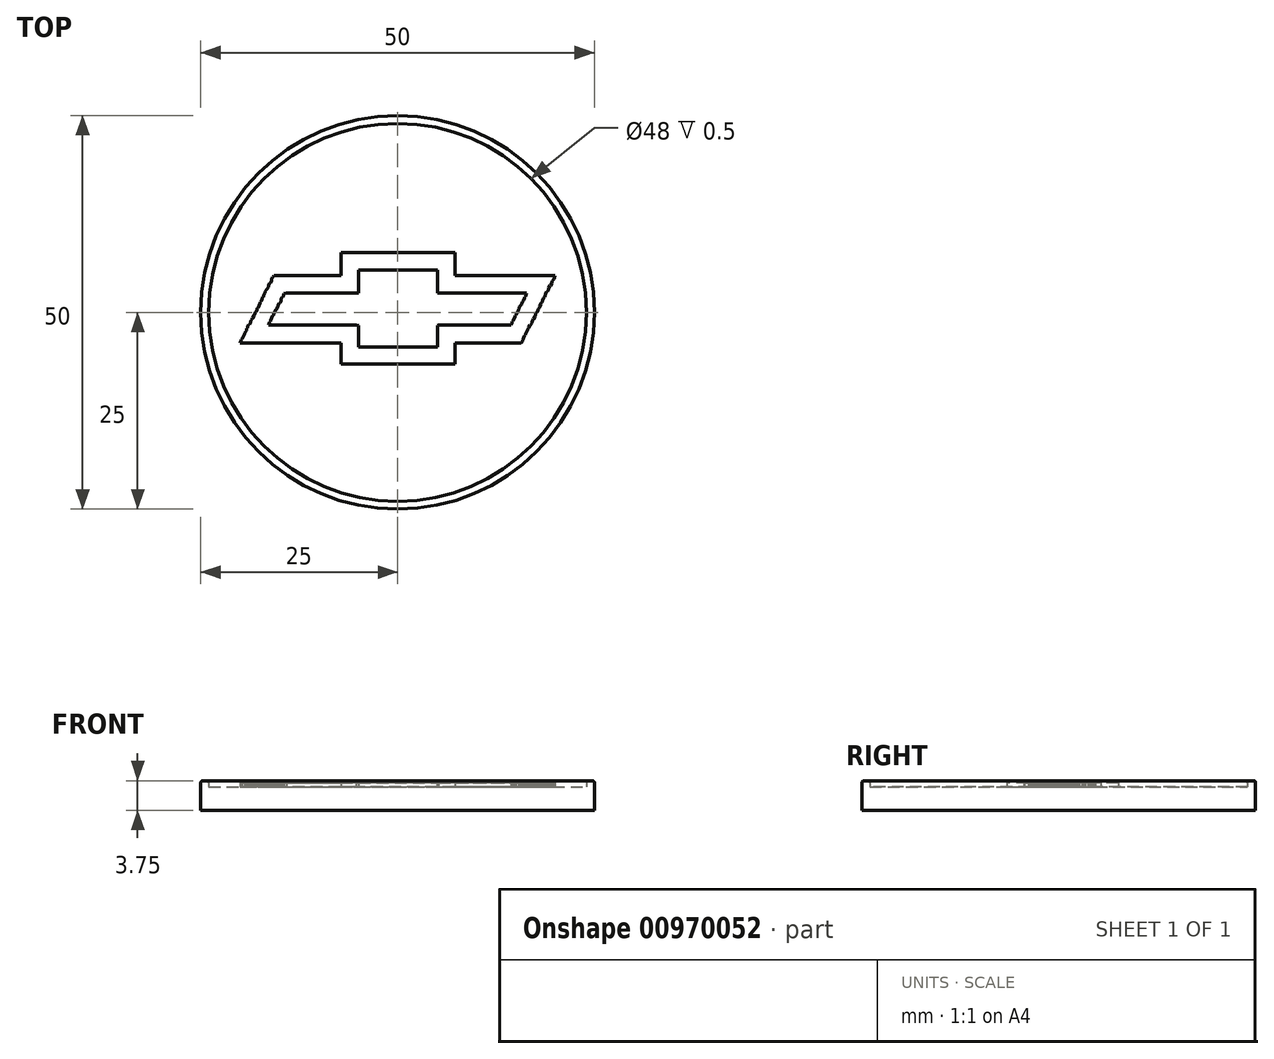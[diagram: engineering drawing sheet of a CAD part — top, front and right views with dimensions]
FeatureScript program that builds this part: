
annotation { "Feature Type Name" : "Feature", "Feature Type Description" : "" }
export const myFeature = defineFeature(function(context is Context, id is Id, definition is map)
    precondition{}
    {
        {
            var Q0;
            Q0=qCreatedBy(makeId("Front.planeOp"),FACE);
            var sketch = newSketch(context, id + "F0", { "sketchPlane" : qUnion([Q0])});
            skLineSegment(sketch, "E0.bottom", {"start": v(0, 0) * mm, "end": v(-25, 0) * mm});
            skLineSegment(sketch, "E0.top", {"start": v(0, 3) * mm, "end": v(-25, 3) * mm});
            skLineSegment(sketch, "E0.left", {"start": v(0, 0) * mm, "end": v(0, 3) * mm});
            skLineSegment(sketch, "E0.right", {"start": v(-25, 0) * mm, "end": v(-25, 3) * mm});
            skLineSegment(sketch, "E1.bottom", {"start": v(-25, 3) * mm, "end": v(-24, 3) * mm});
            skLineSegment(sketch, "E1.top", {"start": v(-25, 3.75) * mm, "end": v(-24, 3.75) * mm});
            skLineSegment(sketch, "E1.left", {"start": v(-25, 3) * mm, "end": v(-25, 3.75) * mm});
            skLineSegment(sketch, "E1.right", {"start": v(-24, 3) * mm, "end": v(-24, 3.75) * mm});
            skSolve(sketch);
        }
        {
            var Q0;
            Q0 = qSketchRegion(id + "F0", true);
            var Q1;
            Q1=sQuery(id+"F0.wireOp",EDGE,"E0.left");
            revolve(context, id + "F1", {"surfaceOperationType" : NewSurfaceOperationType.NEW, "entities" : qUnion([Q0]), "axis" : qUnion([Q1]), "revolveType" : RevolveType.FULL});
        }
        {
            var Q0;
            Q0=qCreatedBy(makeId("Top.planeOp"),FACE);
            cPlane(context, id + "F2", {"entities" : qUnion([Q0]), "cplaneType" : CPlaneType.OFFSET, "offset" : 3 * mm, "width" : 150 * mm, "height" : 150 * mm});
        }
        {
            var Q0;
            Q0=qCreatedBy(id+"F2.planeOp",FACE);
            var sketch = newSketch(context, id + "F3", { "sketchPlane" : qUnion([Q0])});
            skLineSegment(sketch, "E2", {"start": v(-7.2, 7.58) * mm, "end": v(-7.2, 7.38) * mm});
            skLineSegment(sketch, "E3", {"start": v(-7.2, 7.38) * mm, "end": v(-7.2, 7.33) * mm});
            skLineSegment(sketch, "E4", {"start": v(-7.2, 7.33) * mm, "end": v(-7.2, 7.28) * mm});
            skLineSegment(sketch, "E5", {"start": v(-7.2, 7.28) * mm, "end": v(-7.2, 7.23) * mm});
            skLineSegment(sketch, "E6", {"start": v(-7.2, 7.23) * mm, "end": v(-7.2, 7.18) * mm});
            skLineSegment(sketch, "E7", {"start": v(-7.2, 7.18) * mm, "end": v(-7.2, 7.12) * mm});
            skLineSegment(sketch, "E8", {"start": v(-7.2, 7.12) * mm, "end": v(-7.2, 7.08) * mm});
            skLineSegment(sketch, "E9", {"start": v(-7.2, 7.08) * mm, "end": v(-7.2, 7.03) * mm});
            skLineSegment(sketch, "E10", {"start": v(-7.2, 7.03) * mm, "end": v(-7.2, 6.98) * mm});
            skLineSegment(sketch, "E11", {"start": v(-7.2, 6.98) * mm, "end": v(-7.2, 6.93) * mm});
            skLineSegment(sketch, "E12", {"start": v(-7.2, 6.93) * mm, "end": v(-7.2, 6.88) * mm});
            skLineSegment(sketch, "E13", {"start": v(-7.2, 6.88) * mm, "end": v(-7.2, 6.83) * mm});
            skLineSegment(sketch, "E14", {"start": v(-7.2, 6.83) * mm, "end": v(-7.2, 6.77) * mm});
            skLineSegment(sketch, "E15", {"start": v(-7.2, 6.77) * mm, "end": v(-7.2, 6.72) * mm});
            skLineSegment(sketch, "E16", {"start": v(-7.2, 6.72) * mm, "end": v(-7.2, 6.68) * mm});
            skLineSegment(sketch, "E17", {"start": v(-7.2, 6.68) * mm, "end": v(-7.2, 6.62) * mm});
            skLineSegment(sketch, "E18", {"start": v(-7.2, 6.62) * mm, "end": v(-7.2, 6.58) * mm});
            skLineSegment(sketch, "E19", {"start": v(-7.2, 6.58) * mm, "end": v(-7.2, 6.52) * mm});
            skLineSegment(sketch, "E20", {"start": v(-7.2, 6.52) * mm, "end": v(-7.2, 6.47) * mm});
            skLineSegment(sketch, "E21", {"start": v(-7.2, 6.47) * mm, "end": v(-7.2, 6.42) * mm});
            skLineSegment(sketch, "E22", {"start": v(-7.2, 6.42) * mm, "end": v(-7.2, 6.38) * mm});
            skLineSegment(sketch, "E23", {"start": v(-7.2, 6.38) * mm, "end": v(-7.2, 6.33) * mm});
            skLineSegment(sketch, "E24", {"start": v(-7.2, 6.33) * mm, "end": v(-7.2, 6.28) * mm});
            skLineSegment(sketch, "E25", {"start": v(-7.2, 6.28) * mm, "end": v(-7.2, 6.23) * mm});
            skLineSegment(sketch, "E26", {"start": v(-7.2, 6.23) * mm, "end": v(-7.2, 6.17) * mm});
            skLineSegment(sketch, "E27", {"start": v(-7.2, 6.17) * mm, "end": v(-7.2, 6.12) * mm});
            skLineSegment(sketch, "E28", {"start": v(-7.2, 6.12) * mm, "end": v(-7.2, 6.08) * mm});
            skLineSegment(sketch, "E29", {"start": v(-7.2, 6.08) * mm, "end": v(-7.2, 6.03) * mm});
            skLineSegment(sketch, "E30", {"start": v(-7.2, 6.03) * mm, "end": v(-7.2, 5.98) * mm});
            skLineSegment(sketch, "E31", {"start": v(-7.2, 5.98) * mm, "end": v(-7.2, 5.92) * mm});
            skLineSegment(sketch, "E32", {"start": v(-7.2, 5.92) * mm, "end": v(-7.2, 5.88) * mm});
            skLineSegment(sketch, "E33", {"start": v(-7.2, 5.88) * mm, "end": v(-7.2, 5.83) * mm});
            skLineSegment(sketch, "E34", {"start": v(-7.2, 5.83) * mm, "end": v(-7.2, 5.77) * mm});
            skLineSegment(sketch, "E35", {"start": v(-7.2, 5.77) * mm, "end": v(-7.2, 5.72) * mm});
            skLineSegment(sketch, "E36", {"start": v(-7.2, 5.72) * mm, "end": v(-7.2, 5.68) * mm});
            skLineSegment(sketch, "E37", {"start": v(-7.2, 5.68) * mm, "end": v(-7.2, 5.63) * mm});
            skLineSegment(sketch, "E38", {"start": v(-7.2, 5.63) * mm, "end": v(-7.2, 5.58) * mm});
            skLineSegment(sketch, "E39", {"start": v(-7.2, 5.58) * mm, "end": v(-7.2, 5.53) * mm});
            skLineSegment(sketch, "E40", {"start": v(-7.2, 5.53) * mm, "end": v(-7.2, 5.48) * mm});
            skLineSegment(sketch, "E41", {"start": v(-7.2, 5.48) * mm, "end": v(-7.2, 5.42) * mm});
            skLineSegment(sketch, "E42", {"start": v(-7.2, 5.42) * mm, "end": v(-7.2, 5.38) * mm});
            skLineSegment(sketch, "E43", {"start": v(-7.2, 5.38) * mm, "end": v(-7.2, 5.33) * mm});
            skLineSegment(sketch, "E44", {"start": v(-7.2, 5.33) * mm, "end": v(-7.2, 5.28) * mm});
            skLineSegment(sketch, "E45", {"start": v(-7.2, 5.28) * mm, "end": v(-7.2, 5.23) * mm});
            skLineSegment(sketch, "E46", {"start": v(-7.2, 5.23) * mm, "end": v(-7.2, 5.17) * mm});
            skLineSegment(sketch, "E47", {"start": v(-7.2, 5.17) * mm, "end": v(-7.2, 5.12) * mm});
            skLineSegment(sketch, "E48", {"start": v(-7.2, 5.12) * mm, "end": v(-7.2, 5.08) * mm});
            skLineSegment(sketch, "E49", {"start": v(-7.2, 5.08) * mm, "end": v(-7.2, 5.03) * mm});
            skLineSegment(sketch, "E50", {"start": v(-7.2, 5.03) * mm, "end": v(-7.2, 4.68) * mm});
            skLineSegment(sketch, "E51", {"start": v(-7.2, 4.68) * mm, "end": v(-7.4, 4.68) * mm});
            skLineSegment(sketch, "E52", {"start": v(-7.4, 4.68) * mm, "end": v(-7.45, 4.68) * mm});
            skLineSegment(sketch, "E53", {"start": v(-7.45, 4.68) * mm, "end": v(-7.5, 4.68) * mm});
            skLineSegment(sketch, "E54", {"start": v(-7.5, 4.68) * mm, "end": v(-7.55, 4.68) * mm});
            skLineSegment(sketch, "E55", {"start": v(-7.55, 4.68) * mm, "end": v(-7.6, 4.68) * mm});
            skLineSegment(sketch, "E56", {"start": v(-7.6, 4.68) * mm, "end": v(-7.65, 4.68) * mm});
            skLineSegment(sketch, "E57", {"start": v(-7.65, 4.68) * mm, "end": v(-7.7, 4.68) * mm});
            skLineSegment(sketch, "E58", {"start": v(-7.7, 4.68) * mm, "end": v(-7.75, 4.68) * mm});
            skLineSegment(sketch, "E59", {"start": v(-7.75, 4.68) * mm, "end": v(-7.8, 4.68) * mm});
            skLineSegment(sketch, "E60", {"start": v(-7.8, 4.68) * mm, "end": v(-7.85, 4.68) * mm});
            skLineSegment(sketch, "E61", {"start": v(-7.85, 4.68) * mm, "end": v(-7.9, 4.68) * mm});
            skLineSegment(sketch, "E62", {"start": v(-7.9, 4.68) * mm, "end": v(-7.95, 4.68) * mm});
            skLineSegment(sketch, "E63", {"start": v(-7.95, 4.68) * mm, "end": v(-8, 4.68) * mm});
            skLineSegment(sketch, "E64", {"start": v(-8, 4.68) * mm, "end": v(-8.05, 4.68) * mm});
            skLineSegment(sketch, "E65", {"start": v(-8.05, 4.68) * mm, "end": v(-8.1, 4.68) * mm});
            skLineSegment(sketch, "E66", {"start": v(-8.1, 4.68) * mm, "end": v(-8.15, 4.68) * mm});
            skLineSegment(sketch, "E67", {"start": v(-8.15, 4.68) * mm, "end": v(-8.2, 4.68) * mm});
            skLineSegment(sketch, "E68", {"start": v(-8.2, 4.68) * mm, "end": v(-8.25, 4.68) * mm});
            skLineSegment(sketch, "E69", {"start": v(-8.25, 4.68) * mm, "end": v(-8.3, 4.68) * mm});
            skLineSegment(sketch, "E70", {"start": v(-8.3, 4.68) * mm, "end": v(-8.35, 4.68) * mm});
            skLineSegment(sketch, "E71", {"start": v(-8.35, 4.68) * mm, "end": v(-8.4, 4.68) * mm});
            skLineSegment(sketch, "E72", {"start": v(-8.4, 4.68) * mm, "end": v(-8.45, 4.68) * mm});
            skLineSegment(sketch, "E73", {"start": v(-8.45, 4.68) * mm, "end": v(-8.5, 4.68) * mm});
            skLineSegment(sketch, "E74", {"start": v(-8.5, 4.68) * mm, "end": v(-8.55, 4.68) * mm});
            skLineSegment(sketch, "E75", {"start": v(-8.55, 4.68) * mm, "end": v(-8.6, 4.68) * mm});
            skLineSegment(sketch, "E76", {"start": v(-8.6, 4.68) * mm, "end": v(-8.65, 4.68) * mm});
            skLineSegment(sketch, "E77", {"start": v(-8.65, 4.68) * mm, "end": v(-8.7, 4.68) * mm});
            skLineSegment(sketch, "E78", {"start": v(-8.7, 4.68) * mm, "end": v(-8.75, 4.68) * mm});
            skLineSegment(sketch, "E79", {"start": v(-8.75, 4.68) * mm, "end": v(-8.8, 4.68) * mm});
            skLineSegment(sketch, "E80", {"start": v(-8.8, 4.68) * mm, "end": v(-8.85, 4.68) * mm});
            skLineSegment(sketch, "E81", {"start": v(-8.85, 4.68) * mm, "end": v(-8.9, 4.68) * mm});
            skLineSegment(sketch, "E82", {"start": v(-8.9, 4.68) * mm, "end": v(-8.95, 4.68) * mm});
            skLineSegment(sketch, "E83", {"start": v(-8.95, 4.68) * mm, "end": v(-9, 4.68) * mm});
            skLineSegment(sketch, "E84", {"start": v(-9, 4.68) * mm, "end": v(-9.05, 4.68) * mm});
            skLineSegment(sketch, "E85", {"start": v(-9.05, 4.68) * mm, "end": v(-9.1, 4.68) * mm});
            skLineSegment(sketch, "E86", {"start": v(-9.1, 4.68) * mm, "end": v(-9.15, 4.68) * mm});
            skLineSegment(sketch, "E87", {"start": v(-9.15, 4.68) * mm, "end": v(-9.2, 4.68) * mm});
            skLineSegment(sketch, "E88", {"start": v(-9.2, 4.68) * mm, "end": v(-9.25, 4.68) * mm});
            skLineSegment(sketch, "E89", {"start": v(-9.25, 4.68) * mm, "end": v(-9.3, 4.68) * mm});
            skLineSegment(sketch, "E90", {"start": v(-9.3, 4.68) * mm, "end": v(-9.35, 4.68) * mm});
            skLineSegment(sketch, "E91", {"start": v(-9.35, 4.68) * mm, "end": v(-9.4, 4.68) * mm});
            skLineSegment(sketch, "E92", {"start": v(-9.4, 4.68) * mm, "end": v(-9.45, 4.68) * mm});
            skLineSegment(sketch, "E93", {"start": v(-9.45, 4.68) * mm, "end": v(-9.5, 4.68) * mm});
            skLineSegment(sketch, "E94", {"start": v(-9.5, 4.68) * mm, "end": v(-9.55, 4.68) * mm});
            skLineSegment(sketch, "E95", {"start": v(-9.55, 4.68) * mm, "end": v(-9.6, 4.68) * mm});
            skLineSegment(sketch, "E96", {"start": v(-9.6, 4.68) * mm, "end": v(-9.65, 4.68) * mm});
            skLineSegment(sketch, "E97", {"start": v(-9.65, 4.68) * mm, "end": v(-9.7, 4.68) * mm});
            skLineSegment(sketch, "E98", {"start": v(-9.7, 4.68) * mm, "end": v(-9.75, 4.68) * mm});
            skLineSegment(sketch, "E99", {"start": v(-9.75, 4.68) * mm, "end": v(-9.8, 4.68) * mm});
            skLineSegment(sketch, "E100", {"start": v(-9.8, 4.68) * mm, "end": v(-9.85, 4.68) * mm});
            skLineSegment(sketch, "E101", {"start": v(-9.85, 4.68) * mm, "end": v(-9.9, 4.68) * mm});
            skLineSegment(sketch, "E102", {"start": v(-9.9, 4.68) * mm, "end": v(-9.95, 4.68) * mm});
            skLineSegment(sketch, "E103", {"start": v(-9.95, 4.68) * mm, "end": v(-10, 4.68) * mm});
            skLineSegment(sketch, "E104", {"start": v(-10, 4.68) * mm, "end": v(-10.05, 4.68) * mm});
            skLineSegment(sketch, "E105", {"start": v(-10.05, 4.68) * mm, "end": v(-10.1, 4.68) * mm});
            skLineSegment(sketch, "E106", {"start": v(-10.1, 4.68) * mm, "end": v(-10.15, 4.68) * mm});
            skLineSegment(sketch, "E107", {"start": v(-10.15, 4.68) * mm, "end": v(-10.2, 4.68) * mm});
            skLineSegment(sketch, "E108", {"start": v(-10.2, 4.68) * mm, "end": v(-10.25, 4.68) * mm});
            skLineSegment(sketch, "E109", {"start": v(-10.25, 4.68) * mm, "end": v(-10.3, 4.68) * mm});
            skLineSegment(sketch, "E110", {"start": v(-10.3, 4.68) * mm, "end": v(-10.35, 4.68) * mm});
            skLineSegment(sketch, "E111", {"start": v(-10.35, 4.68) * mm, "end": v(-10.4, 4.68) * mm});
            skLineSegment(sketch, "E112", {"start": v(-10.4, 4.68) * mm, "end": v(-10.45, 4.68) * mm});
            skLineSegment(sketch, "E113", {"start": v(-10.45, 4.68) * mm, "end": v(-10.5, 4.68) * mm});
            skLineSegment(sketch, "E114", {"start": v(-10.5, 4.68) * mm, "end": v(-10.55, 4.68) * mm});
            skLineSegment(sketch, "E115", {"start": v(-10.55, 4.68) * mm, "end": v(-10.6, 4.68) * mm});
            skLineSegment(sketch, "E116", {"start": v(-10.6, 4.68) * mm, "end": v(-10.65, 4.68) * mm});
            skLineSegment(sketch, "E117", {"start": v(-10.65, 4.68) * mm, "end": v(-10.7, 4.68) * mm});
            skLineSegment(sketch, "E118", {"start": v(-10.7, 4.68) * mm, "end": v(-10.75, 4.68) * mm});
            skLineSegment(sketch, "E119", {"start": v(-10.75, 4.68) * mm, "end": v(-10.8, 4.68) * mm});
            skLineSegment(sketch, "E120", {"start": v(-10.8, 4.68) * mm, "end": v(-10.85, 4.68) * mm});
            skLineSegment(sketch, "E121", {"start": v(-10.85, 4.68) * mm, "end": v(-10.9, 4.68) * mm});
            skLineSegment(sketch, "E122", {"start": v(-10.9, 4.68) * mm, "end": v(-10.95, 4.68) * mm});
            skLineSegment(sketch, "E123", {"start": v(-10.95, 4.68) * mm, "end": v(-11, 4.68) * mm});
            skLineSegment(sketch, "E124", {"start": v(-11, 4.68) * mm, "end": v(-11.05, 4.68) * mm});
            skLineSegment(sketch, "E125", {"start": v(-11.05, 4.68) * mm, "end": v(-11.1, 4.68) * mm});
            skLineSegment(sketch, "E126", {"start": v(-11.1, 4.68) * mm, "end": v(-11.15, 4.68) * mm});
            skLineSegment(sketch, "E127", {"start": v(-11.15, 4.68) * mm, "end": v(-11.2, 4.68) * mm});
            skLineSegment(sketch, "E128", {"start": v(-11.2, 4.68) * mm, "end": v(-11.25, 4.68) * mm});
            skLineSegment(sketch, "E129", {"start": v(-11.25, 4.68) * mm, "end": v(-11.3, 4.68) * mm});
            skLineSegment(sketch, "E130", {"start": v(-11.3, 4.68) * mm, "end": v(-11.35, 4.68) * mm});
            skLineSegment(sketch, "E131", {"start": v(-11.35, 4.68) * mm, "end": v(-11.4, 4.68) * mm});
            skLineSegment(sketch, "E132", {"start": v(-11.4, 4.68) * mm, "end": v(-11.45, 4.68) * mm});
            skLineSegment(sketch, "E133", {"start": v(-11.45, 4.68) * mm, "end": v(-11.5, 4.68) * mm});
            skLineSegment(sketch, "E134", {"start": v(-11.5, 4.68) * mm, "end": v(-11.55, 4.68) * mm});
            skLineSegment(sketch, "E135", {"start": v(-11.55, 4.68) * mm, "end": v(-11.6, 4.68) * mm});
            skLineSegment(sketch, "E136", {"start": v(-11.6, 4.68) * mm, "end": v(-11.65, 4.68) * mm});
            skLineSegment(sketch, "E137", {"start": v(-11.65, 4.68) * mm, "end": v(-11.7, 4.68) * mm});
            skLineSegment(sketch, "E138", {"start": v(-11.7, 4.68) * mm, "end": v(-11.75, 4.68) * mm});
            skLineSegment(sketch, "E139", {"start": v(-11.75, 4.68) * mm, "end": v(-11.8, 4.68) * mm});
            skLineSegment(sketch, "E140", {"start": v(-11.8, 4.68) * mm, "end": v(-11.85, 4.68) * mm});
            skLineSegment(sketch, "E141", {"start": v(-11.85, 4.68) * mm, "end": v(-11.9, 4.68) * mm});
            skLineSegment(sketch, "E142", {"start": v(-11.9, 4.68) * mm, "end": v(-11.95, 4.68) * mm});
            skLineSegment(sketch, "E143", {"start": v(-11.95, 4.68) * mm, "end": v(-12, 4.68) * mm});
            skLineSegment(sketch, "E144", {"start": v(-12, 4.68) * mm, "end": v(-12.05, 4.68) * mm});
            skLineSegment(sketch, "E145", {"start": v(-12.05, 4.68) * mm, "end": v(-12.1, 4.68) * mm});
            skLineSegment(sketch, "E146", {"start": v(-12.1, 4.68) * mm, "end": v(-12.15, 4.68) * mm});
            skLineSegment(sketch, "E147", {"start": v(-12.15, 4.68) * mm, "end": v(-12.2, 4.68) * mm});
            skLineSegment(sketch, "E148", {"start": v(-12.2, 4.68) * mm, "end": v(-12.25, 4.68) * mm});
            skLineSegment(sketch, "E149", {"start": v(-12.25, 4.68) * mm, "end": v(-12.3, 4.68) * mm});
            skLineSegment(sketch, "E150", {"start": v(-12.3, 4.68) * mm, "end": v(-12.35, 4.68) * mm});
            skLineSegment(sketch, "E151", {"start": v(-12.35, 4.68) * mm, "end": v(-12.4, 4.68) * mm});
            skLineSegment(sketch, "E152", {"start": v(-12.4, 4.68) * mm, "end": v(-12.45, 4.68) * mm});
            skLineSegment(sketch, "E153", {"start": v(-12.45, 4.68) * mm, "end": v(-12.5, 4.68) * mm});
            skLineSegment(sketch, "E154", {"start": v(-12.5, 4.68) * mm, "end": v(-12.55, 4.68) * mm});
            skLineSegment(sketch, "E155", {"start": v(-12.55, 4.68) * mm, "end": v(-12.6, 4.68) * mm});
            skLineSegment(sketch, "E156", {"start": v(-12.6, 4.68) * mm, "end": v(-12.65, 4.68) * mm});
            skLineSegment(sketch, "E157", {"start": v(-12.65, 4.68) * mm, "end": v(-12.7, 4.68) * mm});
            skLineSegment(sketch, "E158", {"start": v(-12.7, 4.68) * mm, "end": v(-12.75, 4.68) * mm});
            skLineSegment(sketch, "E159", {"start": v(-12.75, 4.68) * mm, "end": v(-12.8, 4.68) * mm});
            skLineSegment(sketch, "E160", {"start": v(-12.8, 4.68) * mm, "end": v(-12.85, 4.68) * mm});
            skLineSegment(sketch, "E161", {"start": v(-12.85, 4.68) * mm, "end": v(-12.9, 4.68) * mm});
            skLineSegment(sketch, "E162", {"start": v(-12.9, 4.68) * mm, "end": v(-12.95, 4.68) * mm});
            skLineSegment(sketch, "E163", {"start": v(-12.95, 4.68) * mm, "end": v(-13, 4.68) * mm});
            skLineSegment(sketch, "E164", {"start": v(-13, 4.68) * mm, "end": v(-13.05, 4.68) * mm});
            skLineSegment(sketch, "E165", {"start": v(-13.05, 4.68) * mm, "end": v(-13.1, 4.68) * mm});
            skLineSegment(sketch, "E166", {"start": v(-13.1, 4.68) * mm, "end": v(-13.15, 4.68) * mm});
            skLineSegment(sketch, "E167", {"start": v(-13.15, 4.68) * mm, "end": v(-13.2, 4.68) * mm});
            skLineSegment(sketch, "E168", {"start": v(-13.2, 4.68) * mm, "end": v(-13.25, 4.68) * mm});
            skLineSegment(sketch, "E169", {"start": v(-13.25, 4.68) * mm, "end": v(-13.3, 4.68) * mm});
            skLineSegment(sketch, "E170", {"start": v(-13.3, 4.68) * mm, "end": v(-13.35, 4.68) * mm});
            skLineSegment(sketch, "E171", {"start": v(-13.35, 4.68) * mm, "end": v(-13.4, 4.68) * mm});
            skLineSegment(sketch, "E172", {"start": v(-13.4, 4.68) * mm, "end": v(-13.45, 4.68) * mm});
            skLineSegment(sketch, "E173", {"start": v(-13.45, 4.68) * mm, "end": v(-13.5, 4.68) * mm});
            skLineSegment(sketch, "E174", {"start": v(-13.5, 4.68) * mm, "end": v(-13.55, 4.68) * mm});
            skLineSegment(sketch, "E175", {"start": v(-13.55, 4.68) * mm, "end": v(-13.6, 4.68) * mm});
            skLineSegment(sketch, "E176", {"start": v(-13.6, 4.68) * mm, "end": v(-13.65, 4.68) * mm});
            skLineSegment(sketch, "E177", {"start": v(-13.65, 4.68) * mm, "end": v(-13.7, 4.68) * mm});
            skLineSegment(sketch, "E178", {"start": v(-13.7, 4.68) * mm, "end": v(-13.75, 4.68) * mm});
            skLineSegment(sketch, "E179", {"start": v(-13.75, 4.68) * mm, "end": v(-13.8, 4.68) * mm});
            skLineSegment(sketch, "E180", {"start": v(-13.8, 4.68) * mm, "end": v(-13.85, 4.68) * mm});
            skLineSegment(sketch, "E181", {"start": v(-13.85, 4.68) * mm, "end": v(-13.9, 4.68) * mm});
            skLineSegment(sketch, "E182", {"start": v(-13.9, 4.68) * mm, "end": v(-13.95, 4.68) * mm});
            skLineSegment(sketch, "E183", {"start": v(-13.95, 4.68) * mm, "end": v(-14, 4.68) * mm});
            skLineSegment(sketch, "E184", {"start": v(-14, 4.68) * mm, "end": v(-14.05, 4.68) * mm});
            skLineSegment(sketch, "E185", {"start": v(-14.05, 4.68) * mm, "end": v(-14.1, 4.68) * mm});
            skLineSegment(sketch, "E186", {"start": v(-14.1, 4.68) * mm, "end": v(-14.15, 4.68) * mm});
            skLineSegment(sketch, "E187", {"start": v(-14.15, 4.68) * mm, "end": v(-14.2, 4.68) * mm});
            skLineSegment(sketch, "E188", {"start": v(-14.2, 4.68) * mm, "end": v(-14.25, 4.68) * mm});
            skLineSegment(sketch, "E189", {"start": v(-14.25, 4.68) * mm, "end": v(-14.3, 4.68) * mm});
            skLineSegment(sketch, "E190", {"start": v(-14.3, 4.68) * mm, "end": v(-14.35, 4.68) * mm});
            skLineSegment(sketch, "E191", {"start": v(-14.35, 4.68) * mm, "end": v(-14.4, 4.68) * mm});
            skLineSegment(sketch, "E192", {"start": v(-14.4, 4.68) * mm, "end": v(-14.45, 4.68) * mm});
            skLineSegment(sketch, "E193", {"start": v(-14.45, 4.68) * mm, "end": v(-14.5, 4.68) * mm});
            skLineSegment(sketch, "E194", {"start": v(-14.5, 4.68) * mm, "end": v(-14.55, 4.68) * mm});
            skLineSegment(sketch, "E195", {"start": v(-14.55, 4.68) * mm, "end": v(-14.6, 4.68) * mm});
            skLineSegment(sketch, "E196", {"start": v(-14.6, 4.68) * mm, "end": v(-14.65, 4.68) * mm});
            skLineSegment(sketch, "E197", {"start": v(-14.65, 4.68) * mm, "end": v(-14.7, 4.68) * mm});
            skLineSegment(sketch, "E198", {"start": v(-14.7, 4.68) * mm, "end": v(-14.75, 4.68) * mm});
            skLineSegment(sketch, "E199", {"start": v(-14.75, 4.68) * mm, "end": v(-14.8, 4.68) * mm});
            skLineSegment(sketch, "E200", {"start": v(-14.8, 4.68) * mm, "end": v(-14.85, 4.68) * mm});
            skLineSegment(sketch, "E201", {"start": v(-14.85, 4.68) * mm, "end": v(-14.9, 4.68) * mm});
            skLineSegment(sketch, "E202", {"start": v(-14.9, 4.68) * mm, "end": v(-14.95, 4.68) * mm});
            skLineSegment(sketch, "E203", {"start": v(-14.95, 4.68) * mm, "end": v(-15, 4.68) * mm});
            skLineSegment(sketch, "E204", {"start": v(-15, 4.68) * mm, "end": v(-15.05, 4.68) * mm});
            skLineSegment(sketch, "E205", {"start": v(-15.05, 4.68) * mm, "end": v(-15.1, 4.68) * mm});
            skLineSegment(sketch, "E206", {"start": v(-15.1, 4.68) * mm, "end": v(-15.15, 4.68) * mm});
            skLineSegment(sketch, "E207", {"start": v(-15.15, 4.68) * mm, "end": v(-15.2, 4.68) * mm});
            skLineSegment(sketch, "E208", {"start": v(-15.2, 4.68) * mm, "end": v(-15.25, 4.68) * mm});
            skLineSegment(sketch, "E209", {"start": v(-15.25, 4.68) * mm, "end": v(-15.3, 4.68) * mm});
            skLineSegment(sketch, "E210", {"start": v(-15.3, 4.68) * mm, "end": v(-15.35, 4.68) * mm});
            skLineSegment(sketch, "E211", {"start": v(-15.35, 4.68) * mm, "end": v(-15.7, 4.68) * mm});
            skLineSegment(sketch, "E212", {"start": v(-15.7, 4.68) * mm, "end": v(-15.75, 4.52) * mm});
            skLineSegment(sketch, "E213", {"start": v(-15.75, 4.53) * mm, "end": v(-15.85, 4.48) * mm});
            skLineSegment(sketch, "E214", {"start": v(-15.85, 4.48) * mm, "end": v(-16, 4.22) * mm});
            skLineSegment(sketch, "E215", {"start": v(-16, 4.22) * mm, "end": v(-16, 4.03) * mm});
            skLineSegment(sketch, "E216", {"start": v(-16, 4.03) * mm, "end": v(-16.15, 3.73) * mm});
            skLineSegment(sketch, "E217", {"start": v(-16.15, 3.73) * mm, "end": v(-16.25, 3.73) * mm});
            skLineSegment(sketch, "E218", {"start": v(-16.25, 3.73) * mm, "end": v(-16.4, 3.43) * mm});
            skLineSegment(sketch, "E219", {"start": v(-16.4, 3.43) * mm, "end": v(-16.4, 3.23) * mm});
            skLineSegment(sketch, "E220", {"start": v(-16.4, 3.23) * mm, "end": v(-16.65, 2.93) * mm});
            skLineSegment(sketch, "E221", {"start": v(-16.65, 2.93) * mm, "end": v(-16.8, 2.62) * mm});
            skLineSegment(sketch, "E222", {"start": v(-16.8, 2.63) * mm, "end": v(-16.8, 2.48) * mm});
            skLineSegment(sketch, "E223", {"start": v(-16.8, 2.48) * mm, "end": v(-16.9, 2.43) * mm});
            skLineSegment(sketch, "E224", {"start": v(-16.9, 2.43) * mm, "end": v(-17.05, 2.12) * mm});
            skLineSegment(sketch, "E225", {"start": v(-17.05, 2.13) * mm, "end": v(-17.05, 1.98) * mm});
            skLineSegment(sketch, "E226", {"start": v(-17.05, 1.98) * mm, "end": v(-17.15, 1.93) * mm});
            skLineSegment(sketch, "E227", {"start": v(-17.15, 1.93) * mm, "end": v(-17.2, 1.67) * mm});
            skLineSegment(sketch, "E228", {"start": v(-17.2, 1.68) * mm, "end": v(-17.35, 1.38) * mm});
            skLineSegment(sketch, "E229", {"start": v(-17.35, 1.38) * mm, "end": v(-17.45, 1.33) * mm});
            skLineSegment(sketch, "E230", {"start": v(-17.45, 1.33) * mm, "end": v(-17.45, 1.18) * mm});
            skLineSegment(sketch, "E231", {"start": v(-17.45, 1.18) * mm, "end": v(-17.6, 0.88) * mm});
            skLineSegment(sketch, "E232", {"start": v(-17.6, 0.88) * mm, "end": v(-17.75, 0.57) * mm});
            skLineSegment(sketch, "E233", {"start": v(-17.75, 0.58) * mm, "end": v(-17.85, 0.53) * mm});
            skLineSegment(sketch, "E234", {"start": v(-17.85, 0.53) * mm, "end": v(-17.85, 0.38) * mm});
            skLineSegment(sketch, "E235", {"start": v(-17.85, 0.38) * mm, "end": v(-18, 0.07) * mm});
            skLineSegment(sketch, "E236", {"start": v(-18, 0.08) * mm, "end": v(-18.1, 0.08) * mm});
            skLineSegment(sketch, "E237", {"start": v(-18.1, 0.08) * mm, "end": v(-18.1, -0.07) * mm});
            skLineSegment(sketch, "E238", {"start": v(-18.1, -0.07) * mm, "end": v(-18.25, -0.43) * mm});
            skLineSegment(sketch, "E239", {"start": v(-18.25, -0.42) * mm, "end": v(-18.4, -0.73) * mm});
            skLineSegment(sketch, "E240", {"start": v(-18.4, -0.72) * mm, "end": v(-18.5, -0.72) * mm});
            skLineSegment(sketch, "E241", {"start": v(-18.5, -0.72) * mm, "end": v(-18.5, -0.87) * mm});
            skLineSegment(sketch, "E242", {"start": v(-18.5, -0.87) * mm, "end": v(-18.6, -0.97) * mm});
            skLineSegment(sketch, "E243", {"start": v(-18.6, -0.97) * mm, "end": v(-18.6, -1.07) * mm});
            skLineSegment(sketch, "E244", {"start": v(-18.6, -1.07) * mm, "end": v(-18.65, -1.07) * mm});
            skLineSegment(sketch, "E245", {"start": v(-18.65, -1.07) * mm, "end": v(-18.65, -1.17) * mm});
            skLineSegment(sketch, "E246", {"start": v(-18.65, -1.17) * mm, "end": v(-18.7, -1.17) * mm});
            skLineSegment(sketch, "E247", {"start": v(-18.7, -1.17) * mm, "end": v(-18.7, -1.27) * mm});
            skLineSegment(sketch, "E248", {"start": v(-18.7, -1.27) * mm, "end": v(-18.8, -1.52) * mm});
            skLineSegment(sketch, "E249", {"start": v(-18.8, -1.52) * mm, "end": v(-18.9, -1.52) * mm});
            skLineSegment(sketch, "E250", {"start": v(-18.9, -1.52) * mm, "end": v(-19.05, -1.82) * mm});
            skLineSegment(sketch, "E251", {"start": v(-19.05, -1.82) * mm, "end": v(-19.05, -1.97) * mm});
            skLineSegment(sketch, "E252", {"start": v(-19.05, -1.97) * mm, "end": v(-19.15, -2.03) * mm});
            skLineSegment(sketch, "E253", {"start": v(-19.15, -2.02) * mm, "end": v(-19.2, -2.32) * mm});
            skLineSegment(sketch, "E254", {"start": v(-19.2, -2.32) * mm, "end": v(-19.35, -2.57) * mm});
            skLineSegment(sketch, "E255", {"start": v(-19.35, -2.57) * mm, "end": v(-19.45, -2.62) * mm});
            skLineSegment(sketch, "E256", {"start": v(-19.45, -2.62) * mm, "end": v(-19.45, -2.77) * mm});
            skLineSegment(sketch, "E257", {"start": v(-19.45, -2.77) * mm, "end": v(-19.6, -3.07) * mm});
            skLineSegment(sketch, "E258", {"start": v(-19.6, -3.07) * mm, "end": v(-19.75, -3.37) * mm});
            skLineSegment(sketch, "E259", {"start": v(-19.75, -3.37) * mm, "end": v(-19.85, -3.42) * mm});
            skLineSegment(sketch, "E260", {"start": v(-19.85, -3.42) * mm, "end": v(-19.85, -3.57) * mm});
            skLineSegment(sketch, "E261", {"start": v(-19.85, -3.57) * mm, "end": v(-20, -3.87) * mm});
            skLineSegment(sketch, "E262", {"start": v(-20, -3.87) * mm, "end": v(-19.8, -3.87) * mm});
            skLineSegment(sketch, "E263", {"start": v(-19.8, -3.87) * mm, "end": v(-19.75, -3.87) * mm});
            skLineSegment(sketch, "E264", {"start": v(-19.75, -3.87) * mm, "end": v(-19.7, -3.87) * mm});
            skLineSegment(sketch, "E265", {"start": v(-19.7, -3.87) * mm, "end": v(-19.65, -3.87) * mm});
            skLineSegment(sketch, "E266", {"start": v(-19.65, -3.87) * mm, "end": v(-19.6, -3.87) * mm});
            skLineSegment(sketch, "E267", {"start": v(-19.6, -3.87) * mm, "end": v(-19.55, -3.87) * mm});
            skLineSegment(sketch, "E268", {"start": v(-19.55, -3.87) * mm, "end": v(-19.5, -3.87) * mm});
            skLineSegment(sketch, "E269", {"start": v(-19.5, -3.87) * mm, "end": v(-19.45, -3.87) * mm});
            skLineSegment(sketch, "E270", {"start": v(-19.45, -3.87) * mm, "end": v(-19.4, -3.87) * mm});
            skLineSegment(sketch, "E271", {"start": v(-19.4, -3.87) * mm, "end": v(-19.35, -3.87) * mm});
            skLineSegment(sketch, "E272", {"start": v(-19.35, -3.87) * mm, "end": v(-19.3, -3.87) * mm});
            skLineSegment(sketch, "E273", {"start": v(-19.3, -3.87) * mm, "end": v(-19.25, -3.87) * mm});
            skLineSegment(sketch, "E274", {"start": v(-19.25, -3.87) * mm, "end": v(-19.2, -3.87) * mm});
            skLineSegment(sketch, "E275", {"start": v(-19.2, -3.87) * mm, "end": v(-19.15, -3.87) * mm});
            skLineSegment(sketch, "E276", {"start": v(-19.15, -3.87) * mm, "end": v(-19.1, -3.87) * mm});
            skLineSegment(sketch, "E277", {"start": v(-19.1, -3.87) * mm, "end": v(-19.05, -3.87) * mm});
            skLineSegment(sketch, "E278", {"start": v(-19.05, -3.87) * mm, "end": v(-19, -3.87) * mm});
            skLineSegment(sketch, "E279", {"start": v(-19, -3.87) * mm, "end": v(-18.95, -3.87) * mm});
            skLineSegment(sketch, "E280", {"start": v(-18.95, -3.87) * mm, "end": v(-18.9, -3.87) * mm});
            skLineSegment(sketch, "E281", {"start": v(-18.9, -3.87) * mm, "end": v(-18.85, -3.87) * mm});
            skLineSegment(sketch, "E282", {"start": v(-18.85, -3.87) * mm, "end": v(-18.8, -3.87) * mm});
            skLineSegment(sketch, "E283", {"start": v(-18.8, -3.87) * mm, "end": v(-18.75, -3.87) * mm});
            skLineSegment(sketch, "E284", {"start": v(-18.75, -3.87) * mm, "end": v(-18.7, -3.87) * mm});
            skLineSegment(sketch, "E285", {"start": v(-18.7, -3.87) * mm, "end": v(-18.65, -3.87) * mm});
            skLineSegment(sketch, "E286", {"start": v(-18.65, -3.87) * mm, "end": v(-18.6, -3.87) * mm});
            skLineSegment(sketch, "E287", {"start": v(-18.6, -3.87) * mm, "end": v(-18.55, -3.87) * mm});
            skLineSegment(sketch, "E288", {"start": v(-18.55, -3.87) * mm, "end": v(-18.5, -3.87) * mm});
            skLineSegment(sketch, "E289", {"start": v(-18.5, -3.87) * mm, "end": v(-18.45, -3.87) * mm});
            skLineSegment(sketch, "E290", {"start": v(-18.45, -3.87) * mm, "end": v(-18.4, -3.87) * mm});
            skLineSegment(sketch, "E291", {"start": v(-18.4, -3.87) * mm, "end": v(-18.35, -3.87) * mm});
            skLineSegment(sketch, "E292", {"start": v(-18.35, -3.87) * mm, "end": v(-18.3, -3.87) * mm});
            skLineSegment(sketch, "E293", {"start": v(-18.3, -3.87) * mm, "end": v(-18.25, -3.87) * mm});
            skLineSegment(sketch, "E294", {"start": v(-18.25, -3.87) * mm, "end": v(-18.2, -3.87) * mm});
            skLineSegment(sketch, "E295", {"start": v(-18.2, -3.87) * mm, "end": v(-18.15, -3.87) * mm});
            skLineSegment(sketch, "E296", {"start": v(-18.15, -3.87) * mm, "end": v(-18.1, -3.87) * mm});
            skLineSegment(sketch, "E297", {"start": v(-18.1, -3.87) * mm, "end": v(-18.05, -3.87) * mm});
            skLineSegment(sketch, "E298", {"start": v(-18.05, -3.87) * mm, "end": v(-18, -3.87) * mm});
            skLineSegment(sketch, "E299", {"start": v(-18, -3.87) * mm, "end": v(-17.95, -3.87) * mm});
            skLineSegment(sketch, "E300", {"start": v(-17.95, -3.87) * mm, "end": v(-17.9, -3.87) * mm});
            skLineSegment(sketch, "E301", {"start": v(-17.9, -3.87) * mm, "end": v(-17.85, -3.87) * mm});
            skLineSegment(sketch, "E302", {"start": v(-17.85, -3.87) * mm, "end": v(-17.8, -3.87) * mm});
            skLineSegment(sketch, "E303", {"start": v(-17.8, -3.87) * mm, "end": v(-17.75, -3.87) * mm});
            skLineSegment(sketch, "E304", {"start": v(-17.75, -3.87) * mm, "end": v(-17.7, -3.87) * mm});
            skLineSegment(sketch, "E305", {"start": v(-17.7, -3.87) * mm, "end": v(-17.65, -3.87) * mm});
            skLineSegment(sketch, "E306", {"start": v(-17.65, -3.87) * mm, "end": v(-17.6, -3.87) * mm});
            skLineSegment(sketch, "E307", {"start": v(-17.6, -3.87) * mm, "end": v(-17.55, -3.87) * mm});
            skLineSegment(sketch, "E308", {"start": v(-17.55, -3.87) * mm, "end": v(-17.5, -3.87) * mm});
            skLineSegment(sketch, "E309", {"start": v(-17.5, -3.87) * mm, "end": v(-17.45, -3.87) * mm});
            skLineSegment(sketch, "E310", {"start": v(-17.45, -3.87) * mm, "end": v(-17.4, -3.87) * mm});
            skLineSegment(sketch, "E311", {"start": v(-17.4, -3.87) * mm, "end": v(-17.35, -3.87) * mm});
            skLineSegment(sketch, "E312", {"start": v(-17.35, -3.87) * mm, "end": v(-17.3, -3.87) * mm});
            skLineSegment(sketch, "E313", {"start": v(-17.3, -3.87) * mm, "end": v(-17.25, -3.87) * mm});
            skLineSegment(sketch, "E314", {"start": v(-17.25, -3.87) * mm, "end": v(-17.2, -3.87) * mm});
            skLineSegment(sketch, "E315", {"start": v(-17.2, -3.87) * mm, "end": v(-17.15, -3.87) * mm});
            skLineSegment(sketch, "E316", {"start": v(-17.15, -3.87) * mm, "end": v(-17.1, -3.87) * mm});
            skLineSegment(sketch, "E317", {"start": v(-17.1, -3.87) * mm, "end": v(-17.05, -3.87) * mm});
            skLineSegment(sketch, "E318", {"start": v(-17.05, -3.87) * mm, "end": v(-17, -3.87) * mm});
            skLineSegment(sketch, "E319", {"start": v(-17, -3.87) * mm, "end": v(-16.95, -3.87) * mm});
            skLineSegment(sketch, "E320", {"start": v(-16.95, -3.87) * mm, "end": v(-16.9, -3.87) * mm});
            skLineSegment(sketch, "E321", {"start": v(-16.9, -3.87) * mm, "end": v(-16.85, -3.87) * mm});
            skLineSegment(sketch, "E322", {"start": v(-16.85, -3.87) * mm, "end": v(-16.8, -3.87) * mm});
            skLineSegment(sketch, "E323", {"start": v(-16.8, -3.87) * mm, "end": v(-16.75, -3.87) * mm});
            skLineSegment(sketch, "E324", {"start": v(-16.75, -3.87) * mm, "end": v(-16.7, -3.87) * mm});
            skLineSegment(sketch, "E325", {"start": v(-16.7, -3.87) * mm, "end": v(-16.65, -3.87) * mm});
            skLineSegment(sketch, "E326", {"start": v(-16.65, -3.87) * mm, "end": v(-16.6, -3.87) * mm});
            skLineSegment(sketch, "E327", {"start": v(-16.6, -3.87) * mm, "end": v(-16.55, -3.87) * mm});
            skLineSegment(sketch, "E328", {"start": v(-16.55, -3.87) * mm, "end": v(-16.5, -3.87) * mm});
            skLineSegment(sketch, "E329", {"start": v(-16.5, -3.87) * mm, "end": v(-16.45, -3.87) * mm});
            skLineSegment(sketch, "E330", {"start": v(-16.45, -3.87) * mm, "end": v(-16.4, -3.87) * mm});
            skLineSegment(sketch, "E331", {"start": v(-16.4, -3.87) * mm, "end": v(-16.35, -3.87) * mm});
            skLineSegment(sketch, "E332", {"start": v(-16.35, -3.87) * mm, "end": v(-16.3, -3.87) * mm});
            skLineSegment(sketch, "E333", {"start": v(-16.3, -3.87) * mm, "end": v(-16.25, -3.87) * mm});
            skLineSegment(sketch, "E334", {"start": v(-16.25, -3.87) * mm, "end": v(-16.2, -3.87) * mm});
            skLineSegment(sketch, "E335", {"start": v(-16.2, -3.87) * mm, "end": v(-16.15, -3.87) * mm});
            skLineSegment(sketch, "E336", {"start": v(-16.15, -3.87) * mm, "end": v(-16.1, -3.87) * mm});
            skLineSegment(sketch, "E337", {"start": v(-16.1, -3.87) * mm, "end": v(-16.05, -3.87) * mm});
            skLineSegment(sketch, "E338", {"start": v(-16.05, -3.87) * mm, "end": v(-16, -3.87) * mm});
            skLineSegment(sketch, "E339", {"start": v(-16, -3.87) * mm, "end": v(-15.95, -3.87) * mm});
            skLineSegment(sketch, "E340", {"start": v(-15.95, -3.87) * mm, "end": v(-15.9, -3.87) * mm});
            skLineSegment(sketch, "E341", {"start": v(-15.9, -3.87) * mm, "end": v(-15.85, -3.87) * mm});
            skLineSegment(sketch, "E342", {"start": v(-15.85, -3.87) * mm, "end": v(-15.8, -3.87) * mm});
            skLineSegment(sketch, "E343", {"start": v(-15.8, -3.87) * mm, "end": v(-15.75, -3.87) * mm});
            skLineSegment(sketch, "E344", {"start": v(-15.75, -3.87) * mm, "end": v(-15.7, -3.87) * mm});
            skLineSegment(sketch, "E345", {"start": v(-15.7, -3.87) * mm, "end": v(-15.65, -3.87) * mm});
            skLineSegment(sketch, "E346", {"start": v(-15.65, -3.87) * mm, "end": v(-15.6, -3.87) * mm});
            skLineSegment(sketch, "E347", {"start": v(-15.6, -3.87) * mm, "end": v(-15.55, -3.87) * mm});
            skLineSegment(sketch, "E348", {"start": v(-15.55, -3.87) * mm, "end": v(-15.5, -3.87) * mm});
            skLineSegment(sketch, "E349", {"start": v(-15.5, -3.87) * mm, "end": v(-15.45, -3.87) * mm});
            skLineSegment(sketch, "E350", {"start": v(-15.45, -3.87) * mm, "end": v(-15.4, -3.87) * mm});
            skLineSegment(sketch, "E351", {"start": v(-15.4, -3.87) * mm, "end": v(-15.35, -3.87) * mm});
            skLineSegment(sketch, "E352", {"start": v(-15.35, -3.87) * mm, "end": v(-15.3, -3.87) * mm});
            skLineSegment(sketch, "E353", {"start": v(-15.3, -3.87) * mm, "end": v(-15.25, -3.87) * mm});
            skLineSegment(sketch, "E354", {"start": v(-15.25, -3.87) * mm, "end": v(-15.2, -3.87) * mm});
            skLineSegment(sketch, "E355", {"start": v(-15.2, -3.87) * mm, "end": v(-15.15, -3.87) * mm});
            skLineSegment(sketch, "E356", {"start": v(-15.15, -3.87) * mm, "end": v(-15.1, -3.87) * mm});
            skLineSegment(sketch, "E357", {"start": v(-15.1, -3.87) * mm, "end": v(-15.05, -3.87) * mm});
            skLineSegment(sketch, "E358", {"start": v(-15.05, -3.87) * mm, "end": v(-15, -3.87) * mm});
            skLineSegment(sketch, "E359", {"start": v(-15, -3.87) * mm, "end": v(-14.95, -3.87) * mm});
            skLineSegment(sketch, "E360", {"start": v(-14.95, -3.87) * mm, "end": v(-14.9, -3.87) * mm});
            skLineSegment(sketch, "E361", {"start": v(-14.9, -3.87) * mm, "end": v(-14.85, -3.87) * mm});
            skLineSegment(sketch, "E362", {"start": v(-14.85, -3.87) * mm, "end": v(-14.8, -3.87) * mm});
            skLineSegment(sketch, "E363", {"start": v(-14.8, -3.87) * mm, "end": v(-14.75, -3.87) * mm});
            skLineSegment(sketch, "E364", {"start": v(-14.75, -3.87) * mm, "end": v(-14.7, -3.87) * mm});
            skLineSegment(sketch, "E365", {"start": v(-14.7, -3.87) * mm, "end": v(-14.65, -3.87) * mm});
            skLineSegment(sketch, "E366", {"start": v(-14.65, -3.87) * mm, "end": v(-14.6, -3.87) * mm});
            skLineSegment(sketch, "E367", {"start": v(-14.6, -3.87) * mm, "end": v(-14.55, -3.87) * mm});
            skLineSegment(sketch, "E368", {"start": v(-14.55, -3.87) * mm, "end": v(-14.5, -3.87) * mm});
            skLineSegment(sketch, "E369", {"start": v(-14.5, -3.87) * mm, "end": v(-14.45, -3.87) * mm});
            skLineSegment(sketch, "E370", {"start": v(-14.45, -3.87) * mm, "end": v(-14.4, -3.87) * mm});
            skLineSegment(sketch, "E371", {"start": v(-14.4, -3.87) * mm, "end": v(-14.35, -3.87) * mm});
            skLineSegment(sketch, "E372", {"start": v(-14.35, -3.87) * mm, "end": v(-14.3, -3.87) * mm});
            skLineSegment(sketch, "E373", {"start": v(-14.3, -3.87) * mm, "end": v(-14.25, -3.87) * mm});
            skLineSegment(sketch, "E374", {"start": v(-14.25, -3.87) * mm, "end": v(-14.2, -3.87) * mm});
            skLineSegment(sketch, "E375", {"start": v(-14.2, -3.87) * mm, "end": v(-14.15, -3.87) * mm});
            skLineSegment(sketch, "E376", {"start": v(-14.15, -3.87) * mm, "end": v(-14.1, -3.87) * mm});
            skLineSegment(sketch, "E377", {"start": v(-14.1, -3.87) * mm, "end": v(-14.05, -3.87) * mm});
            skLineSegment(sketch, "E378", {"start": v(-14.05, -3.87) * mm, "end": v(-14, -3.87) * mm});
            skLineSegment(sketch, "E379", {"start": v(-14, -3.87) * mm, "end": v(-13.95, -3.87) * mm});
            skLineSegment(sketch, "E380", {"start": v(-13.95, -3.87) * mm, "end": v(-13.9, -3.87) * mm});
            skLineSegment(sketch, "E381", {"start": v(-13.9, -3.87) * mm, "end": v(-13.85, -3.87) * mm});
            skLineSegment(sketch, "E382", {"start": v(-13.85, -3.87) * mm, "end": v(-13.8, -3.87) * mm});
            skLineSegment(sketch, "E383", {"start": v(-13.8, -3.87) * mm, "end": v(-13.75, -3.87) * mm});
            skLineSegment(sketch, "E384", {"start": v(-13.75, -3.87) * mm, "end": v(-13.7, -3.87) * mm});
            skLineSegment(sketch, "E385", {"start": v(-13.7, -3.87) * mm, "end": v(-13.65, -3.87) * mm});
            skLineSegment(sketch, "E386", {"start": v(-13.65, -3.87) * mm, "end": v(-13.6, -3.87) * mm});
            skLineSegment(sketch, "E387", {"start": v(-13.6, -3.87) * mm, "end": v(-13.55, -3.87) * mm});
            skLineSegment(sketch, "E388", {"start": v(-13.55, -3.87) * mm, "end": v(-13.5, -3.87) * mm});
            skLineSegment(sketch, "E389", {"start": v(-13.5, -3.87) * mm, "end": v(-13.45, -3.87) * mm});
            skLineSegment(sketch, "E390", {"start": v(-13.45, -3.87) * mm, "end": v(-13.4, -3.87) * mm});
            skLineSegment(sketch, "E391", {"start": v(-13.4, -3.87) * mm, "end": v(-13.35, -3.87) * mm});
            skLineSegment(sketch, "E392", {"start": v(-13.35, -3.87) * mm, "end": v(-13.3, -3.87) * mm});
            skLineSegment(sketch, "E393", {"start": v(-13.3, -3.87) * mm, "end": v(-13.25, -3.87) * mm});
            skLineSegment(sketch, "E394", {"start": v(-13.25, -3.87) * mm, "end": v(-13.2, -3.87) * mm});
            skLineSegment(sketch, "E395", {"start": v(-13.2, -3.87) * mm, "end": v(-13.15, -3.87) * mm});
            skLineSegment(sketch, "E396", {"start": v(-13.15, -3.87) * mm, "end": v(-13.1, -3.87) * mm});
            skLineSegment(sketch, "E397", {"start": v(-13.1, -3.87) * mm, "end": v(-13.05, -3.87) * mm});
            skLineSegment(sketch, "E398", {"start": v(-13.05, -3.87) * mm, "end": v(-13, -3.87) * mm});
            skLineSegment(sketch, "E399", {"start": v(-13, -3.87) * mm, "end": v(-12.95, -3.87) * mm});
            skLineSegment(sketch, "E400", {"start": v(-12.95, -3.87) * mm, "end": v(-12.9, -3.87) * mm});
            skLineSegment(sketch, "E401", {"start": v(-12.9, -3.87) * mm, "end": v(-12.85, -3.87) * mm});
            skLineSegment(sketch, "E402", {"start": v(-12.85, -3.87) * mm, "end": v(-12.8, -3.87) * mm});
            skLineSegment(sketch, "E403", {"start": v(-12.8, -3.87) * mm, "end": v(-12.75, -3.87) * mm});
            skLineSegment(sketch, "E404", {"start": v(-12.75, -3.87) * mm, "end": v(-12.7, -3.87) * mm});
            skLineSegment(sketch, "E405", {"start": v(-12.7, -3.87) * mm, "end": v(-12.65, -3.87) * mm});
            skLineSegment(sketch, "E406", {"start": v(-12.65, -3.87) * mm, "end": v(-12.6, -3.87) * mm});
            skLineSegment(sketch, "E407", {"start": v(-12.6, -3.87) * mm, "end": v(-12.55, -3.87) * mm});
            skLineSegment(sketch, "E408", {"start": v(-12.55, -3.87) * mm, "end": v(-12.5, -3.87) * mm});
            skLineSegment(sketch, "E409", {"start": v(-12.5, -3.87) * mm, "end": v(-12.45, -3.87) * mm});
            skLineSegment(sketch, "E410", {"start": v(-12.45, -3.87) * mm, "end": v(-12.4, -3.87) * mm});
            skLineSegment(sketch, "E411", {"start": v(-12.4, -3.87) * mm, "end": v(-12.35, -3.87) * mm});
            skLineSegment(sketch, "E412", {"start": v(-12.35, -3.87) * mm, "end": v(-12.3, -3.87) * mm});
            skLineSegment(sketch, "E413", {"start": v(-12.3, -3.87) * mm, "end": v(-12.25, -3.87) * mm});
            skLineSegment(sketch, "E414", {"start": v(-12.25, -3.87) * mm, "end": v(-12.2, -3.87) * mm});
            skLineSegment(sketch, "E415", {"start": v(-12.2, -3.87) * mm, "end": v(-12.15, -3.87) * mm});
            skLineSegment(sketch, "E416", {"start": v(-12.15, -3.87) * mm, "end": v(-12.1, -3.87) * mm});
            skLineSegment(sketch, "E417", {"start": v(-12.1, -3.87) * mm, "end": v(-12.05, -3.87) * mm});
            skLineSegment(sketch, "E418", {"start": v(-12.05, -3.87) * mm, "end": v(-12, -3.87) * mm});
            skLineSegment(sketch, "E419", {"start": v(-12, -3.87) * mm, "end": v(-11.95, -3.87) * mm});
            skLineSegment(sketch, "E420", {"start": v(-11.95, -3.87) * mm, "end": v(-11.9, -3.87) * mm});
            skLineSegment(sketch, "E421", {"start": v(-11.9, -3.87) * mm, "end": v(-11.85, -3.87) * mm});
            skLineSegment(sketch, "E422", {"start": v(-11.85, -3.87) * mm, "end": v(-11.8, -3.87) * mm});
            skLineSegment(sketch, "E423", {"start": v(-11.8, -3.87) * mm, "end": v(-11.75, -3.87) * mm});
            skLineSegment(sketch, "E424", {"start": v(-11.75, -3.87) * mm, "end": v(-11.7, -3.87) * mm});
            skLineSegment(sketch, "E425", {"start": v(-11.7, -3.87) * mm, "end": v(-11.65, -3.87) * mm});
            skLineSegment(sketch, "E426", {"start": v(-11.65, -3.87) * mm, "end": v(-11.6, -3.87) * mm});
            skLineSegment(sketch, "E427", {"start": v(-11.6, -3.87) * mm, "end": v(-11.55, -3.87) * mm});
            skLineSegment(sketch, "E428", {"start": v(-11.55, -3.87) * mm, "end": v(-11.5, -3.87) * mm});
            skLineSegment(sketch, "E429", {"start": v(-11.5, -3.87) * mm, "end": v(-11.45, -3.87) * mm});
            skLineSegment(sketch, "E430", {"start": v(-11.45, -3.87) * mm, "end": v(-11.4, -3.87) * mm});
            skLineSegment(sketch, "E431", {"start": v(-11.4, -3.87) * mm, "end": v(-11.35, -3.87) * mm});
            skLineSegment(sketch, "E432", {"start": v(-11.35, -3.87) * mm, "end": v(-11.3, -3.87) * mm});
            skLineSegment(sketch, "E433", {"start": v(-11.3, -3.87) * mm, "end": v(-11.25, -3.87) * mm});
            skLineSegment(sketch, "E434", {"start": v(-11.25, -3.87) * mm, "end": v(-11.2, -3.87) * mm});
            skLineSegment(sketch, "E435", {"start": v(-11.2, -3.87) * mm, "end": v(-11.15, -3.87) * mm});
            skLineSegment(sketch, "E436", {"start": v(-11.15, -3.87) * mm, "end": v(-11.1, -3.87) * mm});
            skLineSegment(sketch, "E437", {"start": v(-11.1, -3.87) * mm, "end": v(-11.05, -3.87) * mm});
            skLineSegment(sketch, "E438", {"start": v(-11.05, -3.87) * mm, "end": v(-11, -3.87) * mm});
            skLineSegment(sketch, "E439", {"start": v(-11, -3.87) * mm, "end": v(-10.95, -3.87) * mm});
            skLineSegment(sketch, "E440", {"start": v(-10.95, -3.87) * mm, "end": v(-10.9, -3.87) * mm});
            skLineSegment(sketch, "E441", {"start": v(-10.9, -3.87) * mm, "end": v(-10.85, -3.87) * mm});
            skLineSegment(sketch, "E442", {"start": v(-10.85, -3.87) * mm, "end": v(-10.8, -3.87) * mm});
            skLineSegment(sketch, "E443", {"start": v(-10.8, -3.87) * mm, "end": v(-10.75, -3.87) * mm});
            skLineSegment(sketch, "E444", {"start": v(-10.75, -3.87) * mm, "end": v(-10.7, -3.87) * mm});
            skLineSegment(sketch, "E445", {"start": v(-10.7, -3.87) * mm, "end": v(-10.65, -3.87) * mm});
            skLineSegment(sketch, "E446", {"start": v(-10.65, -3.87) * mm, "end": v(-10.6, -3.87) * mm});
            skLineSegment(sketch, "E447", {"start": v(-10.6, -3.87) * mm, "end": v(-10.55, -3.87) * mm});
            skLineSegment(sketch, "E448", {"start": v(-10.55, -3.87) * mm, "end": v(-10.5, -3.87) * mm});
            skLineSegment(sketch, "E449", {"start": v(-10.5, -3.87) * mm, "end": v(-10.45, -3.87) * mm});
            skLineSegment(sketch, "E450", {"start": v(-10.45, -3.87) * mm, "end": v(-10.4, -3.87) * mm});
            skLineSegment(sketch, "E451", {"start": v(-10.4, -3.87) * mm, "end": v(-10.35, -3.87) * mm});
            skLineSegment(sketch, "E452", {"start": v(-10.35, -3.87) * mm, "end": v(-10.3, -3.87) * mm});
            skLineSegment(sketch, "E453", {"start": v(-10.3, -3.87) * mm, "end": v(-10.25, -3.87) * mm});
            skLineSegment(sketch, "E454", {"start": v(-10.25, -3.87) * mm, "end": v(-10.2, -3.87) * mm});
            skLineSegment(sketch, "E455", {"start": v(-10.2, -3.87) * mm, "end": v(-10.15, -3.87) * mm});
            skLineSegment(sketch, "E456", {"start": v(-10.15, -3.87) * mm, "end": v(-10.1, -3.87) * mm});
            skLineSegment(sketch, "E457", {"start": v(-10.1, -3.87) * mm, "end": v(-10.05, -3.87) * mm});
            skLineSegment(sketch, "E458", {"start": v(-10.05, -3.87) * mm, "end": v(-10, -3.87) * mm});
            skLineSegment(sketch, "E459", {"start": v(-10, -3.87) * mm, "end": v(-9.95, -3.87) * mm});
            skLineSegment(sketch, "E460", {"start": v(-9.95, -3.87) * mm, "end": v(-9.9, -3.87) * mm});
            skLineSegment(sketch, "E461", {"start": v(-9.9, -3.87) * mm, "end": v(-9.85, -3.87) * mm});
            skLineSegment(sketch, "E462", {"start": v(-9.85, -3.87) * mm, "end": v(-9.8, -3.87) * mm});
            skLineSegment(sketch, "E463", {"start": v(-9.8, -3.87) * mm, "end": v(-9.75, -3.87) * mm});
            skLineSegment(sketch, "E464", {"start": v(-9.75, -3.87) * mm, "end": v(-9.7, -3.87) * mm});
            skLineSegment(sketch, "E465", {"start": v(-9.7, -3.87) * mm, "end": v(-9.65, -3.87) * mm});
            skLineSegment(sketch, "E466", {"start": v(-9.65, -3.87) * mm, "end": v(-9.6, -3.87) * mm});
            skLineSegment(sketch, "E467", {"start": v(-9.6, -3.87) * mm, "end": v(-9.55, -3.87) * mm});
            skLineSegment(sketch, "E468", {"start": v(-9.55, -3.87) * mm, "end": v(-9.5, -3.87) * mm});
            skLineSegment(sketch, "E469", {"start": v(-9.5, -3.87) * mm, "end": v(-9.45, -3.87) * mm});
            skLineSegment(sketch, "E470", {"start": v(-9.45, -3.87) * mm, "end": v(-9.4, -3.87) * mm});
            skLineSegment(sketch, "E471", {"start": v(-9.4, -3.87) * mm, "end": v(-9.35, -3.87) * mm});
            skLineSegment(sketch, "E472", {"start": v(-9.35, -3.87) * mm, "end": v(-9.3, -3.87) * mm});
            skLineSegment(sketch, "E473", {"start": v(-9.3, -3.87) * mm, "end": v(-9.25, -3.87) * mm});
            skLineSegment(sketch, "E474", {"start": v(-9.25, -3.87) * mm, "end": v(-9.2, -3.87) * mm});
            skLineSegment(sketch, "E475", {"start": v(-9.2, -3.87) * mm, "end": v(-9.15, -3.87) * mm});
            skLineSegment(sketch, "E476", {"start": v(-9.15, -3.87) * mm, "end": v(-9.1, -3.87) * mm});
            skLineSegment(sketch, "E477", {"start": v(-9.1, -3.87) * mm, "end": v(-9.05, -3.87) * mm});
            skLineSegment(sketch, "E478", {"start": v(-9.05, -3.87) * mm, "end": v(-9, -3.87) * mm});
            skLineSegment(sketch, "E479", {"start": v(-9, -3.87) * mm, "end": v(-8.95, -3.87) * mm});
            skLineSegment(sketch, "E480", {"start": v(-8.95, -3.87) * mm, "end": v(-8.9, -3.87) * mm});
            skLineSegment(sketch, "E481", {"start": v(-8.9, -3.87) * mm, "end": v(-8.85, -3.87) * mm});
            skLineSegment(sketch, "E482", {"start": v(-8.85, -3.87) * mm, "end": v(-8.8, -3.87) * mm});
            skLineSegment(sketch, "E483", {"start": v(-8.8, -3.87) * mm, "end": v(-8.75, -3.87) * mm});
            skLineSegment(sketch, "E484", {"start": v(-8.75, -3.87) * mm, "end": v(-8.7, -3.87) * mm});
            skLineSegment(sketch, "E485", {"start": v(-8.7, -3.87) * mm, "end": v(-8.65, -3.87) * mm});
            skLineSegment(sketch, "E486", {"start": v(-8.65, -3.87) * mm, "end": v(-8.6, -3.87) * mm});
            skLineSegment(sketch, "E487", {"start": v(-8.6, -3.87) * mm, "end": v(-8.55, -3.87) * mm});
            skLineSegment(sketch, "E488", {"start": v(-8.55, -3.87) * mm, "end": v(-8.5, -3.87) * mm});
            skLineSegment(sketch, "E489", {"start": v(-8.5, -3.87) * mm, "end": v(-8.45, -3.87) * mm});
            skLineSegment(sketch, "E490", {"start": v(-8.45, -3.87) * mm, "end": v(-8.4, -3.87) * mm});
            skLineSegment(sketch, "E491", {"start": v(-8.4, -3.87) * mm, "end": v(-8.35, -3.87) * mm});
            skLineSegment(sketch, "E492", {"start": v(-8.35, -3.87) * mm, "end": v(-8.3, -3.87) * mm});
            skLineSegment(sketch, "E493", {"start": v(-8.3, -3.87) * mm, "end": v(-8.25, -3.87) * mm});
            skLineSegment(sketch, "E494", {"start": v(-8.25, -3.87) * mm, "end": v(-8.2, -3.87) * mm});
            skLineSegment(sketch, "E495", {"start": v(-8.2, -3.87) * mm, "end": v(-8.15, -3.87) * mm});
            skLineSegment(sketch, "E496", {"start": v(-8.15, -3.87) * mm, "end": v(-8.1, -3.87) * mm});
            skLineSegment(sketch, "E497", {"start": v(-8.1, -3.87) * mm, "end": v(-8.05, -3.87) * mm});
            skLineSegment(sketch, "E498", {"start": v(-8.05, -3.87) * mm, "end": v(-8, -3.87) * mm});
            skLineSegment(sketch, "E499", {"start": v(-8, -3.87) * mm, "end": v(-7.95, -3.87) * mm});
            skLineSegment(sketch, "E500", {"start": v(-7.95, -3.87) * mm, "end": v(-7.9, -3.87) * mm});
            skLineSegment(sketch, "E501", {"start": v(-7.9, -3.87) * mm, "end": v(-7.85, -3.87) * mm});
            skLineSegment(sketch, "E502", {"start": v(-7.85, -3.87) * mm, "end": v(-7.8, -3.87) * mm});
            skLineSegment(sketch, "E503", {"start": v(-7.8, -3.87) * mm, "end": v(-7.75, -3.87) * mm});
            skLineSegment(sketch, "E504", {"start": v(-7.75, -3.87) * mm, "end": v(-7.7, -3.87) * mm});
            skLineSegment(sketch, "E505", {"start": v(-7.7, -3.87) * mm, "end": v(-7.65, -3.87) * mm});
            skLineSegment(sketch, "E506", {"start": v(-7.65, -3.87) * mm, "end": v(-7.6, -3.87) * mm});
            skLineSegment(sketch, "E507", {"start": v(-7.6, -3.87) * mm, "end": v(-7.55, -3.87) * mm});
            skLineSegment(sketch, "E508", {"start": v(-7.55, -3.87) * mm, "end": v(-7.5, -3.87) * mm});
            skLineSegment(sketch, "E509", {"start": v(-7.5, -3.87) * mm, "end": v(-7.45, -3.87) * mm});
            skLineSegment(sketch, "E510", {"start": v(-7.45, -3.87) * mm, "end": v(-7.2, -3.87) * mm});
            skLineSegment(sketch, "E511", {"start": v(-7.2, -3.87) * mm, "end": v(-7.2, -4.07) * mm});
            skLineSegment(sketch, "E512", {"start": v(-7.2, -4.07) * mm, "end": v(-7.2, -4.12) * mm});
            skLineSegment(sketch, "E513", {"start": v(-7.2, -4.12) * mm, "end": v(-7.2, -4.17) * mm});
            skLineSegment(sketch, "E514", {"start": v(-7.2, -4.17) * mm, "end": v(-7.2, -4.22) * mm});
            skLineSegment(sketch, "E515", {"start": v(-7.2, -4.22) * mm, "end": v(-7.2, -4.27) * mm});
            skLineSegment(sketch, "E516", {"start": v(-7.2, -4.27) * mm, "end": v(-7.2, -4.32) * mm});
            skLineSegment(sketch, "E517", {"start": v(-7.2, -4.32) * mm, "end": v(-7.2, -4.37) * mm});
            skLineSegment(sketch, "E518", {"start": v(-7.2, -4.37) * mm, "end": v(-7.2, -4.42) * mm});
            skLineSegment(sketch, "E519", {"start": v(-7.2, -4.42) * mm, "end": v(-7.2, -4.47) * mm});
            skLineSegment(sketch, "E520", {"start": v(-7.2, -4.47) * mm, "end": v(-7.2, -4.52) * mm});
            skLineSegment(sketch, "E521", {"start": v(-7.2, -4.52) * mm, "end": v(-7.2, -4.57) * mm});
            skLineSegment(sketch, "E522", {"start": v(-7.2, -4.57) * mm, "end": v(-7.2, -4.62) * mm});
            skLineSegment(sketch, "E523", {"start": v(-7.2, -4.62) * mm, "end": v(-7.2, -4.67) * mm});
            skLineSegment(sketch, "E524", {"start": v(-7.2, -4.67) * mm, "end": v(-7.2, -4.72) * mm});
            skLineSegment(sketch, "E525", {"start": v(-7.2, -4.72) * mm, "end": v(-7.2, -4.77) * mm});
            skLineSegment(sketch, "E526", {"start": v(-7.2, -4.77) * mm, "end": v(-7.2, -4.82) * mm});
            skLineSegment(sketch, "E527", {"start": v(-7.2, -4.82) * mm, "end": v(-7.2, -4.87) * mm});
            skLineSegment(sketch, "E528", {"start": v(-7.2, -4.87) * mm, "end": v(-7.2, -4.92) * mm});
            skLineSegment(sketch, "E529", {"start": v(-7.2, -4.92) * mm, "end": v(-7.2, -4.97) * mm});
            skLineSegment(sketch, "E530", {"start": v(-7.2, -4.97) * mm, "end": v(-7.2, -5.02) * mm});
            skLineSegment(sketch, "E531", {"start": v(-7.2, -5.02) * mm, "end": v(-7.2, -5.07) * mm});
            skLineSegment(sketch, "E532", {"start": v(-7.2, -5.07) * mm, "end": v(-7.2, -5.12) * mm});
            skLineSegment(sketch, "E533", {"start": v(-7.2, -5.12) * mm, "end": v(-7.2, -5.17) * mm});
            skLineSegment(sketch, "E534", {"start": v(-7.2, -5.17) * mm, "end": v(-7.2, -5.22) * mm});
            skLineSegment(sketch, "E535", {"start": v(-7.2, -5.22) * mm, "end": v(-7.2, -5.27) * mm});
            skLineSegment(sketch, "E536", {"start": v(-7.2, -5.27) * mm, "end": v(-7.2, -5.32) * mm});
            skLineSegment(sketch, "E537", {"start": v(-7.2, -5.32) * mm, "end": v(-7.2, -5.38) * mm});
            skLineSegment(sketch, "E538", {"start": v(-7.2, -5.38) * mm, "end": v(-7.2, -5.42) * mm});
            skLineSegment(sketch, "E539", {"start": v(-7.2, -5.42) * mm, "end": v(-7.2, -5.47) * mm});
            skLineSegment(sketch, "E540", {"start": v(-7.2, -5.47) * mm, "end": v(-7.2, -5.52) * mm});
            skLineSegment(sketch, "E541", {"start": v(-7.2, -5.52) * mm, "end": v(-7.2, -5.57) * mm});
            skLineSegment(sketch, "E542", {"start": v(-7.2, -5.57) * mm, "end": v(-7.2, -5.62) * mm});
            skLineSegment(sketch, "E543", {"start": v(-7.2, -5.62) * mm, "end": v(-7.2, -5.67) * mm});
            skLineSegment(sketch, "E544", {"start": v(-7.2, -5.67) * mm, "end": v(-7.2, -5.72) * mm});
            skLineSegment(sketch, "E545", {"start": v(-7.2, -5.72) * mm, "end": v(-7.2, -5.77) * mm});
            skLineSegment(sketch, "E546", {"start": v(-7.2, -5.77) * mm, "end": v(-7.2, -5.82) * mm});
            skLineSegment(sketch, "E547", {"start": v(-7.2, -5.82) * mm, "end": v(-7.2, -5.87) * mm});
            skLineSegment(sketch, "E548", {"start": v(-7.2, -5.87) * mm, "end": v(-7.2, -5.92) * mm});
            skLineSegment(sketch, "E549", {"start": v(-7.2, -5.92) * mm, "end": v(-7.2, -5.97) * mm});
            skLineSegment(sketch, "E550", {"start": v(-7.2, -5.97) * mm, "end": v(-7.2, -6.02) * mm});
            skLineSegment(sketch, "E551", {"start": v(-7.2, -6.02) * mm, "end": v(-7.2, -6.07) * mm});
            skLineSegment(sketch, "E552", {"start": v(-7.2, -6.07) * mm, "end": v(-7.2, -6.12) * mm});
            skLineSegment(sketch, "E553", {"start": v(-7.2, -6.12) * mm, "end": v(-7.2, -6.17) * mm});
            skLineSegment(sketch, "E554", {"start": v(-7.2, -6.17) * mm, "end": v(-7.2, -6.22) * mm});
            skLineSegment(sketch, "E555", {"start": v(-7.2, -6.22) * mm, "end": v(-7.2, -6.57) * mm});
            skLineSegment(sketch, "E556", {"start": v(-7.2, -6.57) * mm, "end": v(-7, -6.57) * mm});
            skLineSegment(sketch, "E557", {"start": v(-7, -6.57) * mm, "end": v(-6.95, -6.57) * mm});
            skLineSegment(sketch, "E558", {"start": v(-6.95, -6.57) * mm, "end": v(-6.9, -6.57) * mm});
            skLineSegment(sketch, "E559", {"start": v(-6.9, -6.57) * mm, "end": v(-6.85, -6.57) * mm});
            skLineSegment(sketch, "E560", {"start": v(-6.85, -6.57) * mm, "end": v(-6.8, -6.57) * mm});
            skLineSegment(sketch, "E561", {"start": v(-6.8, -6.57) * mm, "end": v(-6.75, -6.57) * mm});
            skLineSegment(sketch, "E562", {"start": v(-6.75, -6.57) * mm, "end": v(-6.7, -6.57) * mm});
            skLineSegment(sketch, "E563", {"start": v(-6.7, -6.57) * mm, "end": v(-6.65, -6.57) * mm});
            skLineSegment(sketch, "E564", {"start": v(-6.65, -6.57) * mm, "end": v(-6.6, -6.57) * mm});
            skLineSegment(sketch, "E565", {"start": v(-6.6, -6.57) * mm, "end": v(-6.55, -6.57) * mm});
            skLineSegment(sketch, "E566", {"start": v(-6.55, -6.57) * mm, "end": v(-6.5, -6.57) * mm});
            skLineSegment(sketch, "E567", {"start": v(-6.5, -6.57) * mm, "end": v(-6.45, -6.57) * mm});
            skLineSegment(sketch, "E568", {"start": v(-6.45, -6.57) * mm, "end": v(-6.4, -6.57) * mm});
            skLineSegment(sketch, "E569", {"start": v(-6.4, -6.57) * mm, "end": v(-6.35, -6.57) * mm});
            skLineSegment(sketch, "E570", {"start": v(-6.35, -6.57) * mm, "end": v(-6.3, -6.57) * mm});
            skLineSegment(sketch, "E571", {"start": v(-6.3, -6.57) * mm, "end": v(-6.25, -6.57) * mm});
            skLineSegment(sketch, "E572", {"start": v(-6.25, -6.57) * mm, "end": v(-6.2, -6.57) * mm});
            skLineSegment(sketch, "E573", {"start": v(-6.2, -6.57) * mm, "end": v(-6.15, -6.57) * mm});
            skLineSegment(sketch, "E574", {"start": v(-6.15, -6.57) * mm, "end": v(-6.1, -6.57) * mm});
            skLineSegment(sketch, "E575", {"start": v(-6.1, -6.57) * mm, "end": v(-6.05, -6.57) * mm});
            skLineSegment(sketch, "E576", {"start": v(-6.05, -6.57) * mm, "end": v(-6, -6.57) * mm});
            skLineSegment(sketch, "E577", {"start": v(-6, -6.57) * mm, "end": v(-5.95, -6.57) * mm});
            skLineSegment(sketch, "E578", {"start": v(-5.95, -6.57) * mm, "end": v(-5.9, -6.57) * mm});
            skLineSegment(sketch, "E579", {"start": v(-5.9, -6.57) * mm, "end": v(-5.85, -6.57) * mm});
            skLineSegment(sketch, "E580", {"start": v(-5.85, -6.57) * mm, "end": v(-5.8, -6.57) * mm});
            skLineSegment(sketch, "E581", {"start": v(-5.8, -6.57) * mm, "end": v(-5.75, -6.57) * mm});
            skLineSegment(sketch, "E582", {"start": v(-5.75, -6.57) * mm, "end": v(-5.7, -6.57) * mm});
            skLineSegment(sketch, "E583", {"start": v(-5.7, -6.57) * mm, "end": v(-5.65, -6.57) * mm});
            skLineSegment(sketch, "E584", {"start": v(-5.65, -6.57) * mm, "end": v(-5.6, -6.57) * mm});
            skLineSegment(sketch, "E585", {"start": v(-5.6, -6.57) * mm, "end": v(-5.55, -6.57) * mm});
            skLineSegment(sketch, "E586", {"start": v(-5.55, -6.57) * mm, "end": v(-5.5, -6.57) * mm});
            skLineSegment(sketch, "E587", {"start": v(-5.5, -6.57) * mm, "end": v(-5.45, -6.57) * mm});
            skLineSegment(sketch, "E588", {"start": v(-5.45, -6.57) * mm, "end": v(-5.4, -6.57) * mm});
            skLineSegment(sketch, "E589", {"start": v(-5.4, -6.57) * mm, "end": v(-5.35, -6.57) * mm});
            skLineSegment(sketch, "E590", {"start": v(-5.35, -6.57) * mm, "end": v(-5.3, -6.57) * mm});
            skLineSegment(sketch, "E591", {"start": v(-5.3, -6.57) * mm, "end": v(-5.25, -6.57) * mm});
            skLineSegment(sketch, "E592", {"start": v(-5.25, -6.57) * mm, "end": v(-5.2, -6.57) * mm});
            skLineSegment(sketch, "E593", {"start": v(-5.2, -6.57) * mm, "end": v(-5.15, -6.57) * mm});
            skLineSegment(sketch, "E594", {"start": v(-5.15, -6.57) * mm, "end": v(-5.1, -6.57) * mm});
            skLineSegment(sketch, "E595", {"start": v(-5.1, -6.57) * mm, "end": v(-5.05, -6.57) * mm});
            skLineSegment(sketch, "E596", {"start": v(-5.05, -6.57) * mm, "end": v(-5, -6.57) * mm});
            skLineSegment(sketch, "E597", {"start": v(-5, -6.57) * mm, "end": v(-4.95, -6.57) * mm});
            skLineSegment(sketch, "E598", {"start": v(-4.95, -6.57) * mm, "end": v(-4.9, -6.57) * mm});
            skLineSegment(sketch, "E599", {"start": v(-4.9, -6.57) * mm, "end": v(-4.85, -6.57) * mm});
            skLineSegment(sketch, "E600", {"start": v(-4.85, -6.57) * mm, "end": v(-4.8, -6.57) * mm});
            skLineSegment(sketch, "E601", {"start": v(-4.8, -6.57) * mm, "end": v(-4.75, -6.57) * mm});
            skLineSegment(sketch, "E602", {"start": v(-4.75, -6.57) * mm, "end": v(-4.7, -6.57) * mm});
            skLineSegment(sketch, "E603", {"start": v(-4.7, -6.57) * mm, "end": v(-4.65, -6.57) * mm});
            skLineSegment(sketch, "E604", {"start": v(-4.65, -6.57) * mm, "end": v(-4.6, -6.57) * mm});
            skLineSegment(sketch, "E605", {"start": v(-4.6, -6.57) * mm, "end": v(-4.55, -6.57) * mm});
            skLineSegment(sketch, "E606", {"start": v(-4.55, -6.57) * mm, "end": v(-4.5, -6.57) * mm});
            skLineSegment(sketch, "E607", {"start": v(-4.5, -6.57) * mm, "end": v(-4.45, -6.57) * mm});
            skLineSegment(sketch, "E608", {"start": v(-4.45, -6.57) * mm, "end": v(-4.4, -6.57) * mm});
            skLineSegment(sketch, "E609", {"start": v(-4.4, -6.57) * mm, "end": v(-4.35, -6.57) * mm});
            skLineSegment(sketch, "E610", {"start": v(-4.35, -6.57) * mm, "end": v(-4.3, -6.57) * mm});
            skLineSegment(sketch, "E611", {"start": v(-4.3, -6.57) * mm, "end": v(-4.25, -6.57) * mm});
            skLineSegment(sketch, "E612", {"start": v(-4.25, -6.57) * mm, "end": v(-4.2, -6.57) * mm});
            skLineSegment(sketch, "E613", {"start": v(-4.2, -6.57) * mm, "end": v(-4.15, -6.57) * mm});
            skLineSegment(sketch, "E614", {"start": v(-4.15, -6.57) * mm, "end": v(-4.1, -6.57) * mm});
            skLineSegment(sketch, "E615", {"start": v(-4.1, -6.57) * mm, "end": v(-4.05, -6.57) * mm});
            skLineSegment(sketch, "E616", {"start": v(-4.05, -6.57) * mm, "end": v(-4, -6.57) * mm});
            skLineSegment(sketch, "E617", {"start": v(-4, -6.57) * mm, "end": v(-3.95, -6.57) * mm});
            skLineSegment(sketch, "E618", {"start": v(-3.95, -6.57) * mm, "end": v(-3.9, -6.57) * mm});
            skLineSegment(sketch, "E619", {"start": v(-3.9, -6.57) * mm, "end": v(-3.85, -6.57) * mm});
            skLineSegment(sketch, "E620", {"start": v(-3.85, -6.57) * mm, "end": v(-3.8, -6.57) * mm});
            skLineSegment(sketch, "E621", {"start": v(-3.8, -6.57) * mm, "end": v(-3.75, -6.57) * mm});
            skLineSegment(sketch, "E622", {"start": v(-3.75, -6.57) * mm, "end": v(-3.7, -6.57) * mm});
            skLineSegment(sketch, "E623", {"start": v(-3.7, -6.57) * mm, "end": v(-3.65, -6.57) * mm});
            skLineSegment(sketch, "E624", {"start": v(-3.65, -6.57) * mm, "end": v(-3.6, -6.57) * mm});
            skLineSegment(sketch, "E625", {"start": v(-3.6, -6.57) * mm, "end": v(-3.55, -6.57) * mm});
            skLineSegment(sketch, "E626", {"start": v(-3.55, -6.57) * mm, "end": v(-3.5, -6.57) * mm});
            skLineSegment(sketch, "E627", {"start": v(-3.5, -6.57) * mm, "end": v(-3.45, -6.57) * mm});
            skLineSegment(sketch, "E628", {"start": v(-3.45, -6.57) * mm, "end": v(-3.4, -6.57) * mm});
            skLineSegment(sketch, "E629", {"start": v(-3.4, -6.57) * mm, "end": v(-3.35, -6.57) * mm});
            skLineSegment(sketch, "E630", {"start": v(-3.35, -6.57) * mm, "end": v(-3.3, -6.57) * mm});
            skLineSegment(sketch, "E631", {"start": v(-3.3, -6.57) * mm, "end": v(-3.25, -6.57) * mm});
            skLineSegment(sketch, "E632", {"start": v(-3.25, -6.57) * mm, "end": v(-3.2, -6.57) * mm});
            skLineSegment(sketch, "E633", {"start": v(-3.2, -6.57) * mm, "end": v(-3.15, -6.57) * mm});
            skLineSegment(sketch, "E634", {"start": v(-3.15, -6.57) * mm, "end": v(-3.1, -6.57) * mm});
            skLineSegment(sketch, "E635", {"start": v(-3.1, -6.57) * mm, "end": v(-3.05, -6.57) * mm});
            skLineSegment(sketch, "E636", {"start": v(-3.05, -6.57) * mm, "end": v(-3, -6.57) * mm});
            skLineSegment(sketch, "E637", {"start": v(-3, -6.57) * mm, "end": v(-2.95, -6.57) * mm});
            skLineSegment(sketch, "E638", {"start": v(-2.95, -6.57) * mm, "end": v(-2.9, -6.57) * mm});
            skLineSegment(sketch, "E639", {"start": v(-2.9, -6.57) * mm, "end": v(-2.85, -6.57) * mm});
            skLineSegment(sketch, "E640", {"start": v(-2.85, -6.57) * mm, "end": v(-2.8, -6.57) * mm});
            skLineSegment(sketch, "E641", {"start": v(-2.8, -6.57) * mm, "end": v(-2.75, -6.57) * mm});
            skLineSegment(sketch, "E642", {"start": v(-2.75, -6.57) * mm, "end": v(-2.7, -6.57) * mm});
            skLineSegment(sketch, "E643", {"start": v(-2.7, -6.57) * mm, "end": v(-2.65, -6.57) * mm});
            skLineSegment(sketch, "E644", {"start": v(-2.65, -6.57) * mm, "end": v(-2.6, -6.57) * mm});
            skLineSegment(sketch, "E645", {"start": v(-2.6, -6.57) * mm, "end": v(-2.55, -6.57) * mm});
            skLineSegment(sketch, "E646", {"start": v(-2.55, -6.57) * mm, "end": v(-2.5, -6.57) * mm});
            skLineSegment(sketch, "E647", {"start": v(-2.5, -6.57) * mm, "end": v(-2.45, -6.57) * mm});
            skLineSegment(sketch, "E648", {"start": v(-2.45, -6.57) * mm, "end": v(-2.4, -6.57) * mm});
            skLineSegment(sketch, "E649", {"start": v(-2.4, -6.57) * mm, "end": v(-2.35, -6.57) * mm});
            skLineSegment(sketch, "E650", {"start": v(-2.35, -6.57) * mm, "end": v(-2.3, -6.57) * mm});
            skLineSegment(sketch, "E651", {"start": v(-2.3, -6.57) * mm, "end": v(-2.25, -6.57) * mm});
            skLineSegment(sketch, "E652", {"start": v(-2.25, -6.57) * mm, "end": v(-2.2, -6.57) * mm});
            skLineSegment(sketch, "E653", {"start": v(-2.2, -6.57) * mm, "end": v(-2.15, -6.57) * mm});
            skLineSegment(sketch, "E654", {"start": v(-2.15, -6.57) * mm, "end": v(-2.1, -6.57) * mm});
            skLineSegment(sketch, "E655", {"start": v(-2.1, -6.57) * mm, "end": v(-2.05, -6.57) * mm});
            skLineSegment(sketch, "E656", {"start": v(-2.05, -6.57) * mm, "end": v(-2, -6.57) * mm});
            skLineSegment(sketch, "E657", {"start": v(-2, -6.57) * mm, "end": v(-1.95, -6.57) * mm});
            skLineSegment(sketch, "E658", {"start": v(-1.95, -6.57) * mm, "end": v(-1.9, -6.57) * mm});
            skLineSegment(sketch, "E659", {"start": v(-1.9, -6.57) * mm, "end": v(-1.85, -6.57) * mm});
            skLineSegment(sketch, "E660", {"start": v(-1.85, -6.57) * mm, "end": v(-1.8, -6.57) * mm});
            skLineSegment(sketch, "E661", {"start": v(-1.8, -6.57) * mm, "end": v(-1.75, -6.57) * mm});
            skLineSegment(sketch, "E662", {"start": v(-1.75, -6.57) * mm, "end": v(-1.7, -6.57) * mm});
            skLineSegment(sketch, "E663", {"start": v(-1.7, -6.57) * mm, "end": v(-1.65, -6.57) * mm});
            skLineSegment(sketch, "E664", {"start": v(-1.65, -6.57) * mm, "end": v(-1.6, -6.57) * mm});
            skLineSegment(sketch, "E665", {"start": v(-1.6, -6.57) * mm, "end": v(-1.55, -6.57) * mm});
            skLineSegment(sketch, "E666", {"start": v(-1.55, -6.57) * mm, "end": v(-1.5, -6.57) * mm});
            skLineSegment(sketch, "E667", {"start": v(-1.5, -6.57) * mm, "end": v(-1.45, -6.57) * mm});
            skLineSegment(sketch, "E668", {"start": v(-1.45, -6.57) * mm, "end": v(-1.4, -6.57) * mm});
            skLineSegment(sketch, "E669", {"start": v(-1.4, -6.57) * mm, "end": v(-1.35, -6.57) * mm});
            skLineSegment(sketch, "E670", {"start": v(-1.35, -6.57) * mm, "end": v(-1.3, -6.57) * mm});
            skLineSegment(sketch, "E671", {"start": v(-1.3, -6.57) * mm, "end": v(-1.25, -6.57) * mm});
            skLineSegment(sketch, "E672", {"start": v(-1.25, -6.57) * mm, "end": v(-1.2, -6.57) * mm});
            skLineSegment(sketch, "E673", {"start": v(-1.2, -6.57) * mm, "end": v(-1.15, -6.57) * mm});
            skLineSegment(sketch, "E674", {"start": v(-1.15, -6.57) * mm, "end": v(-1.1, -6.57) * mm});
            skLineSegment(sketch, "E675", {"start": v(-1.1, -6.57) * mm, "end": v(-1.05, -6.57) * mm});
            skLineSegment(sketch, "E676", {"start": v(-1.05, -6.57) * mm, "end": v(-1, -6.57) * mm});
            skLineSegment(sketch, "E677", {"start": v(-1, -6.57) * mm, "end": v(-0.95, -6.57) * mm});
            skLineSegment(sketch, "E678", {"start": v(-0.95, -6.57) * mm, "end": v(-0.9, -6.57) * mm});
            skLineSegment(sketch, "E679", {"start": v(-0.9, -6.57) * mm, "end": v(-0.85, -6.57) * mm});
            skLineSegment(sketch, "E680", {"start": v(-0.85, -6.57) * mm, "end": v(-0.8, -6.57) * mm});
            skLineSegment(sketch, "E681", {"start": v(-0.8, -6.57) * mm, "end": v(-0.75, -6.57) * mm});
            skLineSegment(sketch, "E682", {"start": v(-0.75, -6.57) * mm, "end": v(-0.7, -6.57) * mm});
            skLineSegment(sketch, "E683", {"start": v(-0.7, -6.57) * mm, "end": v(-0.65, -6.57) * mm});
            skLineSegment(sketch, "E684", {"start": v(-0.65, -6.57) * mm, "end": v(-0.6, -6.57) * mm});
            skLineSegment(sketch, "E685", {"start": v(-0.6, -6.57) * mm, "end": v(-0.55, -6.57) * mm});
            skLineSegment(sketch, "E686", {"start": v(-0.55, -6.57) * mm, "end": v(-0.5, -6.57) * mm});
            skLineSegment(sketch, "E687", {"start": v(-0.5, -6.57) * mm, "end": v(-0.45, -6.57) * mm});
            skLineSegment(sketch, "E688", {"start": v(-0.45, -6.57) * mm, "end": v(-0.4, -6.57) * mm});
            skLineSegment(sketch, "E689", {"start": v(-0.4, -6.57) * mm, "end": v(-0.35, -6.57) * mm});
            skLineSegment(sketch, "E690", {"start": v(-0.35, -6.57) * mm, "end": v(-0.3, -6.57) * mm});
            skLineSegment(sketch, "E691", {"start": v(-0.3, -6.57) * mm, "end": v(-0.25, -6.57) * mm});
            skLineSegment(sketch, "E692", {"start": v(-0.25, -6.57) * mm, "end": v(-0.2, -6.57) * mm});
            skLineSegment(sketch, "E693", {"start": v(-0.2, -6.57) * mm, "end": v(-0.15, -6.57) * mm});
            skLineSegment(sketch, "E694", {"start": v(-0.15, -6.57) * mm, "end": v(-0.1, -6.57) * mm});
            skLineSegment(sketch, "E695", {"start": v(-0.1, -6.57) * mm, "end": v(-0.05, -6.57) * mm});
            skLineSegment(sketch, "E696", {"start": v(-0.05, -6.57) * mm, "end": v(0, -6.57) * mm});
            skLineSegment(sketch, "E697", {"start": v(0, -6.57) * mm, "end": v(0.05, -6.57) * mm});
            skLineSegment(sketch, "E698", {"start": v(0.05, -6.57) * mm, "end": v(0.1, -6.57) * mm});
            skLineSegment(sketch, "E699", {"start": v(0.1, -6.57) * mm, "end": v(0.15, -6.57) * mm});
            skLineSegment(sketch, "E700", {"start": v(0.15, -6.57) * mm, "end": v(0.2, -6.57) * mm});
            skLineSegment(sketch, "E701", {"start": v(0.2, -6.57) * mm, "end": v(0.25, -6.57) * mm});
            skLineSegment(sketch, "E702", {"start": v(0.25, -6.57) * mm, "end": v(0.3, -6.57) * mm});
            skLineSegment(sketch, "E703", {"start": v(0.3, -6.57) * mm, "end": v(0.35, -6.57) * mm});
            skLineSegment(sketch, "E704", {"start": v(0.35, -6.57) * mm, "end": v(0.4, -6.57) * mm});
            skLineSegment(sketch, "E705", {"start": v(0.4, -6.57) * mm, "end": v(0.45, -6.57) * mm});
            skLineSegment(sketch, "E706", {"start": v(0.45, -6.57) * mm, "end": v(0.5, -6.57) * mm});
            skLineSegment(sketch, "E707", {"start": v(0.5, -6.57) * mm, "end": v(0.55, -6.57) * mm});
            skLineSegment(sketch, "E708", {"start": v(0.55, -6.57) * mm, "end": v(0.6, -6.57) * mm});
            skLineSegment(sketch, "E709", {"start": v(0.6, -6.57) * mm, "end": v(0.65, -6.57) * mm});
            skLineSegment(sketch, "E710", {"start": v(0.65, -6.57) * mm, "end": v(0.7, -6.57) * mm});
            skLineSegment(sketch, "E711", {"start": v(0.7, -6.57) * mm, "end": v(0.75, -6.57) * mm});
            skLineSegment(sketch, "E712", {"start": v(0.75, -6.57) * mm, "end": v(0.8, -6.57) * mm});
            skLineSegment(sketch, "E713", {"start": v(0.8, -6.57) * mm, "end": v(0.85, -6.57) * mm});
            skLineSegment(sketch, "E714", {"start": v(0.85, -6.57) * mm, "end": v(0.9, -6.57) * mm});
            skLineSegment(sketch, "E715", {"start": v(0.9, -6.57) * mm, "end": v(0.95, -6.57) * mm});
            skLineSegment(sketch, "E716", {"start": v(0.95, -6.57) * mm, "end": v(1, -6.57) * mm});
            skLineSegment(sketch, "E717", {"start": v(1, -6.57) * mm, "end": v(1.05, -6.57) * mm});
            skLineSegment(sketch, "E718", {"start": v(1.05, -6.57) * mm, "end": v(1.1, -6.57) * mm});
            skLineSegment(sketch, "E719", {"start": v(1.1, -6.57) * mm, "end": v(1.15, -6.57) * mm});
            skLineSegment(sketch, "E720", {"start": v(1.15, -6.57) * mm, "end": v(1.2, -6.57) * mm});
            skLineSegment(sketch, "E721", {"start": v(1.2, -6.57) * mm, "end": v(1.25, -6.57) * mm});
            skLineSegment(sketch, "E722", {"start": v(1.25, -6.57) * mm, "end": v(1.3, -6.57) * mm});
            skLineSegment(sketch, "E723", {"start": v(1.3, -6.57) * mm, "end": v(1.35, -6.57) * mm});
            skLineSegment(sketch, "E724", {"start": v(1.35, -6.57) * mm, "end": v(1.4, -6.57) * mm});
            skLineSegment(sketch, "E725", {"start": v(1.4, -6.57) * mm, "end": v(1.45, -6.57) * mm});
            skLineSegment(sketch, "E726", {"start": v(1.45, -6.57) * mm, "end": v(1.5, -6.57) * mm});
            skLineSegment(sketch, "E727", {"start": v(1.5, -6.57) * mm, "end": v(1.55, -6.57) * mm});
            skLineSegment(sketch, "E728", {"start": v(1.55, -6.57) * mm, "end": v(1.6, -6.57) * mm});
            skLineSegment(sketch, "E729", {"start": v(1.6, -6.57) * mm, "end": v(1.65, -6.57) * mm});
            skLineSegment(sketch, "E730", {"start": v(1.65, -6.57) * mm, "end": v(1.7, -6.57) * mm});
            skLineSegment(sketch, "E731", {"start": v(1.7, -6.57) * mm, "end": v(1.75, -6.57) * mm});
            skLineSegment(sketch, "E732", {"start": v(1.75, -6.57) * mm, "end": v(1.8, -6.57) * mm});
            skLineSegment(sketch, "E733", {"start": v(1.8, -6.57) * mm, "end": v(1.85, -6.57) * mm});
            skLineSegment(sketch, "E734", {"start": v(1.85, -6.57) * mm, "end": v(1.9, -6.57) * mm});
            skLineSegment(sketch, "E735", {"start": v(1.9, -6.57) * mm, "end": v(1.95, -6.57) * mm});
            skLineSegment(sketch, "E736", {"start": v(1.95, -6.57) * mm, "end": v(2, -6.57) * mm});
            skLineSegment(sketch, "E737", {"start": v(2, -6.57) * mm, "end": v(2.05, -6.57) * mm});
            skLineSegment(sketch, "E738", {"start": v(2.05, -6.57) * mm, "end": v(2.1, -6.57) * mm});
            skLineSegment(sketch, "E739", {"start": v(2.1, -6.57) * mm, "end": v(2.15, -6.57) * mm});
            skLineSegment(sketch, "E740", {"start": v(2.15, -6.57) * mm, "end": v(2.2, -6.57) * mm});
            skLineSegment(sketch, "E741", {"start": v(2.2, -6.57) * mm, "end": v(2.25, -6.57) * mm});
            skLineSegment(sketch, "E742", {"start": v(2.25, -6.57) * mm, "end": v(2.3, -6.57) * mm});
            skLineSegment(sketch, "E743", {"start": v(2.3, -6.57) * mm, "end": v(2.35, -6.57) * mm});
            skLineSegment(sketch, "E744", {"start": v(2.35, -6.57) * mm, "end": v(2.4, -6.57) * mm});
            skLineSegment(sketch, "E745", {"start": v(2.4, -6.57) * mm, "end": v(2.45, -6.57) * mm});
            skLineSegment(sketch, "E746", {"start": v(2.45, -6.57) * mm, "end": v(2.5, -6.57) * mm});
            skLineSegment(sketch, "E747", {"start": v(2.5, -6.57) * mm, "end": v(2.55, -6.57) * mm});
            skLineSegment(sketch, "E748", {"start": v(2.55, -6.57) * mm, "end": v(2.6, -6.57) * mm});
            skLineSegment(sketch, "E749", {"start": v(2.6, -6.57) * mm, "end": v(2.65, -6.57) * mm});
            skLineSegment(sketch, "E750", {"start": v(2.65, -6.57) * mm, "end": v(2.7, -6.57) * mm});
            skLineSegment(sketch, "E751", {"start": v(2.7, -6.57) * mm, "end": v(2.75, -6.57) * mm});
            skLineSegment(sketch, "E752", {"start": v(2.75, -6.57) * mm, "end": v(2.8, -6.57) * mm});
            skLineSegment(sketch, "E753", {"start": v(2.8, -6.57) * mm, "end": v(2.85, -6.57) * mm});
            skLineSegment(sketch, "E754", {"start": v(2.85, -6.57) * mm, "end": v(2.9, -6.57) * mm});
            skLineSegment(sketch, "E755", {"start": v(2.9, -6.57) * mm, "end": v(2.95, -6.57) * mm});
            skLineSegment(sketch, "E756", {"start": v(2.95, -6.57) * mm, "end": v(3, -6.57) * mm});
            skLineSegment(sketch, "E757", {"start": v(3, -6.57) * mm, "end": v(3.05, -6.57) * mm});
            skLineSegment(sketch, "E758", {"start": v(3.05, -6.57) * mm, "end": v(3.1, -6.57) * mm});
            skLineSegment(sketch, "E759", {"start": v(3.1, -6.57) * mm, "end": v(3.15, -6.57) * mm});
            skLineSegment(sketch, "E760", {"start": v(3.15, -6.57) * mm, "end": v(3.2, -6.57) * mm});
            skLineSegment(sketch, "E761", {"start": v(3.2, -6.57) * mm, "end": v(3.25, -6.57) * mm});
            skLineSegment(sketch, "E762", {"start": v(3.25, -6.57) * mm, "end": v(3.3, -6.57) * mm});
            skLineSegment(sketch, "E763", {"start": v(3.3, -6.57) * mm, "end": v(3.35, -6.57) * mm});
            skLineSegment(sketch, "E764", {"start": v(3.35, -6.57) * mm, "end": v(3.4, -6.57) * mm});
            skLineSegment(sketch, "E765", {"start": v(3.4, -6.57) * mm, "end": v(3.45, -6.57) * mm});
            skLineSegment(sketch, "E766", {"start": v(3.45, -6.57) * mm, "end": v(3.5, -6.57) * mm});
            skLineSegment(sketch, "E767", {"start": v(3.5, -6.57) * mm, "end": v(3.55, -6.57) * mm});
            skLineSegment(sketch, "E768", {"start": v(3.55, -6.57) * mm, "end": v(3.6, -6.57) * mm});
            skLineSegment(sketch, "E769", {"start": v(3.6, -6.57) * mm, "end": v(3.65, -6.57) * mm});
            skLineSegment(sketch, "E770", {"start": v(3.65, -6.57) * mm, "end": v(3.7, -6.57) * mm});
            skLineSegment(sketch, "E771", {"start": v(3.7, -6.57) * mm, "end": v(3.75, -6.57) * mm});
            skLineSegment(sketch, "E772", {"start": v(3.75, -6.57) * mm, "end": v(3.8, -6.57) * mm});
            skLineSegment(sketch, "E773", {"start": v(3.8, -6.57) * mm, "end": v(3.85, -6.57) * mm});
            skLineSegment(sketch, "E774", {"start": v(3.85, -6.57) * mm, "end": v(3.9, -6.57) * mm});
            skLineSegment(sketch, "E775", {"start": v(3.9, -6.57) * mm, "end": v(3.95, -6.57) * mm});
            skLineSegment(sketch, "E776", {"start": v(3.95, -6.57) * mm, "end": v(4, -6.57) * mm});
            skLineSegment(sketch, "E777", {"start": v(4, -6.57) * mm, "end": v(4.05, -6.57) * mm});
            skLineSegment(sketch, "E778", {"start": v(4.05, -6.57) * mm, "end": v(4.1, -6.57) * mm});
            skLineSegment(sketch, "E779", {"start": v(4.1, -6.57) * mm, "end": v(4.15, -6.57) * mm});
            skLineSegment(sketch, "E780", {"start": v(4.15, -6.57) * mm, "end": v(4.2, -6.57) * mm});
            skLineSegment(sketch, "E781", {"start": v(4.2, -6.57) * mm, "end": v(4.25, -6.57) * mm});
            skLineSegment(sketch, "E782", {"start": v(4.25, -6.57) * mm, "end": v(4.3, -6.57) * mm});
            skLineSegment(sketch, "E783", {"start": v(4.3, -6.57) * mm, "end": v(4.35, -6.57) * mm});
            skLineSegment(sketch, "E784", {"start": v(4.35, -6.57) * mm, "end": v(4.4, -6.57) * mm});
            skLineSegment(sketch, "E785", {"start": v(4.4, -6.57) * mm, "end": v(4.45, -6.57) * mm});
            skLineSegment(sketch, "E786", {"start": v(4.45, -6.57) * mm, "end": v(4.5, -6.57) * mm});
            skLineSegment(sketch, "E787", {"start": v(4.5, -6.57) * mm, "end": v(4.55, -6.57) * mm});
            skLineSegment(sketch, "E788", {"start": v(4.55, -6.57) * mm, "end": v(4.6, -6.57) * mm});
            skLineSegment(sketch, "E789", {"start": v(4.6, -6.57) * mm, "end": v(4.65, -6.57) * mm});
            skLineSegment(sketch, "E790", {"start": v(4.65, -6.57) * mm, "end": v(4.7, -6.57) * mm});
            skLineSegment(sketch, "E791", {"start": v(4.7, -6.57) * mm, "end": v(4.75, -6.57) * mm});
            skLineSegment(sketch, "E792", {"start": v(4.75, -6.57) * mm, "end": v(4.8, -6.57) * mm});
            skLineSegment(sketch, "E793", {"start": v(4.8, -6.57) * mm, "end": v(4.85, -6.57) * mm});
            skLineSegment(sketch, "E794", {"start": v(4.85, -6.57) * mm, "end": v(4.9, -6.57) * mm});
            skLineSegment(sketch, "E795", {"start": v(4.9, -6.57) * mm, "end": v(4.95, -6.57) * mm});
            skLineSegment(sketch, "E796", {"start": v(4.95, -6.57) * mm, "end": v(5, -6.57) * mm});
            skLineSegment(sketch, "E797", {"start": v(5, -6.57) * mm, "end": v(5.05, -6.57) * mm});
            skLineSegment(sketch, "E798", {"start": v(5.05, -6.57) * mm, "end": v(5.1, -6.57) * mm});
            skLineSegment(sketch, "E799", {"start": v(5.1, -6.57) * mm, "end": v(5.15, -6.57) * mm});
            skLineSegment(sketch, "E800", {"start": v(5.15, -6.57) * mm, "end": v(5.2, -6.57) * mm});
            skLineSegment(sketch, "E801", {"start": v(5.2, -6.57) * mm, "end": v(5.25, -6.57) * mm});
            skLineSegment(sketch, "E802", {"start": v(5.25, -6.57) * mm, "end": v(5.3, -6.57) * mm});
            skLineSegment(sketch, "E803", {"start": v(5.3, -6.57) * mm, "end": v(5.35, -6.57) * mm});
            skLineSegment(sketch, "E804", {"start": v(5.35, -6.57) * mm, "end": v(5.4, -6.57) * mm});
            skLineSegment(sketch, "E805", {"start": v(5.4, -6.57) * mm, "end": v(5.45, -6.57) * mm});
            skLineSegment(sketch, "E806", {"start": v(5.45, -6.57) * mm, "end": v(5.5, -6.57) * mm});
            skLineSegment(sketch, "E807", {"start": v(5.5, -6.57) * mm, "end": v(5.55, -6.57) * mm});
            skLineSegment(sketch, "E808", {"start": v(5.55, -6.57) * mm, "end": v(5.6, -6.57) * mm});
            skLineSegment(sketch, "E809", {"start": v(5.6, -6.57) * mm, "end": v(5.65, -6.57) * mm});
            skLineSegment(sketch, "E810", {"start": v(5.65, -6.57) * mm, "end": v(5.7, -6.57) * mm});
            skLineSegment(sketch, "E811", {"start": v(5.7, -6.57) * mm, "end": v(5.75, -6.57) * mm});
            skLineSegment(sketch, "E812", {"start": v(5.75, -6.57) * mm, "end": v(5.8, -6.57) * mm});
            skLineSegment(sketch, "E813", {"start": v(5.8, -6.57) * mm, "end": v(5.85, -6.57) * mm});
            skLineSegment(sketch, "E814", {"start": v(5.85, -6.57) * mm, "end": v(5.9, -6.57) * mm});
            skLineSegment(sketch, "E815", {"start": v(5.9, -6.57) * mm, "end": v(5.95, -6.57) * mm});
            skLineSegment(sketch, "E816", {"start": v(5.95, -6.57) * mm, "end": v(6, -6.57) * mm});
            skLineSegment(sketch, "E817", {"start": v(6, -6.57) * mm, "end": v(6.05, -6.57) * mm});
            skLineSegment(sketch, "E818", {"start": v(6.05, -6.57) * mm, "end": v(6.1, -6.57) * mm});
            skLineSegment(sketch, "E819", {"start": v(6.1, -6.57) * mm, "end": v(6.15, -6.57) * mm});
            skLineSegment(sketch, "E820", {"start": v(6.15, -6.57) * mm, "end": v(6.2, -6.57) * mm});
            skLineSegment(sketch, "E821", {"start": v(6.2, -6.57) * mm, "end": v(6.25, -6.57) * mm});
            skLineSegment(sketch, "E822", {"start": v(6.25, -6.57) * mm, "end": v(6.3, -6.57) * mm});
            skLineSegment(sketch, "E823", {"start": v(6.3, -6.57) * mm, "end": v(6.35, -6.57) * mm});
            skLineSegment(sketch, "E824", {"start": v(6.35, -6.57) * mm, "end": v(6.4, -6.57) * mm});
            skLineSegment(sketch, "E825", {"start": v(6.4, -6.57) * mm, "end": v(6.45, -6.57) * mm});
            skLineSegment(sketch, "E826", {"start": v(6.45, -6.57) * mm, "end": v(6.5, -6.57) * mm});
            skLineSegment(sketch, "E827", {"start": v(6.5, -6.57) * mm, "end": v(6.55, -6.57) * mm});
            skLineSegment(sketch, "E828", {"start": v(6.55, -6.57) * mm, "end": v(6.6, -6.57) * mm});
            skLineSegment(sketch, "E829", {"start": v(6.6, -6.57) * mm, "end": v(6.65, -6.57) * mm});
            skLineSegment(sketch, "E830", {"start": v(6.65, -6.57) * mm, "end": v(6.7, -6.57) * mm});
            skLineSegment(sketch, "E831", {"start": v(6.7, -6.57) * mm, "end": v(6.75, -6.57) * mm});
            skLineSegment(sketch, "E832", {"start": v(6.75, -6.57) * mm, "end": v(6.8, -6.57) * mm});
            skLineSegment(sketch, "E833", {"start": v(6.8, -6.57) * mm, "end": v(6.85, -6.57) * mm});
            skLineSegment(sketch, "E834", {"start": v(6.85, -6.57) * mm, "end": v(6.9, -6.57) * mm});
            skLineSegment(sketch, "E835", {"start": v(6.9, -6.57) * mm, "end": v(6.95, -6.57) * mm});
            skLineSegment(sketch, "E836", {"start": v(6.95, -6.57) * mm, "end": v(7.3, -6.57) * mm});
            skLineSegment(sketch, "E837", {"start": v(7.3, -6.57) * mm, "end": v(7.3, -6.38) * mm});
            skLineSegment(sketch, "E838", {"start": v(7.3, -6.38) * mm, "end": v(7.3, -6.32) * mm});
            skLineSegment(sketch, "E839", {"start": v(7.3, -6.32) * mm, "end": v(7.3, -6.27) * mm});
            skLineSegment(sketch, "E840", {"start": v(7.3, -6.27) * mm, "end": v(7.3, -6.22) * mm});
            skLineSegment(sketch, "E841", {"start": v(7.3, -6.22) * mm, "end": v(7.3, -6.17) * mm});
            skLineSegment(sketch, "E842", {"start": v(7.3, -6.17) * mm, "end": v(7.3, -6.12) * mm});
            skLineSegment(sketch, "E843", {"start": v(7.3, -6.12) * mm, "end": v(7.3, -6.07) * mm});
            skLineSegment(sketch, "E844", {"start": v(7.3, -6.07) * mm, "end": v(7.3, -6.02) * mm});
            skLineSegment(sketch, "E845", {"start": v(7.3, -6.02) * mm, "end": v(7.3, -5.97) * mm});
            skLineSegment(sketch, "E846", {"start": v(7.3, -5.97) * mm, "end": v(7.3, -5.92) * mm});
            skLineSegment(sketch, "E847", {"start": v(7.3, -5.92) * mm, "end": v(7.3, -5.87) * mm});
            skLineSegment(sketch, "E848", {"start": v(7.3, -5.87) * mm, "end": v(7.3, -5.82) * mm});
            skLineSegment(sketch, "E849", {"start": v(7.3, -5.82) * mm, "end": v(7.3, -5.77) * mm});
            skLineSegment(sketch, "E850", {"start": v(7.3, -5.77) * mm, "end": v(7.3, -5.72) * mm});
            skLineSegment(sketch, "E851", {"start": v(7.3, -5.72) * mm, "end": v(7.3, -5.67) * mm});
            skLineSegment(sketch, "E852", {"start": v(7.3, -5.67) * mm, "end": v(7.3, -5.62) * mm});
            skLineSegment(sketch, "E853", {"start": v(7.3, -5.62) * mm, "end": v(7.3, -5.57) * mm});
            skLineSegment(sketch, "E854", {"start": v(7.3, -5.57) * mm, "end": v(7.3, -5.52) * mm});
            skLineSegment(sketch, "E855", {"start": v(7.3, -5.52) * mm, "end": v(7.3, -5.47) * mm});
            skLineSegment(sketch, "E856", {"start": v(7.3, -5.47) * mm, "end": v(7.3, -5.42) * mm});
            skLineSegment(sketch, "E857", {"start": v(7.3, -5.42) * mm, "end": v(7.3, -5.38) * mm});
            skLineSegment(sketch, "E858", {"start": v(7.3, -5.38) * mm, "end": v(7.3, -5.32) * mm});
            skLineSegment(sketch, "E859", {"start": v(7.3, -5.32) * mm, "end": v(7.3, -5.27) * mm});
            skLineSegment(sketch, "E860", {"start": v(7.3, -5.27) * mm, "end": v(7.3, -5.22) * mm});
            skLineSegment(sketch, "E861", {"start": v(7.3, -5.22) * mm, "end": v(7.3, -5.17) * mm});
            skLineSegment(sketch, "E862", {"start": v(7.3, -5.17) * mm, "end": v(7.3, -5.12) * mm});
            skLineSegment(sketch, "E863", {"start": v(7.3, -5.12) * mm, "end": v(7.3, -5.07) * mm});
            skLineSegment(sketch, "E864", {"start": v(7.3, -5.07) * mm, "end": v(7.3, -5.02) * mm});
            skLineSegment(sketch, "E865", {"start": v(7.3, -5.02) * mm, "end": v(7.3, -4.97) * mm});
            skLineSegment(sketch, "E866", {"start": v(7.3, -4.97) * mm, "end": v(7.3, -4.92) * mm});
            skLineSegment(sketch, "E867", {"start": v(7.3, -4.92) * mm, "end": v(7.3, -4.87) * mm});
            skLineSegment(sketch, "E868", {"start": v(7.3, -4.87) * mm, "end": v(7.3, -4.82) * mm});
            skLineSegment(sketch, "E869", {"start": v(7.3, -4.82) * mm, "end": v(7.3, -4.77) * mm});
            skLineSegment(sketch, "E870", {"start": v(7.3, -4.77) * mm, "end": v(7.3, -4.72) * mm});
            skLineSegment(sketch, "E871", {"start": v(7.3, -4.72) * mm, "end": v(7.3, -4.67) * mm});
            skLineSegment(sketch, "E872", {"start": v(7.3, -4.67) * mm, "end": v(7.3, -4.62) * mm});
            skLineSegment(sketch, "E873", {"start": v(7.3, -4.62) * mm, "end": v(7.3, -4.57) * mm});
            skLineSegment(sketch, "E874", {"start": v(7.3, -4.57) * mm, "end": v(7.3, -4.52) * mm});
            skLineSegment(sketch, "E875", {"start": v(7.3, -4.52) * mm, "end": v(7.3, -4.47) * mm});
            skLineSegment(sketch, "E876", {"start": v(7.3, -4.47) * mm, "end": v(7.3, -4.42) * mm});
            skLineSegment(sketch, "E877", {"start": v(7.3, -4.42) * mm, "end": v(7.3, -4.37) * mm});
            skLineSegment(sketch, "E878", {"start": v(7.3, -4.37) * mm, "end": v(7.3, -4.32) * mm});
            skLineSegment(sketch, "E879", {"start": v(7.3, -4.32) * mm, "end": v(7.3, -4.27) * mm});
            skLineSegment(sketch, "E880", {"start": v(7.3, -4.27) * mm, "end": v(7.3, -4.22) * mm});
            skLineSegment(sketch, "E881", {"start": v(7.3, -4.22) * mm, "end": v(7.3, -3.87) * mm});
            skLineSegment(sketch, "E882", {"start": v(7.3, -3.87) * mm, "end": v(7.5, -3.87) * mm});
            skLineSegment(sketch, "E883", {"start": v(7.5, -3.87) * mm, "end": v(7.55, -3.87) * mm});
            skLineSegment(sketch, "E884", {"start": v(7.55, -3.87) * mm, "end": v(7.6, -3.87) * mm});
            skLineSegment(sketch, "E885", {"start": v(7.6, -3.87) * mm, "end": v(7.65, -3.87) * mm});
            skLineSegment(sketch, "E886", {"start": v(7.65, -3.87) * mm, "end": v(7.7, -3.87) * mm});
            skLineSegment(sketch, "E887", {"start": v(7.7, -3.87) * mm, "end": v(7.75, -3.87) * mm});
            skLineSegment(sketch, "E888", {"start": v(7.75, -3.87) * mm, "end": v(7.8, -3.87) * mm});
            skLineSegment(sketch, "E889", {"start": v(7.8, -3.87) * mm, "end": v(7.85, -3.87) * mm});
            skLineSegment(sketch, "E890", {"start": v(7.85, -3.87) * mm, "end": v(7.9, -3.87) * mm});
            skLineSegment(sketch, "E891", {"start": v(7.9, -3.87) * mm, "end": v(7.95, -3.87) * mm});
            skLineSegment(sketch, "E892", {"start": v(7.95, -3.87) * mm, "end": v(8, -3.87) * mm});
            skLineSegment(sketch, "E893", {"start": v(8, -3.87) * mm, "end": v(8.05, -3.87) * mm});
            skLineSegment(sketch, "E894", {"start": v(8.05, -3.87) * mm, "end": v(8.1, -3.87) * mm});
            skLineSegment(sketch, "E895", {"start": v(8.1, -3.87) * mm, "end": v(8.15, -3.87) * mm});
            skLineSegment(sketch, "E896", {"start": v(8.15, -3.87) * mm, "end": v(8.2, -3.87) * mm});
            skLineSegment(sketch, "E897", {"start": v(8.2, -3.87) * mm, "end": v(8.25, -3.87) * mm});
            skLineSegment(sketch, "E898", {"start": v(8.25, -3.87) * mm, "end": v(8.3, -3.87) * mm});
            skLineSegment(sketch, "E899", {"start": v(8.3, -3.87) * mm, "end": v(8.35, -3.87) * mm});
            skLineSegment(sketch, "E900", {"start": v(8.35, -3.87) * mm, "end": v(8.4, -3.87) * mm});
            skLineSegment(sketch, "E901", {"start": v(8.4, -3.87) * mm, "end": v(8.45, -3.87) * mm});
            skLineSegment(sketch, "E902", {"start": v(8.45, -3.87) * mm, "end": v(8.5, -3.87) * mm});
            skLineSegment(sketch, "E903", {"start": v(8.5, -3.87) * mm, "end": v(8.55, -3.87) * mm});
            skLineSegment(sketch, "E904", {"start": v(8.55, -3.87) * mm, "end": v(8.6, -3.87) * mm});
            skLineSegment(sketch, "E905", {"start": v(8.6, -3.87) * mm, "end": v(8.65, -3.87) * mm});
            skLineSegment(sketch, "E906", {"start": v(8.65, -3.87) * mm, "end": v(8.7, -3.87) * mm});
            skLineSegment(sketch, "E907", {"start": v(8.7, -3.87) * mm, "end": v(8.75, -3.87) * mm});
            skLineSegment(sketch, "E908", {"start": v(8.75, -3.87) * mm, "end": v(8.8, -3.87) * mm});
            skLineSegment(sketch, "E909", {"start": v(8.8, -3.87) * mm, "end": v(8.85, -3.87) * mm});
            skLineSegment(sketch, "E910", {"start": v(8.85, -3.87) * mm, "end": v(8.9, -3.87) * mm});
            skLineSegment(sketch, "E911", {"start": v(8.9, -3.87) * mm, "end": v(8.95, -3.87) * mm});
            skLineSegment(sketch, "E912", {"start": v(8.95, -3.87) * mm, "end": v(9, -3.87) * mm});
            skLineSegment(sketch, "E913", {"start": v(9, -3.87) * mm, "end": v(9.05, -3.87) * mm});
            skLineSegment(sketch, "E914", {"start": v(9.05, -3.87) * mm, "end": v(9.1, -3.87) * mm});
            skLineSegment(sketch, "E915", {"start": v(9.1, -3.87) * mm, "end": v(9.15, -3.87) * mm});
            skLineSegment(sketch, "E916", {"start": v(9.15, -3.87) * mm, "end": v(9.2, -3.87) * mm});
            skLineSegment(sketch, "E917", {"start": v(9.2, -3.87) * mm, "end": v(9.25, -3.87) * mm});
            skLineSegment(sketch, "E918", {"start": v(9.25, -3.87) * mm, "end": v(9.3, -3.87) * mm});
            skLineSegment(sketch, "E919", {"start": v(9.3, -3.87) * mm, "end": v(9.35, -3.87) * mm});
            skLineSegment(sketch, "E920", {"start": v(9.35, -3.87) * mm, "end": v(9.4, -3.87) * mm});
            skLineSegment(sketch, "E921", {"start": v(9.4, -3.87) * mm, "end": v(9.45, -3.87) * mm});
            skLineSegment(sketch, "E922", {"start": v(9.45, -3.87) * mm, "end": v(9.5, -3.87) * mm});
            skLineSegment(sketch, "E923", {"start": v(9.5, -3.87) * mm, "end": v(9.55, -3.87) * mm});
            skLineSegment(sketch, "E924", {"start": v(9.55, -3.87) * mm, "end": v(9.6, -3.87) * mm});
            skLineSegment(sketch, "E925", {"start": v(9.6, -3.87) * mm, "end": v(9.65, -3.87) * mm});
            skLineSegment(sketch, "E926", {"start": v(9.65, -3.87) * mm, "end": v(9.7, -3.87) * mm});
            skLineSegment(sketch, "E927", {"start": v(9.7, -3.87) * mm, "end": v(9.75, -3.87) * mm});
            skLineSegment(sketch, "E928", {"start": v(9.75, -3.87) * mm, "end": v(9.8, -3.87) * mm});
            skLineSegment(sketch, "E929", {"start": v(9.8, -3.87) * mm, "end": v(9.85, -3.87) * mm});
            skLineSegment(sketch, "E930", {"start": v(9.85, -3.87) * mm, "end": v(9.9, -3.87) * mm});
            skLineSegment(sketch, "E931", {"start": v(9.9, -3.87) * mm, "end": v(9.95, -3.87) * mm});
            skLineSegment(sketch, "E932", {"start": v(9.95, -3.87) * mm, "end": v(10, -3.87) * mm});
            skLineSegment(sketch, "E933", {"start": v(10, -3.87) * mm, "end": v(10.05, -3.87) * mm});
            skLineSegment(sketch, "E934", {"start": v(10.05, -3.87) * mm, "end": v(10.1, -3.87) * mm});
            skLineSegment(sketch, "E935", {"start": v(10.1, -3.87) * mm, "end": v(10.15, -3.87) * mm});
            skLineSegment(sketch, "E936", {"start": v(10.15, -3.87) * mm, "end": v(10.2, -3.87) * mm});
            skLineSegment(sketch, "E937", {"start": v(10.2, -3.87) * mm, "end": v(10.25, -3.87) * mm});
            skLineSegment(sketch, "E938", {"start": v(10.25, -3.87) * mm, "end": v(10.3, -3.87) * mm});
            skLineSegment(sketch, "E939", {"start": v(10.3, -3.87) * mm, "end": v(10.35, -3.87) * mm});
            skLineSegment(sketch, "E940", {"start": v(10.35, -3.87) * mm, "end": v(10.4, -3.87) * mm});
            skLineSegment(sketch, "E941", {"start": v(10.4, -3.87) * mm, "end": v(10.45, -3.87) * mm});
            skLineSegment(sketch, "E942", {"start": v(10.45, -3.87) * mm, "end": v(10.5, -3.87) * mm});
            skLineSegment(sketch, "E943", {"start": v(10.5, -3.87) * mm, "end": v(10.55, -3.87) * mm});
            skLineSegment(sketch, "E944", {"start": v(10.55, -3.87) * mm, "end": v(10.6, -3.87) * mm});
            skLineSegment(sketch, "E945", {"start": v(10.6, -3.87) * mm, "end": v(10.65, -3.87) * mm});
            skLineSegment(sketch, "E946", {"start": v(10.65, -3.87) * mm, "end": v(10.7, -3.87) * mm});
            skLineSegment(sketch, "E947", {"start": v(10.7, -3.87) * mm, "end": v(10.75, -3.87) * mm});
            skLineSegment(sketch, "E948", {"start": v(10.75, -3.87) * mm, "end": v(10.8, -3.87) * mm});
            skLineSegment(sketch, "E949", {"start": v(10.8, -3.87) * mm, "end": v(10.85, -3.87) * mm});
            skLineSegment(sketch, "E950", {"start": v(10.85, -3.87) * mm, "end": v(10.9, -3.87) * mm});
            skLineSegment(sketch, "E951", {"start": v(10.9, -3.87) * mm, "end": v(10.95, -3.87) * mm});
            skLineSegment(sketch, "E952", {"start": v(10.95, -3.87) * mm, "end": v(11, -3.87) * mm});
            skLineSegment(sketch, "E953", {"start": v(11, -3.87) * mm, "end": v(11.05, -3.87) * mm});
            skLineSegment(sketch, "E954", {"start": v(11.05, -3.87) * mm, "end": v(11.1, -3.87) * mm});
            skLineSegment(sketch, "E955", {"start": v(11.1, -3.87) * mm, "end": v(11.15, -3.87) * mm});
            skLineSegment(sketch, "E956", {"start": v(11.15, -3.87) * mm, "end": v(11.2, -3.87) * mm});
            skLineSegment(sketch, "E957", {"start": v(11.2, -3.87) * mm, "end": v(11.25, -3.87) * mm});
            skLineSegment(sketch, "E958", {"start": v(11.25, -3.87) * mm, "end": v(11.3, -3.87) * mm});
            skLineSegment(sketch, "E959", {"start": v(11.3, -3.87) * mm, "end": v(11.35, -3.87) * mm});
            skLineSegment(sketch, "E960", {"start": v(11.35, -3.87) * mm, "end": v(11.4, -3.87) * mm});
            skLineSegment(sketch, "E961", {"start": v(11.4, -3.87) * mm, "end": v(11.45, -3.87) * mm});
            skLineSegment(sketch, "E962", {"start": v(11.45, -3.87) * mm, "end": v(11.5, -3.87) * mm});
            skLineSegment(sketch, "E963", {"start": v(11.5, -3.87) * mm, "end": v(11.55, -3.87) * mm});
            skLineSegment(sketch, "E964", {"start": v(11.55, -3.87) * mm, "end": v(11.6, -3.87) * mm});
            skLineSegment(sketch, "E965", {"start": v(11.6, -3.87) * mm, "end": v(11.65, -3.87) * mm});
            skLineSegment(sketch, "E966", {"start": v(11.65, -3.87) * mm, "end": v(11.7, -3.87) * mm});
            skLineSegment(sketch, "E967", {"start": v(11.7, -3.87) * mm, "end": v(11.75, -3.87) * mm});
            skLineSegment(sketch, "E968", {"start": v(11.75, -3.87) * mm, "end": v(11.8, -3.87) * mm});
            skLineSegment(sketch, "E969", {"start": v(11.8, -3.87) * mm, "end": v(11.85, -3.87) * mm});
            skLineSegment(sketch, "E970", {"start": v(11.85, -3.87) * mm, "end": v(11.9, -3.87) * mm});
            skLineSegment(sketch, "E971", {"start": v(11.9, -3.87) * mm, "end": v(11.95, -3.87) * mm});
            skLineSegment(sketch, "E972", {"start": v(11.95, -3.87) * mm, "end": v(12, -3.87) * mm});
            skLineSegment(sketch, "E973", {"start": v(12, -3.87) * mm, "end": v(12.05, -3.87) * mm});
            skLineSegment(sketch, "E974", {"start": v(12.05, -3.87) * mm, "end": v(12.1, -3.87) * mm});
            skLineSegment(sketch, "E975", {"start": v(12.1, -3.87) * mm, "end": v(12.15, -3.87) * mm});
            skLineSegment(sketch, "E976", {"start": v(12.15, -3.87) * mm, "end": v(12.2, -3.87) * mm});
            skLineSegment(sketch, "E977", {"start": v(12.2, -3.87) * mm, "end": v(12.25, -3.87) * mm});
            skLineSegment(sketch, "E978", {"start": v(12.25, -3.87) * mm, "end": v(12.3, -3.87) * mm});
            skLineSegment(sketch, "E979", {"start": v(12.3, -3.87) * mm, "end": v(12.35, -3.87) * mm});
            skLineSegment(sketch, "E980", {"start": v(12.35, -3.87) * mm, "end": v(12.4, -3.87) * mm});
            skLineSegment(sketch, "E981", {"start": v(12.4, -3.87) * mm, "end": v(12.45, -3.87) * mm});
            skLineSegment(sketch, "E982", {"start": v(12.45, -3.87) * mm, "end": v(12.5, -3.87) * mm});
            skLineSegment(sketch, "E983", {"start": v(12.5, -3.87) * mm, "end": v(12.55, -3.87) * mm});
            skLineSegment(sketch, "E984", {"start": v(12.55, -3.87) * mm, "end": v(12.6, -3.87) * mm});
            skLineSegment(sketch, "E985", {"start": v(12.6, -3.87) * mm, "end": v(12.65, -3.87) * mm});
            skLineSegment(sketch, "E986", {"start": v(12.65, -3.87) * mm, "end": v(12.7, -3.87) * mm});
            skLineSegment(sketch, "E987", {"start": v(12.7, -3.87) * mm, "end": v(12.75, -3.87) * mm});
            skLineSegment(sketch, "E988", {"start": v(12.75, -3.87) * mm, "end": v(12.8, -3.87) * mm});
            skLineSegment(sketch, "E989", {"start": v(12.8, -3.87) * mm, "end": v(12.85, -3.87) * mm});
            skLineSegment(sketch, "E990", {"start": v(12.85, -3.87) * mm, "end": v(12.9, -3.87) * mm});
            skLineSegment(sketch, "E991", {"start": v(12.9, -3.87) * mm, "end": v(12.95, -3.87) * mm});
            skLineSegment(sketch, "E992", {"start": v(12.95, -3.87) * mm, "end": v(13, -3.87) * mm});
            skLineSegment(sketch, "E993", {"start": v(13, -3.87) * mm, "end": v(13.05, -3.87) * mm});
            skLineSegment(sketch, "E994", {"start": v(13.05, -3.87) * mm, "end": v(13.1, -3.87) * mm});
            skLineSegment(sketch, "E995", {"start": v(13.1, -3.87) * mm, "end": v(13.15, -3.87) * mm});
            skLineSegment(sketch, "E996", {"start": v(13.15, -3.87) * mm, "end": v(13.2, -3.87) * mm});
            skLineSegment(sketch, "E997", {"start": v(13.2, -3.87) * mm, "end": v(13.25, -3.87) * mm});
            skLineSegment(sketch, "E998", {"start": v(13.25, -3.87) * mm, "end": v(13.3, -3.87) * mm});
            skLineSegment(sketch, "E999", {"start": v(13.3, -3.87) * mm, "end": v(13.35, -3.87) * mm});
            skLineSegment(sketch, "E1000", {"start": v(13.35, -3.87) * mm, "end": v(13.4, -3.87) * mm});
            skLineSegment(sketch, "E1001", {"start": v(13.4, -3.87) * mm, "end": v(13.45, -3.87) * mm});
            skLineSegment(sketch, "E1002", {"start": v(13.45, -3.87) * mm, "end": v(13.5, -3.87) * mm});
            skLineSegment(sketch, "E1003", {"start": v(13.5, -3.87) * mm, "end": v(13.55, -3.87) * mm});
            skLineSegment(sketch, "E1004", {"start": v(13.55, -3.87) * mm, "end": v(13.6, -3.87) * mm});
            skLineSegment(sketch, "E1005", {"start": v(13.6, -3.87) * mm, "end": v(13.65, -3.87) * mm});
            skLineSegment(sketch, "E1006", {"start": v(13.65, -3.87) * mm, "end": v(13.7, -3.87) * mm});
            skLineSegment(sketch, "E1007", {"start": v(13.7, -3.87) * mm, "end": v(13.75, -3.87) * mm});
            skLineSegment(sketch, "E1008", {"start": v(13.75, -3.87) * mm, "end": v(13.8, -3.87) * mm});
            skLineSegment(sketch, "E1009", {"start": v(13.8, -3.87) * mm, "end": v(13.85, -3.87) * mm});
            skLineSegment(sketch, "E1010", {"start": v(13.85, -3.87) * mm, "end": v(13.9, -3.87) * mm});
            skLineSegment(sketch, "E1011", {"start": v(13.9, -3.87) * mm, "end": v(13.95, -3.87) * mm});
            skLineSegment(sketch, "E1012", {"start": v(13.95, -3.87) * mm, "end": v(14, -3.87) * mm});
            skLineSegment(sketch, "E1013", {"start": v(14, -3.87) * mm, "end": v(14.05, -3.87) * mm});
            skLineSegment(sketch, "E1014", {"start": v(14.05, -3.87) * mm, "end": v(14.1, -3.87) * mm});
            skLineSegment(sketch, "E1015", {"start": v(14.1, -3.87) * mm, "end": v(14.15, -3.87) * mm});
            skLineSegment(sketch, "E1016", {"start": v(14.15, -3.87) * mm, "end": v(14.2, -3.87) * mm});
            skLineSegment(sketch, "E1017", {"start": v(14.2, -3.87) * mm, "end": v(14.25, -3.87) * mm});
            skLineSegment(sketch, "E1018", {"start": v(14.25, -3.87) * mm, "end": v(14.3, -3.87) * mm});
            skLineSegment(sketch, "E1019", {"start": v(14.3, -3.87) * mm, "end": v(14.35, -3.87) * mm});
            skLineSegment(sketch, "E1020", {"start": v(14.35, -3.87) * mm, "end": v(14.4, -3.87) * mm});
            skLineSegment(sketch, "E1021", {"start": v(14.4, -3.87) * mm, "end": v(14.45, -3.87) * mm});
            skLineSegment(sketch, "E1022", {"start": v(14.45, -3.87) * mm, "end": v(14.5, -3.87) * mm});
            skLineSegment(sketch, "E1023", {"start": v(14.5, -3.87) * mm, "end": v(14.55, -3.87) * mm});
            skLineSegment(sketch, "E1024", {"start": v(14.55, -3.87) * mm, "end": v(14.6, -3.87) * mm});
            skLineSegment(sketch, "E1025", {"start": v(14.6, -3.87) * mm, "end": v(14.65, -3.87) * mm});
            skLineSegment(sketch, "E1026", {"start": v(14.65, -3.87) * mm, "end": v(14.7, -3.87) * mm});
            skLineSegment(sketch, "E1027", {"start": v(14.7, -3.87) * mm, "end": v(14.75, -3.87) * mm});
            skLineSegment(sketch, "E1028", {"start": v(14.75, -3.87) * mm, "end": v(14.8, -3.87) * mm});
            skLineSegment(sketch, "E1029", {"start": v(14.8, -3.87) * mm, "end": v(14.85, -3.87) * mm});
            skLineSegment(sketch, "E1030", {"start": v(14.85, -3.87) * mm, "end": v(14.9, -3.87) * mm});
            skLineSegment(sketch, "E1031", {"start": v(14.9, -3.87) * mm, "end": v(14.95, -3.87) * mm});
            skLineSegment(sketch, "E1032", {"start": v(14.95, -3.87) * mm, "end": v(15, -3.87) * mm});
            skLineSegment(sketch, "E1033", {"start": v(15, -3.87) * mm, "end": v(15.05, -3.87) * mm});
            skLineSegment(sketch, "E1034", {"start": v(15.05, -3.87) * mm, "end": v(15.1, -3.87) * mm});
            skLineSegment(sketch, "E1035", {"start": v(15.1, -3.87) * mm, "end": v(15.15, -3.87) * mm});
            skLineSegment(sketch, "E1036", {"start": v(15.15, -3.87) * mm, "end": v(15.2, -3.87) * mm});
            skLineSegment(sketch, "E1037", {"start": v(15.2, -3.87) * mm, "end": v(15.25, -3.87) * mm});
            skLineSegment(sketch, "E1038", {"start": v(15.25, -3.87) * mm, "end": v(15.3, -3.87) * mm});
            skLineSegment(sketch, "E1039", {"start": v(15.3, -3.87) * mm, "end": v(15.35, -3.87) * mm});
            skLineSegment(sketch, "E1040", {"start": v(15.35, -3.87) * mm, "end": v(15.4, -3.87) * mm});
            skLineSegment(sketch, "E1041", {"start": v(15.4, -3.87) * mm, "end": v(15.45, -3.87) * mm});
            skLineSegment(sketch, "E1042", {"start": v(15.45, -3.87) * mm, "end": v(15.7, -3.87) * mm});
            skLineSegment(sketch, "E1043", {"start": v(15.7, -3.87) * mm, "end": v(15.85, -3.67) * mm});
            skLineSegment(sketch, "E1044", {"start": v(15.85, -3.67) * mm, "end": v(15.85, -3.52) * mm});
            skLineSegment(sketch, "E1045", {"start": v(15.85, -3.52) * mm, "end": v(15.95, -3.47) * mm});
            skLineSegment(sketch, "E1046", {"start": v(15.95, -3.47) * mm, "end": v(16, -3.22) * mm});
            skLineSegment(sketch, "E1047", {"start": v(16, -3.22) * mm, "end": v(16.15, -2.92) * mm});
            skLineSegment(sketch, "E1048", {"start": v(16.15, -2.92) * mm, "end": v(16.25, -2.87) * mm});
            skLineSegment(sketch, "E1049", {"start": v(16.25, -2.87) * mm, "end": v(16.25, -2.72) * mm});
            skLineSegment(sketch, "E1050", {"start": v(16.25, -2.72) * mm, "end": v(16.4, -2.42) * mm});
            skLineSegment(sketch, "E1051", {"start": v(16.4, -2.42) * mm, "end": v(16.55, -2.12) * mm});
            skLineSegment(sketch, "E1052", {"start": v(16.55, -2.12) * mm, "end": v(16.65, -2.07) * mm});
            skLineSegment(sketch, "E1053", {"start": v(16.65, -2.07) * mm, "end": v(16.65, -1.92) * mm});
            skLineSegment(sketch, "E1054", {"start": v(16.65, -1.92) * mm, "end": v(16.8, -1.62) * mm});
            skLineSegment(sketch, "E1055", {"start": v(16.8, -1.62) * mm, "end": v(16.9, -1.62) * mm});
            skLineSegment(sketch, "E1056", {"start": v(16.9, -1.62) * mm, "end": v(17.05, -1.32) * mm});
            skLineSegment(sketch, "E1057", {"start": v(17.05, -1.32) * mm, "end": v(17.1, -1.07) * mm});
            skLineSegment(sketch, "E1058", {"start": v(17.1, -1.07) * mm, "end": v(17.15, -1.07) * mm});
            skLineSegment(sketch, "E1059", {"start": v(17.15, -1.07) * mm, "end": v(17.2, -0.82) * mm});
            skLineSegment(sketch, "E1060", {"start": v(17.2, -0.82) * mm, "end": v(17.3, -0.82) * mm});
            skLineSegment(sketch, "E1061", {"start": v(17.3, -0.82) * mm, "end": v(17.45, -0.52) * mm});
            skLineSegment(sketch, "E1062", {"start": v(17.45, -0.52) * mm, "end": v(17.5, -0.27) * mm});
            skLineSegment(sketch, "E1063", {"start": v(17.5, -0.27) * mm, "end": v(17.55, -0.27) * mm});
            skLineSegment(sketch, "E1064", {"start": v(17.55, -0.27) * mm, "end": v(17.6, -0.02) * mm});
            skLineSegment(sketch, "E1065", {"start": v(17.6, -0.02) * mm, "end": v(17.7, -0.02) * mm});
            skLineSegment(sketch, "E1066", {"start": v(17.7, -0.02) * mm, "end": v(17.85, 0.28) * mm});
            skLineSegment(sketch, "E1067", {"start": v(17.85, 0.28) * mm, "end": v(17.85, 0.43) * mm});
            skLineSegment(sketch, "E1068", {"start": v(17.85, 0.43) * mm, "end": v(18, 0.58) * mm});
            skLineSegment(sketch, "E1069", {"start": v(18, 0.58) * mm, "end": v(18, 0.78) * mm});
            skLineSegment(sketch, "E1070", {"start": v(18, 0.78) * mm, "end": v(18.25, 1.08) * mm});
            skLineSegment(sketch, "E1071", {"start": v(18.25, 1.08) * mm, "end": v(18.25, 1.23) * mm});
            skLineSegment(sketch, "E1072", {"start": v(18.25, 1.23) * mm, "end": v(18.35, 1.28) * mm});
            skLineSegment(sketch, "E1073", {"start": v(18.35, 1.28) * mm, "end": v(18.4, 1.53) * mm});
            skLineSegment(sketch, "E1074", {"start": v(18.4, 1.53) * mm, "end": v(18.55, 1.83) * mm});
            skLineSegment(sketch, "E1075", {"start": v(18.55, 1.83) * mm, "end": v(18.65, 1.97) * mm});
            skLineSegment(sketch, "E1076", {"start": v(18.65, 1.98) * mm, "end": v(18.7, 1.98) * mm});
            skLineSegment(sketch, "E1077", {"start": v(18.7, 1.98) * mm, "end": v(18.7, 2.08) * mm});
            skLineSegment(sketch, "E1078", {"start": v(18.7, 2.08) * mm, "end": v(18.8, 2.32) * mm});
            skLineSegment(sketch, "E1079", {"start": v(18.8, 2.33) * mm, "end": v(18.95, 2.63) * mm});
            skLineSegment(sketch, "E1080", {"start": v(18.95, 2.63) * mm, "end": v(19.05, 2.63) * mm});
            skLineSegment(sketch, "E1081", {"start": v(19.05, 2.63) * mm, "end": v(19.2, 2.93) * mm});
            skLineSegment(sketch, "E1082", {"start": v(19.2, 2.93) * mm, "end": v(19.2, 3.12) * mm});
            skLineSegment(sketch, "E1083", {"start": v(19.2, 3.12) * mm, "end": v(19.35, 3.43) * mm});
            skLineSegment(sketch, "E1084", {"start": v(19.35, 3.43) * mm, "end": v(19.45, 3.43) * mm});
            skLineSegment(sketch, "E1085", {"start": v(19.45, 3.43) * mm, "end": v(19.6, 3.73) * mm});
            skLineSegment(sketch, "E1086", {"start": v(19.6, 3.73) * mm, "end": v(19.65, 3.98) * mm});
            skLineSegment(sketch, "E1087", {"start": v(19.65, 3.98) * mm, "end": v(19.7, 3.98) * mm});
            skLineSegment(sketch, "E1088", {"start": v(19.7, 3.98) * mm, "end": v(19.7, 4.08) * mm});
            skLineSegment(sketch, "E1089", {"start": v(19.7, 4.08) * mm, "end": v(19.85, 4.23) * mm});
            skLineSegment(sketch, "E1090", {"start": v(19.85, 4.22) * mm, "end": v(20, 4.68) * mm});
            skLineSegment(sketch, "E1091", {"start": v(20, 4.68) * mm, "end": v(19.8, 4.68) * mm});
            skLineSegment(sketch, "E1092", {"start": v(19.8, 4.68) * mm, "end": v(19.75, 4.68) * mm});
            skLineSegment(sketch, "E1093", {"start": v(19.75, 4.68) * mm, "end": v(19.7, 4.68) * mm});
            skLineSegment(sketch, "E1094", {"start": v(19.7, 4.68) * mm, "end": v(19.65, 4.68) * mm});
            skLineSegment(sketch, "E1095", {"start": v(19.65, 4.68) * mm, "end": v(19.6, 4.68) * mm});
            skLineSegment(sketch, "E1096", {"start": v(19.6, 4.68) * mm, "end": v(19.55, 4.68) * mm});
            skLineSegment(sketch, "E1097", {"start": v(19.55, 4.68) * mm, "end": v(19.5, 4.68) * mm});
            skLineSegment(sketch, "E1098", {"start": v(19.5, 4.68) * mm, "end": v(19.45, 4.68) * mm});
            skLineSegment(sketch, "E1099", {"start": v(19.45, 4.68) * mm, "end": v(19.4, 4.68) * mm});
            skLineSegment(sketch, "E1100", {"start": v(19.4, 4.68) * mm, "end": v(19.35, 4.68) * mm});
            skLineSegment(sketch, "E1101", {"start": v(19.35, 4.68) * mm, "end": v(19.3, 4.68) * mm});
            skLineSegment(sketch, "E1102", {"start": v(19.3, 4.68) * mm, "end": v(19.25, 4.68) * mm});
            skLineSegment(sketch, "E1103", {"start": v(19.25, 4.68) * mm, "end": v(19.2, 4.68) * mm});
            skLineSegment(sketch, "E1104", {"start": v(19.2, 4.68) * mm, "end": v(19.15, 4.68) * mm});
            skLineSegment(sketch, "E1105", {"start": v(19.15, 4.68) * mm, "end": v(19.1, 4.68) * mm});
            skLineSegment(sketch, "E1106", {"start": v(19.1, 4.68) * mm, "end": v(19.05, 4.68) * mm});
            skLineSegment(sketch, "E1107", {"start": v(19.05, 4.68) * mm, "end": v(19, 4.68) * mm});
            skLineSegment(sketch, "E1108", {"start": v(19, 4.68) * mm, "end": v(18.95, 4.68) * mm});
            skLineSegment(sketch, "E1109", {"start": v(18.95, 4.68) * mm, "end": v(18.9, 4.68) * mm});
            skLineSegment(sketch, "E1110", {"start": v(18.9, 4.68) * mm, "end": v(18.85, 4.68) * mm});
            skLineSegment(sketch, "E1111", {"start": v(18.85, 4.68) * mm, "end": v(18.8, 4.68) * mm});
            skLineSegment(sketch, "E1112", {"start": v(18.8, 4.68) * mm, "end": v(18.75, 4.68) * mm});
            skLineSegment(sketch, "E1113", {"start": v(18.75, 4.68) * mm, "end": v(18.7, 4.68) * mm});
            skLineSegment(sketch, "E1114", {"start": v(18.7, 4.68) * mm, "end": v(18.65, 4.68) * mm});
            skLineSegment(sketch, "E1115", {"start": v(18.65, 4.68) * mm, "end": v(18.6, 4.68) * mm});
            skLineSegment(sketch, "E1116", {"start": v(18.6, 4.68) * mm, "end": v(18.55, 4.68) * mm});
            skLineSegment(sketch, "E1117", {"start": v(18.55, 4.68) * mm, "end": v(18.5, 4.68) * mm});
            skLineSegment(sketch, "E1118", {"start": v(18.5, 4.68) * mm, "end": v(18.45, 4.68) * mm});
            skLineSegment(sketch, "E1119", {"start": v(18.45, 4.68) * mm, "end": v(18.4, 4.68) * mm});
            skLineSegment(sketch, "E1120", {"start": v(18.4, 4.68) * mm, "end": v(18.35, 4.68) * mm});
            skLineSegment(sketch, "E1121", {"start": v(18.35, 4.68) * mm, "end": v(18.3, 4.68) * mm});
            skLineSegment(sketch, "E1122", {"start": v(18.3, 4.68) * mm, "end": v(18.25, 4.68) * mm});
            skLineSegment(sketch, "E1123", {"start": v(18.25, 4.68) * mm, "end": v(18.2, 4.68) * mm});
            skLineSegment(sketch, "E1124", {"start": v(18.2, 4.68) * mm, "end": v(18.15, 4.68) * mm});
            skLineSegment(sketch, "E1125", {"start": v(18.15, 4.68) * mm, "end": v(18.1, 4.68) * mm});
            skLineSegment(sketch, "E1126", {"start": v(18.1, 4.68) * mm, "end": v(18.05, 4.68) * mm});
            skLineSegment(sketch, "E1127", {"start": v(18.05, 4.68) * mm, "end": v(18, 4.68) * mm});
            skLineSegment(sketch, "E1128", {"start": v(18, 4.68) * mm, "end": v(17.95, 4.68) * mm});
            skLineSegment(sketch, "E1129", {"start": v(17.95, 4.68) * mm, "end": v(17.9, 4.68) * mm});
            skLineSegment(sketch, "E1130", {"start": v(17.9, 4.68) * mm, "end": v(17.85, 4.68) * mm});
            skLineSegment(sketch, "E1131", {"start": v(17.85, 4.68) * mm, "end": v(17.8, 4.68) * mm});
            skLineSegment(sketch, "E1132", {"start": v(17.8, 4.68) * mm, "end": v(17.75, 4.68) * mm});
            skLineSegment(sketch, "E1133", {"start": v(17.75, 4.68) * mm, "end": v(17.7, 4.68) * mm});
            skLineSegment(sketch, "E1134", {"start": v(17.7, 4.68) * mm, "end": v(17.65, 4.68) * mm});
            skLineSegment(sketch, "E1135", {"start": v(17.65, 4.68) * mm, "end": v(17.6, 4.68) * mm});
            skLineSegment(sketch, "E1136", {"start": v(17.6, 4.68) * mm, "end": v(17.55, 4.68) * mm});
            skLineSegment(sketch, "E1137", {"start": v(17.55, 4.68) * mm, "end": v(17.5, 4.68) * mm});
            skLineSegment(sketch, "E1138", {"start": v(17.5, 4.68) * mm, "end": v(17.45, 4.68) * mm});
            skLineSegment(sketch, "E1139", {"start": v(17.45, 4.68) * mm, "end": v(17.4, 4.68) * mm});
            skLineSegment(sketch, "E1140", {"start": v(17.4, 4.68) * mm, "end": v(17.35, 4.68) * mm});
            skLineSegment(sketch, "E1141", {"start": v(17.35, 4.68) * mm, "end": v(17.3, 4.68) * mm});
            skLineSegment(sketch, "E1142", {"start": v(17.3, 4.68) * mm, "end": v(17.25, 4.68) * mm});
            skLineSegment(sketch, "E1143", {"start": v(17.25, 4.68) * mm, "end": v(17.2, 4.68) * mm});
            skLineSegment(sketch, "E1144", {"start": v(17.2, 4.68) * mm, "end": v(17.15, 4.68) * mm});
            skLineSegment(sketch, "E1145", {"start": v(17.15, 4.68) * mm, "end": v(17.1, 4.68) * mm});
            skLineSegment(sketch, "E1146", {"start": v(17.1, 4.68) * mm, "end": v(17.05, 4.68) * mm});
            skLineSegment(sketch, "E1147", {"start": v(17.05, 4.68) * mm, "end": v(17, 4.68) * mm});
            skLineSegment(sketch, "E1148", {"start": v(17, 4.68) * mm, "end": v(16.95, 4.68) * mm});
            skLineSegment(sketch, "E1149", {"start": v(16.95, 4.68) * mm, "end": v(16.9, 4.68) * mm});
            skLineSegment(sketch, "E1150", {"start": v(16.9, 4.68) * mm, "end": v(16.85, 4.68) * mm});
            skLineSegment(sketch, "E1151", {"start": v(16.85, 4.68) * mm, "end": v(16.8, 4.68) * mm});
            skLineSegment(sketch, "E1152", {"start": v(16.8, 4.68) * mm, "end": v(16.75, 4.68) * mm});
            skLineSegment(sketch, "E1153", {"start": v(16.75, 4.68) * mm, "end": v(16.7, 4.68) * mm});
            skLineSegment(sketch, "E1154", {"start": v(16.7, 4.68) * mm, "end": v(16.65, 4.68) * mm});
            skLineSegment(sketch, "E1155", {"start": v(16.65, 4.68) * mm, "end": v(16.6, 4.68) * mm});
            skLineSegment(sketch, "E1156", {"start": v(16.6, 4.68) * mm, "end": v(16.55, 4.68) * mm});
            skLineSegment(sketch, "E1157", {"start": v(16.55, 4.68) * mm, "end": v(16.5, 4.68) * mm});
            skLineSegment(sketch, "E1158", {"start": v(16.5, 4.68) * mm, "end": v(16.45, 4.68) * mm});
            skLineSegment(sketch, "E1159", {"start": v(16.45, 4.68) * mm, "end": v(16.4, 4.68) * mm});
            skLineSegment(sketch, "E1160", {"start": v(16.4, 4.68) * mm, "end": v(16.35, 4.68) * mm});
            skLineSegment(sketch, "E1161", {"start": v(16.35, 4.68) * mm, "end": v(16.3, 4.68) * mm});
            skLineSegment(sketch, "E1162", {"start": v(16.3, 4.68) * mm, "end": v(16.25, 4.68) * mm});
            skLineSegment(sketch, "E1163", {"start": v(16.25, 4.68) * mm, "end": v(16.2, 4.68) * mm});
            skLineSegment(sketch, "E1164", {"start": v(16.2, 4.68) * mm, "end": v(16.15, 4.68) * mm});
            skLineSegment(sketch, "E1165", {"start": v(16.15, 4.68) * mm, "end": v(16.1, 4.68) * mm});
            skLineSegment(sketch, "E1166", {"start": v(16.1, 4.68) * mm, "end": v(16.05, 4.68) * mm});
            skLineSegment(sketch, "E1167", {"start": v(16.05, 4.68) * mm, "end": v(16, 4.68) * mm});
            skLineSegment(sketch, "E1168", {"start": v(16, 4.68) * mm, "end": v(15.95, 4.68) * mm});
            skLineSegment(sketch, "E1169", {"start": v(15.95, 4.68) * mm, "end": v(15.9, 4.68) * mm});
            skLineSegment(sketch, "E1170", {"start": v(15.9, 4.68) * mm, "end": v(15.85, 4.68) * mm});
            skLineSegment(sketch, "E1171", {"start": v(15.85, 4.68) * mm, "end": v(15.8, 4.68) * mm});
            skLineSegment(sketch, "E1172", {"start": v(15.8, 4.68) * mm, "end": v(15.75, 4.68) * mm});
            skLineSegment(sketch, "E1173", {"start": v(15.75, 4.68) * mm, "end": v(15.7, 4.68) * mm});
            skLineSegment(sketch, "E1174", {"start": v(15.7, 4.68) * mm, "end": v(15.65, 4.68) * mm});
            skLineSegment(sketch, "E1175", {"start": v(15.65, 4.68) * mm, "end": v(15.6, 4.68) * mm});
            skLineSegment(sketch, "E1176", {"start": v(15.6, 4.68) * mm, "end": v(15.55, 4.68) * mm});
            skLineSegment(sketch, "E1177", {"start": v(15.55, 4.68) * mm, "end": v(15.5, 4.68) * mm});
            skLineSegment(sketch, "E1178", {"start": v(15.5, 4.68) * mm, "end": v(15.45, 4.68) * mm});
            skLineSegment(sketch, "E1179", {"start": v(15.45, 4.68) * mm, "end": v(15.4, 4.68) * mm});
            skLineSegment(sketch, "E1180", {"start": v(15.4, 4.68) * mm, "end": v(15.35, 4.68) * mm});
            skLineSegment(sketch, "E1181", {"start": v(15.35, 4.68) * mm, "end": v(15.3, 4.68) * mm});
            skLineSegment(sketch, "E1182", {"start": v(15.3, 4.68) * mm, "end": v(15.25, 4.68) * mm});
            skLineSegment(sketch, "E1183", {"start": v(15.25, 4.68) * mm, "end": v(15.2, 4.68) * mm});
            skLineSegment(sketch, "E1184", {"start": v(15.2, 4.68) * mm, "end": v(15.15, 4.68) * mm});
            skLineSegment(sketch, "E1185", {"start": v(15.15, 4.68) * mm, "end": v(15.1, 4.68) * mm});
            skLineSegment(sketch, "E1186", {"start": v(15.1, 4.68) * mm, "end": v(15.05, 4.68) * mm});
            skLineSegment(sketch, "E1187", {"start": v(15.05, 4.68) * mm, "end": v(15, 4.68) * mm});
            skLineSegment(sketch, "E1188", {"start": v(15, 4.68) * mm, "end": v(14.95, 4.68) * mm});
            skLineSegment(sketch, "E1189", {"start": v(14.95, 4.68) * mm, "end": v(14.9, 4.68) * mm});
            skLineSegment(sketch, "E1190", {"start": v(14.9, 4.68) * mm, "end": v(14.85, 4.68) * mm});
            skLineSegment(sketch, "E1191", {"start": v(14.85, 4.68) * mm, "end": v(14.8, 4.68) * mm});
            skLineSegment(sketch, "E1192", {"start": v(14.8, 4.68) * mm, "end": v(14.75, 4.68) * mm});
            skLineSegment(sketch, "E1193", {"start": v(14.75, 4.68) * mm, "end": v(14.7, 4.68) * mm});
            skLineSegment(sketch, "E1194", {"start": v(14.7, 4.68) * mm, "end": v(14.65, 4.68) * mm});
            skLineSegment(sketch, "E1195", {"start": v(14.65, 4.68) * mm, "end": v(14.6, 4.68) * mm});
            skLineSegment(sketch, "E1196", {"start": v(14.6, 4.68) * mm, "end": v(14.55, 4.68) * mm});
            skLineSegment(sketch, "E1197", {"start": v(14.55, 4.68) * mm, "end": v(14.5, 4.68) * mm});
            skLineSegment(sketch, "E1198", {"start": v(14.5, 4.68) * mm, "end": v(14.45, 4.68) * mm});
            skLineSegment(sketch, "E1199", {"start": v(14.45, 4.68) * mm, "end": v(14.4, 4.68) * mm});
            skLineSegment(sketch, "E1200", {"start": v(14.4, 4.68) * mm, "end": v(14.35, 4.68) * mm});
            skLineSegment(sketch, "E1201", {"start": v(14.35, 4.68) * mm, "end": v(14.3, 4.68) * mm});
            skLineSegment(sketch, "E1202", {"start": v(14.3, 4.68) * mm, "end": v(14.25, 4.68) * mm});
            skLineSegment(sketch, "E1203", {"start": v(14.25, 4.68) * mm, "end": v(14.2, 4.68) * mm});
            skLineSegment(sketch, "E1204", {"start": v(14.2, 4.68) * mm, "end": v(14.15, 4.68) * mm});
            skLineSegment(sketch, "E1205", {"start": v(14.15, 4.68) * mm, "end": v(14.1, 4.68) * mm});
            skLineSegment(sketch, "E1206", {"start": v(14.1, 4.68) * mm, "end": v(14.05, 4.68) * mm});
            skLineSegment(sketch, "E1207", {"start": v(14.05, 4.68) * mm, "end": v(14, 4.68) * mm});
            skLineSegment(sketch, "E1208", {"start": v(14, 4.68) * mm, "end": v(13.95, 4.68) * mm});
            skLineSegment(sketch, "E1209", {"start": v(13.95, 4.68) * mm, "end": v(13.9, 4.68) * mm});
            skLineSegment(sketch, "E1210", {"start": v(13.9, 4.68) * mm, "end": v(13.85, 4.68) * mm});
            skLineSegment(sketch, "E1211", {"start": v(13.85, 4.68) * mm, "end": v(13.8, 4.68) * mm});
            skLineSegment(sketch, "E1212", {"start": v(13.8, 4.68) * mm, "end": v(13.75, 4.68) * mm});
            skLineSegment(sketch, "E1213", {"start": v(13.75, 4.68) * mm, "end": v(13.7, 4.68) * mm});
            skLineSegment(sketch, "E1214", {"start": v(13.7, 4.68) * mm, "end": v(13.65, 4.68) * mm});
            skLineSegment(sketch, "E1215", {"start": v(13.65, 4.68) * mm, "end": v(13.6, 4.68) * mm});
            skLineSegment(sketch, "E1216", {"start": v(13.6, 4.68) * mm, "end": v(13.55, 4.68) * mm});
            skLineSegment(sketch, "E1217", {"start": v(13.55, 4.68) * mm, "end": v(13.5, 4.68) * mm});
            skLineSegment(sketch, "E1218", {"start": v(13.5, 4.68) * mm, "end": v(13.45, 4.68) * mm});
            skLineSegment(sketch, "E1219", {"start": v(13.45, 4.68) * mm, "end": v(13.4, 4.68) * mm});
            skLineSegment(sketch, "E1220", {"start": v(13.4, 4.68) * mm, "end": v(13.35, 4.68) * mm});
            skLineSegment(sketch, "E1221", {"start": v(13.35, 4.68) * mm, "end": v(13.3, 4.68) * mm});
            skLineSegment(sketch, "E1222", {"start": v(13.3, 4.68) * mm, "end": v(13.25, 4.68) * mm});
            skLineSegment(sketch, "E1223", {"start": v(13.25, 4.68) * mm, "end": v(13.2, 4.68) * mm});
            skLineSegment(sketch, "E1224", {"start": v(13.2, 4.68) * mm, "end": v(13.15, 4.68) * mm});
            skLineSegment(sketch, "E1225", {"start": v(13.15, 4.68) * mm, "end": v(13.1, 4.68) * mm});
            skLineSegment(sketch, "E1226", {"start": v(13.1, 4.68) * mm, "end": v(13.05, 4.68) * mm});
            skLineSegment(sketch, "E1227", {"start": v(13.05, 4.68) * mm, "end": v(13, 4.68) * mm});
            skLineSegment(sketch, "E1228", {"start": v(13, 4.68) * mm, "end": v(12.95, 4.68) * mm});
            skLineSegment(sketch, "E1229", {"start": v(12.95, 4.68) * mm, "end": v(12.9, 4.68) * mm});
            skLineSegment(sketch, "E1230", {"start": v(12.9, 4.68) * mm, "end": v(12.85, 4.68) * mm});
            skLineSegment(sketch, "E1231", {"start": v(12.85, 4.68) * mm, "end": v(12.8, 4.68) * mm});
            skLineSegment(sketch, "E1232", {"start": v(12.8, 4.68) * mm, "end": v(12.75, 4.68) * mm});
            skLineSegment(sketch, "E1233", {"start": v(12.75, 4.68) * mm, "end": v(12.7, 4.68) * mm});
            skLineSegment(sketch, "E1234", {"start": v(12.7, 4.68) * mm, "end": v(12.65, 4.68) * mm});
            skLineSegment(sketch, "E1235", {"start": v(12.65, 4.68) * mm, "end": v(12.6, 4.68) * mm});
            skLineSegment(sketch, "E1236", {"start": v(12.6, 4.68) * mm, "end": v(12.55, 4.68) * mm});
            skLineSegment(sketch, "E1237", {"start": v(12.55, 4.68) * mm, "end": v(12.5, 4.68) * mm});
            skLineSegment(sketch, "E1238", {"start": v(12.5, 4.68) * mm, "end": v(12.45, 4.68) * mm});
            skLineSegment(sketch, "E1239", {"start": v(12.45, 4.68) * mm, "end": v(12.4, 4.68) * mm});
            skLineSegment(sketch, "E1240", {"start": v(12.4, 4.68) * mm, "end": v(12.35, 4.68) * mm});
            skLineSegment(sketch, "E1241", {"start": v(12.35, 4.68) * mm, "end": v(12.3, 4.68) * mm});
            skLineSegment(sketch, "E1242", {"start": v(12.3, 4.68) * mm, "end": v(12.25, 4.68) * mm});
            skLineSegment(sketch, "E1243", {"start": v(12.25, 4.68) * mm, "end": v(12.2, 4.68) * mm});
            skLineSegment(sketch, "E1244", {"start": v(12.2, 4.68) * mm, "end": v(12.15, 4.68) * mm});
            skLineSegment(sketch, "E1245", {"start": v(12.15, 4.68) * mm, "end": v(12.1, 4.68) * mm});
            skLineSegment(sketch, "E1246", {"start": v(12.1, 4.68) * mm, "end": v(12.05, 4.68) * mm});
            skLineSegment(sketch, "E1247", {"start": v(12.05, 4.68) * mm, "end": v(12, 4.68) * mm});
            skLineSegment(sketch, "E1248", {"start": v(12, 4.68) * mm, "end": v(11.95, 4.68) * mm});
            skLineSegment(sketch, "E1249", {"start": v(11.95, 4.68) * mm, "end": v(11.9, 4.68) * mm});
            skLineSegment(sketch, "E1250", {"start": v(11.9, 4.68) * mm, "end": v(11.85, 4.68) * mm});
            skLineSegment(sketch, "E1251", {"start": v(11.85, 4.68) * mm, "end": v(11.8, 4.68) * mm});
            skLineSegment(sketch, "E1252", {"start": v(11.8, 4.68) * mm, "end": v(11.75, 4.68) * mm});
            skLineSegment(sketch, "E1253", {"start": v(11.75, 4.68) * mm, "end": v(11.7, 4.68) * mm});
            skLineSegment(sketch, "E1254", {"start": v(11.7, 4.68) * mm, "end": v(11.65, 4.68) * mm});
            skLineSegment(sketch, "E1255", {"start": v(11.65, 4.68) * mm, "end": v(11.6, 4.68) * mm});
            skLineSegment(sketch, "E1256", {"start": v(11.6, 4.68) * mm, "end": v(11.55, 4.68) * mm});
            skLineSegment(sketch, "E1257", {"start": v(11.55, 4.68) * mm, "end": v(11.5, 4.68) * mm});
            skLineSegment(sketch, "E1258", {"start": v(11.5, 4.68) * mm, "end": v(11.45, 4.68) * mm});
            skLineSegment(sketch, "E1259", {"start": v(11.45, 4.68) * mm, "end": v(11.4, 4.68) * mm});
            skLineSegment(sketch, "E1260", {"start": v(11.4, 4.68) * mm, "end": v(11.35, 4.68) * mm});
            skLineSegment(sketch, "E1261", {"start": v(11.35, 4.68) * mm, "end": v(11.3, 4.68) * mm});
            skLineSegment(sketch, "E1262", {"start": v(11.3, 4.68) * mm, "end": v(11.25, 4.68) * mm});
            skLineSegment(sketch, "E1263", {"start": v(11.25, 4.68) * mm, "end": v(11.2, 4.68) * mm});
            skLineSegment(sketch, "E1264", {"start": v(11.2, 4.68) * mm, "end": v(11.15, 4.68) * mm});
            skLineSegment(sketch, "E1265", {"start": v(11.15, 4.68) * mm, "end": v(11.1, 4.68) * mm});
            skLineSegment(sketch, "E1266", {"start": v(11.1, 4.68) * mm, "end": v(11.05, 4.68) * mm});
            skLineSegment(sketch, "E1267", {"start": v(11.05, 4.68) * mm, "end": v(11, 4.68) * mm});
            skLineSegment(sketch, "E1268", {"start": v(11, 4.68) * mm, "end": v(10.95, 4.68) * mm});
            skLineSegment(sketch, "E1269", {"start": v(10.95, 4.68) * mm, "end": v(10.9, 4.68) * mm});
            skLineSegment(sketch, "E1270", {"start": v(10.9, 4.68) * mm, "end": v(10.85, 4.68) * mm});
            skLineSegment(sketch, "E1271", {"start": v(10.85, 4.68) * mm, "end": v(10.8, 4.68) * mm});
            skLineSegment(sketch, "E1272", {"start": v(10.8, 4.68) * mm, "end": v(10.75, 4.68) * mm});
            skLineSegment(sketch, "E1273", {"start": v(10.75, 4.68) * mm, "end": v(10.7, 4.68) * mm});
            skLineSegment(sketch, "E1274", {"start": v(10.7, 4.68) * mm, "end": v(10.65, 4.68) * mm});
            skLineSegment(sketch, "E1275", {"start": v(10.65, 4.68) * mm, "end": v(10.6, 4.68) * mm});
            skLineSegment(sketch, "E1276", {"start": v(10.6, 4.68) * mm, "end": v(10.55, 4.68) * mm});
            skLineSegment(sketch, "E1277", {"start": v(10.55, 4.68) * mm, "end": v(10.5, 4.68) * mm});
            skLineSegment(sketch, "E1278", {"start": v(10.5, 4.68) * mm, "end": v(10.45, 4.68) * mm});
            skLineSegment(sketch, "E1279", {"start": v(10.45, 4.68) * mm, "end": v(10.4, 4.68) * mm});
            skLineSegment(sketch, "E1280", {"start": v(10.4, 4.68) * mm, "end": v(10.35, 4.68) * mm});
            skLineSegment(sketch, "E1281", {"start": v(10.35, 4.68) * mm, "end": v(10.3, 4.68) * mm});
            skLineSegment(sketch, "E1282", {"start": v(10.3, 4.68) * mm, "end": v(10.25, 4.68) * mm});
            skLineSegment(sketch, "E1283", {"start": v(10.25, 4.68) * mm, "end": v(10.2, 4.68) * mm});
            skLineSegment(sketch, "E1284", {"start": v(10.2, 4.68) * mm, "end": v(10.15, 4.68) * mm});
            skLineSegment(sketch, "E1285", {"start": v(10.15, 4.68) * mm, "end": v(10.1, 4.68) * mm});
            skLineSegment(sketch, "E1286", {"start": v(10.1, 4.68) * mm, "end": v(10.05, 4.68) * mm});
            skLineSegment(sketch, "E1287", {"start": v(10.05, 4.68) * mm, "end": v(10, 4.68) * mm});
            skLineSegment(sketch, "E1288", {"start": v(10, 4.68) * mm, "end": v(9.95, 4.68) * mm});
            skLineSegment(sketch, "E1289", {"start": v(9.95, 4.68) * mm, "end": v(9.9, 4.68) * mm});
            skLineSegment(sketch, "E1290", {"start": v(9.9, 4.68) * mm, "end": v(9.85, 4.68) * mm});
            skLineSegment(sketch, "E1291", {"start": v(9.85, 4.68) * mm, "end": v(9.8, 4.68) * mm});
            skLineSegment(sketch, "E1292", {"start": v(9.8, 4.68) * mm, "end": v(9.75, 4.68) * mm});
            skLineSegment(sketch, "E1293", {"start": v(9.75, 4.68) * mm, "end": v(9.7, 4.68) * mm});
            skLineSegment(sketch, "E1294", {"start": v(9.7, 4.68) * mm, "end": v(9.65, 4.68) * mm});
            skLineSegment(sketch, "E1295", {"start": v(9.65, 4.68) * mm, "end": v(9.6, 4.68) * mm});
            skLineSegment(sketch, "E1296", {"start": v(9.6, 4.68) * mm, "end": v(9.55, 4.68) * mm});
            skLineSegment(sketch, "E1297", {"start": v(9.55, 4.68) * mm, "end": v(9.5, 4.68) * mm});
            skLineSegment(sketch, "E1298", {"start": v(9.5, 4.68) * mm, "end": v(9.45, 4.68) * mm});
            skLineSegment(sketch, "E1299", {"start": v(9.45, 4.68) * mm, "end": v(9.4, 4.68) * mm});
            skLineSegment(sketch, "E1300", {"start": v(9.4, 4.68) * mm, "end": v(9.35, 4.68) * mm});
            skLineSegment(sketch, "E1301", {"start": v(9.35, 4.68) * mm, "end": v(9.3, 4.68) * mm});
            skLineSegment(sketch, "E1302", {"start": v(9.3, 4.68) * mm, "end": v(9.25, 4.68) * mm});
            skLineSegment(sketch, "E1303", {"start": v(9.25, 4.68) * mm, "end": v(9.2, 4.68) * mm});
            skLineSegment(sketch, "E1304", {"start": v(9.2, 4.68) * mm, "end": v(9.15, 4.68) * mm});
            skLineSegment(sketch, "E1305", {"start": v(9.15, 4.68) * mm, "end": v(9.1, 4.68) * mm});
            skLineSegment(sketch, "E1306", {"start": v(9.1, 4.68) * mm, "end": v(9.05, 4.68) * mm});
            skLineSegment(sketch, "E1307", {"start": v(9.05, 4.68) * mm, "end": v(9, 4.68) * mm});
            skLineSegment(sketch, "E1308", {"start": v(9, 4.68) * mm, "end": v(8.95, 4.68) * mm});
            skLineSegment(sketch, "E1309", {"start": v(8.95, 4.68) * mm, "end": v(8.9, 4.68) * mm});
            skLineSegment(sketch, "E1310", {"start": v(8.9, 4.68) * mm, "end": v(8.85, 4.68) * mm});
            skLineSegment(sketch, "E1311", {"start": v(8.85, 4.68) * mm, "end": v(8.8, 4.68) * mm});
            skLineSegment(sketch, "E1312", {"start": v(8.8, 4.68) * mm, "end": v(8.75, 4.68) * mm});
            skLineSegment(sketch, "E1313", {"start": v(8.75, 4.68) * mm, "end": v(8.7, 4.68) * mm});
            skLineSegment(sketch, "E1314", {"start": v(8.7, 4.68) * mm, "end": v(8.65, 4.68) * mm});
            skLineSegment(sketch, "E1315", {"start": v(8.65, 4.68) * mm, "end": v(8.6, 4.68) * mm});
            skLineSegment(sketch, "E1316", {"start": v(8.6, 4.68) * mm, "end": v(8.55, 4.68) * mm});
            skLineSegment(sketch, "E1317", {"start": v(8.55, 4.68) * mm, "end": v(8.5, 4.68) * mm});
            skLineSegment(sketch, "E1318", {"start": v(8.5, 4.68) * mm, "end": v(8.45, 4.68) * mm});
            skLineSegment(sketch, "E1319", {"start": v(8.45, 4.68) * mm, "end": v(8.4, 4.68) * mm});
            skLineSegment(sketch, "E1320", {"start": v(8.4, 4.68) * mm, "end": v(8.35, 4.68) * mm});
            skLineSegment(sketch, "E1321", {"start": v(8.35, 4.68) * mm, "end": v(8.3, 4.68) * mm});
            skLineSegment(sketch, "E1322", {"start": v(8.3, 4.68) * mm, "end": v(8.25, 4.68) * mm});
            skLineSegment(sketch, "E1323", {"start": v(8.25, 4.68) * mm, "end": v(8.2, 4.68) * mm});
            skLineSegment(sketch, "E1324", {"start": v(8.2, 4.68) * mm, "end": v(8.15, 4.68) * mm});
            skLineSegment(sketch, "E1325", {"start": v(8.15, 4.68) * mm, "end": v(8.1, 4.68) * mm});
            skLineSegment(sketch, "E1326", {"start": v(8.1, 4.68) * mm, "end": v(8.05, 4.68) * mm});
            skLineSegment(sketch, "E1327", {"start": v(8.05, 4.68) * mm, "end": v(8, 4.68) * mm});
            skLineSegment(sketch, "E1328", {"start": v(8, 4.68) * mm, "end": v(7.95, 4.68) * mm});
            skLineSegment(sketch, "E1329", {"start": v(7.95, 4.68) * mm, "end": v(7.9, 4.68) * mm});
            skLineSegment(sketch, "E1330", {"start": v(7.9, 4.68) * mm, "end": v(7.85, 4.68) * mm});
            skLineSegment(sketch, "E1331", {"start": v(7.85, 4.68) * mm, "end": v(7.8, 4.68) * mm});
            skLineSegment(sketch, "E1332", {"start": v(7.8, 4.68) * mm, "end": v(7.75, 4.68) * mm});
            skLineSegment(sketch, "E1333", {"start": v(7.75, 4.68) * mm, "end": v(7.7, 4.68) * mm});
            skLineSegment(sketch, "E1334", {"start": v(7.7, 4.68) * mm, "end": v(7.65, 4.68) * mm});
            skLineSegment(sketch, "E1335", {"start": v(7.65, 4.68) * mm, "end": v(7.3, 4.68) * mm});
            skLineSegment(sketch, "E1336", {"start": v(7.3, 4.68) * mm, "end": v(7.3, 4.88) * mm});
            skLineSegment(sketch, "E1337", {"start": v(7.3, 4.88) * mm, "end": v(7.3, 4.92) * mm});
            skLineSegment(sketch, "E1338", {"start": v(7.3, 4.92) * mm, "end": v(7.3, 4.98) * mm});
            skLineSegment(sketch, "E1339", {"start": v(7.3, 4.98) * mm, "end": v(7.3, 5.03) * mm});
            skLineSegment(sketch, "E1340", {"start": v(7.3, 5.03) * mm, "end": v(7.3, 5.08) * mm});
            skLineSegment(sketch, "E1341", {"start": v(7.3, 5.08) * mm, "end": v(7.3, 5.12) * mm});
            skLineSegment(sketch, "E1342", {"start": v(7.3, 5.12) * mm, "end": v(7.3, 5.17) * mm});
            skLineSegment(sketch, "E1343", {"start": v(7.3, 5.17) * mm, "end": v(7.3, 5.23) * mm});
            skLineSegment(sketch, "E1344", {"start": v(7.3, 5.23) * mm, "end": v(7.3, 5.28) * mm});
            skLineSegment(sketch, "E1345", {"start": v(7.3, 5.28) * mm, "end": v(7.3, 5.33) * mm});
            skLineSegment(sketch, "E1346", {"start": v(7.3, 5.33) * mm, "end": v(7.3, 5.38) * mm});
            skLineSegment(sketch, "E1347", {"start": v(7.3, 5.38) * mm, "end": v(7.3, 5.42) * mm});
            skLineSegment(sketch, "E1348", {"start": v(7.3, 5.42) * mm, "end": v(7.3, 5.48) * mm});
            skLineSegment(sketch, "E1349", {"start": v(7.3, 5.48) * mm, "end": v(7.3, 5.53) * mm});
            skLineSegment(sketch, "E1350", {"start": v(7.3, 5.53) * mm, "end": v(7.3, 5.58) * mm});
            skLineSegment(sketch, "E1351", {"start": v(7.3, 5.58) * mm, "end": v(7.3, 5.63) * mm});
            skLineSegment(sketch, "E1352", {"start": v(7.3, 5.63) * mm, "end": v(7.3, 5.68) * mm});
            skLineSegment(sketch, "E1353", {"start": v(7.3, 5.68) * mm, "end": v(7.3, 5.72) * mm});
            skLineSegment(sketch, "E1354", {"start": v(7.3, 5.72) * mm, "end": v(7.3, 5.77) * mm});
            skLineSegment(sketch, "E1355", {"start": v(7.3, 5.77) * mm, "end": v(7.3, 5.83) * mm});
            skLineSegment(sketch, "E1356", {"start": v(7.3, 5.83) * mm, "end": v(7.3, 5.88) * mm});
            skLineSegment(sketch, "E1357", {"start": v(7.3, 5.88) * mm, "end": v(7.3, 5.92) * mm});
            skLineSegment(sketch, "E1358", {"start": v(7.3, 5.92) * mm, "end": v(7.3, 5.98) * mm});
            skLineSegment(sketch, "E1359", {"start": v(7.3, 5.98) * mm, "end": v(7.3, 6.03) * mm});
            skLineSegment(sketch, "E1360", {"start": v(7.3, 6.03) * mm, "end": v(7.3, 6.08) * mm});
            skLineSegment(sketch, "E1361", {"start": v(7.3, 6.08) * mm, "end": v(7.3, 6.12) * mm});
            skLineSegment(sketch, "E1362", {"start": v(7.3, 6.12) * mm, "end": v(7.3, 6.17) * mm});
            skLineSegment(sketch, "E1363", {"start": v(7.3, 6.17) * mm, "end": v(7.3, 6.23) * mm});
            skLineSegment(sketch, "E1364", {"start": v(7.3, 6.23) * mm, "end": v(7.3, 6.28) * mm});
            skLineSegment(sketch, "E1365", {"start": v(7.3, 6.28) * mm, "end": v(7.3, 6.33) * mm});
            skLineSegment(sketch, "E1366", {"start": v(7.3, 6.33) * mm, "end": v(7.3, 6.38) * mm});
            skLineSegment(sketch, "E1367", {"start": v(7.3, 6.38) * mm, "end": v(7.3, 6.42) * mm});
            skLineSegment(sketch, "E1368", {"start": v(7.3, 6.42) * mm, "end": v(7.3, 6.47) * mm});
            skLineSegment(sketch, "E1369", {"start": v(7.3, 6.47) * mm, "end": v(7.3, 6.52) * mm});
            skLineSegment(sketch, "E1370", {"start": v(7.3, 6.52) * mm, "end": v(7.3, 6.58) * mm});
            skLineSegment(sketch, "E1371", {"start": v(7.3, 6.58) * mm, "end": v(7.3, 6.62) * mm});
            skLineSegment(sketch, "E1372", {"start": v(7.3, 6.62) * mm, "end": v(7.3, 6.68) * mm});
            skLineSegment(sketch, "E1373", {"start": v(7.3, 6.68) * mm, "end": v(7.3, 6.72) * mm});
            skLineSegment(sketch, "E1374", {"start": v(7.3, 6.72) * mm, "end": v(7.3, 6.77) * mm});
            skLineSegment(sketch, "E1375", {"start": v(7.3, 6.77) * mm, "end": v(7.3, 6.83) * mm});
            skLineSegment(sketch, "E1376", {"start": v(7.3, 6.83) * mm, "end": v(7.3, 6.88) * mm});
            skLineSegment(sketch, "E1377", {"start": v(7.3, 6.88) * mm, "end": v(7.3, 6.93) * mm});
            skLineSegment(sketch, "E1378", {"start": v(7.3, 6.93) * mm, "end": v(7.3, 6.98) * mm});
            skLineSegment(sketch, "E1379", {"start": v(7.3, 6.98) * mm, "end": v(7.3, 7.03) * mm});
            skLineSegment(sketch, "E1380", {"start": v(7.3, 7.03) * mm, "end": v(7.3, 7.08) * mm});
            skLineSegment(sketch, "E1381", {"start": v(7.3, 7.08) * mm, "end": v(7.3, 7.12) * mm});
            skLineSegment(sketch, "E1382", {"start": v(7.3, 7.12) * mm, "end": v(7.3, 7.18) * mm});
            skLineSegment(sketch, "E1383", {"start": v(7.3, 7.18) * mm, "end": v(7.3, 7.23) * mm});
            skLineSegment(sketch, "E1384", {"start": v(7.3, 7.23) * mm, "end": v(7.3, 7.58) * mm});
            skLineSegment(sketch, "E1385", {"start": v(7.3, 7.58) * mm, "end": v(7.1, 7.58) * mm});
            skLineSegment(sketch, "E1386", {"start": v(7.1, 7.58) * mm, "end": v(7.05, 7.58) * mm});
            skLineSegment(sketch, "E1387", {"start": v(7.05, 7.58) * mm, "end": v(7, 7.58) * mm});
            skLineSegment(sketch, "E1388", {"start": v(7, 7.58) * mm, "end": v(6.95, 7.58) * mm});
            skLineSegment(sketch, "E1389", {"start": v(6.95, 7.58) * mm, "end": v(6.9, 7.58) * mm});
            skLineSegment(sketch, "E1390", {"start": v(6.9, 7.58) * mm, "end": v(6.85, 7.58) * mm});
            skLineSegment(sketch, "E1391", {"start": v(6.85, 7.58) * mm, "end": v(6.8, 7.58) * mm});
            skLineSegment(sketch, "E1392", {"start": v(6.8, 7.58) * mm, "end": v(6.75, 7.58) * mm});
            skLineSegment(sketch, "E1393", {"start": v(6.75, 7.58) * mm, "end": v(6.7, 7.58) * mm});
            skLineSegment(sketch, "E1394", {"start": v(6.7, 7.58) * mm, "end": v(6.65, 7.58) * mm});
            skLineSegment(sketch, "E1395", {"start": v(6.65, 7.58) * mm, "end": v(6.6, 7.58) * mm});
            skLineSegment(sketch, "E1396", {"start": v(6.6, 7.58) * mm, "end": v(6.55, 7.58) * mm});
            skLineSegment(sketch, "E1397", {"start": v(6.55, 7.58) * mm, "end": v(6.5, 7.58) * mm});
            skLineSegment(sketch, "E1398", {"start": v(6.5, 7.58) * mm, "end": v(6.45, 7.58) * mm});
            skLineSegment(sketch, "E1399", {"start": v(6.45, 7.58) * mm, "end": v(6.4, 7.58) * mm});
            skLineSegment(sketch, "E1400", {"start": v(6.4, 7.58) * mm, "end": v(6.35, 7.58) * mm});
            skLineSegment(sketch, "E1401", {"start": v(6.35, 7.58) * mm, "end": v(6.3, 7.58) * mm});
            skLineSegment(sketch, "E1402", {"start": v(6.3, 7.58) * mm, "end": v(6.25, 7.58) * mm});
            skLineSegment(sketch, "E1403", {"start": v(6.25, 7.58) * mm, "end": v(6.2, 7.58) * mm});
            skLineSegment(sketch, "E1404", {"start": v(6.2, 7.58) * mm, "end": v(6.15, 7.58) * mm});
            skLineSegment(sketch, "E1405", {"start": v(6.15, 7.58) * mm, "end": v(6.1, 7.58) * mm});
            skLineSegment(sketch, "E1406", {"start": v(6.1, 7.58) * mm, "end": v(6.05, 7.58) * mm});
            skLineSegment(sketch, "E1407", {"start": v(6.05, 7.58) * mm, "end": v(6, 7.58) * mm});
            skLineSegment(sketch, "E1408", {"start": v(6, 7.58) * mm, "end": v(5.95, 7.58) * mm});
            skLineSegment(sketch, "E1409", {"start": v(5.95, 7.58) * mm, "end": v(5.9, 7.58) * mm});
            skLineSegment(sketch, "E1410", {"start": v(5.9, 7.58) * mm, "end": v(5.85, 7.58) * mm});
            skLineSegment(sketch, "E1411", {"start": v(5.85, 7.58) * mm, "end": v(5.8, 7.58) * mm});
            skLineSegment(sketch, "E1412", {"start": v(5.8, 7.58) * mm, "end": v(5.75, 7.58) * mm});
            skLineSegment(sketch, "E1413", {"start": v(5.75, 7.58) * mm, "end": v(5.7, 7.58) * mm});
            skLineSegment(sketch, "E1414", {"start": v(5.7, 7.58) * mm, "end": v(5.65, 7.58) * mm});
            skLineSegment(sketch, "E1415", {"start": v(5.65, 7.58) * mm, "end": v(5.6, 7.58) * mm});
            skLineSegment(sketch, "E1416", {"start": v(5.6, 7.58) * mm, "end": v(5.55, 7.58) * mm});
            skLineSegment(sketch, "E1417", {"start": v(5.55, 7.58) * mm, "end": v(5.5, 7.58) * mm});
            skLineSegment(sketch, "E1418", {"start": v(5.5, 7.58) * mm, "end": v(5.45, 7.58) * mm});
            skLineSegment(sketch, "E1419", {"start": v(5.45, 7.58) * mm, "end": v(5.4, 7.58) * mm});
            skLineSegment(sketch, "E1420", {"start": v(5.4, 7.58) * mm, "end": v(5.35, 7.58) * mm});
            skLineSegment(sketch, "E1421", {"start": v(5.35, 7.58) * mm, "end": v(5.3, 7.58) * mm});
            skLineSegment(sketch, "E1422", {"start": v(5.3, 7.58) * mm, "end": v(5.25, 7.58) * mm});
            skLineSegment(sketch, "E1423", {"start": v(5.25, 7.58) * mm, "end": v(5.2, 7.58) * mm});
            skLineSegment(sketch, "E1424", {"start": v(5.2, 7.58) * mm, "end": v(5.15, 7.58) * mm});
            skLineSegment(sketch, "E1425", {"start": v(5.15, 7.58) * mm, "end": v(5.1, 7.58) * mm});
            skLineSegment(sketch, "E1426", {"start": v(5.1, 7.58) * mm, "end": v(5.05, 7.58) * mm});
            skLineSegment(sketch, "E1427", {"start": v(5.05, 7.58) * mm, "end": v(5, 7.58) * mm});
            skLineSegment(sketch, "E1428", {"start": v(5, 7.58) * mm, "end": v(4.95, 7.58) * mm});
            skLineSegment(sketch, "E1429", {"start": v(4.95, 7.58) * mm, "end": v(4.9, 7.58) * mm});
            skLineSegment(sketch, "E1430", {"start": v(4.9, 7.58) * mm, "end": v(4.85, 7.58) * mm});
            skLineSegment(sketch, "E1431", {"start": v(4.85, 7.58) * mm, "end": v(4.8, 7.58) * mm});
            skLineSegment(sketch, "E1432", {"start": v(4.8, 7.58) * mm, "end": v(4.75, 7.58) * mm});
            skLineSegment(sketch, "E1433", {"start": v(4.75, 7.58) * mm, "end": v(4.7, 7.58) * mm});
            skLineSegment(sketch, "E1434", {"start": v(4.7, 7.58) * mm, "end": v(4.65, 7.58) * mm});
            skLineSegment(sketch, "E1435", {"start": v(4.65, 7.58) * mm, "end": v(4.6, 7.58) * mm});
            skLineSegment(sketch, "E1436", {"start": v(4.6, 7.58) * mm, "end": v(4.55, 7.58) * mm});
            skLineSegment(sketch, "E1437", {"start": v(4.55, 7.58) * mm, "end": v(4.5, 7.58) * mm});
            skLineSegment(sketch, "E1438", {"start": v(4.5, 7.58) * mm, "end": v(4.45, 7.58) * mm});
            skLineSegment(sketch, "E1439", {"start": v(4.45, 7.58) * mm, "end": v(4.4, 7.58) * mm});
            skLineSegment(sketch, "E1440", {"start": v(4.4, 7.58) * mm, "end": v(4.35, 7.58) * mm});
            skLineSegment(sketch, "E1441", {"start": v(4.35, 7.58) * mm, "end": v(4.3, 7.58) * mm});
            skLineSegment(sketch, "E1442", {"start": v(4.3, 7.58) * mm, "end": v(4.25, 7.58) * mm});
            skLineSegment(sketch, "E1443", {"start": v(4.25, 7.58) * mm, "end": v(4.2, 7.58) * mm});
            skLineSegment(sketch, "E1444", {"start": v(4.2, 7.58) * mm, "end": v(4.15, 7.58) * mm});
            skLineSegment(sketch, "E1445", {"start": v(4.15, 7.58) * mm, "end": v(4.1, 7.58) * mm});
            skLineSegment(sketch, "E1446", {"start": v(4.1, 7.58) * mm, "end": v(4.05, 7.58) * mm});
            skLineSegment(sketch, "E1447", {"start": v(4.05, 7.58) * mm, "end": v(4, 7.58) * mm});
            skLineSegment(sketch, "E1448", {"start": v(4, 7.58) * mm, "end": v(3.95, 7.58) * mm});
            skLineSegment(sketch, "E1449", {"start": v(3.95, 7.58) * mm, "end": v(3.9, 7.58) * mm});
            skLineSegment(sketch, "E1450", {"start": v(3.9, 7.58) * mm, "end": v(3.85, 7.58) * mm});
            skLineSegment(sketch, "E1451", {"start": v(3.85, 7.58) * mm, "end": v(3.8, 7.58) * mm});
            skLineSegment(sketch, "E1452", {"start": v(3.8, 7.58) * mm, "end": v(3.75, 7.58) * mm});
            skLineSegment(sketch, "E1453", {"start": v(3.75, 7.58) * mm, "end": v(3.7, 7.58) * mm});
            skLineSegment(sketch, "E1454", {"start": v(3.7, 7.58) * mm, "end": v(3.65, 7.58) * mm});
            skLineSegment(sketch, "E1455", {"start": v(3.65, 7.58) * mm, "end": v(3.6, 7.58) * mm});
            skLineSegment(sketch, "E1456", {"start": v(3.6, 7.58) * mm, "end": v(3.55, 7.58) * mm});
            skLineSegment(sketch, "E1457", {"start": v(3.55, 7.58) * mm, "end": v(3.5, 7.58) * mm});
            skLineSegment(sketch, "E1458", {"start": v(3.5, 7.58) * mm, "end": v(3.45, 7.58) * mm});
            skLineSegment(sketch, "E1459", {"start": v(3.45, 7.58) * mm, "end": v(3.4, 7.58) * mm});
            skLineSegment(sketch, "E1460", {"start": v(3.4, 7.58) * mm, "end": v(3.35, 7.58) * mm});
            skLineSegment(sketch, "E1461", {"start": v(3.35, 7.58) * mm, "end": v(3.3, 7.58) * mm});
            skLineSegment(sketch, "E1462", {"start": v(3.3, 7.58) * mm, "end": v(3.25, 7.58) * mm});
            skLineSegment(sketch, "E1463", {"start": v(3.25, 7.58) * mm, "end": v(3.2, 7.58) * mm});
            skLineSegment(sketch, "E1464", {"start": v(3.2, 7.58) * mm, "end": v(3.15, 7.58) * mm});
            skLineSegment(sketch, "E1465", {"start": v(3.15, 7.58) * mm, "end": v(3.1, 7.58) * mm});
            skLineSegment(sketch, "E1466", {"start": v(3.1, 7.58) * mm, "end": v(3.05, 7.58) * mm});
            skLineSegment(sketch, "E1467", {"start": v(3.05, 7.58) * mm, "end": v(3, 7.58) * mm});
            skLineSegment(sketch, "E1468", {"start": v(3, 7.58) * mm, "end": v(2.95, 7.58) * mm});
            skLineSegment(sketch, "E1469", {"start": v(2.95, 7.58) * mm, "end": v(2.9, 7.58) * mm});
            skLineSegment(sketch, "E1470", {"start": v(2.9, 7.58) * mm, "end": v(2.85, 7.58) * mm});
            skLineSegment(sketch, "E1471", {"start": v(2.85, 7.58) * mm, "end": v(2.8, 7.58) * mm});
            skLineSegment(sketch, "E1472", {"start": v(2.8, 7.58) * mm, "end": v(2.75, 7.58) * mm});
            skLineSegment(sketch, "E1473", {"start": v(2.75, 7.58) * mm, "end": v(2.7, 7.58) * mm});
            skLineSegment(sketch, "E1474", {"start": v(2.7, 7.58) * mm, "end": v(2.65, 7.58) * mm});
            skLineSegment(sketch, "E1475", {"start": v(2.65, 7.58) * mm, "end": v(2.6, 7.58) * mm});
            skLineSegment(sketch, "E1476", {"start": v(2.6, 7.58) * mm, "end": v(2.55, 7.58) * mm});
            skLineSegment(sketch, "E1477", {"start": v(2.55, 7.58) * mm, "end": v(2.5, 7.58) * mm});
            skLineSegment(sketch, "E1478", {"start": v(2.5, 7.58) * mm, "end": v(2.45, 7.58) * mm});
            skLineSegment(sketch, "E1479", {"start": v(2.45, 7.58) * mm, "end": v(2.4, 7.58) * mm});
            skLineSegment(sketch, "E1480", {"start": v(2.4, 7.58) * mm, "end": v(2.35, 7.58) * mm});
            skLineSegment(sketch, "E1481", {"start": v(2.35, 7.58) * mm, "end": v(2.3, 7.58) * mm});
            skLineSegment(sketch, "E1482", {"start": v(2.3, 7.58) * mm, "end": v(2.25, 7.58) * mm});
            skLineSegment(sketch, "E1483", {"start": v(2.25, 7.58) * mm, "end": v(2.2, 7.58) * mm});
            skLineSegment(sketch, "E1484", {"start": v(2.2, 7.58) * mm, "end": v(2.15, 7.58) * mm});
            skLineSegment(sketch, "E1485", {"start": v(2.15, 7.58) * mm, "end": v(2.1, 7.58) * mm});
            skLineSegment(sketch, "E1486", {"start": v(2.1, 7.58) * mm, "end": v(2.05, 7.58) * mm});
            skLineSegment(sketch, "E1487", {"start": v(2.05, 7.58) * mm, "end": v(2, 7.58) * mm});
            skLineSegment(sketch, "E1488", {"start": v(2, 7.58) * mm, "end": v(1.95, 7.58) * mm});
            skLineSegment(sketch, "E1489", {"start": v(1.95, 7.58) * mm, "end": v(1.9, 7.58) * mm});
            skLineSegment(sketch, "E1490", {"start": v(1.9, 7.58) * mm, "end": v(1.85, 7.58) * mm});
            skLineSegment(sketch, "E1491", {"start": v(1.85, 7.58) * mm, "end": v(1.8, 7.58) * mm});
            skLineSegment(sketch, "E1492", {"start": v(1.8, 7.58) * mm, "end": v(1.75, 7.58) * mm});
            skLineSegment(sketch, "E1493", {"start": v(1.75, 7.58) * mm, "end": v(1.7, 7.58) * mm});
            skLineSegment(sketch, "E1494", {"start": v(1.7, 7.58) * mm, "end": v(1.65, 7.58) * mm});
            skLineSegment(sketch, "E1495", {"start": v(1.65, 7.58) * mm, "end": v(1.6, 7.58) * mm});
            skLineSegment(sketch, "E1496", {"start": v(1.6, 7.58) * mm, "end": v(1.55, 7.58) * mm});
            skLineSegment(sketch, "E1497", {"start": v(1.55, 7.58) * mm, "end": v(1.5, 7.58) * mm});
            skLineSegment(sketch, "E1498", {"start": v(1.5, 7.58) * mm, "end": v(1.45, 7.58) * mm});
            skLineSegment(sketch, "E1499", {"start": v(1.45, 7.58) * mm, "end": v(1.4, 7.58) * mm});
            skLineSegment(sketch, "E1500", {"start": v(1.4, 7.58) * mm, "end": v(1.35, 7.58) * mm});
            skLineSegment(sketch, "E1501", {"start": v(1.35, 7.58) * mm, "end": v(1.3, 7.58) * mm});
            skLineSegment(sketch, "E1502", {"start": v(1.3, 7.58) * mm, "end": v(1.25, 7.58) * mm});
            skLineSegment(sketch, "E1503", {"start": v(1.25, 7.58) * mm, "end": v(1.2, 7.58) * mm});
            skLineSegment(sketch, "E1504", {"start": v(1.2, 7.58) * mm, "end": v(1.15, 7.58) * mm});
            skLineSegment(sketch, "E1505", {"start": v(1.15, 7.58) * mm, "end": v(1.1, 7.58) * mm});
            skLineSegment(sketch, "E1506", {"start": v(1.1, 7.58) * mm, "end": v(1.05, 7.58) * mm});
            skLineSegment(sketch, "E1507", {"start": v(1.05, 7.58) * mm, "end": v(1, 7.58) * mm});
            skLineSegment(sketch, "E1508", {"start": v(1, 7.58) * mm, "end": v(0.95, 7.58) * mm});
            skLineSegment(sketch, "E1509", {"start": v(0.95, 7.58) * mm, "end": v(0.9, 7.58) * mm});
            skLineSegment(sketch, "E1510", {"start": v(0.9, 7.58) * mm, "end": v(0.85, 7.58) * mm});
            skLineSegment(sketch, "E1511", {"start": v(0.85, 7.58) * mm, "end": v(0.8, 7.58) * mm});
            skLineSegment(sketch, "E1512", {"start": v(0.8, 7.58) * mm, "end": v(0.75, 7.58) * mm});
            skLineSegment(sketch, "E1513", {"start": v(0.75, 7.58) * mm, "end": v(0.7, 7.58) * mm});
            skLineSegment(sketch, "E1514", {"start": v(0.7, 7.58) * mm, "end": v(0.65, 7.58) * mm});
            skLineSegment(sketch, "E1515", {"start": v(0.65, 7.58) * mm, "end": v(0.6, 7.58) * mm});
            skLineSegment(sketch, "E1516", {"start": v(0.6, 7.58) * mm, "end": v(0.55, 7.58) * mm});
            skLineSegment(sketch, "E1517", {"start": v(0.55, 7.58) * mm, "end": v(0.5, 7.58) * mm});
            skLineSegment(sketch, "E1518", {"start": v(0.5, 7.58) * mm, "end": v(0.45, 7.58) * mm});
            skLineSegment(sketch, "E1519", {"start": v(0.45, 7.58) * mm, "end": v(0.4, 7.58) * mm});
            skLineSegment(sketch, "E1520", {"start": v(0.4, 7.58) * mm, "end": v(0.35, 7.58) * mm});
            skLineSegment(sketch, "E1521", {"start": v(0.35, 7.58) * mm, "end": v(0.3, 7.58) * mm});
            skLineSegment(sketch, "E1522", {"start": v(0.3, 7.58) * mm, "end": v(0.25, 7.58) * mm});
            skLineSegment(sketch, "E1523", {"start": v(0.25, 7.58) * mm, "end": v(0.2, 7.58) * mm});
            skLineSegment(sketch, "E1524", {"start": v(0.2, 7.58) * mm, "end": v(0.15, 7.58) * mm});
            skLineSegment(sketch, "E1525", {"start": v(0.15, 7.58) * mm, "end": v(0.1, 7.58) * mm});
            skLineSegment(sketch, "E1526", {"start": v(0.1, 7.58) * mm, "end": v(0.05, 7.58) * mm});
            skLineSegment(sketch, "E1527", {"start": v(0.05, 7.58) * mm, "end": v(0, 7.58) * mm});
            skLineSegment(sketch, "E1528", {"start": v(0, 7.58) * mm, "end": v(-0.05, 7.58) * mm});
            skLineSegment(sketch, "E1529", {"start": v(-0.05, 7.58) * mm, "end": v(-0.1, 7.58) * mm});
            skLineSegment(sketch, "E1530", {"start": v(-0.1, 7.58) * mm, "end": v(-0.15, 7.58) * mm});
            skLineSegment(sketch, "E1531", {"start": v(-0.15, 7.58) * mm, "end": v(-0.2, 7.58) * mm});
            skLineSegment(sketch, "E1532", {"start": v(-0.2, 7.58) * mm, "end": v(-0.25, 7.58) * mm});
            skLineSegment(sketch, "E1533", {"start": v(-0.25, 7.58) * mm, "end": v(-0.3, 7.58) * mm});
            skLineSegment(sketch, "E1534", {"start": v(-0.3, 7.58) * mm, "end": v(-0.35, 7.58) * mm});
            skLineSegment(sketch, "E1535", {"start": v(-0.35, 7.58) * mm, "end": v(-0.4, 7.58) * mm});
            skLineSegment(sketch, "E1536", {"start": v(-0.4, 7.58) * mm, "end": v(-0.45, 7.58) * mm});
            skLineSegment(sketch, "E1537", {"start": v(-0.45, 7.58) * mm, "end": v(-0.5, 7.58) * mm});
            skLineSegment(sketch, "E1538", {"start": v(-0.5, 7.58) * mm, "end": v(-0.55, 7.58) * mm});
            skLineSegment(sketch, "E1539", {"start": v(-0.55, 7.58) * mm, "end": v(-0.6, 7.58) * mm});
            skLineSegment(sketch, "E1540", {"start": v(-0.6, 7.58) * mm, "end": v(-0.65, 7.58) * mm});
            skLineSegment(sketch, "E1541", {"start": v(-0.65, 7.58) * mm, "end": v(-0.7, 7.58) * mm});
            skLineSegment(sketch, "E1542", {"start": v(-0.7, 7.58) * mm, "end": v(-0.75, 7.58) * mm});
            skLineSegment(sketch, "E1543", {"start": v(-0.75, 7.58) * mm, "end": v(-0.8, 7.58) * mm});
            skLineSegment(sketch, "E1544", {"start": v(-0.8, 7.58) * mm, "end": v(-0.85, 7.58) * mm});
            skLineSegment(sketch, "E1545", {"start": v(-0.85, 7.58) * mm, "end": v(-0.9, 7.58) * mm});
            skLineSegment(sketch, "E1546", {"start": v(-0.9, 7.58) * mm, "end": v(-0.95, 7.58) * mm});
            skLineSegment(sketch, "E1547", {"start": v(-0.95, 7.58) * mm, "end": v(-1, 7.58) * mm});
            skLineSegment(sketch, "E1548", {"start": v(-1, 7.58) * mm, "end": v(-1.05, 7.58) * mm});
            skLineSegment(sketch, "E1549", {"start": v(-1.05, 7.58) * mm, "end": v(-1.1, 7.58) * mm});
            skLineSegment(sketch, "E1550", {"start": v(-1.1, 7.58) * mm, "end": v(-1.15, 7.58) * mm});
            skLineSegment(sketch, "E1551", {"start": v(-1.15, 7.58) * mm, "end": v(-1.2, 7.58) * mm});
            skLineSegment(sketch, "E1552", {"start": v(-1.2, 7.58) * mm, "end": v(-1.25, 7.58) * mm});
            skLineSegment(sketch, "E1553", {"start": v(-1.25, 7.58) * mm, "end": v(-1.3, 7.58) * mm});
            skLineSegment(sketch, "E1554", {"start": v(-1.3, 7.58) * mm, "end": v(-1.35, 7.58) * mm});
            skLineSegment(sketch, "E1555", {"start": v(-1.35, 7.58) * mm, "end": v(-1.4, 7.58) * mm});
            skLineSegment(sketch, "E1556", {"start": v(-1.4, 7.58) * mm, "end": v(-1.45, 7.58) * mm});
            skLineSegment(sketch, "E1557", {"start": v(-1.45, 7.58) * mm, "end": v(-1.5, 7.58) * mm});
            skLineSegment(sketch, "E1558", {"start": v(-1.5, 7.58) * mm, "end": v(-1.55, 7.58) * mm});
            skLineSegment(sketch, "E1559", {"start": v(-1.55, 7.58) * mm, "end": v(-1.6, 7.58) * mm});
            skLineSegment(sketch, "E1560", {"start": v(-1.6, 7.58) * mm, "end": v(-1.65, 7.58) * mm});
            skLineSegment(sketch, "E1561", {"start": v(-1.65, 7.58) * mm, "end": v(-1.7, 7.58) * mm});
            skLineSegment(sketch, "E1562", {"start": v(-1.7, 7.58) * mm, "end": v(-1.75, 7.58) * mm});
            skLineSegment(sketch, "E1563", {"start": v(-1.75, 7.58) * mm, "end": v(-1.8, 7.58) * mm});
            skLineSegment(sketch, "E1564", {"start": v(-1.8, 7.58) * mm, "end": v(-1.85, 7.58) * mm});
            skLineSegment(sketch, "E1565", {"start": v(-1.85, 7.58) * mm, "end": v(-1.9, 7.58) * mm});
            skLineSegment(sketch, "E1566", {"start": v(-1.9, 7.58) * mm, "end": v(-1.95, 7.58) * mm});
            skLineSegment(sketch, "E1567", {"start": v(-1.95, 7.58) * mm, "end": v(-2, 7.58) * mm});
            skLineSegment(sketch, "E1568", {"start": v(-2, 7.58) * mm, "end": v(-2.05, 7.58) * mm});
            skLineSegment(sketch, "E1569", {"start": v(-2.05, 7.58) * mm, "end": v(-2.1, 7.58) * mm});
            skLineSegment(sketch, "E1570", {"start": v(-2.1, 7.58) * mm, "end": v(-2.15, 7.58) * mm});
            skLineSegment(sketch, "E1571", {"start": v(-2.15, 7.58) * mm, "end": v(-2.2, 7.58) * mm});
            skLineSegment(sketch, "E1572", {"start": v(-2.2, 7.58) * mm, "end": v(-2.25, 7.58) * mm});
            skLineSegment(sketch, "E1573", {"start": v(-2.25, 7.58) * mm, "end": v(-2.3, 7.58) * mm});
            skLineSegment(sketch, "E1574", {"start": v(-2.3, 7.58) * mm, "end": v(-2.35, 7.58) * mm});
            skLineSegment(sketch, "E1575", {"start": v(-2.35, 7.58) * mm, "end": v(-2.4, 7.58) * mm});
            skLineSegment(sketch, "E1576", {"start": v(-2.4, 7.58) * mm, "end": v(-2.45, 7.58) * mm});
            skLineSegment(sketch, "E1577", {"start": v(-2.45, 7.58) * mm, "end": v(-2.5, 7.58) * mm});
            skLineSegment(sketch, "E1578", {"start": v(-2.5, 7.58) * mm, "end": v(-2.55, 7.58) * mm});
            skLineSegment(sketch, "E1579", {"start": v(-2.55, 7.58) * mm, "end": v(-2.6, 7.58) * mm});
            skLineSegment(sketch, "E1580", {"start": v(-2.6, 7.58) * mm, "end": v(-2.65, 7.58) * mm});
            skLineSegment(sketch, "E1581", {"start": v(-2.65, 7.58) * mm, "end": v(-2.7, 7.58) * mm});
            skLineSegment(sketch, "E1582", {"start": v(-2.7, 7.58) * mm, "end": v(-2.75, 7.58) * mm});
            skLineSegment(sketch, "E1583", {"start": v(-2.75, 7.58) * mm, "end": v(-2.8, 7.58) * mm});
            skLineSegment(sketch, "E1584", {"start": v(-2.8, 7.58) * mm, "end": v(-2.85, 7.58) * mm});
            skLineSegment(sketch, "E1585", {"start": v(-2.85, 7.58) * mm, "end": v(-2.9, 7.58) * mm});
            skLineSegment(sketch, "E1586", {"start": v(-2.9, 7.58) * mm, "end": v(-2.95, 7.58) * mm});
            skLineSegment(sketch, "E1587", {"start": v(-2.95, 7.58) * mm, "end": v(-3, 7.58) * mm});
            skLineSegment(sketch, "E1588", {"start": v(-3, 7.58) * mm, "end": v(-3.05, 7.58) * mm});
            skLineSegment(sketch, "E1589", {"start": v(-3.05, 7.58) * mm, "end": v(-3.1, 7.58) * mm});
            skLineSegment(sketch, "E1590", {"start": v(-3.1, 7.58) * mm, "end": v(-3.15, 7.58) * mm});
            skLineSegment(sketch, "E1591", {"start": v(-3.15, 7.58) * mm, "end": v(-3.2, 7.58) * mm});
            skLineSegment(sketch, "E1592", {"start": v(-3.2, 7.58) * mm, "end": v(-3.25, 7.58) * mm});
            skLineSegment(sketch, "E1593", {"start": v(-3.25, 7.58) * mm, "end": v(-3.3, 7.58) * mm});
            skLineSegment(sketch, "E1594", {"start": v(-3.3, 7.58) * mm, "end": v(-3.35, 7.58) * mm});
            skLineSegment(sketch, "E1595", {"start": v(-3.35, 7.58) * mm, "end": v(-3.4, 7.58) * mm});
            skLineSegment(sketch, "E1596", {"start": v(-3.4, 7.58) * mm, "end": v(-3.45, 7.58) * mm});
            skLineSegment(sketch, "E1597", {"start": v(-3.45, 7.58) * mm, "end": v(-3.5, 7.58) * mm});
            skLineSegment(sketch, "E1598", {"start": v(-3.5, 7.58) * mm, "end": v(-3.55, 7.58) * mm});
            skLineSegment(sketch, "E1599", {"start": v(-3.55, 7.58) * mm, "end": v(-3.6, 7.58) * mm});
            skLineSegment(sketch, "E1600", {"start": v(-3.6, 7.58) * mm, "end": v(-3.65, 7.58) * mm});
            skLineSegment(sketch, "E1601", {"start": v(-3.65, 7.58) * mm, "end": v(-3.7, 7.58) * mm});
            skLineSegment(sketch, "E1602", {"start": v(-3.7, 7.58) * mm, "end": v(-3.75, 7.58) * mm});
            skLineSegment(sketch, "E1603", {"start": v(-3.75, 7.58) * mm, "end": v(-3.8, 7.58) * mm});
            skLineSegment(sketch, "E1604", {"start": v(-3.8, 7.58) * mm, "end": v(-3.85, 7.58) * mm});
            skLineSegment(sketch, "E1605", {"start": v(-3.85, 7.58) * mm, "end": v(-3.9, 7.58) * mm});
            skLineSegment(sketch, "E1606", {"start": v(-3.9, 7.58) * mm, "end": v(-3.95, 7.58) * mm});
            skLineSegment(sketch, "E1607", {"start": v(-3.95, 7.58) * mm, "end": v(-4, 7.58) * mm});
            skLineSegment(sketch, "E1608", {"start": v(-4, 7.58) * mm, "end": v(-4.05, 7.58) * mm});
            skLineSegment(sketch, "E1609", {"start": v(-4.05, 7.58) * mm, "end": v(-4.1, 7.58) * mm});
            skLineSegment(sketch, "E1610", {"start": v(-4.1, 7.58) * mm, "end": v(-4.15, 7.58) * mm});
            skLineSegment(sketch, "E1611", {"start": v(-4.15, 7.58) * mm, "end": v(-4.2, 7.58) * mm});
            skLineSegment(sketch, "E1612", {"start": v(-4.2, 7.58) * mm, "end": v(-4.25, 7.58) * mm});
            skLineSegment(sketch, "E1613", {"start": v(-4.25, 7.58) * mm, "end": v(-4.3, 7.58) * mm});
            skLineSegment(sketch, "E1614", {"start": v(-4.3, 7.58) * mm, "end": v(-4.35, 7.58) * mm});
            skLineSegment(sketch, "E1615", {"start": v(-4.35, 7.58) * mm, "end": v(-4.4, 7.58) * mm});
            skLineSegment(sketch, "E1616", {"start": v(-4.4, 7.58) * mm, "end": v(-4.45, 7.58) * mm});
            skLineSegment(sketch, "E1617", {"start": v(-4.45, 7.58) * mm, "end": v(-4.5, 7.58) * mm});
            skLineSegment(sketch, "E1618", {"start": v(-4.5, 7.58) * mm, "end": v(-4.55, 7.58) * mm});
            skLineSegment(sketch, "E1619", {"start": v(-4.55, 7.58) * mm, "end": v(-4.6, 7.58) * mm});
            skLineSegment(sketch, "E1620", {"start": v(-4.6, 7.58) * mm, "end": v(-4.65, 7.58) * mm});
            skLineSegment(sketch, "E1621", {"start": v(-4.65, 7.58) * mm, "end": v(-4.7, 7.58) * mm});
            skLineSegment(sketch, "E1622", {"start": v(-4.7, 7.58) * mm, "end": v(-4.75, 7.58) * mm});
            skLineSegment(sketch, "E1623", {"start": v(-4.75, 7.58) * mm, "end": v(-4.8, 7.58) * mm});
            skLineSegment(sketch, "E1624", {"start": v(-4.8, 7.58) * mm, "end": v(-4.85, 7.58) * mm});
            skLineSegment(sketch, "E1625", {"start": v(-4.85, 7.58) * mm, "end": v(-4.9, 7.58) * mm});
            skLineSegment(sketch, "E1626", {"start": v(-4.9, 7.58) * mm, "end": v(-4.95, 7.58) * mm});
            skLineSegment(sketch, "E1627", {"start": v(-4.95, 7.58) * mm, "end": v(-5, 7.58) * mm});
            skLineSegment(sketch, "E1628", {"start": v(-5, 7.58) * mm, "end": v(-5.05, 7.58) * mm});
            skLineSegment(sketch, "E1629", {"start": v(-5.05, 7.58) * mm, "end": v(-5.1, 7.58) * mm});
            skLineSegment(sketch, "E1630", {"start": v(-5.1, 7.58) * mm, "end": v(-5.15, 7.58) * mm});
            skLineSegment(sketch, "E1631", {"start": v(-5.15, 7.58) * mm, "end": v(-5.2, 7.58) * mm});
            skLineSegment(sketch, "E1632", {"start": v(-5.2, 7.58) * mm, "end": v(-5.25, 7.58) * mm});
            skLineSegment(sketch, "E1633", {"start": v(-5.25, 7.58) * mm, "end": v(-5.3, 7.58) * mm});
            skLineSegment(sketch, "E1634", {"start": v(-5.3, 7.58) * mm, "end": v(-5.35, 7.58) * mm});
            skLineSegment(sketch, "E1635", {"start": v(-5.35, 7.58) * mm, "end": v(-5.4, 7.58) * mm});
            skLineSegment(sketch, "E1636", {"start": v(-5.4, 7.58) * mm, "end": v(-5.45, 7.58) * mm});
            skLineSegment(sketch, "E1637", {"start": v(-5.45, 7.58) * mm, "end": v(-5.5, 7.58) * mm});
            skLineSegment(sketch, "E1638", {"start": v(-5.5, 7.58) * mm, "end": v(-5.55, 7.58) * mm});
            skLineSegment(sketch, "E1639", {"start": v(-5.55, 7.58) * mm, "end": v(-5.6, 7.58) * mm});
            skLineSegment(sketch, "E1640", {"start": v(-5.6, 7.58) * mm, "end": v(-5.65, 7.58) * mm});
            skLineSegment(sketch, "E1641", {"start": v(-5.65, 7.58) * mm, "end": v(-5.7, 7.58) * mm});
            skLineSegment(sketch, "E1642", {"start": v(-5.7, 7.58) * mm, "end": v(-5.75, 7.58) * mm});
            skLineSegment(sketch, "E1643", {"start": v(-5.75, 7.58) * mm, "end": v(-5.8, 7.58) * mm});
            skLineSegment(sketch, "E1644", {"start": v(-5.8, 7.58) * mm, "end": v(-5.85, 7.58) * mm});
            skLineSegment(sketch, "E1645", {"start": v(-5.85, 7.58) * mm, "end": v(-5.9, 7.58) * mm});
            skLineSegment(sketch, "E1646", {"start": v(-5.9, 7.58) * mm, "end": v(-5.95, 7.58) * mm});
            skLineSegment(sketch, "E1647", {"start": v(-5.95, 7.58) * mm, "end": v(-6, 7.58) * mm});
            skLineSegment(sketch, "E1648", {"start": v(-6, 7.58) * mm, "end": v(-6.05, 7.58) * mm});
            skLineSegment(sketch, "E1649", {"start": v(-6.05, 7.58) * mm, "end": v(-6.1, 7.58) * mm});
            skLineSegment(sketch, "E1650", {"start": v(-6.1, 7.58) * mm, "end": v(-6.15, 7.58) * mm});
            skLineSegment(sketch, "E1651", {"start": v(-6.15, 7.58) * mm, "end": v(-6.2, 7.58) * mm});
            skLineSegment(sketch, "E1652", {"start": v(-6.2, 7.58) * mm, "end": v(-6.25, 7.58) * mm});
            skLineSegment(sketch, "E1653", {"start": v(-6.25, 7.58) * mm, "end": v(-6.3, 7.58) * mm});
            skLineSegment(sketch, "E1654", {"start": v(-6.3, 7.58) * mm, "end": v(-6.35, 7.58) * mm});
            skLineSegment(sketch, "E1655", {"start": v(-6.35, 7.58) * mm, "end": v(-6.4, 7.58) * mm});
            skLineSegment(sketch, "E1656", {"start": v(-6.4, 7.58) * mm, "end": v(-6.45, 7.58) * mm});
            skLineSegment(sketch, "E1657", {"start": v(-6.45, 7.58) * mm, "end": v(-6.5, 7.58) * mm});
            skLineSegment(sketch, "E1658", {"start": v(-6.5, 7.58) * mm, "end": v(-6.55, 7.58) * mm});
            skLineSegment(sketch, "E1659", {"start": v(-6.55, 7.58) * mm, "end": v(-6.6, 7.58) * mm});
            skLineSegment(sketch, "E1660", {"start": v(-6.6, 7.58) * mm, "end": v(-6.65, 7.58) * mm});
            skLineSegment(sketch, "E1661", {"start": v(-6.65, 7.58) * mm, "end": v(-6.7, 7.58) * mm});
            skLineSegment(sketch, "E1662", {"start": v(-6.7, 7.58) * mm, "end": v(-6.75, 7.58) * mm});
            skLineSegment(sketch, "E1663", {"start": v(-6.75, 7.58) * mm, "end": v(-6.8, 7.58) * mm});
            skLineSegment(sketch, "E1664", {"start": v(-6.8, 7.58) * mm, "end": v(-6.85, 7.58) * mm});
            skLineSegment(sketch, "E1665", {"start": v(-6.85, 7.58) * mm, "end": v(-7.2, 7.58) * mm});
            skLineSegment(sketch, "E1666", {"start": v(-4.95, 5.38) * mm, "end": v(-4.95, 5.17) * mm});
            skLineSegment(sketch, "E1667", {"start": v(-4.95, 5.17) * mm, "end": v(-4.95, 5.12) * mm});
            skLineSegment(sketch, "E1668", {"start": v(-4.95, 5.12) * mm, "end": v(-4.95, 5.08) * mm});
            skLineSegment(sketch, "E1669", {"start": v(-4.95, 5.08) * mm, "end": v(-4.95, 5.03) * mm});
            skLineSegment(sketch, "E1670", {"start": v(-4.95, 5.03) * mm, "end": v(-4.95, 4.98) * mm});
            skLineSegment(sketch, "E1671", {"start": v(-4.95, 4.98) * mm, "end": v(-4.95, 4.92) * mm});
            skLineSegment(sketch, "E1672", {"start": v(-4.95, 4.92) * mm, "end": v(-4.95, 4.88) * mm});
            skLineSegment(sketch, "E1673", {"start": v(-4.95, 4.88) * mm, "end": v(-4.95, 4.83) * mm});
            skLineSegment(sketch, "E1674", {"start": v(-4.95, 4.83) * mm, "end": v(-4.95, 4.78) * mm});
            skLineSegment(sketch, "E1675", {"start": v(-4.95, 4.78) * mm, "end": v(-4.95, 4.73) * mm});
            skLineSegment(sketch, "E1676", {"start": v(-4.95, 4.73) * mm, "end": v(-4.95, 4.68) * mm});
            skLineSegment(sketch, "E1677", {"start": v(-4.95, 4.68) * mm, "end": v(-4.95, 4.63) * mm});
            skLineSegment(sketch, "E1678", {"start": v(-4.95, 4.63) * mm, "end": v(-4.95, 4.58) * mm});
            skLineSegment(sketch, "E1679", {"start": v(-4.95, 4.58) * mm, "end": v(-4.95, 4.53) * mm});
            skLineSegment(sketch, "E1680", {"start": v(-4.95, 4.53) * mm, "end": v(-4.95, 4.48) * mm});
            skLineSegment(sketch, "E1681", {"start": v(-4.95, 4.48) * mm, "end": v(-4.95, 4.42) * mm});
            skLineSegment(sketch, "E1682", {"start": v(-4.95, 4.42) * mm, "end": v(-4.95, 4.38) * mm});
            skLineSegment(sketch, "E1683", {"start": v(-4.95, 4.38) * mm, "end": v(-4.95, 4.33) * mm});
            skLineSegment(sketch, "E1684", {"start": v(-4.95, 4.33) * mm, "end": v(-4.95, 4.28) * mm});
            skLineSegment(sketch, "E1685", {"start": v(-4.95, 4.28) * mm, "end": v(-4.95, 4.22) * mm});
            skLineSegment(sketch, "E1686", {"start": v(-4.95, 4.22) * mm, "end": v(-4.95, 4.17) * mm});
            skLineSegment(sketch, "E1687", {"start": v(-4.95, 4.17) * mm, "end": v(-4.95, 4.12) * mm});
            skLineSegment(sketch, "E1688", {"start": v(-4.95, 4.12) * mm, "end": v(-4.95, 4.08) * mm});
            skLineSegment(sketch, "E1689", {"start": v(-4.95, 4.08) * mm, "end": v(-4.95, 4.03) * mm});
            skLineSegment(sketch, "E1690", {"start": v(-4.95, 4.03) * mm, "end": v(-4.95, 3.98) * mm});
            skLineSegment(sketch, "E1691", {"start": v(-4.95, 3.98) * mm, "end": v(-4.95, 3.93) * mm});
            skLineSegment(sketch, "E1692", {"start": v(-4.95, 3.93) * mm, "end": v(-4.95, 3.88) * mm});
            skLineSegment(sketch, "E1693", {"start": v(-4.95, 3.88) * mm, "end": v(-4.95, 3.83) * mm});
            skLineSegment(sketch, "E1694", {"start": v(-4.95, 3.83) * mm, "end": v(-4.95, 3.78) * mm});
            skLineSegment(sketch, "E1695", {"start": v(-4.95, 3.78) * mm, "end": v(-4.95, 3.73) * mm});
            skLineSegment(sketch, "E1696", {"start": v(-4.95, 3.73) * mm, "end": v(-4.95, 3.68) * mm});
            skLineSegment(sketch, "E1697", {"start": v(-4.95, 3.68) * mm, "end": v(-4.95, 3.62) * mm});
            skLineSegment(sketch, "E1698", {"start": v(-4.95, 3.62) * mm, "end": v(-4.95, 3.58) * mm});
            skLineSegment(sketch, "E1699", {"start": v(-4.95, 3.58) * mm, "end": v(-4.95, 3.53) * mm});
            skLineSegment(sketch, "E1700", {"start": v(-4.95, 3.53) * mm, "end": v(-4.95, 3.48) * mm});
            skLineSegment(sketch, "E1701", {"start": v(-4.95, 3.48) * mm, "end": v(-4.95, 3.43) * mm});
            skLineSegment(sketch, "E1702", {"start": v(-4.95, 3.43) * mm, "end": v(-4.95, 3.38) * mm});
            skLineSegment(sketch, "E1703", {"start": v(-4.95, 3.38) * mm, "end": v(-4.95, 3.33) * mm});
            skLineSegment(sketch, "E1704", {"start": v(-4.95, 3.33) * mm, "end": v(-4.95, 3.28) * mm});
            skLineSegment(sketch, "E1705", {"start": v(-4.95, 3.28) * mm, "end": v(-4.95, 3.23) * mm});
            skLineSegment(sketch, "E1706", {"start": v(-4.95, 3.23) * mm, "end": v(-4.95, 3.18) * mm});
            skLineSegment(sketch, "E1707", {"start": v(-4.95, 3.18) * mm, "end": v(-4.95, 3.12) * mm});
            skLineSegment(sketch, "E1708", {"start": v(-4.95, 3.12) * mm, "end": v(-4.95, 3.08) * mm});
            skLineSegment(sketch, "E1709", {"start": v(-4.95, 3.08) * mm, "end": v(-4.95, 3.03) * mm});
            skLineSegment(sketch, "E1710", {"start": v(-4.95, 3.03) * mm, "end": v(-4.95, 2.98) * mm});
            skLineSegment(sketch, "E1711", {"start": v(-4.95, 2.98) * mm, "end": v(-4.95, 2.93) * mm});
            skLineSegment(sketch, "E1712", {"start": v(-4.95, 2.93) * mm, "end": v(-4.95, 2.88) * mm});
            skLineSegment(sketch, "E1713", {"start": v(-4.95, 2.88) * mm, "end": v(-4.95, 2.83) * mm});
            skLineSegment(sketch, "E1714", {"start": v(-4.95, 2.83) * mm, "end": v(-4.95, 2.48) * mm});
            skLineSegment(sketch, "E1715", {"start": v(-4.95, 2.48) * mm, "end": v(-5.15, 2.48) * mm});
            skLineSegment(sketch, "E1716", {"start": v(-5.15, 2.48) * mm, "end": v(-5.2, 2.48) * mm});
            skLineSegment(sketch, "E1717", {"start": v(-5.2, 2.48) * mm, "end": v(-5.25, 2.48) * mm});
            skLineSegment(sketch, "E1718", {"start": v(-5.25, 2.48) * mm, "end": v(-5.3, 2.48) * mm});
            skLineSegment(sketch, "E1719", {"start": v(-5.3, 2.48) * mm, "end": v(-5.35, 2.48) * mm});
            skLineSegment(sketch, "E1720", {"start": v(-5.35, 2.48) * mm, "end": v(-5.4, 2.48) * mm});
            skLineSegment(sketch, "E1721", {"start": v(-5.4, 2.48) * mm, "end": v(-5.45, 2.48) * mm});
            skLineSegment(sketch, "E1722", {"start": v(-5.45, 2.48) * mm, "end": v(-5.5, 2.48) * mm});
            skLineSegment(sketch, "E1723", {"start": v(-5.5, 2.48) * mm, "end": v(-5.55, 2.48) * mm});
            skLineSegment(sketch, "E1724", {"start": v(-5.55, 2.48) * mm, "end": v(-5.6, 2.48) * mm});
            skLineSegment(sketch, "E1725", {"start": v(-5.6, 2.48) * mm, "end": v(-5.65, 2.48) * mm});
            skLineSegment(sketch, "E1726", {"start": v(-5.65, 2.48) * mm, "end": v(-5.7, 2.48) * mm});
            skLineSegment(sketch, "E1727", {"start": v(-5.7, 2.48) * mm, "end": v(-5.75, 2.48) * mm});
            skLineSegment(sketch, "E1728", {"start": v(-5.75, 2.48) * mm, "end": v(-5.8, 2.48) * mm});
            skLineSegment(sketch, "E1729", {"start": v(-5.8, 2.48) * mm, "end": v(-5.85, 2.48) * mm});
            skLineSegment(sketch, "E1730", {"start": v(-5.85, 2.48) * mm, "end": v(-5.9, 2.48) * mm});
            skLineSegment(sketch, "E1731", {"start": v(-5.9, 2.48) * mm, "end": v(-5.95, 2.48) * mm});
            skLineSegment(sketch, "E1732", {"start": v(-5.95, 2.48) * mm, "end": v(-6, 2.48) * mm});
            skLineSegment(sketch, "E1733", {"start": v(-6, 2.48) * mm, "end": v(-6.05, 2.48) * mm});
            skLineSegment(sketch, "E1734", {"start": v(-6.05, 2.48) * mm, "end": v(-6.1, 2.48) * mm});
            skLineSegment(sketch, "E1735", {"start": v(-6.1, 2.48) * mm, "end": v(-6.15, 2.48) * mm});
            skLineSegment(sketch, "E1736", {"start": v(-6.15, 2.48) * mm, "end": v(-6.2, 2.48) * mm});
            skLineSegment(sketch, "E1737", {"start": v(-6.2, 2.48) * mm, "end": v(-6.25, 2.48) * mm});
            skLineSegment(sketch, "E1738", {"start": v(-6.25, 2.48) * mm, "end": v(-6.3, 2.48) * mm});
            skLineSegment(sketch, "E1739", {"start": v(-6.3, 2.48) * mm, "end": v(-6.35, 2.48) * mm});
            skLineSegment(sketch, "E1740", {"start": v(-6.35, 2.48) * mm, "end": v(-6.4, 2.48) * mm});
            skLineSegment(sketch, "E1741", {"start": v(-6.4, 2.48) * mm, "end": v(-6.45, 2.48) * mm});
            skLineSegment(sketch, "E1742", {"start": v(-6.45, 2.48) * mm, "end": v(-6.5, 2.48) * mm});
            skLineSegment(sketch, "E1743", {"start": v(-6.5, 2.48) * mm, "end": v(-6.55, 2.48) * mm});
            skLineSegment(sketch, "E1744", {"start": v(-6.55, 2.48) * mm, "end": v(-6.6, 2.48) * mm});
            skLineSegment(sketch, "E1745", {"start": v(-6.6, 2.48) * mm, "end": v(-6.65, 2.48) * mm});
            skLineSegment(sketch, "E1746", {"start": v(-6.65, 2.48) * mm, "end": v(-6.7, 2.48) * mm});
            skLineSegment(sketch, "E1747", {"start": v(-6.7, 2.48) * mm, "end": v(-6.75, 2.48) * mm});
            skLineSegment(sketch, "E1748", {"start": v(-6.75, 2.48) * mm, "end": v(-6.8, 2.48) * mm});
            skLineSegment(sketch, "E1749", {"start": v(-6.8, 2.48) * mm, "end": v(-6.85, 2.48) * mm});
            skLineSegment(sketch, "E1750", {"start": v(-6.85, 2.48) * mm, "end": v(-6.9, 2.48) * mm});
            skLineSegment(sketch, "E1751", {"start": v(-6.9, 2.48) * mm, "end": v(-6.95, 2.48) * mm});
            skLineSegment(sketch, "E1752", {"start": v(-6.95, 2.48) * mm, "end": v(-7, 2.48) * mm});
            skLineSegment(sketch, "E1753", {"start": v(-7, 2.48) * mm, "end": v(-7.05, 2.48) * mm});
            skLineSegment(sketch, "E1754", {"start": v(-7.05, 2.48) * mm, "end": v(-7.1, 2.48) * mm});
            skLineSegment(sketch, "E1755", {"start": v(-7.1, 2.48) * mm, "end": v(-7.15, 2.48) * mm});
            skLineSegment(sketch, "E1756", {"start": v(-7.15, 2.48) * mm, "end": v(-7.2, 2.48) * mm});
            skLineSegment(sketch, "E1757", {"start": v(-7.2, 2.48) * mm, "end": v(-7.25, 2.48) * mm});
            skLineSegment(sketch, "E1758", {"start": v(-7.25, 2.48) * mm, "end": v(-7.3, 2.48) * mm});
            skLineSegment(sketch, "E1759", {"start": v(-7.3, 2.48) * mm, "end": v(-7.35, 2.48) * mm});
            skLineSegment(sketch, "E1760", {"start": v(-7.35, 2.48) * mm, "end": v(-7.4, 2.48) * mm});
            skLineSegment(sketch, "E1761", {"start": v(-7.4, 2.48) * mm, "end": v(-7.45, 2.48) * mm});
            skLineSegment(sketch, "E1762", {"start": v(-7.45, 2.48) * mm, "end": v(-7.5, 2.48) * mm});
            skLineSegment(sketch, "E1763", {"start": v(-7.5, 2.48) * mm, "end": v(-7.55, 2.48) * mm});
            skLineSegment(sketch, "E1764", {"start": v(-7.55, 2.48) * mm, "end": v(-7.6, 2.48) * mm});
            skLineSegment(sketch, "E1765", {"start": v(-7.6, 2.48) * mm, "end": v(-7.65, 2.48) * mm});
            skLineSegment(sketch, "E1766", {"start": v(-7.65, 2.48) * mm, "end": v(-7.7, 2.48) * mm});
            skLineSegment(sketch, "E1767", {"start": v(-7.7, 2.48) * mm, "end": v(-7.75, 2.48) * mm});
            skLineSegment(sketch, "E1768", {"start": v(-7.75, 2.48) * mm, "end": v(-7.8, 2.48) * mm});
            skLineSegment(sketch, "E1769", {"start": v(-7.8, 2.48) * mm, "end": v(-7.85, 2.48) * mm});
            skLineSegment(sketch, "E1770", {"start": v(-7.85, 2.48) * mm, "end": v(-7.9, 2.48) * mm});
            skLineSegment(sketch, "E1771", {"start": v(-7.9, 2.48) * mm, "end": v(-7.95, 2.48) * mm});
            skLineSegment(sketch, "E1772", {"start": v(-7.95, 2.48) * mm, "end": v(-8, 2.48) * mm});
            skLineSegment(sketch, "E1773", {"start": v(-8, 2.48) * mm, "end": v(-8.05, 2.48) * mm});
            skLineSegment(sketch, "E1774", {"start": v(-8.05, 2.48) * mm, "end": v(-8.1, 2.48) * mm});
            skLineSegment(sketch, "E1775", {"start": v(-8.1, 2.48) * mm, "end": v(-8.15, 2.48) * mm});
            skLineSegment(sketch, "E1776", {"start": v(-8.15, 2.48) * mm, "end": v(-8.2, 2.48) * mm});
            skLineSegment(sketch, "E1777", {"start": v(-8.2, 2.48) * mm, "end": v(-8.25, 2.48) * mm});
            skLineSegment(sketch, "E1778", {"start": v(-8.25, 2.48) * mm, "end": v(-8.3, 2.48) * mm});
            skLineSegment(sketch, "E1779", {"start": v(-8.3, 2.48) * mm, "end": v(-8.35, 2.48) * mm});
            skLineSegment(sketch, "E1780", {"start": v(-8.35, 2.48) * mm, "end": v(-8.4, 2.48) * mm});
            skLineSegment(sketch, "E1781", {"start": v(-8.4, 2.48) * mm, "end": v(-8.45, 2.48) * mm});
            skLineSegment(sketch, "E1782", {"start": v(-8.45, 2.48) * mm, "end": v(-8.5, 2.48) * mm});
            skLineSegment(sketch, "E1783", {"start": v(-8.5, 2.48) * mm, "end": v(-8.55, 2.48) * mm});
            skLineSegment(sketch, "E1784", {"start": v(-8.55, 2.48) * mm, "end": v(-8.6, 2.48) * mm});
            skLineSegment(sketch, "E1785", {"start": v(-8.6, 2.48) * mm, "end": v(-8.65, 2.48) * mm});
            skLineSegment(sketch, "E1786", {"start": v(-8.65, 2.48) * mm, "end": v(-8.7, 2.48) * mm});
            skLineSegment(sketch, "E1787", {"start": v(-8.7, 2.48) * mm, "end": v(-8.75, 2.48) * mm});
            skLineSegment(sketch, "E1788", {"start": v(-8.75, 2.48) * mm, "end": v(-8.8, 2.48) * mm});
            skLineSegment(sketch, "E1789", {"start": v(-8.8, 2.48) * mm, "end": v(-8.85, 2.48) * mm});
            skLineSegment(sketch, "E1790", {"start": v(-8.85, 2.48) * mm, "end": v(-8.9, 2.48) * mm});
            skLineSegment(sketch, "E1791", {"start": v(-8.9, 2.48) * mm, "end": v(-8.95, 2.48) * mm});
            skLineSegment(sketch, "E1792", {"start": v(-8.95, 2.48) * mm, "end": v(-9, 2.48) * mm});
            skLineSegment(sketch, "E1793", {"start": v(-9, 2.48) * mm, "end": v(-9.05, 2.48) * mm});
            skLineSegment(sketch, "E1794", {"start": v(-9.05, 2.48) * mm, "end": v(-9.1, 2.48) * mm});
            skLineSegment(sketch, "E1795", {"start": v(-9.1, 2.48) * mm, "end": v(-9.15, 2.48) * mm});
            skLineSegment(sketch, "E1796", {"start": v(-9.15, 2.48) * mm, "end": v(-9.2, 2.48) * mm});
            skLineSegment(sketch, "E1797", {"start": v(-9.2, 2.48) * mm, "end": v(-9.25, 2.48) * mm});
            skLineSegment(sketch, "E1798", {"start": v(-9.25, 2.48) * mm, "end": v(-9.3, 2.48) * mm});
            skLineSegment(sketch, "E1799", {"start": v(-9.3, 2.48) * mm, "end": v(-9.35, 2.48) * mm});
            skLineSegment(sketch, "E1800", {"start": v(-9.35, 2.48) * mm, "end": v(-9.4, 2.48) * mm});
            skLineSegment(sketch, "E1801", {"start": v(-9.4, 2.48) * mm, "end": v(-9.45, 2.48) * mm});
            skLineSegment(sketch, "E1802", {"start": v(-9.45, 2.48) * mm, "end": v(-9.5, 2.48) * mm});
            skLineSegment(sketch, "E1803", {"start": v(-9.5, 2.48) * mm, "end": v(-9.55, 2.48) * mm});
            skLineSegment(sketch, "E1804", {"start": v(-9.55, 2.48) * mm, "end": v(-9.6, 2.48) * mm});
            skLineSegment(sketch, "E1805", {"start": v(-9.6, 2.48) * mm, "end": v(-9.65, 2.48) * mm});
            skLineSegment(sketch, "E1806", {"start": v(-9.65, 2.48) * mm, "end": v(-9.7, 2.48) * mm});
            skLineSegment(sketch, "E1807", {"start": v(-9.7, 2.48) * mm, "end": v(-9.75, 2.48) * mm});
            skLineSegment(sketch, "E1808", {"start": v(-9.75, 2.48) * mm, "end": v(-9.8, 2.48) * mm});
            skLineSegment(sketch, "E1809", {"start": v(-9.8, 2.48) * mm, "end": v(-9.85, 2.48) * mm});
            skLineSegment(sketch, "E1810", {"start": v(-9.85, 2.48) * mm, "end": v(-9.9, 2.48) * mm});
            skLineSegment(sketch, "E1811", {"start": v(-9.9, 2.48) * mm, "end": v(-9.95, 2.48) * mm});
            skLineSegment(sketch, "E1812", {"start": v(-9.95, 2.48) * mm, "end": v(-10, 2.48) * mm});
            skLineSegment(sketch, "E1813", {"start": v(-10, 2.48) * mm, "end": v(-10.05, 2.48) * mm});
            skLineSegment(sketch, "E1814", {"start": v(-10.05, 2.48) * mm, "end": v(-10.1, 2.48) * mm});
            skLineSegment(sketch, "E1815", {"start": v(-10.1, 2.48) * mm, "end": v(-10.15, 2.48) * mm});
            skLineSegment(sketch, "E1816", {"start": v(-10.15, 2.48) * mm, "end": v(-10.2, 2.48) * mm});
            skLineSegment(sketch, "E1817", {"start": v(-10.2, 2.48) * mm, "end": v(-10.25, 2.48) * mm});
            skLineSegment(sketch, "E1818", {"start": v(-10.25, 2.48) * mm, "end": v(-10.3, 2.48) * mm});
            skLineSegment(sketch, "E1819", {"start": v(-10.3, 2.48) * mm, "end": v(-10.35, 2.48) * mm});
            skLineSegment(sketch, "E1820", {"start": v(-10.35, 2.48) * mm, "end": v(-10.4, 2.48) * mm});
            skLineSegment(sketch, "E1821", {"start": v(-10.4, 2.48) * mm, "end": v(-10.45, 2.48) * mm});
            skLineSegment(sketch, "E1822", {"start": v(-10.45, 2.48) * mm, "end": v(-10.5, 2.48) * mm});
            skLineSegment(sketch, "E1823", {"start": v(-10.5, 2.48) * mm, "end": v(-10.55, 2.48) * mm});
            skLineSegment(sketch, "E1824", {"start": v(-10.55, 2.48) * mm, "end": v(-10.6, 2.48) * mm});
            skLineSegment(sketch, "E1825", {"start": v(-10.6, 2.48) * mm, "end": v(-10.65, 2.48) * mm});
            skLineSegment(sketch, "E1826", {"start": v(-10.65, 2.48) * mm, "end": v(-10.7, 2.48) * mm});
            skLineSegment(sketch, "E1827", {"start": v(-10.7, 2.48) * mm, "end": v(-10.75, 2.48) * mm});
            skLineSegment(sketch, "E1828", {"start": v(-10.75, 2.48) * mm, "end": v(-10.8, 2.48) * mm});
            skLineSegment(sketch, "E1829", {"start": v(-10.8, 2.48) * mm, "end": v(-10.85, 2.48) * mm});
            skLineSegment(sketch, "E1830", {"start": v(-10.85, 2.48) * mm, "end": v(-10.9, 2.48) * mm});
            skLineSegment(sketch, "E1831", {"start": v(-10.9, 2.48) * mm, "end": v(-10.95, 2.48) * mm});
            skLineSegment(sketch, "E1832", {"start": v(-10.95, 2.48) * mm, "end": v(-11, 2.48) * mm});
            skLineSegment(sketch, "E1833", {"start": v(-11, 2.48) * mm, "end": v(-11.05, 2.48) * mm});
            skLineSegment(sketch, "E1834", {"start": v(-11.05, 2.48) * mm, "end": v(-11.1, 2.48) * mm});
            skLineSegment(sketch, "E1835", {"start": v(-11.1, 2.48) * mm, "end": v(-11.15, 2.48) * mm});
            skLineSegment(sketch, "E1836", {"start": v(-11.15, 2.48) * mm, "end": v(-11.2, 2.48) * mm});
            skLineSegment(sketch, "E1837", {"start": v(-11.2, 2.48) * mm, "end": v(-11.25, 2.48) * mm});
            skLineSegment(sketch, "E1838", {"start": v(-11.25, 2.48) * mm, "end": v(-11.3, 2.48) * mm});
            skLineSegment(sketch, "E1839", {"start": v(-11.3, 2.48) * mm, "end": v(-11.35, 2.48) * mm});
            skLineSegment(sketch, "E1840", {"start": v(-11.35, 2.48) * mm, "end": v(-11.4, 2.48) * mm});
            skLineSegment(sketch, "E1841", {"start": v(-11.4, 2.48) * mm, "end": v(-11.45, 2.48) * mm});
            skLineSegment(sketch, "E1842", {"start": v(-11.45, 2.48) * mm, "end": v(-11.5, 2.48) * mm});
            skLineSegment(sketch, "E1843", {"start": v(-11.5, 2.48) * mm, "end": v(-11.55, 2.48) * mm});
            skLineSegment(sketch, "E1844", {"start": v(-11.55, 2.48) * mm, "end": v(-11.6, 2.48) * mm});
            skLineSegment(sketch, "E1845", {"start": v(-11.6, 2.48) * mm, "end": v(-11.65, 2.48) * mm});
            skLineSegment(sketch, "E1846", {"start": v(-11.65, 2.48) * mm, "end": v(-11.7, 2.48) * mm});
            skLineSegment(sketch, "E1847", {"start": v(-11.7, 2.48) * mm, "end": v(-11.75, 2.48) * mm});
            skLineSegment(sketch, "E1848", {"start": v(-11.75, 2.48) * mm, "end": v(-11.8, 2.48) * mm});
            skLineSegment(sketch, "E1849", {"start": v(-11.8, 2.48) * mm, "end": v(-11.85, 2.48) * mm});
            skLineSegment(sketch, "E1850", {"start": v(-11.85, 2.48) * mm, "end": v(-11.9, 2.48) * mm});
            skLineSegment(sketch, "E1851", {"start": v(-11.9, 2.48) * mm, "end": v(-11.95, 2.48) * mm});
            skLineSegment(sketch, "E1852", {"start": v(-11.95, 2.48) * mm, "end": v(-12, 2.48) * mm});
            skLineSegment(sketch, "E1853", {"start": v(-12, 2.48) * mm, "end": v(-12.05, 2.48) * mm});
            skLineSegment(sketch, "E1854", {"start": v(-12.05, 2.48) * mm, "end": v(-12.1, 2.48) * mm});
            skLineSegment(sketch, "E1855", {"start": v(-12.1, 2.48) * mm, "end": v(-12.15, 2.48) * mm});
            skLineSegment(sketch, "E1856", {"start": v(-12.15, 2.48) * mm, "end": v(-12.2, 2.48) * mm});
            skLineSegment(sketch, "E1857", {"start": v(-12.2, 2.48) * mm, "end": v(-12.25, 2.48) * mm});
            skLineSegment(sketch, "E1858", {"start": v(-12.25, 2.48) * mm, "end": v(-12.3, 2.48) * mm});
            skLineSegment(sketch, "E1859", {"start": v(-12.3, 2.48) * mm, "end": v(-12.35, 2.48) * mm});
            skLineSegment(sketch, "E1860", {"start": v(-12.35, 2.48) * mm, "end": v(-12.4, 2.48) * mm});
            skLineSegment(sketch, "E1861", {"start": v(-12.4, 2.48) * mm, "end": v(-12.45, 2.48) * mm});
            skLineSegment(sketch, "E1862", {"start": v(-12.45, 2.48) * mm, "end": v(-12.5, 2.48) * mm});
            skLineSegment(sketch, "E1863", {"start": v(-12.5, 2.48) * mm, "end": v(-12.55, 2.48) * mm});
            skLineSegment(sketch, "E1864", {"start": v(-12.55, 2.48) * mm, "end": v(-12.6, 2.48) * mm});
            skLineSegment(sketch, "E1865", {"start": v(-12.6, 2.48) * mm, "end": v(-12.65, 2.48) * mm});
            skLineSegment(sketch, "E1866", {"start": v(-12.65, 2.48) * mm, "end": v(-12.7, 2.48) * mm});
            skLineSegment(sketch, "E1867", {"start": v(-12.7, 2.48) * mm, "end": v(-12.75, 2.48) * mm});
            skLineSegment(sketch, "E1868", {"start": v(-12.75, 2.48) * mm, "end": v(-12.8, 2.48) * mm});
            skLineSegment(sketch, "E1869", {"start": v(-12.8, 2.48) * mm, "end": v(-12.85, 2.48) * mm});
            skLineSegment(sketch, "E1870", {"start": v(-12.85, 2.48) * mm, "end": v(-12.9, 2.48) * mm});
            skLineSegment(sketch, "E1871", {"start": v(-12.9, 2.48) * mm, "end": v(-12.95, 2.48) * mm});
            skLineSegment(sketch, "E1872", {"start": v(-12.95, 2.48) * mm, "end": v(-13, 2.48) * mm});
            skLineSegment(sketch, "E1873", {"start": v(-13, 2.48) * mm, "end": v(-13.05, 2.48) * mm});
            skLineSegment(sketch, "E1874", {"start": v(-13.05, 2.48) * mm, "end": v(-13.1, 2.48) * mm});
            skLineSegment(sketch, "E1875", {"start": v(-13.1, 2.48) * mm, "end": v(-13.15, 2.48) * mm});
            skLineSegment(sketch, "E1876", {"start": v(-13.15, 2.48) * mm, "end": v(-13.2, 2.48) * mm});
            skLineSegment(sketch, "E1877", {"start": v(-13.2, 2.48) * mm, "end": v(-13.25, 2.48) * mm});
            skLineSegment(sketch, "E1878", {"start": v(-13.25, 2.48) * mm, "end": v(-13.3, 2.48) * mm});
            skLineSegment(sketch, "E1879", {"start": v(-13.3, 2.48) * mm, "end": v(-13.35, 2.48) * mm});
            skLineSegment(sketch, "E1880", {"start": v(-13.35, 2.48) * mm, "end": v(-13.4, 2.48) * mm});
            skLineSegment(sketch, "E1881", {"start": v(-13.4, 2.48) * mm, "end": v(-13.45, 2.48) * mm});
            skLineSegment(sketch, "E1882", {"start": v(-13.45, 2.48) * mm, "end": v(-13.5, 2.48) * mm});
            skLineSegment(sketch, "E1883", {"start": v(-13.5, 2.48) * mm, "end": v(-13.55, 2.48) * mm});
            skLineSegment(sketch, "E1884", {"start": v(-13.55, 2.48) * mm, "end": v(-13.6, 2.48) * mm});
            skLineSegment(sketch, "E1885", {"start": v(-13.6, 2.48) * mm, "end": v(-13.65, 2.48) * mm});
            skLineSegment(sketch, "E1886", {"start": v(-13.65, 2.48) * mm, "end": v(-13.7, 2.48) * mm});
            skLineSegment(sketch, "E1887", {"start": v(-13.7, 2.48) * mm, "end": v(-13.75, 2.48) * mm});
            skLineSegment(sketch, "E1888", {"start": v(-13.75, 2.48) * mm, "end": v(-13.8, 2.48) * mm});
            skLineSegment(sketch, "E1889", {"start": v(-13.8, 2.48) * mm, "end": v(-13.85, 2.48) * mm});
            skLineSegment(sketch, "E1890", {"start": v(-13.85, 2.48) * mm, "end": v(-13.9, 2.48) * mm});
            skLineSegment(sketch, "E1891", {"start": v(-13.9, 2.48) * mm, "end": v(-13.95, 2.48) * mm});
            skLineSegment(sketch, "E1892", {"start": v(-13.95, 2.48) * mm, "end": v(-14, 2.48) * mm});
            skLineSegment(sketch, "E1893", {"start": v(-14, 2.48) * mm, "end": v(-14.05, 2.48) * mm});
            skLineSegment(sketch, "E1894", {"start": v(-14.05, 2.48) * mm, "end": v(-14.1, 2.48) * mm});
            skLineSegment(sketch, "E1895", {"start": v(-14.1, 2.48) * mm, "end": v(-14.4, 2.43) * mm});
            skLineSegment(sketch, "E1896", {"start": v(-14.4, 2.43) * mm, "end": v(-14.5, 2.23) * mm});
            skLineSegment(sketch, "E1897", {"start": v(-14.5, 2.23) * mm, "end": v(-14.55, 1.98) * mm});
            skLineSegment(sketch, "E1898", {"start": v(-14.55, 1.98) * mm, "end": v(-14.65, 1.98) * mm});
            skLineSegment(sketch, "E1899", {"start": v(-14.65, 1.98) * mm, "end": v(-14.8, 1.68) * mm});
            skLineSegment(sketch, "E1900", {"start": v(-14.8, 1.68) * mm, "end": v(-14.8, 1.48) * mm});
            skLineSegment(sketch, "E1901", {"start": v(-14.8, 1.48) * mm, "end": v(-14.95, 1.17) * mm});
            skLineSegment(sketch, "E1902", {"start": v(-14.95, 1.18) * mm, "end": v(-15.05, 1.18) * mm});
            skLineSegment(sketch, "E1903", {"start": v(-15.05, 1.18) * mm, "end": v(-15.2, 0.87) * mm});
            skLineSegment(sketch, "E1904", {"start": v(-15.2, 0.88) * mm, "end": v(-15.25, 0.63) * mm});
            skLineSegment(sketch, "E1905", {"start": v(-15.25, 0.63) * mm, "end": v(-15.3, 0.63) * mm});
            skLineSegment(sketch, "E1906", {"start": v(-15.3, 0.63) * mm, "end": v(-15.35, 0.38) * mm});
            skLineSegment(sketch, "E1907", {"start": v(-15.35, 0.38) * mm, "end": v(-15.45, 0.38) * mm});
            skLineSegment(sketch, "E1908", {"start": v(-15.45, 0.38) * mm, "end": v(-15.6, 0.07) * mm});
            skLineSegment(sketch, "E1909", {"start": v(-15.6, 0.08) * mm, "end": v(-15.75, -0.23) * mm});
            skLineSegment(sketch, "E1910", {"start": v(-15.75, -0.22) * mm, "end": v(-15.75, -0.37) * mm});
            skLineSegment(sketch, "E1911", {"start": v(-15.75, -0.37) * mm, "end": v(-15.85, -0.42) * mm});
            skLineSegment(sketch, "E1912", {"start": v(-15.85, -0.42) * mm, "end": v(-16, -0.73) * mm});
            skLineSegment(sketch, "E1913", {"start": v(-16, -0.72) * mm, "end": v(-16.15, -1.02) * mm});
            skLineSegment(sketch, "E1914", {"start": v(-16.15, -1.02) * mm, "end": v(-16.15, -1.17) * mm});
            skLineSegment(sketch, "E1915", {"start": v(-16.15, -1.17) * mm, "end": v(-16.25, -1.23) * mm});
            skLineSegment(sketch, "E1916", {"start": v(-16.25, -1.22) * mm, "end": v(-16.4, -1.62) * mm});
            skLineSegment(sketch, "E1917", {"start": v(-16.4, -1.62) * mm, "end": v(-16.2, -1.62) * mm});
            skLineSegment(sketch, "E1918", {"start": v(-16.2, -1.62) * mm, "end": v(-16.15, -1.62) * mm});
            skLineSegment(sketch, "E1919", {"start": v(-16.15, -1.62) * mm, "end": v(-16.1, -1.62) * mm});
            skLineSegment(sketch, "E1920", {"start": v(-16.1, -1.62) * mm, "end": v(-16.05, -1.62) * mm});
            skLineSegment(sketch, "E1921", {"start": v(-16.05, -1.62) * mm, "end": v(-16, -1.62) * mm});
            skLineSegment(sketch, "E1922", {"start": v(-16, -1.62) * mm, "end": v(-15.95, -1.62) * mm});
            skLineSegment(sketch, "E1923", {"start": v(-15.95, -1.62) * mm, "end": v(-15.9, -1.62) * mm});
            skLineSegment(sketch, "E1924", {"start": v(-15.9, -1.62) * mm, "end": v(-15.85, -1.62) * mm});
            skLineSegment(sketch, "E1925", {"start": v(-15.85, -1.62) * mm, "end": v(-15.8, -1.62) * mm});
            skLineSegment(sketch, "E1926", {"start": v(-15.8, -1.62) * mm, "end": v(-15.75, -1.62) * mm});
            skLineSegment(sketch, "E1927", {"start": v(-15.75, -1.62) * mm, "end": v(-15.7, -1.62) * mm});
            skLineSegment(sketch, "E1928", {"start": v(-15.7, -1.62) * mm, "end": v(-15.65, -1.62) * mm});
            skLineSegment(sketch, "E1929", {"start": v(-15.65, -1.62) * mm, "end": v(-15.6, -1.62) * mm});
            skLineSegment(sketch, "E1930", {"start": v(-15.6, -1.62) * mm, "end": v(-15.55, -1.62) * mm});
            skLineSegment(sketch, "E1931", {"start": v(-15.55, -1.62) * mm, "end": v(-15.5, -1.62) * mm});
            skLineSegment(sketch, "E1932", {"start": v(-15.5, -1.62) * mm, "end": v(-15.45, -1.62) * mm});
            skLineSegment(sketch, "E1933", {"start": v(-15.45, -1.62) * mm, "end": v(-15.4, -1.62) * mm});
            skLineSegment(sketch, "E1934", {"start": v(-15.4, -1.62) * mm, "end": v(-15.35, -1.62) * mm});
            skLineSegment(sketch, "E1935", {"start": v(-15.35, -1.62) * mm, "end": v(-15.3, -1.62) * mm});
            skLineSegment(sketch, "E1936", {"start": v(-15.3, -1.62) * mm, "end": v(-15.25, -1.62) * mm});
            skLineSegment(sketch, "E1937", {"start": v(-15.25, -1.62) * mm, "end": v(-15.2, -1.62) * mm});
            skLineSegment(sketch, "E1938", {"start": v(-15.2, -1.62) * mm, "end": v(-15.15, -1.62) * mm});
            skLineSegment(sketch, "E1939", {"start": v(-15.15, -1.62) * mm, "end": v(-15.1, -1.62) * mm});
            skLineSegment(sketch, "E1940", {"start": v(-15.1, -1.62) * mm, "end": v(-15.05, -1.62) * mm});
            skLineSegment(sketch, "E1941", {"start": v(-15.05, -1.62) * mm, "end": v(-15, -1.62) * mm});
            skLineSegment(sketch, "E1942", {"start": v(-15, -1.62) * mm, "end": v(-14.95, -1.62) * mm});
            skLineSegment(sketch, "E1943", {"start": v(-14.95, -1.62) * mm, "end": v(-14.9, -1.62) * mm});
            skLineSegment(sketch, "E1944", {"start": v(-14.9, -1.62) * mm, "end": v(-14.85, -1.62) * mm});
            skLineSegment(sketch, "E1945", {"start": v(-14.85, -1.62) * mm, "end": v(-14.8, -1.62) * mm});
            skLineSegment(sketch, "E1946", {"start": v(-14.8, -1.62) * mm, "end": v(-14.75, -1.62) * mm});
            skLineSegment(sketch, "E1947", {"start": v(-14.75, -1.62) * mm, "end": v(-14.7, -1.62) * mm});
            skLineSegment(sketch, "E1948", {"start": v(-14.7, -1.62) * mm, "end": v(-14.65, -1.62) * mm});
            skLineSegment(sketch, "E1949", {"start": v(-14.65, -1.62) * mm, "end": v(-14.6, -1.62) * mm});
            skLineSegment(sketch, "E1950", {"start": v(-14.6, -1.62) * mm, "end": v(-14.55, -1.62) * mm});
            skLineSegment(sketch, "E1951", {"start": v(-14.55, -1.62) * mm, "end": v(-14.5, -1.62) * mm});
            skLineSegment(sketch, "E1952", {"start": v(-14.5, -1.62) * mm, "end": v(-14.45, -1.62) * mm});
            skLineSegment(sketch, "E1953", {"start": v(-14.45, -1.62) * mm, "end": v(-14.4, -1.62) * mm});
            skLineSegment(sketch, "E1954", {"start": v(-14.4, -1.62) * mm, "end": v(-14.35, -1.62) * mm});
            skLineSegment(sketch, "E1955", {"start": v(-14.35, -1.62) * mm, "end": v(-14.3, -1.62) * mm});
            skLineSegment(sketch, "E1956", {"start": v(-14.3, -1.62) * mm, "end": v(-14.25, -1.62) * mm});
            skLineSegment(sketch, "E1957", {"start": v(-14.25, -1.62) * mm, "end": v(-14.2, -1.62) * mm});
            skLineSegment(sketch, "E1958", {"start": v(-14.2, -1.62) * mm, "end": v(-14.15, -1.62) * mm});
            skLineSegment(sketch, "E1959", {"start": v(-14.15, -1.62) * mm, "end": v(-14.1, -1.62) * mm});
            skLineSegment(sketch, "E1960", {"start": v(-14.1, -1.62) * mm, "end": v(-14.05, -1.62) * mm});
            skLineSegment(sketch, "E1961", {"start": v(-14.05, -1.62) * mm, "end": v(-14, -1.62) * mm});
            skLineSegment(sketch, "E1962", {"start": v(-14, -1.62) * mm, "end": v(-13.95, -1.62) * mm});
            skLineSegment(sketch, "E1963", {"start": v(-13.95, -1.62) * mm, "end": v(-13.9, -1.62) * mm});
            skLineSegment(sketch, "E1964", {"start": v(-13.9, -1.62) * mm, "end": v(-13.85, -1.62) * mm});
            skLineSegment(sketch, "E1965", {"start": v(-13.85, -1.62) * mm, "end": v(-13.8, -1.62) * mm});
            skLineSegment(sketch, "E1966", {"start": v(-13.8, -1.62) * mm, "end": v(-13.75, -1.62) * mm});
            skLineSegment(sketch, "E1967", {"start": v(-13.75, -1.62) * mm, "end": v(-13.7, -1.62) * mm});
            skLineSegment(sketch, "E1968", {"start": v(-13.7, -1.62) * mm, "end": v(-13.65, -1.62) * mm});
            skLineSegment(sketch, "E1969", {"start": v(-13.65, -1.62) * mm, "end": v(-13.6, -1.62) * mm});
            skLineSegment(sketch, "E1970", {"start": v(-13.6, -1.62) * mm, "end": v(-13.55, -1.62) * mm});
            skLineSegment(sketch, "E1971", {"start": v(-13.55, -1.62) * mm, "end": v(-13.5, -1.62) * mm});
            skLineSegment(sketch, "E1972", {"start": v(-13.5, -1.62) * mm, "end": v(-13.45, -1.62) * mm});
            skLineSegment(sketch, "E1973", {"start": v(-13.45, -1.62) * mm, "end": v(-13.4, -1.62) * mm});
            skLineSegment(sketch, "E1974", {"start": v(-13.4, -1.62) * mm, "end": v(-13.35, -1.62) * mm});
            skLineSegment(sketch, "E1975", {"start": v(-13.35, -1.62) * mm, "end": v(-13.3, -1.62) * mm});
            skLineSegment(sketch, "E1976", {"start": v(-13.3, -1.62) * mm, "end": v(-13.25, -1.62) * mm});
            skLineSegment(sketch, "E1977", {"start": v(-13.25, -1.62) * mm, "end": v(-13.2, -1.62) * mm});
            skLineSegment(sketch, "E1978", {"start": v(-13.2, -1.62) * mm, "end": v(-13.15, -1.62) * mm});
            skLineSegment(sketch, "E1979", {"start": v(-13.15, -1.62) * mm, "end": v(-13.1, -1.62) * mm});
            skLineSegment(sketch, "E1980", {"start": v(-13.1, -1.62) * mm, "end": v(-13.05, -1.62) * mm});
            skLineSegment(sketch, "E1981", {"start": v(-13.05, -1.62) * mm, "end": v(-13, -1.62) * mm});
            skLineSegment(sketch, "E1982", {"start": v(-13, -1.62) * mm, "end": v(-12.95, -1.62) * mm});
            skLineSegment(sketch, "E1983", {"start": v(-12.95, -1.62) * mm, "end": v(-12.9, -1.62) * mm});
            skLineSegment(sketch, "E1984", {"start": v(-12.9, -1.62) * mm, "end": v(-12.85, -1.62) * mm});
            skLineSegment(sketch, "E1985", {"start": v(-12.85, -1.62) * mm, "end": v(-12.8, -1.62) * mm});
            skLineSegment(sketch, "E1986", {"start": v(-12.8, -1.62) * mm, "end": v(-12.75, -1.62) * mm});
            skLineSegment(sketch, "E1987", {"start": v(-12.75, -1.62) * mm, "end": v(-12.7, -1.62) * mm});
            skLineSegment(sketch, "E1988", {"start": v(-12.7, -1.62) * mm, "end": v(-12.65, -1.62) * mm});
            skLineSegment(sketch, "E1989", {"start": v(-12.65, -1.62) * mm, "end": v(-12.6, -1.62) * mm});
            skLineSegment(sketch, "E1990", {"start": v(-12.6, -1.62) * mm, "end": v(-12.55, -1.62) * mm});
            skLineSegment(sketch, "E1991", {"start": v(-12.55, -1.62) * mm, "end": v(-12.5, -1.62) * mm});
            skLineSegment(sketch, "E1992", {"start": v(-12.5, -1.62) * mm, "end": v(-12.45, -1.62) * mm});
            skLineSegment(sketch, "E1993", {"start": v(-12.45, -1.62) * mm, "end": v(-12.4, -1.62) * mm});
            skLineSegment(sketch, "E1994", {"start": v(-12.4, -1.62) * mm, "end": v(-12.35, -1.62) * mm});
            skLineSegment(sketch, "E1995", {"start": v(-12.35, -1.62) * mm, "end": v(-12.3, -1.62) * mm});
            skLineSegment(sketch, "E1996", {"start": v(-12.3, -1.62) * mm, "end": v(-12.25, -1.62) * mm});
            skLineSegment(sketch, "E1997", {"start": v(-12.25, -1.62) * mm, "end": v(-12.2, -1.62) * mm});
            skLineSegment(sketch, "E1998", {"start": v(-12.2, -1.62) * mm, "end": v(-12.15, -1.62) * mm});
            skLineSegment(sketch, "E1999", {"start": v(-12.15, -1.62) * mm, "end": v(-12.1, -1.62) * mm});
            skLineSegment(sketch, "E2000", {"start": v(-12.1, -1.62) * mm, "end": v(-12.05, -1.62) * mm});
            skLineSegment(sketch, "E2001", {"start": v(-12.05, -1.62) * mm, "end": v(-12, -1.62) * mm});
            skLineSegment(sketch, "E2002", {"start": v(-12, -1.62) * mm, "end": v(-11.95, -1.62) * mm});
            skLineSegment(sketch, "E2003", {"start": v(-11.95, -1.62) * mm, "end": v(-11.9, -1.62) * mm});
            skLineSegment(sketch, "E2004", {"start": v(-11.9, -1.62) * mm, "end": v(-11.85, -1.62) * mm});
            skLineSegment(sketch, "E2005", {"start": v(-11.85, -1.62) * mm, "end": v(-11.8, -1.62) * mm});
            skLineSegment(sketch, "E2006", {"start": v(-11.8, -1.62) * mm, "end": v(-11.75, -1.62) * mm});
            skLineSegment(sketch, "E2007", {"start": v(-11.75, -1.62) * mm, "end": v(-11.7, -1.62) * mm});
            skLineSegment(sketch, "E2008", {"start": v(-11.7, -1.62) * mm, "end": v(-11.65, -1.62) * mm});
            skLineSegment(sketch, "E2009", {"start": v(-11.65, -1.62) * mm, "end": v(-11.6, -1.62) * mm});
            skLineSegment(sketch, "E2010", {"start": v(-11.6, -1.62) * mm, "end": v(-11.55, -1.62) * mm});
            skLineSegment(sketch, "E2011", {"start": v(-11.55, -1.62) * mm, "end": v(-11.5, -1.62) * mm});
            skLineSegment(sketch, "E2012", {"start": v(-11.5, -1.62) * mm, "end": v(-11.45, -1.62) * mm});
            skLineSegment(sketch, "E2013", {"start": v(-11.45, -1.62) * mm, "end": v(-11.4, -1.62) * mm});
            skLineSegment(sketch, "E2014", {"start": v(-11.4, -1.62) * mm, "end": v(-11.35, -1.62) * mm});
            skLineSegment(sketch, "E2015", {"start": v(-11.35, -1.62) * mm, "end": v(-11.3, -1.62) * mm});
            skLineSegment(sketch, "E2016", {"start": v(-11.3, -1.62) * mm, "end": v(-11.25, -1.62) * mm});
            skLineSegment(sketch, "E2017", {"start": v(-11.25, -1.62) * mm, "end": v(-11.2, -1.62) * mm});
            skLineSegment(sketch, "E2018", {"start": v(-11.2, -1.62) * mm, "end": v(-11.15, -1.62) * mm});
            skLineSegment(sketch, "E2019", {"start": v(-11.15, -1.62) * mm, "end": v(-11.1, -1.62) * mm});
            skLineSegment(sketch, "E2020", {"start": v(-11.1, -1.62) * mm, "end": v(-11.05, -1.62) * mm});
            skLineSegment(sketch, "E2021", {"start": v(-11.05, -1.62) * mm, "end": v(-11, -1.62) * mm});
            skLineSegment(sketch, "E2022", {"start": v(-11, -1.62) * mm, "end": v(-10.95, -1.62) * mm});
            skLineSegment(sketch, "E2023", {"start": v(-10.95, -1.62) * mm, "end": v(-10.9, -1.62) * mm});
            skLineSegment(sketch, "E2024", {"start": v(-10.9, -1.62) * mm, "end": v(-10.85, -1.62) * mm});
            skLineSegment(sketch, "E2025", {"start": v(-10.85, -1.62) * mm, "end": v(-10.8, -1.62) * mm});
            skLineSegment(sketch, "E2026", {"start": v(-10.8, -1.62) * mm, "end": v(-10.75, -1.62) * mm});
            skLineSegment(sketch, "E2027", {"start": v(-10.75, -1.62) * mm, "end": v(-10.7, -1.62) * mm});
            skLineSegment(sketch, "E2028", {"start": v(-10.7, -1.62) * mm, "end": v(-10.65, -1.62) * mm});
            skLineSegment(sketch, "E2029", {"start": v(-10.65, -1.62) * mm, "end": v(-10.6, -1.62) * mm});
            skLineSegment(sketch, "E2030", {"start": v(-10.6, -1.62) * mm, "end": v(-10.55, -1.62) * mm});
            skLineSegment(sketch, "E2031", {"start": v(-10.55, -1.62) * mm, "end": v(-10.5, -1.62) * mm});
            skLineSegment(sketch, "E2032", {"start": v(-10.5, -1.62) * mm, "end": v(-10.45, -1.62) * mm});
            skLineSegment(sketch, "E2033", {"start": v(-10.45, -1.62) * mm, "end": v(-10.4, -1.62) * mm});
            skLineSegment(sketch, "E2034", {"start": v(-10.4, -1.62) * mm, "end": v(-10.35, -1.62) * mm});
            skLineSegment(sketch, "E2035", {"start": v(-10.35, -1.62) * mm, "end": v(-10.3, -1.62) * mm});
            skLineSegment(sketch, "E2036", {"start": v(-10.3, -1.62) * mm, "end": v(-10.25, -1.62) * mm});
            skLineSegment(sketch, "E2037", {"start": v(-10.25, -1.62) * mm, "end": v(-10.2, -1.62) * mm});
            skLineSegment(sketch, "E2038", {"start": v(-10.2, -1.62) * mm, "end": v(-10.15, -1.62) * mm});
            skLineSegment(sketch, "E2039", {"start": v(-10.15, -1.62) * mm, "end": v(-10.1, -1.62) * mm});
            skLineSegment(sketch, "E2040", {"start": v(-10.1, -1.62) * mm, "end": v(-10.05, -1.62) * mm});
            skLineSegment(sketch, "E2041", {"start": v(-10.05, -1.62) * mm, "end": v(-10, -1.62) * mm});
            skLineSegment(sketch, "E2042", {"start": v(-10, -1.62) * mm, "end": v(-9.95, -1.62) * mm});
            skLineSegment(sketch, "E2043", {"start": v(-9.95, -1.62) * mm, "end": v(-9.9, -1.62) * mm});
            skLineSegment(sketch, "E2044", {"start": v(-9.9, -1.62) * mm, "end": v(-9.85, -1.62) * mm});
            skLineSegment(sketch, "E2045", {"start": v(-9.85, -1.62) * mm, "end": v(-9.8, -1.62) * mm});
            skLineSegment(sketch, "E2046", {"start": v(-9.8, -1.62) * mm, "end": v(-9.75, -1.62) * mm});
            skLineSegment(sketch, "E2047", {"start": v(-9.75, -1.62) * mm, "end": v(-9.7, -1.62) * mm});
            skLineSegment(sketch, "E2048", {"start": v(-9.7, -1.62) * mm, "end": v(-9.65, -1.62) * mm});
            skLineSegment(sketch, "E2049", {"start": v(-9.65, -1.62) * mm, "end": v(-9.6, -1.62) * mm});
            skLineSegment(sketch, "E2050", {"start": v(-9.6, -1.62) * mm, "end": v(-9.55, -1.62) * mm});
            skLineSegment(sketch, "E2051", {"start": v(-9.55, -1.62) * mm, "end": v(-9.5, -1.62) * mm});
            skLineSegment(sketch, "E2052", {"start": v(-9.5, -1.62) * mm, "end": v(-9.45, -1.62) * mm});
            skLineSegment(sketch, "E2053", {"start": v(-9.45, -1.62) * mm, "end": v(-9.4, -1.62) * mm});
            skLineSegment(sketch, "E2054", {"start": v(-9.4, -1.62) * mm, "end": v(-9.35, -1.62) * mm});
            skLineSegment(sketch, "E2055", {"start": v(-9.35, -1.62) * mm, "end": v(-9.3, -1.62) * mm});
            skLineSegment(sketch, "E2056", {"start": v(-9.3, -1.62) * mm, "end": v(-9.25, -1.62) * mm});
            skLineSegment(sketch, "E2057", {"start": v(-9.25, -1.62) * mm, "end": v(-9.2, -1.62) * mm});
            skLineSegment(sketch, "E2058", {"start": v(-9.2, -1.62) * mm, "end": v(-9.15, -1.62) * mm});
            skLineSegment(sketch, "E2059", {"start": v(-9.15, -1.62) * mm, "end": v(-9.1, -1.62) * mm});
            skLineSegment(sketch, "E2060", {"start": v(-9.1, -1.62) * mm, "end": v(-9.05, -1.62) * mm});
            skLineSegment(sketch, "E2061", {"start": v(-9.05, -1.62) * mm, "end": v(-9, -1.62) * mm});
            skLineSegment(sketch, "E2062", {"start": v(-9, -1.62) * mm, "end": v(-8.95, -1.62) * mm});
            skLineSegment(sketch, "E2063", {"start": v(-8.95, -1.62) * mm, "end": v(-8.9, -1.62) * mm});
            skLineSegment(sketch, "E2064", {"start": v(-8.9, -1.62) * mm, "end": v(-8.85, -1.62) * mm});
            skLineSegment(sketch, "E2065", {"start": v(-8.85, -1.62) * mm, "end": v(-8.8, -1.62) * mm});
            skLineSegment(sketch, "E2066", {"start": v(-8.8, -1.62) * mm, "end": v(-8.75, -1.62) * mm});
            skLineSegment(sketch, "E2067", {"start": v(-8.75, -1.62) * mm, "end": v(-8.7, -1.62) * mm});
            skLineSegment(sketch, "E2068", {"start": v(-8.7, -1.62) * mm, "end": v(-8.65, -1.62) * mm});
            skLineSegment(sketch, "E2069", {"start": v(-8.65, -1.62) * mm, "end": v(-8.6, -1.62) * mm});
            skLineSegment(sketch, "E2070", {"start": v(-8.6, -1.62) * mm, "end": v(-8.55, -1.62) * mm});
            skLineSegment(sketch, "E2071", {"start": v(-8.55, -1.62) * mm, "end": v(-8.5, -1.62) * mm});
            skLineSegment(sketch, "E2072", {"start": v(-8.5, -1.62) * mm, "end": v(-8.45, -1.62) * mm});
            skLineSegment(sketch, "E2073", {"start": v(-8.45, -1.62) * mm, "end": v(-8.4, -1.62) * mm});
            skLineSegment(sketch, "E2074", {"start": v(-8.4, -1.62) * mm, "end": v(-8.35, -1.62) * mm});
            skLineSegment(sketch, "E2075", {"start": v(-8.35, -1.62) * mm, "end": v(-8.3, -1.62) * mm});
            skLineSegment(sketch, "E2076", {"start": v(-8.3, -1.62) * mm, "end": v(-8.25, -1.62) * mm});
            skLineSegment(sketch, "E2077", {"start": v(-8.25, -1.62) * mm, "end": v(-8.2, -1.62) * mm});
            skLineSegment(sketch, "E2078", {"start": v(-8.2, -1.62) * mm, "end": v(-8.15, -1.62) * mm});
            skLineSegment(sketch, "E2079", {"start": v(-8.15, -1.62) * mm, "end": v(-8.1, -1.62) * mm});
            skLineSegment(sketch, "E2080", {"start": v(-8.1, -1.62) * mm, "end": v(-8.05, -1.62) * mm});
            skLineSegment(sketch, "E2081", {"start": v(-8.05, -1.62) * mm, "end": v(-8, -1.62) * mm});
            skLineSegment(sketch, "E2082", {"start": v(-8, -1.62) * mm, "end": v(-7.95, -1.62) * mm});
            skLineSegment(sketch, "E2083", {"start": v(-7.95, -1.62) * mm, "end": v(-7.9, -1.62) * mm});
            skLineSegment(sketch, "E2084", {"start": v(-7.9, -1.62) * mm, "end": v(-7.85, -1.62) * mm});
            skLineSegment(sketch, "E2085", {"start": v(-7.85, -1.62) * mm, "end": v(-7.8, -1.62) * mm});
            skLineSegment(sketch, "E2086", {"start": v(-7.8, -1.62) * mm, "end": v(-7.75, -1.62) * mm});
            skLineSegment(sketch, "E2087", {"start": v(-7.75, -1.62) * mm, "end": v(-7.7, -1.62) * mm});
            skLineSegment(sketch, "E2088", {"start": v(-7.7, -1.62) * mm, "end": v(-7.65, -1.62) * mm});
            skLineSegment(sketch, "E2089", {"start": v(-7.65, -1.62) * mm, "end": v(-7.6, -1.62) * mm});
            skLineSegment(sketch, "E2090", {"start": v(-7.6, -1.62) * mm, "end": v(-7.55, -1.62) * mm});
            skLineSegment(sketch, "E2091", {"start": v(-7.55, -1.62) * mm, "end": v(-7.5, -1.62) * mm});
            skLineSegment(sketch, "E2092", {"start": v(-7.5, -1.62) * mm, "end": v(-7.45, -1.62) * mm});
            skLineSegment(sketch, "E2093", {"start": v(-7.45, -1.62) * mm, "end": v(-7.4, -1.62) * mm});
            skLineSegment(sketch, "E2094", {"start": v(-7.4, -1.62) * mm, "end": v(-7.35, -1.62) * mm});
            skLineSegment(sketch, "E2095", {"start": v(-7.35, -1.62) * mm, "end": v(-7.3, -1.62) * mm});
            skLineSegment(sketch, "E2096", {"start": v(-7.3, -1.62) * mm, "end": v(-7.25, -1.62) * mm});
            skLineSegment(sketch, "E2097", {"start": v(-7.25, -1.62) * mm, "end": v(-7.2, -1.62) * mm});
            skLineSegment(sketch, "E2098", {"start": v(-7.2, -1.62) * mm, "end": v(-7.15, -1.62) * mm});
            skLineSegment(sketch, "E2099", {"start": v(-7.15, -1.62) * mm, "end": v(-7.1, -1.62) * mm});
            skLineSegment(sketch, "E2100", {"start": v(-7.1, -1.62) * mm, "end": v(-7.05, -1.62) * mm});
            skLineSegment(sketch, "E2101", {"start": v(-7.05, -1.62) * mm, "end": v(-7, -1.62) * mm});
            skLineSegment(sketch, "E2102", {"start": v(-7, -1.62) * mm, "end": v(-6.95, -1.62) * mm});
            skLineSegment(sketch, "E2103", {"start": v(-6.95, -1.62) * mm, "end": v(-6.9, -1.62) * mm});
            skLineSegment(sketch, "E2104", {"start": v(-6.9, -1.62) * mm, "end": v(-6.85, -1.62) * mm});
            skLineSegment(sketch, "E2105", {"start": v(-6.85, -1.62) * mm, "end": v(-6.8, -1.62) * mm});
            skLineSegment(sketch, "E2106", {"start": v(-6.8, -1.62) * mm, "end": v(-6.75, -1.62) * mm});
            skLineSegment(sketch, "E2107", {"start": v(-6.75, -1.62) * mm, "end": v(-6.7, -1.62) * mm});
            skLineSegment(sketch, "E2108", {"start": v(-6.7, -1.62) * mm, "end": v(-6.65, -1.62) * mm});
            skLineSegment(sketch, "E2109", {"start": v(-6.65, -1.62) * mm, "end": v(-6.6, -1.62) * mm});
            skLineSegment(sketch, "E2110", {"start": v(-6.6, -1.62) * mm, "end": v(-6.55, -1.62) * mm});
            skLineSegment(sketch, "E2111", {"start": v(-6.55, -1.62) * mm, "end": v(-6.5, -1.62) * mm});
            skLineSegment(sketch, "E2112", {"start": v(-6.5, -1.62) * mm, "end": v(-6.45, -1.62) * mm});
            skLineSegment(sketch, "E2113", {"start": v(-6.45, -1.62) * mm, "end": v(-6.4, -1.62) * mm});
            skLineSegment(sketch, "E2114", {"start": v(-6.4, -1.62) * mm, "end": v(-6.35, -1.62) * mm});
            skLineSegment(sketch, "E2115", {"start": v(-6.35, -1.62) * mm, "end": v(-6.3, -1.62) * mm});
            skLineSegment(sketch, "E2116", {"start": v(-6.3, -1.62) * mm, "end": v(-6.25, -1.62) * mm});
            skLineSegment(sketch, "E2117", {"start": v(-6.25, -1.62) * mm, "end": v(-6.2, -1.62) * mm});
            skLineSegment(sketch, "E2118", {"start": v(-6.2, -1.62) * mm, "end": v(-6.15, -1.62) * mm});
            skLineSegment(sketch, "E2119", {"start": v(-6.15, -1.62) * mm, "end": v(-6.1, -1.62) * mm});
            skLineSegment(sketch, "E2120", {"start": v(-6.1, -1.62) * mm, "end": v(-6.05, -1.62) * mm});
            skLineSegment(sketch, "E2121", {"start": v(-6.05, -1.62) * mm, "end": v(-6, -1.62) * mm});
            skLineSegment(sketch, "E2122", {"start": v(-6, -1.62) * mm, "end": v(-5.95, -1.62) * mm});
            skLineSegment(sketch, "E2123", {"start": v(-5.95, -1.62) * mm, "end": v(-5.9, -1.62) * mm});
            skLineSegment(sketch, "E2124", {"start": v(-5.9, -1.62) * mm, "end": v(-5.85, -1.62) * mm});
            skLineSegment(sketch, "E2125", {"start": v(-5.85, -1.62) * mm, "end": v(-5.8, -1.62) * mm});
            skLineSegment(sketch, "E2126", {"start": v(-5.8, -1.62) * mm, "end": v(-5.75, -1.62) * mm});
            skLineSegment(sketch, "E2127", {"start": v(-5.75, -1.62) * mm, "end": v(-5.7, -1.62) * mm});
            skLineSegment(sketch, "E2128", {"start": v(-5.7, -1.62) * mm, "end": v(-5.65, -1.62) * mm});
            skLineSegment(sketch, "E2129", {"start": v(-5.65, -1.62) * mm, "end": v(-5.6, -1.62) * mm});
            skLineSegment(sketch, "E2130", {"start": v(-5.6, -1.62) * mm, "end": v(-5.55, -1.62) * mm});
            skLineSegment(sketch, "E2131", {"start": v(-5.55, -1.62) * mm, "end": v(-5.5, -1.62) * mm});
            skLineSegment(sketch, "E2132", {"start": v(-5.5, -1.62) * mm, "end": v(-5.45, -1.62) * mm});
            skLineSegment(sketch, "E2133", {"start": v(-5.45, -1.62) * mm, "end": v(-5.4, -1.62) * mm});
            skLineSegment(sketch, "E2134", {"start": v(-5.4, -1.62) * mm, "end": v(-5.35, -1.62) * mm});
            skLineSegment(sketch, "E2135", {"start": v(-5.35, -1.62) * mm, "end": v(-5.3, -1.62) * mm});
            skLineSegment(sketch, "E2136", {"start": v(-5.3, -1.62) * mm, "end": v(-5.25, -1.62) * mm});
            skLineSegment(sketch, "E2137", {"start": v(-5.25, -1.62) * mm, "end": v(-4.95, -1.67) * mm});
            skLineSegment(sketch, "E2138", {"start": v(-4.95, -1.67) * mm, "end": v(-4.95, -1.87) * mm});
            skLineSegment(sketch, "E2139", {"start": v(-4.95, -1.87) * mm, "end": v(-4.95, -1.92) * mm});
            skLineSegment(sketch, "E2140", {"start": v(-4.95, -1.92) * mm, "end": v(-4.95, -1.97) * mm});
            skLineSegment(sketch, "E2141", {"start": v(-4.95, -1.97) * mm, "end": v(-4.95, -2.02) * mm});
            skLineSegment(sketch, "E2142", {"start": v(-4.95, -2.02) * mm, "end": v(-4.95, -2.07) * mm});
            skLineSegment(sketch, "E2143", {"start": v(-4.95, -2.07) * mm, "end": v(-4.95, -2.12) * mm});
            skLineSegment(sketch, "E2144", {"start": v(-4.95, -2.12) * mm, "end": v(-4.95, -2.17) * mm});
            skLineSegment(sketch, "E2145", {"start": v(-4.95, -2.17) * mm, "end": v(-4.95, -2.22) * mm});
            skLineSegment(sketch, "E2146", {"start": v(-4.95, -2.22) * mm, "end": v(-4.95, -2.27) * mm});
            skLineSegment(sketch, "E2147", {"start": v(-4.95, -2.27) * mm, "end": v(-4.95, -2.32) * mm});
            skLineSegment(sketch, "E2148", {"start": v(-4.95, -2.32) * mm, "end": v(-4.95, -2.37) * mm});
            skLineSegment(sketch, "E2149", {"start": v(-4.95, -2.37) * mm, "end": v(-4.95, -2.42) * mm});
            skLineSegment(sketch, "E2150", {"start": v(-4.95, -2.42) * mm, "end": v(-4.95, -2.47) * mm});
            skLineSegment(sketch, "E2151", {"start": v(-4.95, -2.47) * mm, "end": v(-4.95, -2.52) * mm});
            skLineSegment(sketch, "E2152", {"start": v(-4.95, -2.52) * mm, "end": v(-4.95, -2.57) * mm});
            skLineSegment(sketch, "E2153", {"start": v(-4.95, -2.57) * mm, "end": v(-4.95, -2.62) * mm});
            skLineSegment(sketch, "E2154", {"start": v(-4.95, -2.62) * mm, "end": v(-4.95, -2.67) * mm});
            skLineSegment(sketch, "E2155", {"start": v(-4.95, -2.67) * mm, "end": v(-4.95, -2.72) * mm});
            skLineSegment(sketch, "E2156", {"start": v(-4.95, -2.72) * mm, "end": v(-4.95, -2.77) * mm});
            skLineSegment(sketch, "E2157", {"start": v(-4.95, -2.77) * mm, "end": v(-4.95, -2.82) * mm});
            skLineSegment(sketch, "E2158", {"start": v(-4.95, -2.82) * mm, "end": v(-4.95, -2.87) * mm});
            skLineSegment(sketch, "E2159", {"start": v(-4.95, -2.87) * mm, "end": v(-4.95, -2.92) * mm});
            skLineSegment(sketch, "E2160", {"start": v(-4.95, -2.92) * mm, "end": v(-4.95, -2.97) * mm});
            skLineSegment(sketch, "E2161", {"start": v(-4.95, -2.97) * mm, "end": v(-4.95, -3.02) * mm});
            skLineSegment(sketch, "E2162", {"start": v(-4.95, -3.02) * mm, "end": v(-4.95, -3.07) * mm});
            skLineSegment(sketch, "E2163", {"start": v(-4.95, -3.07) * mm, "end": v(-4.95, -3.12) * mm});
            skLineSegment(sketch, "E2164", {"start": v(-4.95, -3.12) * mm, "end": v(-4.95, -3.17) * mm});
            skLineSegment(sketch, "E2165", {"start": v(-4.95, -3.17) * mm, "end": v(-4.95, -3.22) * mm});
            skLineSegment(sketch, "E2166", {"start": v(-4.95, -3.22) * mm, "end": v(-4.95, -3.27) * mm});
            skLineSegment(sketch, "E2167", {"start": v(-4.95, -3.27) * mm, "end": v(-4.95, -3.32) * mm});
            skLineSegment(sketch, "E2168", {"start": v(-4.95, -3.32) * mm, "end": v(-4.95, -3.37) * mm});
            skLineSegment(sketch, "E2169", {"start": v(-4.95, -3.37) * mm, "end": v(-4.95, -3.42) * mm});
            skLineSegment(sketch, "E2170", {"start": v(-4.95, -3.42) * mm, "end": v(-4.95, -3.47) * mm});
            skLineSegment(sketch, "E2171", {"start": v(-4.95, -3.47) * mm, "end": v(-4.95, -3.52) * mm});
            skLineSegment(sketch, "E2172", {"start": v(-4.95, -3.52) * mm, "end": v(-4.95, -3.57) * mm});
            skLineSegment(sketch, "E2173", {"start": v(-4.95, -3.57) * mm, "end": v(-4.95, -3.62) * mm});
            skLineSegment(sketch, "E2174", {"start": v(-4.95, -3.62) * mm, "end": v(-4.95, -3.67) * mm});
            skLineSegment(sketch, "E2175", {"start": v(-4.95, -3.67) * mm, "end": v(-4.95, -3.72) * mm});
            skLineSegment(sketch, "E2176", {"start": v(-4.95, -3.72) * mm, "end": v(-4.95, -3.77) * mm});
            skLineSegment(sketch, "E2177", {"start": v(-4.95, -3.77) * mm, "end": v(-4.95, -3.82) * mm});
            skLineSegment(sketch, "E2178", {"start": v(-4.95, -3.82) * mm, "end": v(-4.95, -3.87) * mm});
            skLineSegment(sketch, "E2179", {"start": v(-4.95, -3.87) * mm, "end": v(-4.95, -3.92) * mm});
            skLineSegment(sketch, "E2180", {"start": v(-4.95, -3.92) * mm, "end": v(-4.95, -3.97) * mm});
            skLineSegment(sketch, "E2181", {"start": v(-4.95, -3.97) * mm, "end": v(-4.95, -4.02) * mm});
            skLineSegment(sketch, "E2182", {"start": v(-4.95, -4.02) * mm, "end": v(-4.95, -4.07) * mm});
            skLineSegment(sketch, "E2183", {"start": v(-4.95, -4.07) * mm, "end": v(-4.95, -4.12) * mm});
            skLineSegment(sketch, "E2184", {"start": v(-4.95, -4.12) * mm, "end": v(-4.95, -4.17) * mm});
            skLineSegment(sketch, "E2185", {"start": v(-4.95, -4.17) * mm, "end": v(-4.95, -4.22) * mm});
            skLineSegment(sketch, "E2186", {"start": v(-4.95, -4.22) * mm, "end": v(-4.95, -4.42) * mm});
            skLineSegment(sketch, "E2187", {"start": v(-4.95, -4.42) * mm, "end": v(-4.75, -4.42) * mm});
            skLineSegment(sketch, "E2188", {"start": v(-4.75, -4.42) * mm, "end": v(-4.7, -4.42) * mm});
            skLineSegment(sketch, "E2189", {"start": v(-4.7, -4.42) * mm, "end": v(-4.65, -4.42) * mm});
            skLineSegment(sketch, "E2190", {"start": v(-4.65, -4.42) * mm, "end": v(-4.6, -4.42) * mm});
            skLineSegment(sketch, "E2191", {"start": v(-4.6, -4.42) * mm, "end": v(-4.55, -4.42) * mm});
            skLineSegment(sketch, "E2192", {"start": v(-4.55, -4.42) * mm, "end": v(-4.5, -4.42) * mm});
            skLineSegment(sketch, "E2193", {"start": v(-4.5, -4.42) * mm, "end": v(-4.45, -4.42) * mm});
            skLineSegment(sketch, "E2194", {"start": v(-4.45, -4.42) * mm, "end": v(-4.4, -4.42) * mm});
            skLineSegment(sketch, "E2195", {"start": v(-4.4, -4.42) * mm, "end": v(-4.35, -4.42) * mm});
            skLineSegment(sketch, "E2196", {"start": v(-4.35, -4.42) * mm, "end": v(-4.3, -4.42) * mm});
            skLineSegment(sketch, "E2197", {"start": v(-4.3, -4.42) * mm, "end": v(-4.25, -4.42) * mm});
            skLineSegment(sketch, "E2198", {"start": v(-4.25, -4.42) * mm, "end": v(-4.2, -4.42) * mm});
            skLineSegment(sketch, "E2199", {"start": v(-4.2, -4.42) * mm, "end": v(-4.15, -4.42) * mm});
            skLineSegment(sketch, "E2200", {"start": v(-4.15, -4.42) * mm, "end": v(-4.1, -4.42) * mm});
            skLineSegment(sketch, "E2201", {"start": v(-4.1, -4.42) * mm, "end": v(-4.05, -4.42) * mm});
            skLineSegment(sketch, "E2202", {"start": v(-4.05, -4.42) * mm, "end": v(-4, -4.42) * mm});
            skLineSegment(sketch, "E2203", {"start": v(-4, -4.42) * mm, "end": v(-3.95, -4.42) * mm});
            skLineSegment(sketch, "E2204", {"start": v(-3.95, -4.42) * mm, "end": v(-3.9, -4.42) * mm});
            skLineSegment(sketch, "E2205", {"start": v(-3.9, -4.42) * mm, "end": v(-3.85, -4.42) * mm});
            skLineSegment(sketch, "E2206", {"start": v(-3.85, -4.42) * mm, "end": v(-3.8, -4.42) * mm});
            skLineSegment(sketch, "E2207", {"start": v(-3.8, -4.42) * mm, "end": v(-3.75, -4.42) * mm});
            skLineSegment(sketch, "E2208", {"start": v(-3.75, -4.42) * mm, "end": v(-3.7, -4.42) * mm});
            skLineSegment(sketch, "E2209", {"start": v(-3.7, -4.42) * mm, "end": v(-3.65, -4.42) * mm});
            skLineSegment(sketch, "E2210", {"start": v(-3.65, -4.42) * mm, "end": v(-3.6, -4.42) * mm});
            skLineSegment(sketch, "E2211", {"start": v(-3.6, -4.42) * mm, "end": v(-3.55, -4.42) * mm});
            skLineSegment(sketch, "E2212", {"start": v(-3.55, -4.42) * mm, "end": v(-3.5, -4.42) * mm});
            skLineSegment(sketch, "E2213", {"start": v(-3.5, -4.42) * mm, "end": v(-3.45, -4.42) * mm});
            skLineSegment(sketch, "E2214", {"start": v(-3.45, -4.42) * mm, "end": v(-3.4, -4.42) * mm});
            skLineSegment(sketch, "E2215", {"start": v(-3.4, -4.42) * mm, "end": v(-3.35, -4.42) * mm});
            skLineSegment(sketch, "E2216", {"start": v(-3.35, -4.42) * mm, "end": v(-3.3, -4.42) * mm});
            skLineSegment(sketch, "E2217", {"start": v(-3.3, -4.42) * mm, "end": v(-3.25, -4.42) * mm});
            skLineSegment(sketch, "E2218", {"start": v(-3.25, -4.42) * mm, "end": v(-3.2, -4.42) * mm});
            skLineSegment(sketch, "E2219", {"start": v(-3.2, -4.42) * mm, "end": v(-3.15, -4.42) * mm});
            skLineSegment(sketch, "E2220", {"start": v(-3.15, -4.42) * mm, "end": v(-3.1, -4.42) * mm});
            skLineSegment(sketch, "E2221", {"start": v(-3.1, -4.42) * mm, "end": v(-3.05, -4.42) * mm});
            skLineSegment(sketch, "E2222", {"start": v(-3.05, -4.42) * mm, "end": v(-3, -4.42) * mm});
            skLineSegment(sketch, "E2223", {"start": v(-3, -4.42) * mm, "end": v(-2.95, -4.42) * mm});
            skLineSegment(sketch, "E2224", {"start": v(-2.95, -4.42) * mm, "end": v(-2.9, -4.42) * mm});
            skLineSegment(sketch, "E2225", {"start": v(-2.9, -4.42) * mm, "end": v(-2.85, -4.42) * mm});
            skLineSegment(sketch, "E2226", {"start": v(-2.85, -4.42) * mm, "end": v(-2.8, -4.42) * mm});
            skLineSegment(sketch, "E2227", {"start": v(-2.8, -4.42) * mm, "end": v(-2.75, -4.42) * mm});
            skLineSegment(sketch, "E2228", {"start": v(-2.75, -4.42) * mm, "end": v(-2.7, -4.42) * mm});
            skLineSegment(sketch, "E2229", {"start": v(-2.7, -4.42) * mm, "end": v(-2.65, -4.42) * mm});
            skLineSegment(sketch, "E2230", {"start": v(-2.65, -4.42) * mm, "end": v(-2.6, -4.42) * mm});
            skLineSegment(sketch, "E2231", {"start": v(-2.6, -4.42) * mm, "end": v(-2.55, -4.42) * mm});
            skLineSegment(sketch, "E2232", {"start": v(-2.55, -4.42) * mm, "end": v(-2.5, -4.42) * mm});
            skLineSegment(sketch, "E2233", {"start": v(-2.5, -4.42) * mm, "end": v(-2.45, -4.42) * mm});
            skLineSegment(sketch, "E2234", {"start": v(-2.45, -4.42) * mm, "end": v(-2.4, -4.42) * mm});
            skLineSegment(sketch, "E2235", {"start": v(-2.4, -4.42) * mm, "end": v(-2.35, -4.42) * mm});
            skLineSegment(sketch, "E2236", {"start": v(-2.35, -4.42) * mm, "end": v(-2.3, -4.42) * mm});
            skLineSegment(sketch, "E2237", {"start": v(-2.3, -4.42) * mm, "end": v(-2.25, -4.42) * mm});
            skLineSegment(sketch, "E2238", {"start": v(-2.25, -4.42) * mm, "end": v(-2.2, -4.42) * mm});
            skLineSegment(sketch, "E2239", {"start": v(-2.2, -4.42) * mm, "end": v(-2.15, -4.42) * mm});
            skLineSegment(sketch, "E2240", {"start": v(-2.15, -4.42) * mm, "end": v(-2.1, -4.42) * mm});
            skLineSegment(sketch, "E2241", {"start": v(-2.1, -4.42) * mm, "end": v(-2.05, -4.42) * mm});
            skLineSegment(sketch, "E2242", {"start": v(-2.05, -4.42) * mm, "end": v(-2, -4.42) * mm});
            skLineSegment(sketch, "E2243", {"start": v(-2, -4.42) * mm, "end": v(-1.95, -4.42) * mm});
            skLineSegment(sketch, "E2244", {"start": v(-1.95, -4.42) * mm, "end": v(-1.9, -4.42) * mm});
            skLineSegment(sketch, "E2245", {"start": v(-1.9, -4.42) * mm, "end": v(-1.85, -4.42) * mm});
            skLineSegment(sketch, "E2246", {"start": v(-1.85, -4.42) * mm, "end": v(-1.8, -4.42) * mm});
            skLineSegment(sketch, "E2247", {"start": v(-1.8, -4.42) * mm, "end": v(-1.75, -4.42) * mm});
            skLineSegment(sketch, "E2248", {"start": v(-1.75, -4.42) * mm, "end": v(-1.7, -4.42) * mm});
            skLineSegment(sketch, "E2249", {"start": v(-1.7, -4.42) * mm, "end": v(-1.65, -4.42) * mm});
            skLineSegment(sketch, "E2250", {"start": v(-1.65, -4.42) * mm, "end": v(-1.6, -4.42) * mm});
            skLineSegment(sketch, "E2251", {"start": v(-1.6, -4.42) * mm, "end": v(-1.55, -4.42) * mm});
            skLineSegment(sketch, "E2252", {"start": v(-1.55, -4.42) * mm, "end": v(-1.5, -4.42) * mm});
            skLineSegment(sketch, "E2253", {"start": v(-1.5, -4.42) * mm, "end": v(-1.45, -4.42) * mm});
            skLineSegment(sketch, "E2254", {"start": v(-1.45, -4.42) * mm, "end": v(-1.4, -4.42) * mm});
            skLineSegment(sketch, "E2255", {"start": v(-1.4, -4.42) * mm, "end": v(-1.35, -4.42) * mm});
            skLineSegment(sketch, "E2256", {"start": v(-1.35, -4.42) * mm, "end": v(-1.3, -4.42) * mm});
            skLineSegment(sketch, "E2257", {"start": v(-1.3, -4.42) * mm, "end": v(-1.25, -4.42) * mm});
            skLineSegment(sketch, "E2258", {"start": v(-1.25, -4.42) * mm, "end": v(-1.2, -4.42) * mm});
            skLineSegment(sketch, "E2259", {"start": v(-1.2, -4.42) * mm, "end": v(-1.15, -4.42) * mm});
            skLineSegment(sketch, "E2260", {"start": v(-1.15, -4.42) * mm, "end": v(-1.1, -4.42) * mm});
            skLineSegment(sketch, "E2261", {"start": v(-1.1, -4.42) * mm, "end": v(-1.05, -4.42) * mm});
            skLineSegment(sketch, "E2262", {"start": v(-1.05, -4.42) * mm, "end": v(-1, -4.42) * mm});
            skLineSegment(sketch, "E2263", {"start": v(-1, -4.42) * mm, "end": v(-0.95, -4.42) * mm});
            skLineSegment(sketch, "E2264", {"start": v(-0.95, -4.42) * mm, "end": v(-0.9, -4.42) * mm});
            skLineSegment(sketch, "E2265", {"start": v(-0.9, -4.42) * mm, "end": v(-0.85, -4.42) * mm});
            skLineSegment(sketch, "E2266", {"start": v(-0.85, -4.42) * mm, "end": v(-0.8, -4.42) * mm});
            skLineSegment(sketch, "E2267", {"start": v(-0.8, -4.42) * mm, "end": v(-0.75, -4.42) * mm});
            skLineSegment(sketch, "E2268", {"start": v(-0.75, -4.42) * mm, "end": v(-0.7, -4.42) * mm});
            skLineSegment(sketch, "E2269", {"start": v(-0.7, -4.42) * mm, "end": v(-0.65, -4.42) * mm});
            skLineSegment(sketch, "E2270", {"start": v(-0.65, -4.42) * mm, "end": v(-0.6, -4.42) * mm});
            skLineSegment(sketch, "E2271", {"start": v(-0.6, -4.42) * mm, "end": v(-0.55, -4.42) * mm});
            skLineSegment(sketch, "E2272", {"start": v(-0.55, -4.42) * mm, "end": v(-0.5, -4.42) * mm});
            skLineSegment(sketch, "E2273", {"start": v(-0.5, -4.42) * mm, "end": v(-0.45, -4.42) * mm});
            skLineSegment(sketch, "E2274", {"start": v(-0.45, -4.42) * mm, "end": v(-0.4, -4.42) * mm});
            skLineSegment(sketch, "E2275", {"start": v(-0.4, -4.42) * mm, "end": v(-0.35, -4.42) * mm});
            skLineSegment(sketch, "E2276", {"start": v(-0.35, -4.42) * mm, "end": v(-0.3, -4.42) * mm});
            skLineSegment(sketch, "E2277", {"start": v(-0.3, -4.42) * mm, "end": v(-0.25, -4.42) * mm});
            skLineSegment(sketch, "E2278", {"start": v(-0.25, -4.42) * mm, "end": v(-0.2, -4.42) * mm});
            skLineSegment(sketch, "E2279", {"start": v(-0.2, -4.42) * mm, "end": v(-0.15, -4.42) * mm});
            skLineSegment(sketch, "E2280", {"start": v(-0.15, -4.42) * mm, "end": v(-0.1, -4.42) * mm});
            skLineSegment(sketch, "E2281", {"start": v(-0.1, -4.42) * mm, "end": v(-0.05, -4.42) * mm});
            skLineSegment(sketch, "E2282", {"start": v(-0.05, -4.42) * mm, "end": v(0, -4.42) * mm});
            skLineSegment(sketch, "E2283", {"start": v(0, -4.42) * mm, "end": v(0.05, -4.42) * mm});
            skLineSegment(sketch, "E2284", {"start": v(0.05, -4.42) * mm, "end": v(0.1, -4.42) * mm});
            skLineSegment(sketch, "E2285", {"start": v(0.1, -4.42) * mm, "end": v(0.15, -4.42) * mm});
            skLineSegment(sketch, "E2286", {"start": v(0.15, -4.42) * mm, "end": v(0.2, -4.42) * mm});
            skLineSegment(sketch, "E2287", {"start": v(0.2, -4.42) * mm, "end": v(0.25, -4.42) * mm});
            skLineSegment(sketch, "E2288", {"start": v(0.25, -4.42) * mm, "end": v(0.3, -4.42) * mm});
            skLineSegment(sketch, "E2289", {"start": v(0.3, -4.42) * mm, "end": v(0.35, -4.42) * mm});
            skLineSegment(sketch, "E2290", {"start": v(0.35, -4.42) * mm, "end": v(0.4, -4.42) * mm});
            skLineSegment(sketch, "E2291", {"start": v(0.4, -4.42) * mm, "end": v(0.45, -4.42) * mm});
            skLineSegment(sketch, "E2292", {"start": v(0.45, -4.42) * mm, "end": v(0.5, -4.42) * mm});
            skLineSegment(sketch, "E2293", {"start": v(0.5, -4.42) * mm, "end": v(0.55, -4.42) * mm});
            skLineSegment(sketch, "E2294", {"start": v(0.55, -4.42) * mm, "end": v(0.6, -4.42) * mm});
            skLineSegment(sketch, "E2295", {"start": v(0.6, -4.42) * mm, "end": v(0.65, -4.42) * mm});
            skLineSegment(sketch, "E2296", {"start": v(0.65, -4.42) * mm, "end": v(0.7, -4.42) * mm});
            skLineSegment(sketch, "E2297", {"start": v(0.7, -4.42) * mm, "end": v(0.75, -4.42) * mm});
            skLineSegment(sketch, "E2298", {"start": v(0.75, -4.42) * mm, "end": v(0.8, -4.42) * mm});
            skLineSegment(sketch, "E2299", {"start": v(0.8, -4.42) * mm, "end": v(0.85, -4.42) * mm});
            skLineSegment(sketch, "E2300", {"start": v(0.85, -4.42) * mm, "end": v(0.9, -4.42) * mm});
            skLineSegment(sketch, "E2301", {"start": v(0.9, -4.42) * mm, "end": v(0.95, -4.42) * mm});
            skLineSegment(sketch, "E2302", {"start": v(0.95, -4.42) * mm, "end": v(1, -4.42) * mm});
            skLineSegment(sketch, "E2303", {"start": v(1, -4.42) * mm, "end": v(1.05, -4.42) * mm});
            skLineSegment(sketch, "E2304", {"start": v(1.05, -4.42) * mm, "end": v(1.1, -4.42) * mm});
            skLineSegment(sketch, "E2305", {"start": v(1.1, -4.42) * mm, "end": v(1.15, -4.42) * mm});
            skLineSegment(sketch, "E2306", {"start": v(1.15, -4.42) * mm, "end": v(1.2, -4.42) * mm});
            skLineSegment(sketch, "E2307", {"start": v(1.2, -4.42) * mm, "end": v(1.25, -4.42) * mm});
            skLineSegment(sketch, "E2308", {"start": v(1.25, -4.42) * mm, "end": v(1.3, -4.42) * mm});
            skLineSegment(sketch, "E2309", {"start": v(1.3, -4.42) * mm, "end": v(1.35, -4.42) * mm});
            skLineSegment(sketch, "E2310", {"start": v(1.35, -4.42) * mm, "end": v(1.4, -4.42) * mm});
            skLineSegment(sketch, "E2311", {"start": v(1.4, -4.42) * mm, "end": v(1.45, -4.42) * mm});
            skLineSegment(sketch, "E2312", {"start": v(1.45, -4.42) * mm, "end": v(1.5, -4.42) * mm});
            skLineSegment(sketch, "E2313", {"start": v(1.5, -4.42) * mm, "end": v(1.55, -4.42) * mm});
            skLineSegment(sketch, "E2314", {"start": v(1.55, -4.42) * mm, "end": v(1.6, -4.42) * mm});
            skLineSegment(sketch, "E2315", {"start": v(1.6, -4.42) * mm, "end": v(1.65, -4.42) * mm});
            skLineSegment(sketch, "E2316", {"start": v(1.65, -4.42) * mm, "end": v(1.7, -4.42) * mm});
            skLineSegment(sketch, "E2317", {"start": v(1.7, -4.42) * mm, "end": v(1.75, -4.42) * mm});
            skLineSegment(sketch, "E2318", {"start": v(1.75, -4.42) * mm, "end": v(1.8, -4.42) * mm});
            skLineSegment(sketch, "E2319", {"start": v(1.8, -4.42) * mm, "end": v(1.85, -4.42) * mm});
            skLineSegment(sketch, "E2320", {"start": v(1.85, -4.42) * mm, "end": v(1.9, -4.42) * mm});
            skLineSegment(sketch, "E2321", {"start": v(1.9, -4.42) * mm, "end": v(1.95, -4.42) * mm});
            skLineSegment(sketch, "E2322", {"start": v(1.95, -4.42) * mm, "end": v(2, -4.42) * mm});
            skLineSegment(sketch, "E2323", {"start": v(2, -4.42) * mm, "end": v(2.05, -4.42) * mm});
            skLineSegment(sketch, "E2324", {"start": v(2.05, -4.42) * mm, "end": v(2.1, -4.42) * mm});
            skLineSegment(sketch, "E2325", {"start": v(2.1, -4.42) * mm, "end": v(2.15, -4.42) * mm});
            skLineSegment(sketch, "E2326", {"start": v(2.15, -4.42) * mm, "end": v(2.2, -4.42) * mm});
            skLineSegment(sketch, "E2327", {"start": v(2.2, -4.42) * mm, "end": v(2.25, -4.42) * mm});
            skLineSegment(sketch, "E2328", {"start": v(2.25, -4.42) * mm, "end": v(2.3, -4.42) * mm});
            skLineSegment(sketch, "E2329", {"start": v(2.3, -4.42) * mm, "end": v(2.35, -4.42) * mm});
            skLineSegment(sketch, "E2330", {"start": v(2.35, -4.42) * mm, "end": v(2.4, -4.42) * mm});
            skLineSegment(sketch, "E2331", {"start": v(2.4, -4.42) * mm, "end": v(2.45, -4.42) * mm});
            skLineSegment(sketch, "E2332", {"start": v(2.45, -4.42) * mm, "end": v(2.5, -4.42) * mm});
            skLineSegment(sketch, "E2333", {"start": v(2.5, -4.42) * mm, "end": v(2.55, -4.42) * mm});
            skLineSegment(sketch, "E2334", {"start": v(2.55, -4.42) * mm, "end": v(2.6, -4.42) * mm});
            skLineSegment(sketch, "E2335", {"start": v(2.6, -4.42) * mm, "end": v(2.65, -4.42) * mm});
            skLineSegment(sketch, "E2336", {"start": v(2.65, -4.42) * mm, "end": v(2.7, -4.42) * mm});
            skLineSegment(sketch, "E2337", {"start": v(2.7, -4.42) * mm, "end": v(2.75, -4.42) * mm});
            skLineSegment(sketch, "E2338", {"start": v(2.75, -4.42) * mm, "end": v(2.8, -4.42) * mm});
            skLineSegment(sketch, "E2339", {"start": v(2.8, -4.42) * mm, "end": v(2.85, -4.42) * mm});
            skLineSegment(sketch, "E2340", {"start": v(2.85, -4.42) * mm, "end": v(2.9, -4.42) * mm});
            skLineSegment(sketch, "E2341", {"start": v(2.9, -4.42) * mm, "end": v(2.95, -4.42) * mm});
            skLineSegment(sketch, "E2342", {"start": v(2.95, -4.42) * mm, "end": v(3, -4.42) * mm});
            skLineSegment(sketch, "E2343", {"start": v(3, -4.42) * mm, "end": v(3.05, -4.42) * mm});
            skLineSegment(sketch, "E2344", {"start": v(3.05, -4.42) * mm, "end": v(3.1, -4.42) * mm});
            skLineSegment(sketch, "E2345", {"start": v(3.1, -4.42) * mm, "end": v(3.15, -4.42) * mm});
            skLineSegment(sketch, "E2346", {"start": v(3.15, -4.42) * mm, "end": v(3.2, -4.42) * mm});
            skLineSegment(sketch, "E2347", {"start": v(3.2, -4.42) * mm, "end": v(3.25, -4.42) * mm});
            skLineSegment(sketch, "E2348", {"start": v(3.25, -4.42) * mm, "end": v(3.3, -4.42) * mm});
            skLineSegment(sketch, "E2349", {"start": v(3.3, -4.42) * mm, "end": v(3.35, -4.42) * mm});
            skLineSegment(sketch, "E2350", {"start": v(3.35, -4.42) * mm, "end": v(3.4, -4.42) * mm});
            skLineSegment(sketch, "E2351", {"start": v(3.4, -4.42) * mm, "end": v(3.45, -4.42) * mm});
            skLineSegment(sketch, "E2352", {"start": v(3.45, -4.42) * mm, "end": v(3.5, -4.42) * mm});
            skLineSegment(sketch, "E2353", {"start": v(3.5, -4.42) * mm, "end": v(3.55, -4.42) * mm});
            skLineSegment(sketch, "E2354", {"start": v(3.55, -4.42) * mm, "end": v(3.6, -4.42) * mm});
            skLineSegment(sketch, "E2355", {"start": v(3.6, -4.42) * mm, "end": v(3.65, -4.42) * mm});
            skLineSegment(sketch, "E2356", {"start": v(3.65, -4.42) * mm, "end": v(3.7, -4.42) * mm});
            skLineSegment(sketch, "E2357", {"start": v(3.7, -4.42) * mm, "end": v(3.75, -4.42) * mm});
            skLineSegment(sketch, "E2358", {"start": v(3.75, -4.42) * mm, "end": v(3.8, -4.42) * mm});
            skLineSegment(sketch, "E2359", {"start": v(3.8, -4.42) * mm, "end": v(3.85, -4.42) * mm});
            skLineSegment(sketch, "E2360", {"start": v(3.85, -4.42) * mm, "end": v(3.9, -4.42) * mm});
            skLineSegment(sketch, "E2361", {"start": v(3.9, -4.42) * mm, "end": v(3.95, -4.42) * mm});
            skLineSegment(sketch, "E2362", {"start": v(3.95, -4.42) * mm, "end": v(4, -4.42) * mm});
            skLineSegment(sketch, "E2363", {"start": v(4, -4.42) * mm, "end": v(4.05, -4.42) * mm});
            skLineSegment(sketch, "E2364", {"start": v(4.05, -4.42) * mm, "end": v(4.1, -4.42) * mm});
            skLineSegment(sketch, "E2365", {"start": v(4.1, -4.42) * mm, "end": v(4.15, -4.42) * mm});
            skLineSegment(sketch, "E2366", {"start": v(4.15, -4.42) * mm, "end": v(4.2, -4.42) * mm});
            skLineSegment(sketch, "E2367", {"start": v(4.2, -4.42) * mm, "end": v(4.25, -4.42) * mm});
            skLineSegment(sketch, "E2368", {"start": v(4.25, -4.42) * mm, "end": v(4.3, -4.42) * mm});
            skLineSegment(sketch, "E2369", {"start": v(4.3, -4.42) * mm, "end": v(4.35, -4.42) * mm});
            skLineSegment(sketch, "E2370", {"start": v(4.35, -4.42) * mm, "end": v(4.4, -4.42) * mm});
            skLineSegment(sketch, "E2371", {"start": v(4.4, -4.42) * mm, "end": v(4.45, -4.42) * mm});
            skLineSegment(sketch, "E2372", {"start": v(4.45, -4.42) * mm, "end": v(4.5, -4.42) * mm});
            skLineSegment(sketch, "E2373", {"start": v(4.5, -4.42) * mm, "end": v(4.55, -4.42) * mm});
            skLineSegment(sketch, "E2374", {"start": v(4.55, -4.42) * mm, "end": v(4.6, -4.42) * mm});
            skLineSegment(sketch, "E2375", {"start": v(4.6, -4.42) * mm, "end": v(4.65, -4.42) * mm});
            skLineSegment(sketch, "E2376", {"start": v(4.65, -4.42) * mm, "end": v(4.7, -4.42) * mm});
            skLineSegment(sketch, "E2377", {"start": v(4.7, -4.42) * mm, "end": v(4.75, -4.42) * mm});
            skLineSegment(sketch, "E2378", {"start": v(4.75, -4.42) * mm, "end": v(4.8, -4.42) * mm});
            skLineSegment(sketch, "E2379", {"start": v(4.8, -4.42) * mm, "end": v(5, -4.42) * mm});
            skLineSegment(sketch, "E2380", {"start": v(5, -4.42) * mm, "end": v(5.05, -4.37) * mm});
            skLineSegment(sketch, "E2381", {"start": v(5.05, -4.37) * mm, "end": v(5.05, -4.27) * mm});
            skLineSegment(sketch, "E2382", {"start": v(5.05, -4.27) * mm, "end": v(5.05, -4.07) * mm});
            skLineSegment(sketch, "E2383", {"start": v(5.05, -4.07) * mm, "end": v(5.05, -4.02) * mm});
            skLineSegment(sketch, "E2384", {"start": v(5.05, -4.02) * mm, "end": v(5.05, -3.97) * mm});
            skLineSegment(sketch, "E2385", {"start": v(5.05, -3.97) * mm, "end": v(5.05, -3.92) * mm});
            skLineSegment(sketch, "E2386", {"start": v(5.05, -3.92) * mm, "end": v(5.05, -3.87) * mm});
            skLineSegment(sketch, "E2387", {"start": v(5.05, -3.87) * mm, "end": v(5.05, -3.82) * mm});
            skLineSegment(sketch, "E2388", {"start": v(5.05, -3.82) * mm, "end": v(5.05, -3.77) * mm});
            skLineSegment(sketch, "E2389", {"start": v(5.05, -3.77) * mm, "end": v(5.05, -3.72) * mm});
            skLineSegment(sketch, "E2390", {"start": v(5.05, -3.72) * mm, "end": v(5.05, -3.67) * mm});
            skLineSegment(sketch, "E2391", {"start": v(5.05, -3.67) * mm, "end": v(5.05, -3.62) * mm});
            skLineSegment(sketch, "E2392", {"start": v(5.05, -3.62) * mm, "end": v(5.05, -3.57) * mm});
            skLineSegment(sketch, "E2393", {"start": v(5.05, -3.57) * mm, "end": v(5.05, -3.52) * mm});
            skLineSegment(sketch, "E2394", {"start": v(5.05, -3.52) * mm, "end": v(5.05, -3.47) * mm});
            skLineSegment(sketch, "E2395", {"start": v(5.05, -3.47) * mm, "end": v(5.05, -3.42) * mm});
            skLineSegment(sketch, "E2396", {"start": v(5.05, -3.42) * mm, "end": v(5.05, -3.37) * mm});
            skLineSegment(sketch, "E2397", {"start": v(5.05, -3.37) * mm, "end": v(5.05, -3.32) * mm});
            skLineSegment(sketch, "E2398", {"start": v(5.05, -3.32) * mm, "end": v(5.05, -3.27) * mm});
            skLineSegment(sketch, "E2399", {"start": v(5.05, -3.27) * mm, "end": v(5.05, -3.22) * mm});
            skLineSegment(sketch, "E2400", {"start": v(5.05, -3.22) * mm, "end": v(5.05, -3.17) * mm});
            skLineSegment(sketch, "E2401", {"start": v(5.05, -3.17) * mm, "end": v(5.05, -3.12) * mm});
            skLineSegment(sketch, "E2402", {"start": v(5.05, -3.12) * mm, "end": v(5.05, -3.07) * mm});
            skLineSegment(sketch, "E2403", {"start": v(5.05, -3.07) * mm, "end": v(5.05, -3.02) * mm});
            skLineSegment(sketch, "E2404", {"start": v(5.05, -3.02) * mm, "end": v(5.05, -2.97) * mm});
            skLineSegment(sketch, "E2405", {"start": v(5.05, -2.97) * mm, "end": v(5.05, -2.92) * mm});
            skLineSegment(sketch, "E2406", {"start": v(5.05, -2.92) * mm, "end": v(5.05, -2.87) * mm});
            skLineSegment(sketch, "E2407", {"start": v(5.05, -2.87) * mm, "end": v(5.05, -2.82) * mm});
            skLineSegment(sketch, "E2408", {"start": v(5.05, -2.82) * mm, "end": v(5.05, -2.77) * mm});
            skLineSegment(sketch, "E2409", {"start": v(5.05, -2.77) * mm, "end": v(5.05, -2.72) * mm});
            skLineSegment(sketch, "E2410", {"start": v(5.05, -2.72) * mm, "end": v(5.05, -2.67) * mm});
            skLineSegment(sketch, "E2411", {"start": v(5.05, -2.67) * mm, "end": v(5.05, -2.62) * mm});
            skLineSegment(sketch, "E2412", {"start": v(5.05, -2.62) * mm, "end": v(5.05, -2.57) * mm});
            skLineSegment(sketch, "E2413", {"start": v(5.05, -2.57) * mm, "end": v(5.05, -2.52) * mm});
            skLineSegment(sketch, "E2414", {"start": v(5.05, -2.52) * mm, "end": v(5.05, -2.47) * mm});
            skLineSegment(sketch, "E2415", {"start": v(5.05, -2.47) * mm, "end": v(5.05, -2.42) * mm});
            skLineSegment(sketch, "E2416", {"start": v(5.05, -2.42) * mm, "end": v(5.05, -2.37) * mm});
            skLineSegment(sketch, "E2417", {"start": v(5.05, -2.37) * mm, "end": v(5.05, -2.32) * mm});
            skLineSegment(sketch, "E2418", {"start": v(5.05, -2.32) * mm, "end": v(5.05, -2.27) * mm});
            skLineSegment(sketch, "E2419", {"start": v(5.05, -2.27) * mm, "end": v(5.05, -2.22) * mm});
            skLineSegment(sketch, "E2420", {"start": v(5.05, -2.22) * mm, "end": v(5.05, -2.17) * mm});
            skLineSegment(sketch, "E2421", {"start": v(5.05, -2.17) * mm, "end": v(5.05, -2.12) * mm});
            skLineSegment(sketch, "E2422", {"start": v(5.05, -2.12) * mm, "end": v(5.05, -2.07) * mm});
            skLineSegment(sketch, "E2423", {"start": v(5.05, -2.07) * mm, "end": v(5.05, -2.02) * mm});
            skLineSegment(sketch, "E2424", {"start": v(5.05, -2.02) * mm, "end": v(5.05, -1.97) * mm});
            skLineSegment(sketch, "E2425", {"start": v(5.05, -1.97) * mm, "end": v(5.05, -1.92) * mm});
            skLineSegment(sketch, "E2426", {"start": v(5.05, -1.92) * mm, "end": v(5.05, -1.67) * mm});
            skLineSegment(sketch, "E2427", {"start": v(5.05, -1.67) * mm, "end": v(5.2, -1.62) * mm});
            skLineSegment(sketch, "E2428", {"start": v(5.2, -1.62) * mm, "end": v(5.4, -1.62) * mm});
            skLineSegment(sketch, "E2429", {"start": v(5.4, -1.62) * mm, "end": v(5.45, -1.62) * mm});
            skLineSegment(sketch, "E2430", {"start": v(5.45, -1.62) * mm, "end": v(5.5, -1.62) * mm});
            skLineSegment(sketch, "E2431", {"start": v(5.5, -1.62) * mm, "end": v(5.55, -1.62) * mm});
            skLineSegment(sketch, "E2432", {"start": v(5.55, -1.62) * mm, "end": v(5.6, -1.62) * mm});
            skLineSegment(sketch, "E2433", {"start": v(5.6, -1.62) * mm, "end": v(5.65, -1.62) * mm});
            skLineSegment(sketch, "E2434", {"start": v(5.65, -1.62) * mm, "end": v(5.7, -1.62) * mm});
            skLineSegment(sketch, "E2435", {"start": v(5.7, -1.62) * mm, "end": v(5.75, -1.62) * mm});
            skLineSegment(sketch, "E2436", {"start": v(5.75, -1.62) * mm, "end": v(5.8, -1.62) * mm});
            skLineSegment(sketch, "E2437", {"start": v(5.8, -1.62) * mm, "end": v(5.85, -1.62) * mm});
            skLineSegment(sketch, "E2438", {"start": v(5.85, -1.62) * mm, "end": v(5.9, -1.62) * mm});
            skLineSegment(sketch, "E2439", {"start": v(5.9, -1.62) * mm, "end": v(5.95, -1.62) * mm});
            skLineSegment(sketch, "E2440", {"start": v(5.95, -1.62) * mm, "end": v(6, -1.62) * mm});
            skLineSegment(sketch, "E2441", {"start": v(6, -1.62) * mm, "end": v(6.05, -1.62) * mm});
            skLineSegment(sketch, "E2442", {"start": v(6.05, -1.62) * mm, "end": v(6.1, -1.62) * mm});
            skLineSegment(sketch, "E2443", {"start": v(6.1, -1.62) * mm, "end": v(6.15, -1.62) * mm});
            skLineSegment(sketch, "E2444", {"start": v(6.15, -1.62) * mm, "end": v(6.2, -1.62) * mm});
            skLineSegment(sketch, "E2445", {"start": v(6.2, -1.62) * mm, "end": v(6.25, -1.62) * mm});
            skLineSegment(sketch, "E2446", {"start": v(6.25, -1.62) * mm, "end": v(6.3, -1.62) * mm});
            skLineSegment(sketch, "E2447", {"start": v(6.3, -1.62) * mm, "end": v(6.35, -1.62) * mm});
            skLineSegment(sketch, "E2448", {"start": v(6.35, -1.62) * mm, "end": v(6.4, -1.62) * mm});
            skLineSegment(sketch, "E2449", {"start": v(6.4, -1.62) * mm, "end": v(6.45, -1.62) * mm});
            skLineSegment(sketch, "E2450", {"start": v(6.45, -1.62) * mm, "end": v(6.5, -1.62) * mm});
            skLineSegment(sketch, "E2451", {"start": v(6.5, -1.62) * mm, "end": v(6.55, -1.62) * mm});
            skLineSegment(sketch, "E2452", {"start": v(6.55, -1.62) * mm, "end": v(6.6, -1.62) * mm});
            skLineSegment(sketch, "E2453", {"start": v(6.6, -1.62) * mm, "end": v(6.65, -1.62) * mm});
            skLineSegment(sketch, "E2454", {"start": v(6.65, -1.62) * mm, "end": v(6.7, -1.62) * mm});
            skLineSegment(sketch, "E2455", {"start": v(6.7, -1.62) * mm, "end": v(6.75, -1.62) * mm});
            skLineSegment(sketch, "E2456", {"start": v(6.75, -1.62) * mm, "end": v(6.8, -1.62) * mm});
            skLineSegment(sketch, "E2457", {"start": v(6.8, -1.62) * mm, "end": v(6.85, -1.62) * mm});
            skLineSegment(sketch, "E2458", {"start": v(6.85, -1.62) * mm, "end": v(6.9, -1.62) * mm});
            skLineSegment(sketch, "E2459", {"start": v(6.9, -1.62) * mm, "end": v(6.95, -1.62) * mm});
            skLineSegment(sketch, "E2460", {"start": v(6.95, -1.62) * mm, "end": v(7, -1.62) * mm});
            skLineSegment(sketch, "E2461", {"start": v(7, -1.62) * mm, "end": v(7.05, -1.62) * mm});
            skLineSegment(sketch, "E2462", {"start": v(7.05, -1.62) * mm, "end": v(7.1, -1.62) * mm});
            skLineSegment(sketch, "E2463", {"start": v(7.1, -1.62) * mm, "end": v(7.15, -1.62) * mm});
            skLineSegment(sketch, "E2464", {"start": v(7.15, -1.62) * mm, "end": v(7.2, -1.62) * mm});
            skLineSegment(sketch, "E2465", {"start": v(7.2, -1.62) * mm, "end": v(7.25, -1.62) * mm});
            skLineSegment(sketch, "E2466", {"start": v(7.25, -1.62) * mm, "end": v(7.3, -1.62) * mm});
            skLineSegment(sketch, "E2467", {"start": v(7.3, -1.62) * mm, "end": v(7.35, -1.62) * mm});
            skLineSegment(sketch, "E2468", {"start": v(7.35, -1.62) * mm, "end": v(7.4, -1.62) * mm});
            skLineSegment(sketch, "E2469", {"start": v(7.4, -1.62) * mm, "end": v(7.45, -1.62) * mm});
            skLineSegment(sketch, "E2470", {"start": v(7.45, -1.62) * mm, "end": v(7.5, -1.62) * mm});
            skLineSegment(sketch, "E2471", {"start": v(7.5, -1.62) * mm, "end": v(7.55, -1.62) * mm});
            skLineSegment(sketch, "E2472", {"start": v(7.55, -1.62) * mm, "end": v(7.6, -1.62) * mm});
            skLineSegment(sketch, "E2473", {"start": v(7.6, -1.62) * mm, "end": v(7.65, -1.62) * mm});
            skLineSegment(sketch, "E2474", {"start": v(7.65, -1.62) * mm, "end": v(7.7, -1.62) * mm});
            skLineSegment(sketch, "E2475", {"start": v(7.7, -1.62) * mm, "end": v(7.75, -1.62) * mm});
            skLineSegment(sketch, "E2476", {"start": v(7.75, -1.62) * mm, "end": v(7.8, -1.62) * mm});
            skLineSegment(sketch, "E2477", {"start": v(7.8, -1.62) * mm, "end": v(7.85, -1.62) * mm});
            skLineSegment(sketch, "E2478", {"start": v(7.85, -1.62) * mm, "end": v(7.9, -1.62) * mm});
            skLineSegment(sketch, "E2479", {"start": v(7.9, -1.62) * mm, "end": v(7.95, -1.62) * mm});
            skLineSegment(sketch, "E2480", {"start": v(7.95, -1.62) * mm, "end": v(8, -1.62) * mm});
            skLineSegment(sketch, "E2481", {"start": v(8, -1.62) * mm, "end": v(8.05, -1.62) * mm});
            skLineSegment(sketch, "E2482", {"start": v(8.05, -1.62) * mm, "end": v(8.1, -1.62) * mm});
            skLineSegment(sketch, "E2483", {"start": v(8.1, -1.62) * mm, "end": v(8.15, -1.62) * mm});
            skLineSegment(sketch, "E2484", {"start": v(8.15, -1.62) * mm, "end": v(8.2, -1.62) * mm});
            skLineSegment(sketch, "E2485", {"start": v(8.2, -1.62) * mm, "end": v(8.25, -1.62) * mm});
            skLineSegment(sketch, "E2486", {"start": v(8.25, -1.62) * mm, "end": v(8.3, -1.62) * mm});
            skLineSegment(sketch, "E2487", {"start": v(8.3, -1.62) * mm, "end": v(8.35, -1.62) * mm});
            skLineSegment(sketch, "E2488", {"start": v(8.35, -1.62) * mm, "end": v(8.4, -1.62) * mm});
            skLineSegment(sketch, "E2489", {"start": v(8.4, -1.62) * mm, "end": v(8.45, -1.62) * mm});
            skLineSegment(sketch, "E2490", {"start": v(8.45, -1.62) * mm, "end": v(8.5, -1.62) * mm});
            skLineSegment(sketch, "E2491", {"start": v(8.5, -1.62) * mm, "end": v(8.55, -1.62) * mm});
            skLineSegment(sketch, "E2492", {"start": v(8.55, -1.62) * mm, "end": v(8.6, -1.62) * mm});
            skLineSegment(sketch, "E2493", {"start": v(8.6, -1.62) * mm, "end": v(8.65, -1.62) * mm});
            skLineSegment(sketch, "E2494", {"start": v(8.65, -1.62) * mm, "end": v(8.7, -1.62) * mm});
            skLineSegment(sketch, "E2495", {"start": v(8.7, -1.62) * mm, "end": v(8.75, -1.62) * mm});
            skLineSegment(sketch, "E2496", {"start": v(8.75, -1.62) * mm, "end": v(8.8, -1.62) * mm});
            skLineSegment(sketch, "E2497", {"start": v(8.8, -1.62) * mm, "end": v(8.85, -1.62) * mm});
            skLineSegment(sketch, "E2498", {"start": v(8.85, -1.62) * mm, "end": v(8.9, -1.62) * mm});
            skLineSegment(sketch, "E2499", {"start": v(8.9, -1.62) * mm, "end": v(8.95, -1.62) * mm});
            skLineSegment(sketch, "E2500", {"start": v(8.95, -1.62) * mm, "end": v(9, -1.62) * mm});
            skLineSegment(sketch, "E2501", {"start": v(9, -1.62) * mm, "end": v(9.05, -1.62) * mm});
            skLineSegment(sketch, "E2502", {"start": v(9.05, -1.62) * mm, "end": v(9.1, -1.62) * mm});
            skLineSegment(sketch, "E2503", {"start": v(9.1, -1.62) * mm, "end": v(9.15, -1.62) * mm});
            skLineSegment(sketch, "E2504", {"start": v(9.15, -1.62) * mm, "end": v(9.2, -1.62) * mm});
            skLineSegment(sketch, "E2505", {"start": v(9.2, -1.62) * mm, "end": v(9.25, -1.62) * mm});
            skLineSegment(sketch, "E2506", {"start": v(9.25, -1.62) * mm, "end": v(9.3, -1.62) * mm});
            skLineSegment(sketch, "E2507", {"start": v(9.3, -1.62) * mm, "end": v(9.35, -1.62) * mm});
            skLineSegment(sketch, "E2508", {"start": v(9.35, -1.62) * mm, "end": v(9.4, -1.62) * mm});
            skLineSegment(sketch, "E2509", {"start": v(9.4, -1.62) * mm, "end": v(9.45, -1.62) * mm});
            skLineSegment(sketch, "E2510", {"start": v(9.45, -1.62) * mm, "end": v(9.5, -1.62) * mm});
            skLineSegment(sketch, "E2511", {"start": v(9.5, -1.62) * mm, "end": v(9.55, -1.62) * mm});
            skLineSegment(sketch, "E2512", {"start": v(9.55, -1.62) * mm, "end": v(9.6, -1.62) * mm});
            skLineSegment(sketch, "E2513", {"start": v(9.6, -1.62) * mm, "end": v(9.65, -1.62) * mm});
            skLineSegment(sketch, "E2514", {"start": v(9.65, -1.62) * mm, "end": v(9.7, -1.62) * mm});
            skLineSegment(sketch, "E2515", {"start": v(9.7, -1.62) * mm, "end": v(9.75, -1.62) * mm});
            skLineSegment(sketch, "E2516", {"start": v(9.75, -1.62) * mm, "end": v(9.8, -1.62) * mm});
            skLineSegment(sketch, "E2517", {"start": v(9.8, -1.62) * mm, "end": v(9.85, -1.62) * mm});
            skLineSegment(sketch, "E2518", {"start": v(9.85, -1.62) * mm, "end": v(9.9, -1.62) * mm});
            skLineSegment(sketch, "E2519", {"start": v(9.9, -1.62) * mm, "end": v(9.95, -1.62) * mm});
            skLineSegment(sketch, "E2520", {"start": v(9.95, -1.62) * mm, "end": v(10, -1.62) * mm});
            skLineSegment(sketch, "E2521", {"start": v(10, -1.62) * mm, "end": v(10.05, -1.62) * mm});
            skLineSegment(sketch, "E2522", {"start": v(10.05, -1.62) * mm, "end": v(10.1, -1.62) * mm});
            skLineSegment(sketch, "E2523", {"start": v(10.1, -1.62) * mm, "end": v(10.15, -1.62) * mm});
            skLineSegment(sketch, "E2524", {"start": v(10.15, -1.62) * mm, "end": v(10.2, -1.62) * mm});
            skLineSegment(sketch, "E2525", {"start": v(10.2, -1.62) * mm, "end": v(10.25, -1.62) * mm});
            skLineSegment(sketch, "E2526", {"start": v(10.25, -1.62) * mm, "end": v(10.3, -1.62) * mm});
            skLineSegment(sketch, "E2527", {"start": v(10.3, -1.62) * mm, "end": v(10.35, -1.62) * mm});
            skLineSegment(sketch, "E2528", {"start": v(10.35, -1.62) * mm, "end": v(10.4, -1.62) * mm});
            skLineSegment(sketch, "E2529", {"start": v(10.4, -1.62) * mm, "end": v(10.45, -1.62) * mm});
            skLineSegment(sketch, "E2530", {"start": v(10.45, -1.62) * mm, "end": v(10.5, -1.62) * mm});
            skLineSegment(sketch, "E2531", {"start": v(10.5, -1.62) * mm, "end": v(10.55, -1.62) * mm});
            skLineSegment(sketch, "E2532", {"start": v(10.55, -1.62) * mm, "end": v(10.6, -1.62) * mm});
            skLineSegment(sketch, "E2533", {"start": v(10.6, -1.62) * mm, "end": v(10.65, -1.62) * mm});
            skLineSegment(sketch, "E2534", {"start": v(10.65, -1.62) * mm, "end": v(10.7, -1.62) * mm});
            skLineSegment(sketch, "E2535", {"start": v(10.7, -1.62) * mm, "end": v(10.75, -1.62) * mm});
            skLineSegment(sketch, "E2536", {"start": v(10.75, -1.62) * mm, "end": v(10.8, -1.62) * mm});
            skLineSegment(sketch, "E2537", {"start": v(10.8, -1.62) * mm, "end": v(10.85, -1.62) * mm});
            skLineSegment(sketch, "E2538", {"start": v(10.85, -1.62) * mm, "end": v(10.9, -1.62) * mm});
            skLineSegment(sketch, "E2539", {"start": v(10.9, -1.62) * mm, "end": v(10.95, -1.62) * mm});
            skLineSegment(sketch, "E2540", {"start": v(10.95, -1.62) * mm, "end": v(11, -1.62) * mm});
            skLineSegment(sketch, "E2541", {"start": v(11, -1.62) * mm, "end": v(11.05, -1.62) * mm});
            skLineSegment(sketch, "E2542", {"start": v(11.05, -1.62) * mm, "end": v(11.1, -1.62) * mm});
            skLineSegment(sketch, "E2543", {"start": v(11.1, -1.62) * mm, "end": v(11.15, -1.62) * mm});
            skLineSegment(sketch, "E2544", {"start": v(11.15, -1.62) * mm, "end": v(11.2, -1.62) * mm});
            skLineSegment(sketch, "E2545", {"start": v(11.2, -1.62) * mm, "end": v(11.25, -1.62) * mm});
            skLineSegment(sketch, "E2546", {"start": v(11.25, -1.62) * mm, "end": v(11.3, -1.62) * mm});
            skLineSegment(sketch, "E2547", {"start": v(11.3, -1.62) * mm, "end": v(11.35, -1.62) * mm});
            skLineSegment(sketch, "E2548", {"start": v(11.35, -1.62) * mm, "end": v(11.4, -1.62) * mm});
            skLineSegment(sketch, "E2549", {"start": v(11.4, -1.62) * mm, "end": v(11.45, -1.62) * mm});
            skLineSegment(sketch, "E2550", {"start": v(11.45, -1.62) * mm, "end": v(11.5, -1.62) * mm});
            skLineSegment(sketch, "E2551", {"start": v(11.5, -1.62) * mm, "end": v(11.55, -1.62) * mm});
            skLineSegment(sketch, "E2552", {"start": v(11.55, -1.62) * mm, "end": v(11.6, -1.62) * mm});
            skLineSegment(sketch, "E2553", {"start": v(11.6, -1.62) * mm, "end": v(11.65, -1.62) * mm});
            skLineSegment(sketch, "E2554", {"start": v(11.65, -1.62) * mm, "end": v(11.7, -1.62) * mm});
            skLineSegment(sketch, "E2555", {"start": v(11.7, -1.62) * mm, "end": v(11.75, -1.62) * mm});
            skLineSegment(sketch, "E2556", {"start": v(11.75, -1.62) * mm, "end": v(11.8, -1.62) * mm});
            skLineSegment(sketch, "E2557", {"start": v(11.8, -1.62) * mm, "end": v(11.85, -1.62) * mm});
            skLineSegment(sketch, "E2558", {"start": v(11.85, -1.62) * mm, "end": v(11.9, -1.62) * mm});
            skLineSegment(sketch, "E2559", {"start": v(11.9, -1.62) * mm, "end": v(11.95, -1.62) * mm});
            skLineSegment(sketch, "E2560", {"start": v(11.95, -1.62) * mm, "end": v(12, -1.62) * mm});
            skLineSegment(sketch, "E2561", {"start": v(12, -1.62) * mm, "end": v(12.05, -1.62) * mm});
            skLineSegment(sketch, "E2562", {"start": v(12.05, -1.62) * mm, "end": v(12.1, -1.62) * mm});
            skLineSegment(sketch, "E2563", {"start": v(12.1, -1.62) * mm, "end": v(12.15, -1.62) * mm});
            skLineSegment(sketch, "E2564", {"start": v(12.15, -1.62) * mm, "end": v(12.2, -1.62) * mm});
            skLineSegment(sketch, "E2565", {"start": v(12.2, -1.62) * mm, "end": v(12.25, -1.62) * mm});
            skLineSegment(sketch, "E2566", {"start": v(12.25, -1.62) * mm, "end": v(12.3, -1.62) * mm});
            skLineSegment(sketch, "E2567", {"start": v(12.3, -1.62) * mm, "end": v(12.35, -1.62) * mm});
            skLineSegment(sketch, "E2568", {"start": v(12.35, -1.62) * mm, "end": v(12.4, -1.62) * mm});
            skLineSegment(sketch, "E2569", {"start": v(12.4, -1.62) * mm, "end": v(12.45, -1.62) * mm});
            skLineSegment(sketch, "E2570", {"start": v(12.45, -1.62) * mm, "end": v(12.5, -1.62) * mm});
            skLineSegment(sketch, "E2571", {"start": v(12.5, -1.62) * mm, "end": v(12.55, -1.62) * mm});
            skLineSegment(sketch, "E2572", {"start": v(12.55, -1.62) * mm, "end": v(12.6, -1.62) * mm});
            skLineSegment(sketch, "E2573", {"start": v(12.6, -1.62) * mm, "end": v(12.65, -1.62) * mm});
            skLineSegment(sketch, "E2574", {"start": v(12.65, -1.62) * mm, "end": v(12.7, -1.62) * mm});
            skLineSegment(sketch, "E2575", {"start": v(12.7, -1.62) * mm, "end": v(12.75, -1.62) * mm});
            skLineSegment(sketch, "E2576", {"start": v(12.75, -1.62) * mm, "end": v(12.8, -1.62) * mm});
            skLineSegment(sketch, "E2577", {"start": v(12.8, -1.62) * mm, "end": v(12.85, -1.62) * mm});
            skLineSegment(sketch, "E2578", {"start": v(12.85, -1.62) * mm, "end": v(12.9, -1.62) * mm});
            skLineSegment(sketch, "E2579", {"start": v(12.9, -1.62) * mm, "end": v(12.95, -1.62) * mm});
            skLineSegment(sketch, "E2580", {"start": v(12.95, -1.62) * mm, "end": v(13, -1.62) * mm});
            skLineSegment(sketch, "E2581", {"start": v(13, -1.62) * mm, "end": v(13.05, -1.62) * mm});
            skLineSegment(sketch, "E2582", {"start": v(13.05, -1.62) * mm, "end": v(13.1, -1.62) * mm});
            skLineSegment(sketch, "E2583", {"start": v(13.1, -1.62) * mm, "end": v(13.15, -1.62) * mm});
            skLineSegment(sketch, "E2584", {"start": v(13.15, -1.62) * mm, "end": v(13.2, -1.62) * mm});
            skLineSegment(sketch, "E2585", {"start": v(13.2, -1.62) * mm, "end": v(13.25, -1.62) * mm});
            skLineSegment(sketch, "E2586", {"start": v(13.25, -1.62) * mm, "end": v(13.3, -1.62) * mm});
            skLineSegment(sketch, "E2587", {"start": v(13.3, -1.62) * mm, "end": v(13.35, -1.62) * mm});
            skLineSegment(sketch, "E2588", {"start": v(13.35, -1.62) * mm, "end": v(13.4, -1.62) * mm});
            skLineSegment(sketch, "E2589", {"start": v(13.4, -1.62) * mm, "end": v(13.45, -1.62) * mm});
            skLineSegment(sketch, "E2590", {"start": v(13.45, -1.62) * mm, "end": v(13.5, -1.62) * mm});
            skLineSegment(sketch, "E2591", {"start": v(13.5, -1.62) * mm, "end": v(13.55, -1.62) * mm});
            skLineSegment(sketch, "E2592", {"start": v(13.55, -1.62) * mm, "end": v(13.6, -1.62) * mm});
            skLineSegment(sketch, "E2593", {"start": v(13.6, -1.62) * mm, "end": v(13.65, -1.62) * mm});
            skLineSegment(sketch, "E2594", {"start": v(13.65, -1.62) * mm, "end": v(13.7, -1.62) * mm});
            skLineSegment(sketch, "E2595", {"start": v(13.7, -1.62) * mm, "end": v(13.75, -1.62) * mm});
            skLineSegment(sketch, "E2596", {"start": v(13.75, -1.62) * mm, "end": v(13.8, -1.62) * mm});
            skLineSegment(sketch, "E2597", {"start": v(13.8, -1.62) * mm, "end": v(13.85, -1.62) * mm});
            skLineSegment(sketch, "E2598", {"start": v(13.85, -1.62) * mm, "end": v(13.9, -1.62) * mm});
            skLineSegment(sketch, "E2599", {"start": v(13.9, -1.62) * mm, "end": v(13.95, -1.62) * mm});
            skLineSegment(sketch, "E2600", {"start": v(13.95, -1.62) * mm, "end": v(14, -1.62) * mm});
            skLineSegment(sketch, "E2601", {"start": v(14, -1.62) * mm, "end": v(14.05, -1.62) * mm});
            skLineSegment(sketch, "E2602", {"start": v(14.05, -1.62) * mm, "end": v(14.1, -1.62) * mm});
            skLineSegment(sketch, "E2603", {"start": v(14.1, -1.62) * mm, "end": v(14.15, -1.62) * mm});
            skLineSegment(sketch, "E2604", {"start": v(14.15, -1.62) * mm, "end": v(14.4, -1.62) * mm});
            skLineSegment(sketch, "E2605", {"start": v(14.4, -1.62) * mm, "end": v(14.55, -1.32) * mm});
            skLineSegment(sketch, "E2606", {"start": v(14.55, -1.32) * mm, "end": v(14.55, -1.17) * mm});
            skLineSegment(sketch, "E2607", {"start": v(14.55, -1.17) * mm, "end": v(14.65, -1.12) * mm});
            skLineSegment(sketch, "E2608", {"start": v(14.65, -1.12) * mm, "end": v(14.8, -0.83) * mm});
            skLineSegment(sketch, "E2609", {"start": v(14.8, -0.82) * mm, "end": v(14.95, -0.52) * mm});
            skLineSegment(sketch, "E2610", {"start": v(14.95, -0.52) * mm, "end": v(14.95, -0.37) * mm});
            skLineSegment(sketch, "E2611", {"start": v(14.95, -0.37) * mm, "end": v(15.05, -0.32) * mm});
            skLineSegment(sketch, "E2612", {"start": v(15.05, -0.32) * mm, "end": v(15.2, -0.02) * mm});
            skLineSegment(sketch, "E2613", {"start": v(15.2, -0.02) * mm, "end": v(15.35, 0.28) * mm});
            skLineSegment(sketch, "E2614", {"start": v(15.35, 0.28) * mm, "end": v(15.35, 0.43) * mm});
            skLineSegment(sketch, "E2615", {"start": v(15.35, 0.43) * mm, "end": v(15.45, 0.48) * mm});
            skLineSegment(sketch, "E2616", {"start": v(15.45, 0.48) * mm, "end": v(15.5, 0.73) * mm});
            skLineSegment(sketch, "E2617", {"start": v(15.5, 0.73) * mm, "end": v(15.75, 1.03) * mm});
            skLineSegment(sketch, "E2618", {"start": v(15.75, 1.03) * mm, "end": v(15.8, 1.28) * mm});
            skLineSegment(sketch, "E2619", {"start": v(15.8, 1.28) * mm, "end": v(15.85, 1.28) * mm});
            skLineSegment(sketch, "E2620", {"start": v(15.85, 1.28) * mm, "end": v(15.85, 1.38) * mm});
            skLineSegment(sketch, "E2621", {"start": v(15.85, 1.38) * mm, "end": v(16, 1.53) * mm});
            skLineSegment(sketch, "E2622", {"start": v(16, 1.53) * mm, "end": v(16.15, 1.83) * mm});
            skLineSegment(sketch, "E2623", {"start": v(16.15, 1.83) * mm, "end": v(16.15, 1.98) * mm});
            skLineSegment(sketch, "E2624", {"start": v(16.15, 1.98) * mm, "end": v(16.25, 2.03) * mm});
            skLineSegment(sketch, "E2625", {"start": v(16.25, 2.03) * mm, "end": v(16.4, 2.48) * mm});
            skLineSegment(sketch, "E2626", {"start": v(16.4, 2.48) * mm, "end": v(16.2, 2.48) * mm});
            skLineSegment(sketch, "E2627", {"start": v(16.2, 2.48) * mm, "end": v(16.15, 2.48) * mm});
            skLineSegment(sketch, "E2628", {"start": v(16.15, 2.48) * mm, "end": v(16.1, 2.48) * mm});
            skLineSegment(sketch, "E2629", {"start": v(16.1, 2.48) * mm, "end": v(16.05, 2.48) * mm});
            skLineSegment(sketch, "E2630", {"start": v(16.05, 2.48) * mm, "end": v(16, 2.48) * mm});
            skLineSegment(sketch, "E2631", {"start": v(16, 2.48) * mm, "end": v(15.95, 2.48) * mm});
            skLineSegment(sketch, "E2632", {"start": v(15.95, 2.48) * mm, "end": v(15.9, 2.48) * mm});
            skLineSegment(sketch, "E2633", {"start": v(15.9, 2.48) * mm, "end": v(15.85, 2.48) * mm});
            skLineSegment(sketch, "E2634", {"start": v(15.85, 2.48) * mm, "end": v(15.8, 2.48) * mm});
            skLineSegment(sketch, "E2635", {"start": v(15.8, 2.48) * mm, "end": v(15.75, 2.48) * mm});
            skLineSegment(sketch, "E2636", {"start": v(15.75, 2.48) * mm, "end": v(15.7, 2.48) * mm});
            skLineSegment(sketch, "E2637", {"start": v(15.7, 2.48) * mm, "end": v(15.65, 2.48) * mm});
            skLineSegment(sketch, "E2638", {"start": v(15.65, 2.48) * mm, "end": v(15.6, 2.48) * mm});
            skLineSegment(sketch, "E2639", {"start": v(15.6, 2.48) * mm, "end": v(15.55, 2.48) * mm});
            skLineSegment(sketch, "E2640", {"start": v(15.55, 2.48) * mm, "end": v(15.5, 2.48) * mm});
            skLineSegment(sketch, "E2641", {"start": v(15.5, 2.48) * mm, "end": v(15.45, 2.48) * mm});
            skLineSegment(sketch, "E2642", {"start": v(15.45, 2.48) * mm, "end": v(15.4, 2.48) * mm});
            skLineSegment(sketch, "E2643", {"start": v(15.4, 2.48) * mm, "end": v(15.35, 2.48) * mm});
            skLineSegment(sketch, "E2644", {"start": v(15.35, 2.48) * mm, "end": v(15.3, 2.48) * mm});
            skLineSegment(sketch, "E2645", {"start": v(15.3, 2.48) * mm, "end": v(15.25, 2.48) * mm});
            skLineSegment(sketch, "E2646", {"start": v(15.25, 2.48) * mm, "end": v(15.2, 2.48) * mm});
            skLineSegment(sketch, "E2647", {"start": v(15.2, 2.48) * mm, "end": v(15.15, 2.48) * mm});
            skLineSegment(sketch, "E2648", {"start": v(15.15, 2.48) * mm, "end": v(15.1, 2.48) * mm});
            skLineSegment(sketch, "E2649", {"start": v(15.1, 2.48) * mm, "end": v(15.05, 2.48) * mm});
            skLineSegment(sketch, "E2650", {"start": v(15.05, 2.48) * mm, "end": v(15, 2.48) * mm});
            skLineSegment(sketch, "E2651", {"start": v(15, 2.48) * mm, "end": v(14.95, 2.48) * mm});
            skLineSegment(sketch, "E2652", {"start": v(14.95, 2.48) * mm, "end": v(14.9, 2.48) * mm});
            skLineSegment(sketch, "E2653", {"start": v(14.9, 2.48) * mm, "end": v(14.85, 2.48) * mm});
            skLineSegment(sketch, "E2654", {"start": v(14.85, 2.48) * mm, "end": v(14.8, 2.48) * mm});
            skLineSegment(sketch, "E2655", {"start": v(14.8, 2.48) * mm, "end": v(14.75, 2.48) * mm});
            skLineSegment(sketch, "E2656", {"start": v(14.75, 2.48) * mm, "end": v(14.7, 2.48) * mm});
            skLineSegment(sketch, "E2657", {"start": v(14.7, 2.48) * mm, "end": v(14.65, 2.48) * mm});
            skLineSegment(sketch, "E2658", {"start": v(14.65, 2.48) * mm, "end": v(14.6, 2.48) * mm});
            skLineSegment(sketch, "E2659", {"start": v(14.6, 2.48) * mm, "end": v(14.55, 2.48) * mm});
            skLineSegment(sketch, "E2660", {"start": v(14.55, 2.48) * mm, "end": v(14.5, 2.48) * mm});
            skLineSegment(sketch, "E2661", {"start": v(14.5, 2.48) * mm, "end": v(14.45, 2.48) * mm});
            skLineSegment(sketch, "E2662", {"start": v(14.45, 2.48) * mm, "end": v(14.4, 2.48) * mm});
            skLineSegment(sketch, "E2663", {"start": v(14.4, 2.48) * mm, "end": v(14.35, 2.48) * mm});
            skLineSegment(sketch, "E2664", {"start": v(14.35, 2.48) * mm, "end": v(14.3, 2.48) * mm});
            skLineSegment(sketch, "E2665", {"start": v(14.3, 2.48) * mm, "end": v(14.25, 2.48) * mm});
            skLineSegment(sketch, "E2666", {"start": v(14.25, 2.48) * mm, "end": v(14.2, 2.48) * mm});
            skLineSegment(sketch, "E2667", {"start": v(14.2, 2.48) * mm, "end": v(14.15, 2.48) * mm});
            skLineSegment(sketch, "E2668", {"start": v(14.15, 2.48) * mm, "end": v(14.1, 2.48) * mm});
            skLineSegment(sketch, "E2669", {"start": v(14.1, 2.48) * mm, "end": v(14.05, 2.48) * mm});
            skLineSegment(sketch, "E2670", {"start": v(14.05, 2.48) * mm, "end": v(14, 2.48) * mm});
            skLineSegment(sketch, "E2671", {"start": v(14, 2.48) * mm, "end": v(13.95, 2.48) * mm});
            skLineSegment(sketch, "E2672", {"start": v(13.95, 2.48) * mm, "end": v(13.9, 2.48) * mm});
            skLineSegment(sketch, "E2673", {"start": v(13.9, 2.48) * mm, "end": v(13.85, 2.48) * mm});
            skLineSegment(sketch, "E2674", {"start": v(13.85, 2.48) * mm, "end": v(13.8, 2.48) * mm});
            skLineSegment(sketch, "E2675", {"start": v(13.8, 2.48) * mm, "end": v(13.75, 2.48) * mm});
            skLineSegment(sketch, "E2676", {"start": v(13.75, 2.48) * mm, "end": v(13.7, 2.48) * mm});
            skLineSegment(sketch, "E2677", {"start": v(13.7, 2.48) * mm, "end": v(13.65, 2.48) * mm});
            skLineSegment(sketch, "E2678", {"start": v(13.65, 2.48) * mm, "end": v(13.6, 2.48) * mm});
            skLineSegment(sketch, "E2679", {"start": v(13.6, 2.48) * mm, "end": v(13.55, 2.48) * mm});
            skLineSegment(sketch, "E2680", {"start": v(13.55, 2.48) * mm, "end": v(13.5, 2.48) * mm});
            skLineSegment(sketch, "E2681", {"start": v(13.5, 2.48) * mm, "end": v(13.45, 2.48) * mm});
            skLineSegment(sketch, "E2682", {"start": v(13.45, 2.48) * mm, "end": v(13.4, 2.48) * mm});
            skLineSegment(sketch, "E2683", {"start": v(13.4, 2.48) * mm, "end": v(13.35, 2.48) * mm});
            skLineSegment(sketch, "E2684", {"start": v(13.35, 2.48) * mm, "end": v(13.3, 2.48) * mm});
            skLineSegment(sketch, "E2685", {"start": v(13.3, 2.48) * mm, "end": v(13.25, 2.48) * mm});
            skLineSegment(sketch, "E2686", {"start": v(13.25, 2.48) * mm, "end": v(13.2, 2.48) * mm});
            skLineSegment(sketch, "E2687", {"start": v(13.2, 2.48) * mm, "end": v(13.15, 2.48) * mm});
            skLineSegment(sketch, "E2688", {"start": v(13.15, 2.48) * mm, "end": v(13.1, 2.48) * mm});
            skLineSegment(sketch, "E2689", {"start": v(13.1, 2.48) * mm, "end": v(13.05, 2.48) * mm});
            skLineSegment(sketch, "E2690", {"start": v(13.05, 2.48) * mm, "end": v(13, 2.48) * mm});
            skLineSegment(sketch, "E2691", {"start": v(13, 2.48) * mm, "end": v(12.95, 2.48) * mm});
            skLineSegment(sketch, "E2692", {"start": v(12.95, 2.48) * mm, "end": v(12.9, 2.48) * mm});
            skLineSegment(sketch, "E2693", {"start": v(12.9, 2.48) * mm, "end": v(12.85, 2.48) * mm});
            skLineSegment(sketch, "E2694", {"start": v(12.85, 2.48) * mm, "end": v(12.8, 2.48) * mm});
            skLineSegment(sketch, "E2695", {"start": v(12.8, 2.48) * mm, "end": v(12.75, 2.48) * mm});
            skLineSegment(sketch, "E2696", {"start": v(12.75, 2.48) * mm, "end": v(12.7, 2.48) * mm});
            skLineSegment(sketch, "E2697", {"start": v(12.7, 2.48) * mm, "end": v(12.65, 2.48) * mm});
            skLineSegment(sketch, "E2698", {"start": v(12.65, 2.48) * mm, "end": v(12.6, 2.48) * mm});
            skLineSegment(sketch, "E2699", {"start": v(12.6, 2.48) * mm, "end": v(12.55, 2.48) * mm});
            skLineSegment(sketch, "E2700", {"start": v(12.55, 2.48) * mm, "end": v(12.5, 2.48) * mm});
            skLineSegment(sketch, "E2701", {"start": v(12.5, 2.48) * mm, "end": v(12.45, 2.48) * mm});
            skLineSegment(sketch, "E2702", {"start": v(12.45, 2.48) * mm, "end": v(12.4, 2.48) * mm});
            skLineSegment(sketch, "E2703", {"start": v(12.4, 2.48) * mm, "end": v(12.35, 2.48) * mm});
            skLineSegment(sketch, "E2704", {"start": v(12.35, 2.48) * mm, "end": v(12.3, 2.48) * mm});
            skLineSegment(sketch, "E2705", {"start": v(12.3, 2.48) * mm, "end": v(12.25, 2.48) * mm});
            skLineSegment(sketch, "E2706", {"start": v(12.25, 2.48) * mm, "end": v(12.2, 2.48) * mm});
            skLineSegment(sketch, "E2707", {"start": v(12.2, 2.48) * mm, "end": v(12.15, 2.48) * mm});
            skLineSegment(sketch, "E2708", {"start": v(12.15, 2.48) * mm, "end": v(12.1, 2.48) * mm});
            skLineSegment(sketch, "E2709", {"start": v(12.1, 2.48) * mm, "end": v(12.05, 2.48) * mm});
            skLineSegment(sketch, "E2710", {"start": v(12.05, 2.48) * mm, "end": v(12, 2.48) * mm});
            skLineSegment(sketch, "E2711", {"start": v(12, 2.48) * mm, "end": v(11.95, 2.48) * mm});
            skLineSegment(sketch, "E2712", {"start": v(11.95, 2.48) * mm, "end": v(11.9, 2.48) * mm});
            skLineSegment(sketch, "E2713", {"start": v(11.9, 2.48) * mm, "end": v(11.85, 2.48) * mm});
            skLineSegment(sketch, "E2714", {"start": v(11.85, 2.48) * mm, "end": v(11.8, 2.48) * mm});
            skLineSegment(sketch, "E2715", {"start": v(11.8, 2.48) * mm, "end": v(11.75, 2.48) * mm});
            skLineSegment(sketch, "E2716", {"start": v(11.75, 2.48) * mm, "end": v(11.7, 2.48) * mm});
            skLineSegment(sketch, "E2717", {"start": v(11.7, 2.48) * mm, "end": v(11.65, 2.48) * mm});
            skLineSegment(sketch, "E2718", {"start": v(11.65, 2.48) * mm, "end": v(11.6, 2.48) * mm});
            skLineSegment(sketch, "E2719", {"start": v(11.6, 2.48) * mm, "end": v(11.55, 2.48) * mm});
            skLineSegment(sketch, "E2720", {"start": v(11.55, 2.48) * mm, "end": v(11.5, 2.48) * mm});
            skLineSegment(sketch, "E2721", {"start": v(11.5, 2.48) * mm, "end": v(11.45, 2.48) * mm});
            skLineSegment(sketch, "E2722", {"start": v(11.45, 2.48) * mm, "end": v(11.4, 2.48) * mm});
            skLineSegment(sketch, "E2723", {"start": v(11.4, 2.48) * mm, "end": v(11.35, 2.48) * mm});
            skLineSegment(sketch, "E2724", {"start": v(11.35, 2.48) * mm, "end": v(11.3, 2.48) * mm});
            skLineSegment(sketch, "E2725", {"start": v(11.3, 2.48) * mm, "end": v(11.25, 2.48) * mm});
            skLineSegment(sketch, "E2726", {"start": v(11.25, 2.48) * mm, "end": v(11.2, 2.48) * mm});
            skLineSegment(sketch, "E2727", {"start": v(11.2, 2.48) * mm, "end": v(11.15, 2.48) * mm});
            skLineSegment(sketch, "E2728", {"start": v(11.15, 2.48) * mm, "end": v(11.1, 2.48) * mm});
            skLineSegment(sketch, "E2729", {"start": v(11.1, 2.48) * mm, "end": v(11.05, 2.48) * mm});
            skLineSegment(sketch, "E2730", {"start": v(11.05, 2.48) * mm, "end": v(11, 2.48) * mm});
            skLineSegment(sketch, "E2731", {"start": v(11, 2.48) * mm, "end": v(10.95, 2.48) * mm});
            skLineSegment(sketch, "E2732", {"start": v(10.95, 2.48) * mm, "end": v(10.9, 2.48) * mm});
            skLineSegment(sketch, "E2733", {"start": v(10.9, 2.48) * mm, "end": v(10.85, 2.48) * mm});
            skLineSegment(sketch, "E2734", {"start": v(10.85, 2.48) * mm, "end": v(10.8, 2.48) * mm});
            skLineSegment(sketch, "E2735", {"start": v(10.8, 2.48) * mm, "end": v(10.75, 2.48) * mm});
            skLineSegment(sketch, "E2736", {"start": v(10.75, 2.48) * mm, "end": v(10.7, 2.48) * mm});
            skLineSegment(sketch, "E2737", {"start": v(10.7, 2.48) * mm, "end": v(10.65, 2.48) * mm});
            skLineSegment(sketch, "E2738", {"start": v(10.65, 2.48) * mm, "end": v(10.6, 2.48) * mm});
            skLineSegment(sketch, "E2739", {"start": v(10.6, 2.48) * mm, "end": v(10.55, 2.48) * mm});
            skLineSegment(sketch, "E2740", {"start": v(10.55, 2.48) * mm, "end": v(10.5, 2.48) * mm});
            skLineSegment(sketch, "E2741", {"start": v(10.5, 2.48) * mm, "end": v(10.45, 2.48) * mm});
            skLineSegment(sketch, "E2742", {"start": v(10.45, 2.48) * mm, "end": v(10.4, 2.48) * mm});
            skLineSegment(sketch, "E2743", {"start": v(10.4, 2.48) * mm, "end": v(10.35, 2.48) * mm});
            skLineSegment(sketch, "E2744", {"start": v(10.35, 2.48) * mm, "end": v(10.3, 2.48) * mm});
            skLineSegment(sketch, "E2745", {"start": v(10.3, 2.48) * mm, "end": v(10.25, 2.48) * mm});
            skLineSegment(sketch, "E2746", {"start": v(10.25, 2.48) * mm, "end": v(10.2, 2.48) * mm});
            skLineSegment(sketch, "E2747", {"start": v(10.2, 2.48) * mm, "end": v(10.15, 2.48) * mm});
            skLineSegment(sketch, "E2748", {"start": v(10.15, 2.48) * mm, "end": v(10.1, 2.48) * mm});
            skLineSegment(sketch, "E2749", {"start": v(10.1, 2.48) * mm, "end": v(10.05, 2.48) * mm});
            skLineSegment(sketch, "E2750", {"start": v(10.05, 2.48) * mm, "end": v(10, 2.48) * mm});
            skLineSegment(sketch, "E2751", {"start": v(10, 2.48) * mm, "end": v(9.95, 2.48) * mm});
            skLineSegment(sketch, "E2752", {"start": v(9.95, 2.48) * mm, "end": v(9.9, 2.48) * mm});
            skLineSegment(sketch, "E2753", {"start": v(9.9, 2.48) * mm, "end": v(9.85, 2.48) * mm});
            skLineSegment(sketch, "E2754", {"start": v(9.85, 2.48) * mm, "end": v(9.8, 2.48) * mm});
            skLineSegment(sketch, "E2755", {"start": v(9.8, 2.48) * mm, "end": v(9.75, 2.48) * mm});
            skLineSegment(sketch, "E2756", {"start": v(9.75, 2.48) * mm, "end": v(9.7, 2.48) * mm});
            skLineSegment(sketch, "E2757", {"start": v(9.7, 2.48) * mm, "end": v(9.65, 2.48) * mm});
            skLineSegment(sketch, "E2758", {"start": v(9.65, 2.48) * mm, "end": v(9.6, 2.48) * mm});
            skLineSegment(sketch, "E2759", {"start": v(9.6, 2.48) * mm, "end": v(9.55, 2.48) * mm});
            skLineSegment(sketch, "E2760", {"start": v(9.55, 2.48) * mm, "end": v(9.5, 2.48) * mm});
            skLineSegment(sketch, "E2761", {"start": v(9.5, 2.48) * mm, "end": v(9.45, 2.48) * mm});
            skLineSegment(sketch, "E2762", {"start": v(9.45, 2.48) * mm, "end": v(9.4, 2.48) * mm});
            skLineSegment(sketch, "E2763", {"start": v(9.4, 2.48) * mm, "end": v(9.35, 2.48) * mm});
            skLineSegment(sketch, "E2764", {"start": v(9.35, 2.48) * mm, "end": v(9.3, 2.48) * mm});
            skLineSegment(sketch, "E2765", {"start": v(9.3, 2.48) * mm, "end": v(9.25, 2.48) * mm});
            skLineSegment(sketch, "E2766", {"start": v(9.25, 2.48) * mm, "end": v(9.2, 2.48) * mm});
            skLineSegment(sketch, "E2767", {"start": v(9.2, 2.48) * mm, "end": v(9.15, 2.48) * mm});
            skLineSegment(sketch, "E2768", {"start": v(9.15, 2.48) * mm, "end": v(9.1, 2.48) * mm});
            skLineSegment(sketch, "E2769", {"start": v(9.1, 2.48) * mm, "end": v(9.05, 2.48) * mm});
            skLineSegment(sketch, "E2770", {"start": v(9.05, 2.48) * mm, "end": v(9, 2.48) * mm});
            skLineSegment(sketch, "E2771", {"start": v(9, 2.48) * mm, "end": v(8.95, 2.48) * mm});
            skLineSegment(sketch, "E2772", {"start": v(8.95, 2.48) * mm, "end": v(8.9, 2.48) * mm});
            skLineSegment(sketch, "E2773", {"start": v(8.9, 2.48) * mm, "end": v(8.85, 2.48) * mm});
            skLineSegment(sketch, "E2774", {"start": v(8.85, 2.48) * mm, "end": v(8.8, 2.48) * mm});
            skLineSegment(sketch, "E2775", {"start": v(8.8, 2.48) * mm, "end": v(8.75, 2.48) * mm});
            skLineSegment(sketch, "E2776", {"start": v(8.75, 2.48) * mm, "end": v(8.7, 2.48) * mm});
            skLineSegment(sketch, "E2777", {"start": v(8.7, 2.48) * mm, "end": v(8.65, 2.48) * mm});
            skLineSegment(sketch, "E2778", {"start": v(8.65, 2.48) * mm, "end": v(8.6, 2.48) * mm});
            skLineSegment(sketch, "E2779", {"start": v(8.6, 2.48) * mm, "end": v(8.55, 2.48) * mm});
            skLineSegment(sketch, "E2780", {"start": v(8.55, 2.48) * mm, "end": v(8.5, 2.48) * mm});
            skLineSegment(sketch, "E2781", {"start": v(8.5, 2.48) * mm, "end": v(8.45, 2.48) * mm});
            skLineSegment(sketch, "E2782", {"start": v(8.45, 2.48) * mm, "end": v(8.4, 2.48) * mm});
            skLineSegment(sketch, "E2783", {"start": v(8.4, 2.48) * mm, "end": v(8.35, 2.48) * mm});
            skLineSegment(sketch, "E2784", {"start": v(8.35, 2.48) * mm, "end": v(8.3, 2.48) * mm});
            skLineSegment(sketch, "E2785", {"start": v(8.3, 2.48) * mm, "end": v(8.25, 2.48) * mm});
            skLineSegment(sketch, "E2786", {"start": v(8.25, 2.48) * mm, "end": v(8.2, 2.48) * mm});
            skLineSegment(sketch, "E2787", {"start": v(8.2, 2.48) * mm, "end": v(8.15, 2.48) * mm});
            skLineSegment(sketch, "E2788", {"start": v(8.15, 2.48) * mm, "end": v(8.1, 2.48) * mm});
            skLineSegment(sketch, "E2789", {"start": v(8.1, 2.48) * mm, "end": v(8.05, 2.48) * mm});
            skLineSegment(sketch, "E2790", {"start": v(8.05, 2.48) * mm, "end": v(8, 2.48) * mm});
            skLineSegment(sketch, "E2791", {"start": v(8, 2.48) * mm, "end": v(7.95, 2.48) * mm});
            skLineSegment(sketch, "E2792", {"start": v(7.95, 2.48) * mm, "end": v(7.9, 2.48) * mm});
            skLineSegment(sketch, "E2793", {"start": v(7.9, 2.48) * mm, "end": v(7.85, 2.48) * mm});
            skLineSegment(sketch, "E2794", {"start": v(7.85, 2.48) * mm, "end": v(7.8, 2.48) * mm});
            skLineSegment(sketch, "E2795", {"start": v(7.8, 2.48) * mm, "end": v(7.75, 2.48) * mm});
            skLineSegment(sketch, "E2796", {"start": v(7.75, 2.48) * mm, "end": v(7.7, 2.48) * mm});
            skLineSegment(sketch, "E2797", {"start": v(7.7, 2.48) * mm, "end": v(7.65, 2.48) * mm});
            skLineSegment(sketch, "E2798", {"start": v(7.65, 2.48) * mm, "end": v(7.6, 2.48) * mm});
            skLineSegment(sketch, "E2799", {"start": v(7.6, 2.48) * mm, "end": v(7.55, 2.48) * mm});
            skLineSegment(sketch, "E2800", {"start": v(7.55, 2.48) * mm, "end": v(7.5, 2.48) * mm});
            skLineSegment(sketch, "E2801", {"start": v(7.5, 2.48) * mm, "end": v(7.45, 2.48) * mm});
            skLineSegment(sketch, "E2802", {"start": v(7.45, 2.48) * mm, "end": v(7.4, 2.48) * mm});
            skLineSegment(sketch, "E2803", {"start": v(7.4, 2.48) * mm, "end": v(7.35, 2.48) * mm});
            skLineSegment(sketch, "E2804", {"start": v(7.35, 2.48) * mm, "end": v(7.3, 2.48) * mm});
            skLineSegment(sketch, "E2805", {"start": v(7.3, 2.48) * mm, "end": v(7.25, 2.48) * mm});
            skLineSegment(sketch, "E2806", {"start": v(7.25, 2.48) * mm, "end": v(7.2, 2.48) * mm});
            skLineSegment(sketch, "E2807", {"start": v(7.2, 2.48) * mm, "end": v(7.15, 2.48) * mm});
            skLineSegment(sketch, "E2808", {"start": v(7.15, 2.48) * mm, "end": v(7.1, 2.48) * mm});
            skLineSegment(sketch, "E2809", {"start": v(7.1, 2.48) * mm, "end": v(7.05, 2.48) * mm});
            skLineSegment(sketch, "E2810", {"start": v(7.05, 2.48) * mm, "end": v(7, 2.48) * mm});
            skLineSegment(sketch, "E2811", {"start": v(7, 2.48) * mm, "end": v(6.95, 2.48) * mm});
            skLineSegment(sketch, "E2812", {"start": v(6.95, 2.48) * mm, "end": v(6.9, 2.48) * mm});
            skLineSegment(sketch, "E2813", {"start": v(6.9, 2.48) * mm, "end": v(6.85, 2.48) * mm});
            skLineSegment(sketch, "E2814", {"start": v(6.85, 2.48) * mm, "end": v(6.8, 2.48) * mm});
            skLineSegment(sketch, "E2815", {"start": v(6.8, 2.48) * mm, "end": v(6.75, 2.48) * mm});
            skLineSegment(sketch, "E2816", {"start": v(6.75, 2.48) * mm, "end": v(6.7, 2.48) * mm});
            skLineSegment(sketch, "E2817", {"start": v(6.7, 2.48) * mm, "end": v(6.65, 2.48) * mm});
            skLineSegment(sketch, "E2818", {"start": v(6.65, 2.48) * mm, "end": v(6.6, 2.48) * mm});
            skLineSegment(sketch, "E2819", {"start": v(6.6, 2.48) * mm, "end": v(6.55, 2.48) * mm});
            skLineSegment(sketch, "E2820", {"start": v(6.55, 2.48) * mm, "end": v(6.5, 2.48) * mm});
            skLineSegment(sketch, "E2821", {"start": v(6.5, 2.48) * mm, "end": v(6.45, 2.48) * mm});
            skLineSegment(sketch, "E2822", {"start": v(6.45, 2.48) * mm, "end": v(6.4, 2.48) * mm});
            skLineSegment(sketch, "E2823", {"start": v(6.4, 2.48) * mm, "end": v(6.35, 2.48) * mm});
            skLineSegment(sketch, "E2824", {"start": v(6.35, 2.48) * mm, "end": v(6.3, 2.48) * mm});
            skLineSegment(sketch, "E2825", {"start": v(6.3, 2.48) * mm, "end": v(6.25, 2.48) * mm});
            skLineSegment(sketch, "E2826", {"start": v(6.25, 2.48) * mm, "end": v(6.2, 2.48) * mm});
            skLineSegment(sketch, "E2827", {"start": v(6.2, 2.48) * mm, "end": v(6.15, 2.48) * mm});
            skLineSegment(sketch, "E2828", {"start": v(6.15, 2.48) * mm, "end": v(6.1, 2.48) * mm});
            skLineSegment(sketch, "E2829", {"start": v(6.1, 2.48) * mm, "end": v(6.05, 2.48) * mm});
            skLineSegment(sketch, "E2830", {"start": v(6.05, 2.48) * mm, "end": v(6, 2.48) * mm});
            skLineSegment(sketch, "E2831", {"start": v(6, 2.48) * mm, "end": v(5.95, 2.48) * mm});
            skLineSegment(sketch, "E2832", {"start": v(5.95, 2.48) * mm, "end": v(5.9, 2.48) * mm});
            skLineSegment(sketch, "E2833", {"start": v(5.9, 2.48) * mm, "end": v(5.85, 2.48) * mm});
            skLineSegment(sketch, "E2834", {"start": v(5.85, 2.48) * mm, "end": v(5.8, 2.48) * mm});
            skLineSegment(sketch, "E2835", {"start": v(5.8, 2.48) * mm, "end": v(5.75, 2.48) * mm});
            skLineSegment(sketch, "E2836", {"start": v(5.75, 2.48) * mm, "end": v(5.7, 2.48) * mm});
            skLineSegment(sketch, "E2837", {"start": v(5.7, 2.48) * mm, "end": v(5.65, 2.48) * mm});
            skLineSegment(sketch, "E2838", {"start": v(5.65, 2.48) * mm, "end": v(5.6, 2.48) * mm});
            skLineSegment(sketch, "E2839", {"start": v(5.6, 2.48) * mm, "end": v(5.55, 2.48) * mm});
            skLineSegment(sketch, "E2840", {"start": v(5.55, 2.48) * mm, "end": v(5.5, 2.48) * mm});
            skLineSegment(sketch, "E2841", {"start": v(5.5, 2.48) * mm, "end": v(5.45, 2.48) * mm});
            skLineSegment(sketch, "E2842", {"start": v(5.45, 2.48) * mm, "end": v(5.4, 2.48) * mm});
            skLineSegment(sketch, "E2843", {"start": v(5.4, 2.48) * mm, "end": v(5.35, 2.48) * mm});
            skLineSegment(sketch, "E2844", {"start": v(5.35, 2.48) * mm, "end": v(5.3, 2.48) * mm});
            skLineSegment(sketch, "E2845", {"start": v(5.3, 2.48) * mm, "end": v(5.25, 2.48) * mm});
            skLineSegment(sketch, "E2846", {"start": v(5.25, 2.48) * mm, "end": v(5.05, 2.48) * mm});
            skLineSegment(sketch, "E2847", {"start": v(5.05, 2.48) * mm, "end": v(5.05, 2.68) * mm});
            skLineSegment(sketch, "E2848", {"start": v(5.05, 2.68) * mm, "end": v(5.05, 2.73) * mm});
            skLineSegment(sketch, "E2849", {"start": v(5.05, 2.73) * mm, "end": v(5.05, 2.78) * mm});
            skLineSegment(sketch, "E2850", {"start": v(5.05, 2.78) * mm, "end": v(5.05, 2.83) * mm});
            skLineSegment(sketch, "E2851", {"start": v(5.05, 2.83) * mm, "end": v(5.05, 2.88) * mm});
            skLineSegment(sketch, "E2852", {"start": v(5.05, 2.88) * mm, "end": v(5.05, 2.93) * mm});
            skLineSegment(sketch, "E2853", {"start": v(5.05, 2.93) * mm, "end": v(5.05, 2.98) * mm});
            skLineSegment(sketch, "E2854", {"start": v(5.05, 2.98) * mm, "end": v(5.05, 3.03) * mm});
            skLineSegment(sketch, "E2855", {"start": v(5.05, 3.03) * mm, "end": v(5.05, 3.08) * mm});
            skLineSegment(sketch, "E2856", {"start": v(5.05, 3.08) * mm, "end": v(5.05, 3.12) * mm});
            skLineSegment(sketch, "E2857", {"start": v(5.05, 3.12) * mm, "end": v(5.05, 3.18) * mm});
            skLineSegment(sketch, "E2858", {"start": v(5.05, 3.18) * mm, "end": v(5.05, 3.23) * mm});
            skLineSegment(sketch, "E2859", {"start": v(5.05, 3.23) * mm, "end": v(5.05, 3.28) * mm});
            skLineSegment(sketch, "E2860", {"start": v(5.05, 3.28) * mm, "end": v(5.05, 3.33) * mm});
            skLineSegment(sketch, "E2861", {"start": v(5.05, 3.33) * mm, "end": v(5.05, 3.38) * mm});
            skLineSegment(sketch, "E2862", {"start": v(5.05, 3.38) * mm, "end": v(5.05, 3.43) * mm});
            skLineSegment(sketch, "E2863", {"start": v(5.05, 3.43) * mm, "end": v(5.05, 3.48) * mm});
            skLineSegment(sketch, "E2864", {"start": v(5.05, 3.48) * mm, "end": v(5.05, 3.53) * mm});
            skLineSegment(sketch, "E2865", {"start": v(5.05, 3.53) * mm, "end": v(5.05, 3.58) * mm});
            skLineSegment(sketch, "E2866", {"start": v(5.05, 3.58) * mm, "end": v(5.05, 3.62) * mm});
            skLineSegment(sketch, "E2867", {"start": v(5.05, 3.62) * mm, "end": v(5.05, 3.68) * mm});
            skLineSegment(sketch, "E2868", {"start": v(5.05, 3.68) * mm, "end": v(5.05, 3.73) * mm});
            skLineSegment(sketch, "E2869", {"start": v(5.05, 3.73) * mm, "end": v(5.05, 3.78) * mm});
            skLineSegment(sketch, "E2870", {"start": v(5.05, 3.78) * mm, "end": v(5.05, 3.83) * mm});
            skLineSegment(sketch, "E2871", {"start": v(5.05, 3.83) * mm, "end": v(5.05, 3.88) * mm});
            skLineSegment(sketch, "E2872", {"start": v(5.05, 3.88) * mm, "end": v(5.05, 3.93) * mm});
            skLineSegment(sketch, "E2873", {"start": v(5.05, 3.93) * mm, "end": v(5.05, 3.98) * mm});
            skLineSegment(sketch, "E2874", {"start": v(5.05, 3.98) * mm, "end": v(5.05, 4.03) * mm});
            skLineSegment(sketch, "E2875", {"start": v(5.05, 4.03) * mm, "end": v(5.05, 4.08) * mm});
            skLineSegment(sketch, "E2876", {"start": v(5.05, 4.08) * mm, "end": v(5.05, 4.12) * mm});
            skLineSegment(sketch, "E2877", {"start": v(5.05, 4.12) * mm, "end": v(5.05, 4.17) * mm});
            skLineSegment(sketch, "E2878", {"start": v(5.05, 4.17) * mm, "end": v(5.05, 4.22) * mm});
            skLineSegment(sketch, "E2879", {"start": v(5.05, 4.22) * mm, "end": v(5.05, 4.28) * mm});
            skLineSegment(sketch, "E2880", {"start": v(5.05, 4.28) * mm, "end": v(5.05, 4.33) * mm});
            skLineSegment(sketch, "E2881", {"start": v(5.05, 4.33) * mm, "end": v(5.05, 4.38) * mm});
            skLineSegment(sketch, "E2882", {"start": v(5.05, 4.38) * mm, "end": v(5.05, 4.42) * mm});
            skLineSegment(sketch, "E2883", {"start": v(5.05, 4.42) * mm, "end": v(5.05, 4.48) * mm});
            skLineSegment(sketch, "E2884", {"start": v(5.05, 4.48) * mm, "end": v(5.05, 4.53) * mm});
            skLineSegment(sketch, "E2885", {"start": v(5.05, 4.53) * mm, "end": v(5.05, 4.58) * mm});
            skLineSegment(sketch, "E2886", {"start": v(5.05, 4.58) * mm, "end": v(5.05, 4.63) * mm});
            skLineSegment(sketch, "E2887", {"start": v(5.05, 4.63) * mm, "end": v(5.05, 4.68) * mm});
            skLineSegment(sketch, "E2888", {"start": v(5.05, 4.68) * mm, "end": v(5.05, 4.73) * mm});
            skLineSegment(sketch, "E2889", {"start": v(5.05, 4.73) * mm, "end": v(5.05, 4.78) * mm});
            skLineSegment(sketch, "E2890", {"start": v(5.05, 4.78) * mm, "end": v(5.05, 4.83) * mm});
            skLineSegment(sketch, "E2891", {"start": v(5.05, 4.83) * mm, "end": v(5.05, 4.88) * mm});
            skLineSegment(sketch, "E2892", {"start": v(5.05, 4.88) * mm, "end": v(5.05, 4.92) * mm});
            skLineSegment(sketch, "E2893", {"start": v(5.05, 4.92) * mm, "end": v(5.05, 4.98) * mm});
            skLineSegment(sketch, "E2894", {"start": v(5.05, 4.98) * mm, "end": v(5.05, 5.03) * mm});
            skLineSegment(sketch, "E2895", {"start": v(5.05, 5.03) * mm, "end": v(5.05, 5.38) * mm});
            skLineSegment(sketch, "E2896", {"start": v(5.05, 5.38) * mm, "end": v(4.85, 5.38) * mm});
            skLineSegment(sketch, "E2897", {"start": v(4.85, 5.38) * mm, "end": v(4.8, 5.38) * mm});
            skLineSegment(sketch, "E2898", {"start": v(4.8, 5.38) * mm, "end": v(4.75, 5.38) * mm});
            skLineSegment(sketch, "E2899", {"start": v(4.75, 5.38) * mm, "end": v(4.7, 5.38) * mm});
            skLineSegment(sketch, "E2900", {"start": v(4.7, 5.38) * mm, "end": v(4.65, 5.38) * mm});
            skLineSegment(sketch, "E2901", {"start": v(4.65, 5.38) * mm, "end": v(4.6, 5.38) * mm});
            skLineSegment(sketch, "E2902", {"start": v(4.6, 5.38) * mm, "end": v(4.55, 5.38) * mm});
            skLineSegment(sketch, "E2903", {"start": v(4.55, 5.38) * mm, "end": v(4.5, 5.38) * mm});
            skLineSegment(sketch, "E2904", {"start": v(4.5, 5.38) * mm, "end": v(4.45, 5.38) * mm});
            skLineSegment(sketch, "E2905", {"start": v(4.45, 5.38) * mm, "end": v(4.4, 5.38) * mm});
            skLineSegment(sketch, "E2906", {"start": v(4.4, 5.38) * mm, "end": v(4.35, 5.38) * mm});
            skLineSegment(sketch, "E2907", {"start": v(4.35, 5.38) * mm, "end": v(4.3, 5.38) * mm});
            skLineSegment(sketch, "E2908", {"start": v(4.3, 5.38) * mm, "end": v(4.25, 5.38) * mm});
            skLineSegment(sketch, "E2909", {"start": v(4.25, 5.38) * mm, "end": v(4.2, 5.38) * mm});
            skLineSegment(sketch, "E2910", {"start": v(4.2, 5.38) * mm, "end": v(4.15, 5.38) * mm});
            skLineSegment(sketch, "E2911", {"start": v(4.15, 5.38) * mm, "end": v(4.1, 5.38) * mm});
            skLineSegment(sketch, "E2912", {"start": v(4.1, 5.38) * mm, "end": v(4.05, 5.38) * mm});
            skLineSegment(sketch, "E2913", {"start": v(4.05, 5.38) * mm, "end": v(4, 5.38) * mm});
            skLineSegment(sketch, "E2914", {"start": v(4, 5.38) * mm, "end": v(3.95, 5.38) * mm});
            skLineSegment(sketch, "E2915", {"start": v(3.95, 5.38) * mm, "end": v(3.9, 5.38) * mm});
            skLineSegment(sketch, "E2916", {"start": v(3.9, 5.38) * mm, "end": v(3.85, 5.38) * mm});
            skLineSegment(sketch, "E2917", {"start": v(3.85, 5.38) * mm, "end": v(3.8, 5.38) * mm});
            skLineSegment(sketch, "E2918", {"start": v(3.8, 5.38) * mm, "end": v(3.75, 5.38) * mm});
            skLineSegment(sketch, "E2919", {"start": v(3.75, 5.38) * mm, "end": v(3.7, 5.38) * mm});
            skLineSegment(sketch, "E2920", {"start": v(3.7, 5.38) * mm, "end": v(3.65, 5.38) * mm});
            skLineSegment(sketch, "E2921", {"start": v(3.65, 5.38) * mm, "end": v(3.6, 5.38) * mm});
            skLineSegment(sketch, "E2922", {"start": v(3.6, 5.38) * mm, "end": v(3.55, 5.38) * mm});
            skLineSegment(sketch, "E2923", {"start": v(3.55, 5.38) * mm, "end": v(3.5, 5.38) * mm});
            skLineSegment(sketch, "E2924", {"start": v(3.5, 5.38) * mm, "end": v(3.45, 5.38) * mm});
            skLineSegment(sketch, "E2925", {"start": v(3.45, 5.38) * mm, "end": v(3.4, 5.38) * mm});
            skLineSegment(sketch, "E2926", {"start": v(3.4, 5.38) * mm, "end": v(3.35, 5.38) * mm});
            skLineSegment(sketch, "E2927", {"start": v(3.35, 5.38) * mm, "end": v(3.3, 5.38) * mm});
            skLineSegment(sketch, "E2928", {"start": v(3.3, 5.38) * mm, "end": v(3.25, 5.38) * mm});
            skLineSegment(sketch, "E2929", {"start": v(3.25, 5.38) * mm, "end": v(3.2, 5.38) * mm});
            skLineSegment(sketch, "E2930", {"start": v(3.2, 5.38) * mm, "end": v(3.15, 5.38) * mm});
            skLineSegment(sketch, "E2931", {"start": v(3.15, 5.38) * mm, "end": v(3.1, 5.38) * mm});
            skLineSegment(sketch, "E2932", {"start": v(3.1, 5.38) * mm, "end": v(3.05, 5.38) * mm});
            skLineSegment(sketch, "E2933", {"start": v(3.05, 5.38) * mm, "end": v(3, 5.38) * mm});
            skLineSegment(sketch, "E2934", {"start": v(3, 5.38) * mm, "end": v(2.95, 5.38) * mm});
            skLineSegment(sketch, "E2935", {"start": v(2.95, 5.38) * mm, "end": v(2.9, 5.38) * mm});
            skLineSegment(sketch, "E2936", {"start": v(2.9, 5.38) * mm, "end": v(2.85, 5.38) * mm});
            skLineSegment(sketch, "E2937", {"start": v(2.85, 5.38) * mm, "end": v(2.8, 5.38) * mm});
            skLineSegment(sketch, "E2938", {"start": v(2.8, 5.38) * mm, "end": v(2.75, 5.38) * mm});
            skLineSegment(sketch, "E2939", {"start": v(2.75, 5.38) * mm, "end": v(2.7, 5.38) * mm});
            skLineSegment(sketch, "E2940", {"start": v(2.7, 5.38) * mm, "end": v(2.65, 5.38) * mm});
            skLineSegment(sketch, "E2941", {"start": v(2.65, 5.38) * mm, "end": v(2.6, 5.38) * mm});
            skLineSegment(sketch, "E2942", {"start": v(2.6, 5.38) * mm, "end": v(2.55, 5.38) * mm});
            skLineSegment(sketch, "E2943", {"start": v(2.55, 5.38) * mm, "end": v(2.5, 5.38) * mm});
            skLineSegment(sketch, "E2944", {"start": v(2.5, 5.38) * mm, "end": v(2.45, 5.38) * mm});
            skLineSegment(sketch, "E2945", {"start": v(2.45, 5.38) * mm, "end": v(2.4, 5.38) * mm});
            skLineSegment(sketch, "E2946", {"start": v(2.4, 5.38) * mm, "end": v(2.35, 5.38) * mm});
            skLineSegment(sketch, "E2947", {"start": v(2.35, 5.38) * mm, "end": v(2.3, 5.38) * mm});
            skLineSegment(sketch, "E2948", {"start": v(2.3, 5.38) * mm, "end": v(2.25, 5.38) * mm});
            skLineSegment(sketch, "E2949", {"start": v(2.25, 5.38) * mm, "end": v(2.2, 5.38) * mm});
            skLineSegment(sketch, "E2950", {"start": v(2.2, 5.38) * mm, "end": v(2.15, 5.38) * mm});
            skLineSegment(sketch, "E2951", {"start": v(2.15, 5.38) * mm, "end": v(2.1, 5.38) * mm});
            skLineSegment(sketch, "E2952", {"start": v(2.1, 5.38) * mm, "end": v(2.05, 5.38) * mm});
            skLineSegment(sketch, "E2953", {"start": v(2.05, 5.38) * mm, "end": v(2, 5.38) * mm});
            skLineSegment(sketch, "E2954", {"start": v(2, 5.38) * mm, "end": v(1.95, 5.38) * mm});
            skLineSegment(sketch, "E2955", {"start": v(1.95, 5.38) * mm, "end": v(1.9, 5.38) * mm});
            skLineSegment(sketch, "E2956", {"start": v(1.9, 5.38) * mm, "end": v(1.85, 5.38) * mm});
            skLineSegment(sketch, "E2957", {"start": v(1.85, 5.38) * mm, "end": v(1.8, 5.38) * mm});
            skLineSegment(sketch, "E2958", {"start": v(1.8, 5.38) * mm, "end": v(1.75, 5.38) * mm});
            skLineSegment(sketch, "E2959", {"start": v(1.75, 5.38) * mm, "end": v(1.7, 5.38) * mm});
            skLineSegment(sketch, "E2960", {"start": v(1.7, 5.38) * mm, "end": v(1.65, 5.38) * mm});
            skLineSegment(sketch, "E2961", {"start": v(1.65, 5.38) * mm, "end": v(1.6, 5.38) * mm});
            skLineSegment(sketch, "E2962", {"start": v(1.6, 5.38) * mm, "end": v(1.55, 5.38) * mm});
            skLineSegment(sketch, "E2963", {"start": v(1.55, 5.38) * mm, "end": v(1.5, 5.38) * mm});
            skLineSegment(sketch, "E2964", {"start": v(1.5, 5.38) * mm, "end": v(1.45, 5.38) * mm});
            skLineSegment(sketch, "E2965", {"start": v(1.45, 5.38) * mm, "end": v(1.4, 5.38) * mm});
            skLineSegment(sketch, "E2966", {"start": v(1.4, 5.38) * mm, "end": v(1.35, 5.38) * mm});
            skLineSegment(sketch, "E2967", {"start": v(1.35, 5.38) * mm, "end": v(1.3, 5.38) * mm});
            skLineSegment(sketch, "E2968", {"start": v(1.3, 5.38) * mm, "end": v(1.25, 5.38) * mm});
            skLineSegment(sketch, "E2969", {"start": v(1.25, 5.38) * mm, "end": v(1.2, 5.38) * mm});
            skLineSegment(sketch, "E2970", {"start": v(1.2, 5.38) * mm, "end": v(1.15, 5.38) * mm});
            skLineSegment(sketch, "E2971", {"start": v(1.15, 5.38) * mm, "end": v(1.1, 5.38) * mm});
            skLineSegment(sketch, "E2972", {"start": v(1.1, 5.38) * mm, "end": v(1.05, 5.38) * mm});
            skLineSegment(sketch, "E2973", {"start": v(1.05, 5.38) * mm, "end": v(1, 5.38) * mm});
            skLineSegment(sketch, "E2974", {"start": v(1, 5.38) * mm, "end": v(0.95, 5.38) * mm});
            skLineSegment(sketch, "E2975", {"start": v(0.95, 5.38) * mm, "end": v(0.9, 5.38) * mm});
            skLineSegment(sketch, "E2976", {"start": v(0.9, 5.38) * mm, "end": v(0.85, 5.38) * mm});
            skLineSegment(sketch, "E2977", {"start": v(0.85, 5.38) * mm, "end": v(0.8, 5.38) * mm});
            skLineSegment(sketch, "E2978", {"start": v(0.8, 5.38) * mm, "end": v(0.75, 5.38) * mm});
            skLineSegment(sketch, "E2979", {"start": v(0.75, 5.38) * mm, "end": v(0.7, 5.38) * mm});
            skLineSegment(sketch, "E2980", {"start": v(0.7, 5.38) * mm, "end": v(0.65, 5.38) * mm});
            skLineSegment(sketch, "E2981", {"start": v(0.65, 5.38) * mm, "end": v(0.6, 5.38) * mm});
            skLineSegment(sketch, "E2982", {"start": v(0.6, 5.38) * mm, "end": v(0.55, 5.38) * mm});
            skLineSegment(sketch, "E2983", {"start": v(0.55, 5.38) * mm, "end": v(0.5, 5.38) * mm});
            skLineSegment(sketch, "E2984", {"start": v(0.5, 5.38) * mm, "end": v(0.45, 5.38) * mm});
            skLineSegment(sketch, "E2985", {"start": v(0.45, 5.38) * mm, "end": v(0.4, 5.38) * mm});
            skLineSegment(sketch, "E2986", {"start": v(0.4, 5.38) * mm, "end": v(0.35, 5.38) * mm});
            skLineSegment(sketch, "E2987", {"start": v(0.35, 5.38) * mm, "end": v(0.3, 5.38) * mm});
            skLineSegment(sketch, "E2988", {"start": v(0.3, 5.38) * mm, "end": v(0.25, 5.38) * mm});
            skLineSegment(sketch, "E2989", {"start": v(0.25, 5.38) * mm, "end": v(0.2, 5.38) * mm});
            skLineSegment(sketch, "E2990", {"start": v(0.2, 5.38) * mm, "end": v(0.15, 5.38) * mm});
            skLineSegment(sketch, "E2991", {"start": v(0.15, 5.38) * mm, "end": v(0.1, 5.38) * mm});
            skLineSegment(sketch, "E2992", {"start": v(0.1, 5.38) * mm, "end": v(0.05, 5.38) * mm});
            skLineSegment(sketch, "E2993", {"start": v(0.05, 5.38) * mm, "end": v(0, 5.38) * mm});
            skLineSegment(sketch, "E2994", {"start": v(0, 5.38) * mm, "end": v(-0.05, 5.38) * mm});
            skLineSegment(sketch, "E2995", {"start": v(-0.05, 5.38) * mm, "end": v(-0.1, 5.38) * mm});
            skLineSegment(sketch, "E2996", {"start": v(-0.1, 5.38) * mm, "end": v(-0.15, 5.38) * mm});
            skLineSegment(sketch, "E2997", {"start": v(-0.15, 5.38) * mm, "end": v(-0.2, 5.38) * mm});
            skLineSegment(sketch, "E2998", {"start": v(-0.2, 5.38) * mm, "end": v(-0.25, 5.38) * mm});
            skLineSegment(sketch, "E2999", {"start": v(-0.25, 5.38) * mm, "end": v(-0.3, 5.38) * mm});
            skLineSegment(sketch, "E3000", {"start": v(-0.3, 5.38) * mm, "end": v(-0.35, 5.38) * mm});
            skLineSegment(sketch, "E3001", {"start": v(-0.35, 5.38) * mm, "end": v(-0.4, 5.38) * mm});
            skLineSegment(sketch, "E3002", {"start": v(-0.4, 5.38) * mm, "end": v(-0.45, 5.38) * mm});
            skLineSegment(sketch, "E3003", {"start": v(-0.45, 5.38) * mm, "end": v(-0.5, 5.38) * mm});
            skLineSegment(sketch, "E3004", {"start": v(-0.5, 5.38) * mm, "end": v(-0.55, 5.38) * mm});
            skLineSegment(sketch, "E3005", {"start": v(-0.55, 5.38) * mm, "end": v(-0.6, 5.38) * mm});
            skLineSegment(sketch, "E3006", {"start": v(-0.6, 5.38) * mm, "end": v(-0.65, 5.38) * mm});
            skLineSegment(sketch, "E3007", {"start": v(-0.65, 5.38) * mm, "end": v(-0.7, 5.38) * mm});
            skLineSegment(sketch, "E3008", {"start": v(-0.7, 5.38) * mm, "end": v(-0.75, 5.38) * mm});
            skLineSegment(sketch, "E3009", {"start": v(-0.75, 5.38) * mm, "end": v(-0.8, 5.38) * mm});
            skLineSegment(sketch, "E3010", {"start": v(-0.8, 5.38) * mm, "end": v(-0.85, 5.38) * mm});
            skLineSegment(sketch, "E3011", {"start": v(-0.85, 5.38) * mm, "end": v(-0.9, 5.38) * mm});
            skLineSegment(sketch, "E3012", {"start": v(-0.9, 5.38) * mm, "end": v(-0.95, 5.38) * mm});
            skLineSegment(sketch, "E3013", {"start": v(-0.95, 5.38) * mm, "end": v(-1, 5.38) * mm});
            skLineSegment(sketch, "E3014", {"start": v(-1, 5.38) * mm, "end": v(-1.05, 5.38) * mm});
            skLineSegment(sketch, "E3015", {"start": v(-1.05, 5.38) * mm, "end": v(-1.1, 5.38) * mm});
            skLineSegment(sketch, "E3016", {"start": v(-1.1, 5.38) * mm, "end": v(-1.15, 5.38) * mm});
            skLineSegment(sketch, "E3017", {"start": v(-1.15, 5.38) * mm, "end": v(-1.2, 5.38) * mm});
            skLineSegment(sketch, "E3018", {"start": v(-1.2, 5.38) * mm, "end": v(-1.25, 5.38) * mm});
            skLineSegment(sketch, "E3019", {"start": v(-1.25, 5.38) * mm, "end": v(-1.3, 5.38) * mm});
            skLineSegment(sketch, "E3020", {"start": v(-1.3, 5.38) * mm, "end": v(-1.35, 5.38) * mm});
            skLineSegment(sketch, "E3021", {"start": v(-1.35, 5.38) * mm, "end": v(-1.4, 5.38) * mm});
            skLineSegment(sketch, "E3022", {"start": v(-1.4, 5.38) * mm, "end": v(-1.45, 5.38) * mm});
            skLineSegment(sketch, "E3023", {"start": v(-1.45, 5.38) * mm, "end": v(-1.5, 5.38) * mm});
            skLineSegment(sketch, "E3024", {"start": v(-1.5, 5.38) * mm, "end": v(-1.55, 5.38) * mm});
            skLineSegment(sketch, "E3025", {"start": v(-1.55, 5.38) * mm, "end": v(-1.6, 5.38) * mm});
            skLineSegment(sketch, "E3026", {"start": v(-1.6, 5.38) * mm, "end": v(-1.65, 5.38) * mm});
            skLineSegment(sketch, "E3027", {"start": v(-1.65, 5.38) * mm, "end": v(-1.7, 5.38) * mm});
            skLineSegment(sketch, "E3028", {"start": v(-1.7, 5.38) * mm, "end": v(-1.75, 5.38) * mm});
            skLineSegment(sketch, "E3029", {"start": v(-1.75, 5.38) * mm, "end": v(-1.8, 5.38) * mm});
            skLineSegment(sketch, "E3030", {"start": v(-1.8, 5.38) * mm, "end": v(-1.85, 5.38) * mm});
            skLineSegment(sketch, "E3031", {"start": v(-1.85, 5.38) * mm, "end": v(-1.9, 5.38) * mm});
            skLineSegment(sketch, "E3032", {"start": v(-1.9, 5.38) * mm, "end": v(-1.95, 5.38) * mm});
            skLineSegment(sketch, "E3033", {"start": v(-1.95, 5.38) * mm, "end": v(-2, 5.38) * mm});
            skLineSegment(sketch, "E3034", {"start": v(-2, 5.38) * mm, "end": v(-2.05, 5.38) * mm});
            skLineSegment(sketch, "E3035", {"start": v(-2.05, 5.38) * mm, "end": v(-2.1, 5.38) * mm});
            skLineSegment(sketch, "E3036", {"start": v(-2.1, 5.38) * mm, "end": v(-2.15, 5.38) * mm});
            skLineSegment(sketch, "E3037", {"start": v(-2.15, 5.38) * mm, "end": v(-2.2, 5.38) * mm});
            skLineSegment(sketch, "E3038", {"start": v(-2.2, 5.38) * mm, "end": v(-2.25, 5.38) * mm});
            skLineSegment(sketch, "E3039", {"start": v(-2.25, 5.38) * mm, "end": v(-2.3, 5.38) * mm});
            skLineSegment(sketch, "E3040", {"start": v(-2.3, 5.38) * mm, "end": v(-2.35, 5.38) * mm});
            skLineSegment(sketch, "E3041", {"start": v(-2.35, 5.38) * mm, "end": v(-2.4, 5.38) * mm});
            skLineSegment(sketch, "E3042", {"start": v(-2.4, 5.38) * mm, "end": v(-2.45, 5.38) * mm});
            skLineSegment(sketch, "E3043", {"start": v(-2.45, 5.38) * mm, "end": v(-2.5, 5.38) * mm});
            skLineSegment(sketch, "E3044", {"start": v(-2.5, 5.38) * mm, "end": v(-2.55, 5.38) * mm});
            skLineSegment(sketch, "E3045", {"start": v(-2.55, 5.38) * mm, "end": v(-2.6, 5.38) * mm});
            skLineSegment(sketch, "E3046", {"start": v(-2.6, 5.38) * mm, "end": v(-2.65, 5.38) * mm});
            skLineSegment(sketch, "E3047", {"start": v(-2.65, 5.38) * mm, "end": v(-2.7, 5.38) * mm});
            skLineSegment(sketch, "E3048", {"start": v(-2.7, 5.38) * mm, "end": v(-2.75, 5.38) * mm});
            skLineSegment(sketch, "E3049", {"start": v(-2.75, 5.38) * mm, "end": v(-2.8, 5.38) * mm});
            skLineSegment(sketch, "E3050", {"start": v(-2.8, 5.38) * mm, "end": v(-2.85, 5.38) * mm});
            skLineSegment(sketch, "E3051", {"start": v(-2.85, 5.38) * mm, "end": v(-2.9, 5.38) * mm});
            skLineSegment(sketch, "E3052", {"start": v(-2.9, 5.38) * mm, "end": v(-2.95, 5.38) * mm});
            skLineSegment(sketch, "E3053", {"start": v(-2.95, 5.38) * mm, "end": v(-3, 5.38) * mm});
            skLineSegment(sketch, "E3054", {"start": v(-3, 5.38) * mm, "end": v(-3.05, 5.38) * mm});
            skLineSegment(sketch, "E3055", {"start": v(-3.05, 5.38) * mm, "end": v(-3.1, 5.38) * mm});
            skLineSegment(sketch, "E3056", {"start": v(-3.1, 5.38) * mm, "end": v(-3.15, 5.38) * mm});
            skLineSegment(sketch, "E3057", {"start": v(-3.15, 5.38) * mm, "end": v(-3.2, 5.38) * mm});
            skLineSegment(sketch, "E3058", {"start": v(-3.2, 5.38) * mm, "end": v(-3.25, 5.38) * mm});
            skLineSegment(sketch, "E3059", {"start": v(-3.25, 5.38) * mm, "end": v(-3.3, 5.38) * mm});
            skLineSegment(sketch, "E3060", {"start": v(-3.3, 5.38) * mm, "end": v(-3.35, 5.38) * mm});
            skLineSegment(sketch, "E3061", {"start": v(-3.35, 5.38) * mm, "end": v(-3.4, 5.38) * mm});
            skLineSegment(sketch, "E3062", {"start": v(-3.4, 5.38) * mm, "end": v(-3.45, 5.38) * mm});
            skLineSegment(sketch, "E3063", {"start": v(-3.45, 5.38) * mm, "end": v(-3.5, 5.38) * mm});
            skLineSegment(sketch, "E3064", {"start": v(-3.5, 5.38) * mm, "end": v(-3.55, 5.38) * mm});
            skLineSegment(sketch, "E3065", {"start": v(-3.55, 5.38) * mm, "end": v(-3.6, 5.38) * mm});
            skLineSegment(sketch, "E3066", {"start": v(-3.6, 5.38) * mm, "end": v(-3.65, 5.38) * mm});
            skLineSegment(sketch, "E3067", {"start": v(-3.65, 5.38) * mm, "end": v(-3.7, 5.38) * mm});
            skLineSegment(sketch, "E3068", {"start": v(-3.7, 5.38) * mm, "end": v(-3.75, 5.38) * mm});
            skLineSegment(sketch, "E3069", {"start": v(-3.75, 5.38) * mm, "end": v(-3.8, 5.38) * mm});
            skLineSegment(sketch, "E3070", {"start": v(-3.8, 5.38) * mm, "end": v(-3.85, 5.38) * mm});
            skLineSegment(sketch, "E3071", {"start": v(-3.85, 5.38) * mm, "end": v(-3.9, 5.38) * mm});
            skLineSegment(sketch, "E3072", {"start": v(-3.9, 5.38) * mm, "end": v(-3.95, 5.38) * mm});
            skLineSegment(sketch, "E3073", {"start": v(-3.95, 5.38) * mm, "end": v(-4, 5.38) * mm});
            skLineSegment(sketch, "E3074", {"start": v(-4, 5.38) * mm, "end": v(-4.05, 5.38) * mm});
            skLineSegment(sketch, "E3075", {"start": v(-4.05, 5.38) * mm, "end": v(-4.1, 5.38) * mm});
            skLineSegment(sketch, "E3076", {"start": v(-4.1, 5.38) * mm, "end": v(-4.15, 5.38) * mm});
            skLineSegment(sketch, "E3077", {"start": v(-4.15, 5.38) * mm, "end": v(-4.2, 5.38) * mm});
            skLineSegment(sketch, "E3078", {"start": v(-4.2, 5.38) * mm, "end": v(-4.25, 5.38) * mm});
            skLineSegment(sketch, "E3079", {"start": v(-4.25, 5.38) * mm, "end": v(-4.3, 5.38) * mm});
            skLineSegment(sketch, "E3080", {"start": v(-4.3, 5.38) * mm, "end": v(-4.35, 5.38) * mm});
            skLineSegment(sketch, "E3081", {"start": v(-4.35, 5.38) * mm, "end": v(-4.4, 5.38) * mm});
            skLineSegment(sketch, "E3082", {"start": v(-4.4, 5.38) * mm, "end": v(-4.45, 5.38) * mm});
            skLineSegment(sketch, "E3083", {"start": v(-4.45, 5.38) * mm, "end": v(-4.5, 5.38) * mm});
            skLineSegment(sketch, "E3084", {"start": v(-4.5, 5.38) * mm, "end": v(-4.55, 5.38) * mm});
            skLineSegment(sketch, "E3085", {"start": v(-4.55, 5.38) * mm, "end": v(-4.6, 5.38) * mm});
            skLineSegment(sketch, "E3086", {"start": v(-4.6, 5.38) * mm, "end": v(-4.65, 5.38) * mm});
            skLineSegment(sketch, "E3087", {"start": v(-4.65, 5.38) * mm, "end": v(-4.7, 5.38) * mm});
            skLineSegment(sketch, "E3088", {"start": v(-4.7, 5.38) * mm, "end": v(-4.95, 5.38) * mm});
            skSolve(sketch);
        }
        {
            var Q0;
            Q0 = qSketchRegion(id + "F3", true);
            extrude(context, id + "F4", {"entities" : qUnion([Q0]), "operationType" : NewBodyOperationType.ADD, "depth" : .5 * mm, "offsetDistance" : 25 * mm});
        }
        {
            var Q0;
            Q0=makeQuery(id+"F1.opRevolve","SWEPT_EDGE",EDGE,{"disambiguationData":[OSD([sQuery(id+"F0.wireOp",EDGE,"E1.top"),sQuery(id+"F0.wireOp",EDGE,"E1.left")])]});
            fillet(context, id + "F5", {"entities" : qUnion([Q0]), "radius" : .25 * mm, "tangentPropagation" : true, "allowEdgeOverflow" : false});
        }
        {
            var Q0;
            Q0=makeQuery(id+"F1.opRevolve","SWEPT_EDGE",EDGE,{"disambiguationData":[OSD([sQuery(id+"F0.wireOp",EDGE,"E1.top"),sQuery(id+"F0.wireOp",EDGE,"E1.right")])]});
            fillet(context, id + "F6", {"entities" : qUnion([Q0]), "radius" : .25 * mm, "tangentPropagation" : true, "allowEdgeOverflow" : false});
        }
    });
